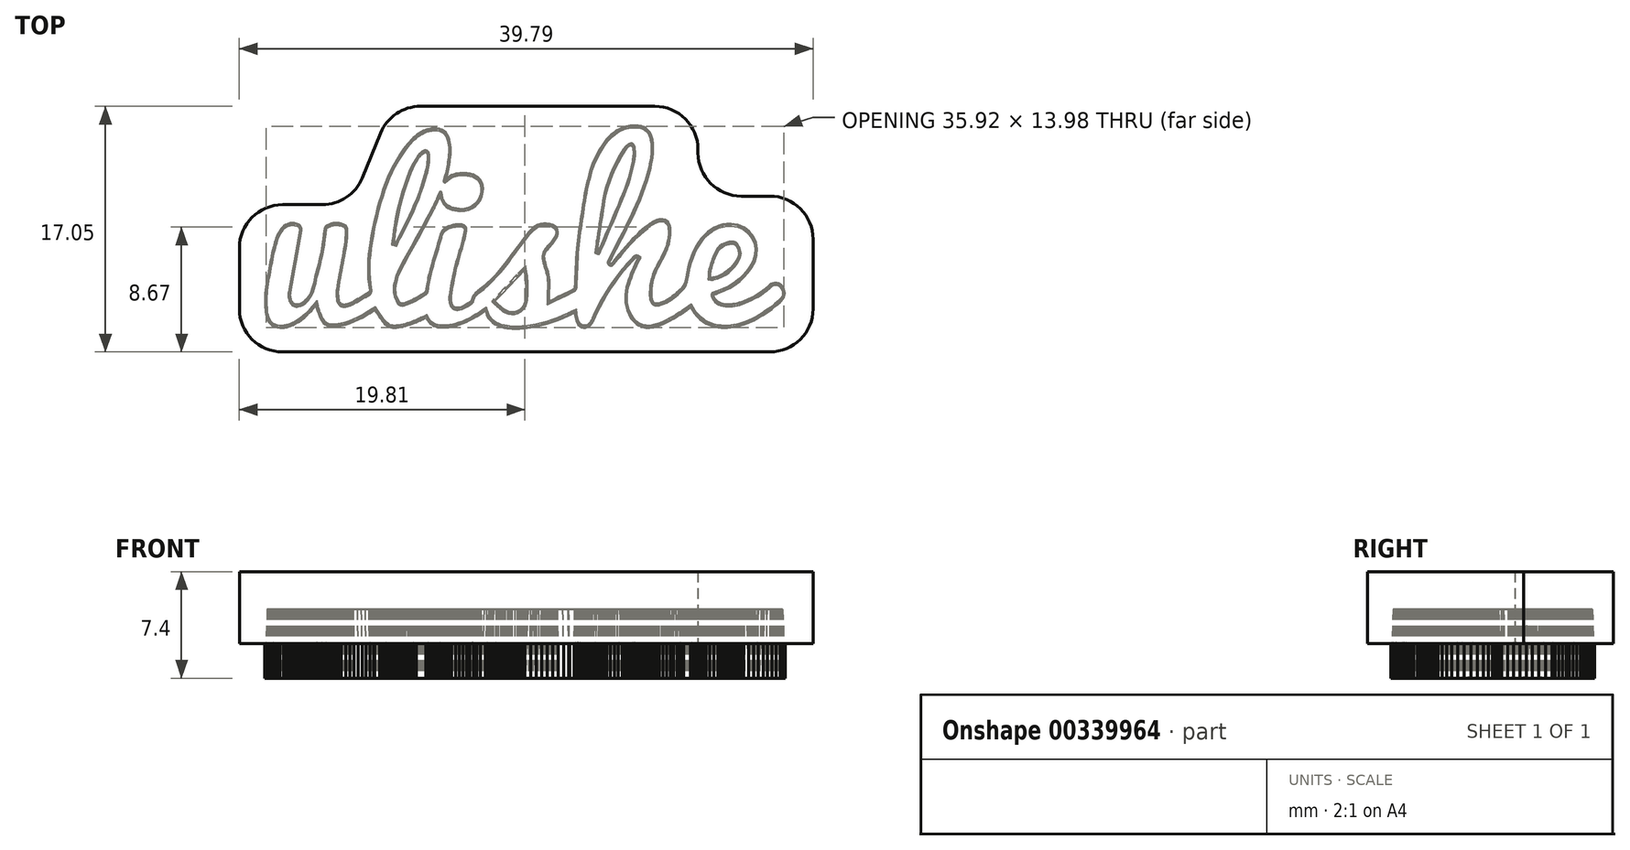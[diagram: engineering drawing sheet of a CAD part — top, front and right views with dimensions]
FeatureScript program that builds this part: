
annotation { "Feature Type Name" : "Feature", "Feature Type Description" : "" }
export const myFeature = defineFeature(function(context is Context, id is Id, definition is map)
    precondition{}
    {
        {
            var Q0;
            Q0=qCreatedBy(makeId("Top.planeOp"),FACE);
            var sketch = newSketch(context, id + "F0", { "sketchPlane" : qUnion([Q0])});
            skLineSegment(sketch, "E0", {"start": v(148.2, -33.5) * mm, "end": v(147.47, -32.9) * mm});
            skLineSegment(sketch, "E1", {"start": v(147.47, -32.9) * mm, "end": v(146.65, -32.48) * mm});
            skLineSegment(sketch, "E2", {"start": v(146.65, -32.48) * mm, "end": v(145.8, -32.22) * mm});
            skLineSegment(sketch, "E3", {"start": v(145.8, -32.22) * mm, "end": v(144.9, -32.13) * mm});
            skLineSegment(sketch, "E4", {"start": v(144.9, -32.13) * mm, "end": v(144, -32.2) * mm});
            skLineSegment(sketch, "E5", {"start": v(144, -32.2) * mm, "end": v(143.13, -32.42) * mm});
            skLineSegment(sketch, "E6", {"start": v(143.13, -32.42) * mm, "end": v(142.3, -32.82) * mm});
            skLineSegment(sketch, "E7", {"start": v(142.3, -32.82) * mm, "end": v(141.55, -33.38) * mm});
            skLineSegment(sketch, "E8", {"start": v(141.55, -33.38) * mm, "end": v(141.41, -33.5) * mm});
            skLineSegment(sketch, "E9", {"start": v(141.41, -33.5) * mm, "end": v(141.29, -33.62) * mm});
            skLineSegment(sketch, "E10", {"start": v(141.29, -33.62) * mm, "end": v(141.17, -33.73) * mm});
            skLineSegment(sketch, "E11", {"start": v(141.17, -33.73) * mm, "end": v(141.07, -33.82) * mm});
            skLineSegment(sketch, "E12", {"start": v(141.07, -33.82) * mm, "end": v(140.98, -33.9) * mm});
            skLineSegment(sketch, "E13", {"start": v(140.98, -33.9) * mm, "end": v(140.91, -33.96) * mm});
            skLineSegment(sketch, "E14", {"start": v(140.91, -33.96) * mm, "end": v(140.86, -34) * mm});
            skLineSegment(sketch, "E15", {"start": v(140.86, -34) * mm, "end": v(140.83, -34.04) * mm});
            skLineSegment(sketch, "E16", {"start": v(140.83, -34.04) * mm, "end": v(138.94, -35.65) * mm});
            skLineSegment(sketch, "E17", {"start": v(138.94, -35.65) * mm, "end": v(137.24, -37) * mm});
            skLineSegment(sketch, "E18", {"start": v(137.24, -37) * mm, "end": v(135.64, -38.16) * mm});
            skLineSegment(sketch, "E19", {"start": v(135.64, -38.16) * mm, "end": v(134.07, -39.16) * mm});
            skLineSegment(sketch, "E20", {"start": v(134.07, -39.16) * mm, "end": v(132.43, -40.06) * mm});
            skLineSegment(sketch, "E21", {"start": v(132.43, -40.06) * mm, "end": v(130.66, -40.94) * mm});
            skLineSegment(sketch, "E22", {"start": v(130.66, -40.94) * mm, "end": v(128.66, -41.83) * mm});
            skLineSegment(sketch, "E23", {"start": v(128.66, -41.83) * mm, "end": v(126.37, -42.8) * mm});
            skLineSegment(sketch, "E24", {"start": v(126.37, -42.8) * mm, "end": v(125.09, -43.3) * mm});
            skLineSegment(sketch, "E25", {"start": v(125.09, -43.3) * mm, "end": v(123.8, -43.72) * mm});
            skLineSegment(sketch, "E26", {"start": v(123.8, -43.72) * mm, "end": v(122.52, -44.05) * mm});
            skLineSegment(sketch, "E27", {"start": v(122.52, -44.05) * mm, "end": v(121.22, -44.3) * mm});
            skLineSegment(sketch, "E28", {"start": v(121.22, -44.3) * mm, "end": v(119.9, -44.5) * mm});
            skLineSegment(sketch, "E29", {"start": v(119.9, -44.5) * mm, "end": v(118.57, -44.6) * mm});
            skLineSegment(sketch, "E30", {"start": v(118.57, -44.6) * mm, "end": v(117.21, -44.64) * mm});
            skLineSegment(sketch, "E31", {"start": v(117.21, -44.64) * mm, "end": v(115.82, -44.6) * mm});
            skLineSegment(sketch, "E32", {"start": v(115.82, -44.6) * mm, "end": v(114.69, -44.46) * mm});
            skLineSegment(sketch, "E33", {"start": v(114.69, -44.46) * mm, "end": v(113.6, -44.14) * mm});
            skLineSegment(sketch, "E34", {"start": v(113.6, -44.14) * mm, "end": v(112.57, -43.66) * mm});
            skLineSegment(sketch, "E35", {"start": v(112.57, -43.66) * mm, "end": v(111.62, -43.03) * mm});
            skLineSegment(sketch, "E36", {"start": v(111.62, -43.03) * mm, "end": v(110.77, -42.27) * mm});
            skLineSegment(sketch, "E37", {"start": v(110.77, -42.27) * mm, "end": v(110.04, -41.4) * mm});
            skLineSegment(sketch, "E38", {"start": v(110.04, -41.4) * mm, "end": v(109.44, -40.41) * mm});
            skLineSegment(sketch, "E39", {"start": v(109.44, -40.41) * mm, "end": v(109, -39.34) * mm});
            skLineSegment(sketch, "E40", {"start": v(109, -39.34) * mm, "end": v(109, -39.33) * mm});
            skLineSegment(sketch, "E41", {"start": v(109, -39.33) * mm, "end": v(109, -39.31) * mm});
            skLineSegment(sketch, "E42", {"start": v(109, -39.31) * mm, "end": v(109.01, -39.3) * mm});
            skLineSegment(sketch, "E43", {"start": v(109.01, -39.3) * mm, "end": v(109.02, -39.28) * mm});
            skLineSegment(sketch, "E44", {"start": v(109.02, -39.28) * mm, "end": v(109.03, -39.27) * mm});
            skLineSegment(sketch, "E45", {"start": v(109.03, -39.27) * mm, "end": v(109.04, -39.25) * mm});
            skLineSegment(sketch, "E46", {"start": v(109.04, -39.25) * mm, "end": v(109.04, -39.24) * mm});
            skLineSegment(sketch, "E47", {"start": v(109.04, -39.24) * mm, "end": v(109.05, -39.22) * mm});
            skLineSegment(sketch, "E48", {"start": v(109.05, -39.22) * mm, "end": v(109.38, -39.11) * mm});
            skLineSegment(sketch, "E49", {"start": v(109.38, -39.11) * mm, "end": v(109.7, -39) * mm});
            skLineSegment(sketch, "E50", {"start": v(109.7, -39) * mm, "end": v(110.03, -38.9) * mm});
            skLineSegment(sketch, "E51", {"start": v(110.03, -38.9) * mm, "end": v(110.36, -38.8) * mm});
            skLineSegment(sketch, "E52", {"start": v(110.36, -38.8) * mm, "end": v(110.69, -38.7) * mm});
            skLineSegment(sketch, "E53", {"start": v(110.69, -38.7) * mm, "end": v(111.01, -38.58) * mm});
            skLineSegment(sketch, "E54", {"start": v(111.01, -38.58) * mm, "end": v(111.34, -38.47) * mm});
            skLineSegment(sketch, "E55", {"start": v(111.34, -38.47) * mm, "end": v(111.67, -38.36) * mm});
            skLineSegment(sketch, "E56", {"start": v(111.67, -38.36) * mm, "end": v(115.1, -37) * mm});
            skLineSegment(sketch, "E57", {"start": v(115.1, -37) * mm, "end": v(118.32, -35.42) * mm});
            skLineSegment(sketch, "E58", {"start": v(118.32, -35.42) * mm, "end": v(121.34, -33.6) * mm});
            skLineSegment(sketch, "E59", {"start": v(121.34, -33.6) * mm, "end": v(124.14, -31.51) * mm});
            skLineSegment(sketch, "E60", {"start": v(124.14, -31.51) * mm, "end": v(126.7, -29.16) * mm});
            skLineSegment(sketch, "E61", {"start": v(126.7, -29.16) * mm, "end": v(129.02, -26.51) * mm});
            skLineSegment(sketch, "E62", {"start": v(129.02, -26.51) * mm, "end": v(131.08, -23.57) * mm});
            skLineSegment(sketch, "E63", {"start": v(131.08, -23.57) * mm, "end": v(132.87, -20.3) * mm});
            skLineSegment(sketch, "E64", {"start": v(132.87, -20.3) * mm, "end": v(134.14, -16.46) * mm});
            skLineSegment(sketch, "E65", {"start": v(134.14, -16.46) * mm, "end": v(134.38, -12.6) * mm});
            skLineSegment(sketch, "E66", {"start": v(134.38, -12.6) * mm, "end": v(133.67, -8.87) * mm});
            skLineSegment(sketch, "E67", {"start": v(133.67, -8.87) * mm, "end": v(132.11, -5.45) * mm});
            skLineSegment(sketch, "E68", {"start": v(132.11, -5.45) * mm, "end": v(129.8, -2.48) * mm});
            skLineSegment(sketch, "E69", {"start": v(129.8, -2.48) * mm, "end": v(126.84, -0.14) * mm});
            skLineSegment(sketch, "E70", {"start": v(126.84, -0.14) * mm, "end": v(123.32, 1.42) * mm});
            skLineSegment(sketch, "E71", {"start": v(123.32, 1.42) * mm, "end": v(119.32, 2.03) * mm});
            skLineSegment(sketch, "E72", {"start": v(119.32, 2.03) * mm, "end": v(116.62, 1.93) * mm});
            skLineSegment(sketch, "E73", {"start": v(116.62, 1.93) * mm, "end": v(114.08, 1.53) * mm});
            skLineSegment(sketch, "E74", {"start": v(114.08, 1.53) * mm, "end": v(111.68, 0.84) * mm});
            skLineSegment(sketch, "E75", {"start": v(111.68, 0.84) * mm, "end": v(109.43, -0.14) * mm});
            skLineSegment(sketch, "E76", {"start": v(109.43, -0.14) * mm, "end": v(107.33, -1.39) * mm});
            skLineSegment(sketch, "E77", {"start": v(107.33, -1.39) * mm, "end": v(105.35, -2.9) * mm});
            skLineSegment(sketch, "E78", {"start": v(105.35, -2.9) * mm, "end": v(103.51, -4.65) * mm});
            skLineSegment(sketch, "E79", {"start": v(103.51, -4.65) * mm, "end": v(101.8, -6.64) * mm});
            skLineSegment(sketch, "E80", {"start": v(101.8, -6.64) * mm, "end": v(99.98, -9.17) * mm});
            skLineSegment(sketch, "E81", {"start": v(99.98, -9.17) * mm, "end": v(98.42, -11.8) * mm});
            skLineSegment(sketch, "E82", {"start": v(98.42, -11.8) * mm, "end": v(97.07, -14.53) * mm});
            skLineSegment(sketch, "E83", {"start": v(97.07, -14.53) * mm, "end": v(95.93, -17.34) * mm});
            skLineSegment(sketch, "E84", {"start": v(95.93, -17.34) * mm, "end": v(94.98, -20.22) * mm});
            skLineSegment(sketch, "E85", {"start": v(94.98, -20.22) * mm, "end": v(94.18, -23.16) * mm});
            skLineSegment(sketch, "E86", {"start": v(94.18, -23.16) * mm, "end": v(93.52, -26.14) * mm});
            skLineSegment(sketch, "E87", {"start": v(93.52, -26.14) * mm, "end": v(92.98, -29.16) * mm});
            skLineSegment(sketch, "E88", {"start": v(92.98, -29.16) * mm, "end": v(92.8, -30.2) * mm});
            skLineSegment(sketch, "E89", {"start": v(92.8, -30.2) * mm, "end": v(92.57, -31.2) * mm});
            skLineSegment(sketch, "E90", {"start": v(92.57, -31.2) * mm, "end": v(92.3, -32.14) * mm});
            skLineSegment(sketch, "E91", {"start": v(92.3, -32.14) * mm, "end": v(91.95, -33.04) * mm});
            skLineSegment(sketch, "E92", {"start": v(91.95, -33.04) * mm, "end": v(91.52, -33.88) * mm});
            skLineSegment(sketch, "E93", {"start": v(91.52, -33.88) * mm, "end": v(90.98, -34.66) * mm});
            skLineSegment(sketch, "E94", {"start": v(90.98, -34.66) * mm, "end": v(90.33, -35.4) * mm});
            skLineSegment(sketch, "E95", {"start": v(90.33, -35.4) * mm, "end": v(89.53, -36.07) * mm});
            skLineSegment(sketch, "E96", {"start": v(89.53, -36.07) * mm, "end": v(89.42, -36.17) * mm});
            skLineSegment(sketch, "E97", {"start": v(89.42, -36.17) * mm, "end": v(89.3, -36.27) * mm});
            skLineSegment(sketch, "E98", {"start": v(89.3, -36.27) * mm, "end": v(89.2, -36.37) * mm});
            skLineSegment(sketch, "E99", {"start": v(89.2, -36.37) * mm, "end": v(89.1, -36.48) * mm});
            skLineSegment(sketch, "E100", {"start": v(89.1, -36.48) * mm, "end": v(89, -36.59) * mm});
            skLineSegment(sketch, "E101", {"start": v(89, -36.59) * mm, "end": v(88.89, -36.7) * mm});
            skLineSegment(sketch, "E102", {"start": v(88.89, -36.7) * mm, "end": v(88.78, -36.8) * mm});
            skLineSegment(sketch, "E103", {"start": v(88.78, -36.8) * mm, "end": v(88.68, -36.91) * mm});
            skLineSegment(sketch, "E104", {"start": v(88.68, -36.91) * mm, "end": v(87.54, -37.97) * mm});
            skLineSegment(sketch, "E105", {"start": v(87.54, -37.97) * mm, "end": v(86.38, -39) * mm});
            skLineSegment(sketch, "E106", {"start": v(86.38, -39) * mm, "end": v(85.19, -39.96) * mm});
            skLineSegment(sketch, "E107", {"start": v(85.19, -39.96) * mm, "end": v(83.96, -40.88) * mm});
            skLineSegment(sketch, "E108", {"start": v(83.96, -40.88) * mm, "end": v(82.68, -41.72) * mm});
            skLineSegment(sketch, "E109", {"start": v(82.68, -41.72) * mm, "end": v(81.34, -42.48) * mm});
            skLineSegment(sketch, "E110", {"start": v(81.34, -42.48) * mm, "end": v(79.95, -43.15) * mm});
            skLineSegment(sketch, "E111", {"start": v(79.95, -43.15) * mm, "end": v(78.49, -43.7) * mm});
            skLineSegment(sketch, "E112", {"start": v(78.49, -43.7) * mm, "end": v(77.35, -44.02) * mm});
            skLineSegment(sketch, "E113", {"start": v(77.35, -44.02) * mm, "end": v(76.37, -44.13) * mm});
            skLineSegment(sketch, "E114", {"start": v(76.37, -44.13) * mm, "end": v(75.54, -44.03) * mm});
            skLineSegment(sketch, "E115", {"start": v(75.54, -44.03) * mm, "end": v(74.85, -43.72) * mm});
            skLineSegment(sketch, "E116", {"start": v(74.85, -43.72) * mm, "end": v(74.3, -43.2) * mm});
            skLineSegment(sketch, "E117", {"start": v(74.3, -43.2) * mm, "end": v(73.89, -42.47) * mm});
            skLineSegment(sketch, "E118", {"start": v(73.89, -42.47) * mm, "end": v(73.6, -41.52) * mm});
            skLineSegment(sketch, "E119", {"start": v(73.6, -41.52) * mm, "end": v(73.42, -40.34) * mm});
            skLineSegment(sketch, "E120", {"start": v(73.42, -40.34) * mm, "end": v(73.41, -40.3) * mm});
            skLineSegment(sketch, "E121", {"start": v(73.41, -40.3) * mm, "end": v(73.41, -40.25) * mm});
            skLineSegment(sketch, "E122", {"start": v(73.41, -40.25) * mm, "end": v(73.4, -40.2) * mm});
            skLineSegment(sketch, "E123", {"start": v(73.4, -40.2) * mm, "end": v(73.4, -40.16) * mm});
            skLineSegment(sketch, "E124", {"start": v(73.4, -40.16) * mm, "end": v(73.4, -40.12) * mm});
            skLineSegment(sketch, "E125", {"start": v(73.4, -40.12) * mm, "end": v(73.4, -40.07) * mm});
            skLineSegment(sketch, "E126", {"start": v(73.4, -40.07) * mm, "end": v(73.4, -40.03) * mm});
            skLineSegment(sketch, "E127", {"start": v(73.4, -40.03) * mm, "end": v(73.4, -39.98) * mm});
            skLineSegment(sketch, "E128", {"start": v(73.4, -39.98) * mm, "end": v(73.34, -37.9) * mm});
            skLineSegment(sketch, "E129", {"start": v(73.34, -37.9) * mm, "end": v(73.43, -35.85) * mm});
            skLineSegment(sketch, "E130", {"start": v(73.43, -35.85) * mm, "end": v(73.65, -33.82) * mm});
            skLineSegment(sketch, "E131", {"start": v(73.65, -33.82) * mm, "end": v(74, -31.82) * mm});
            skLineSegment(sketch, "E132", {"start": v(74, -31.82) * mm, "end": v(74.5, -29.85) * mm});
            skLineSegment(sketch, "E133", {"start": v(74.5, -29.85) * mm, "end": v(75.11, -27.9) * mm});
            skLineSegment(sketch, "E134", {"start": v(75.11, -27.9) * mm, "end": v(75.86, -26) * mm});
            skLineSegment(sketch, "E135", {"start": v(75.86, -26) * mm, "end": v(76.74, -24.11) * mm});
            skLineSegment(sketch, "E136", {"start": v(76.74, -24.11) * mm, "end": v(77.32, -22.98) * mm});
            skLineSegment(sketch, "E137", {"start": v(77.32, -22.98) * mm, "end": v(77.9, -21.85) * mm});
            skLineSegment(sketch, "E138", {"start": v(77.9, -21.85) * mm, "end": v(78.5, -20.72) * mm});
            skLineSegment(sketch, "E139", {"start": v(78.5, -20.72) * mm, "end": v(79.1, -19.6) * mm});
            skLineSegment(sketch, "E140", {"start": v(79.1, -19.6) * mm, "end": v(79.68, -18.47) * mm});
            skLineSegment(sketch, "E141", {"start": v(79.68, -18.47) * mm, "end": v(80.27, -17.34) * mm});
            skLineSegment(sketch, "E142", {"start": v(80.27, -17.34) * mm, "end": v(80.84, -16.2) * mm});
            skLineSegment(sketch, "E143", {"start": v(80.84, -16.2) * mm, "end": v(81.4, -15.06) * mm});
            skLineSegment(sketch, "E144", {"start": v(81.4, -15.06) * mm, "end": v(82.18, -13.33) * mm});
            skLineSegment(sketch, "E145", {"start": v(82.18, -13.33) * mm, "end": v(82.84, -11.58) * mm});
            skLineSegment(sketch, "E146", {"start": v(82.84, -11.58) * mm, "end": v(83.39, -9.8) * mm});
            skLineSegment(sketch, "E147", {"start": v(83.39, -9.8) * mm, "end": v(83.82, -8) * mm});
            skLineSegment(sketch, "E148", {"start": v(83.82, -8) * mm, "end": v(84.12, -6.16) * mm});
            skLineSegment(sketch, "E149", {"start": v(84.12, -6.16) * mm, "end": v(84.3, -4.31) * mm});
            skLineSegment(sketch, "E150", {"start": v(84.3, -4.31) * mm, "end": v(84.33, -2.44) * mm});
            skLineSegment(sketch, "E151", {"start": v(84.33, -2.44) * mm, "end": v(84.23, -0.53) * mm});
            skLineSegment(sketch, "E152", {"start": v(84.23, -0.53) * mm, "end": v(83.98, 0.8) * mm});
            skLineSegment(sketch, "E153", {"start": v(83.98, 0.8) * mm, "end": v(83.52, 1.97) * mm});
            skLineSegment(sketch, "E154", {"start": v(83.52, 1.97) * mm, "end": v(82.87, 2.95) * mm});
            skLineSegment(sketch, "E155", {"start": v(82.87, 2.95) * mm, "end": v(82.04, 3.72) * mm});
            skLineSegment(sketch, "E156", {"start": v(82.04, 3.72) * mm, "end": v(81.05, 4.27) * mm});
            skLineSegment(sketch, "E157", {"start": v(81.05, 4.27) * mm, "end": v(79.92, 4.6) * mm});
            skLineSegment(sketch, "E158", {"start": v(79.92, 4.6) * mm, "end": v(78.67, 4.67) * mm});
            skLineSegment(sketch, "E159", {"start": v(78.67, 4.67) * mm, "end": v(77.33, 4.5) * mm});
            skLineSegment(sketch, "E160", {"start": v(77.33, 4.5) * mm, "end": v(76.9, 4.38) * mm});
            skLineSegment(sketch, "E161", {"start": v(76.9, 4.38) * mm, "end": v(76.47, 4.26) * mm});
            skLineSegment(sketch, "E162", {"start": v(76.47, 4.26) * mm, "end": v(76.04, 4.12) * mm});
            skLineSegment(sketch, "E163", {"start": v(76.04, 4.12) * mm, "end": v(75.62, 3.96) * mm});
            skLineSegment(sketch, "E164", {"start": v(75.62, 3.96) * mm, "end": v(75.2, 3.8) * mm});
            skLineSegment(sketch, "E165", {"start": v(75.2, 3.8) * mm, "end": v(74.8, 3.6) * mm});
            skLineSegment(sketch, "E166", {"start": v(74.8, 3.6) * mm, "end": v(74.4, 3.4) * mm});
            skLineSegment(sketch, "E167", {"start": v(74.4, 3.4) * mm, "end": v(74, 3.2) * mm});
            skLineSegment(sketch, "E168", {"start": v(74, 3.2) * mm, "end": v(73.49, 2.89) * mm});
            skLineSegment(sketch, "E169", {"start": v(73.49, 2.89) * mm, "end": v(72.98, 2.57) * mm});
            skLineSegment(sketch, "E170", {"start": v(72.98, 2.57) * mm, "end": v(72.48, 2.24) * mm});
            skLineSegment(sketch, "E171", {"start": v(72.48, 2.24) * mm, "end": v(71.98, 1.9) * mm});
            skLineSegment(sketch, "E172", {"start": v(71.98, 1.9) * mm, "end": v(71.5, 1.56) * mm});
            skLineSegment(sketch, "E173", {"start": v(71.5, 1.56) * mm, "end": v(71.01, 1.2) * mm});
            skLineSegment(sketch, "E174", {"start": v(71.01, 1.2) * mm, "end": v(70.54, 0.83) * mm});
            skLineSegment(sketch, "E175", {"start": v(70.54, 0.83) * mm, "end": v(70.08, 0.45) * mm});
            skLineSegment(sketch, "E176", {"start": v(70.08, 0.45) * mm, "end": v(67.96, -1.36) * mm});
            skLineSegment(sketch, "E177", {"start": v(67.96, -1.36) * mm, "end": v(65.88, -3.23) * mm});
            skLineSegment(sketch, "E178", {"start": v(65.88, -3.23) * mm, "end": v(63.85, -5.14) * mm});
            skLineSegment(sketch, "E179", {"start": v(63.85, -5.14) * mm, "end": v(61.88, -7.1) * mm});
            skLineSegment(sketch, "E180", {"start": v(61.88, -7.1) * mm, "end": v(59.95, -9.11) * mm});
            skLineSegment(sketch, "E181", {"start": v(59.95, -9.11) * mm, "end": v(58.08, -11.18) * mm});
            skLineSegment(sketch, "E182", {"start": v(58.08, -11.18) * mm, "end": v(56.27, -13.3) * mm});
            skLineSegment(sketch, "E183", {"start": v(56.27, -13.3) * mm, "end": v(54.52, -15.47) * mm});
            skLineSegment(sketch, "E184", {"start": v(54.52, -15.47) * mm, "end": v(53.98, -16.15) * mm});
            skLineSegment(sketch, "E185", {"start": v(53.98, -16.15) * mm, "end": v(53.43, -16.82) * mm});
            skLineSegment(sketch, "E186", {"start": v(53.43, -16.82) * mm, "end": v(52.87, -17.49) * mm});
            skLineSegment(sketch, "E187", {"start": v(52.87, -17.49) * mm, "end": v(52.31, -18.16) * mm});
            skLineSegment(sketch, "E188", {"start": v(52.31, -18.16) * mm, "end": v(51.75, -18.83) * mm});
            skLineSegment(sketch, "E189", {"start": v(51.75, -18.83) * mm, "end": v(51.2, -19.5) * mm});
            skLineSegment(sketch, "E190", {"start": v(51.2, -19.5) * mm, "end": v(50.64, -20.2) * mm});
            skLineSegment(sketch, "E191", {"start": v(50.64, -20.2) * mm, "end": v(50.09, -20.89) * mm});
            skLineSegment(sketch, "E192", {"start": v(50.09, -20.89) * mm, "end": v(49.92, -21.02) * mm});
            skLineSegment(sketch, "E193", {"start": v(49.92, -21.02) * mm, "end": v(49.73, -21.07) * mm});
            skLineSegment(sketch, "E194", {"start": v(49.73, -21.07) * mm, "end": v(49.53, -21.03) * mm});
            skLineSegment(sketch, "E195", {"start": v(49.53, -21.03) * mm, "end": v(49.35, -20.94) * mm});
            skLineSegment(sketch, "E196", {"start": v(49.35, -20.94) * mm, "end": v(49.2, -20.79) * mm});
            skLineSegment(sketch, "E197", {"start": v(49.2, -20.79) * mm, "end": v(49.11, -20.6) * mm});
            skLineSegment(sketch, "E198", {"start": v(49.11, -20.6) * mm, "end": v(49.08, -20.39) * mm});
            skLineSegment(sketch, "E199", {"start": v(49.08, -20.39) * mm, "end": v(49.14, -20.16) * mm});
            skLineSegment(sketch, "E200", {"start": v(49.14, -20.16) * mm, "end": v(49.23, -19.99) * mm});
            skLineSegment(sketch, "E201", {"start": v(49.23, -19.99) * mm, "end": v(49.32, -19.82) * mm});
            skLineSegment(sketch, "E202", {"start": v(49.32, -19.82) * mm, "end": v(49.4, -19.66) * mm});
            skLineSegment(sketch, "E203", {"start": v(49.4, -19.66) * mm, "end": v(49.48, -19.5) * mm});
            skLineSegment(sketch, "E204", {"start": v(49.48, -19.5) * mm, "end": v(49.56, -19.36) * mm});
            skLineSegment(sketch, "E205", {"start": v(49.56, -19.36) * mm, "end": v(49.64, -19.21) * mm});
            skLineSegment(sketch, "E206", {"start": v(49.64, -19.21) * mm, "end": v(49.72, -19.06) * mm});
            skLineSegment(sketch, "E207", {"start": v(49.72, -19.06) * mm, "end": v(49.8, -18.92) * mm});
            skLineSegment(sketch, "E208", {"start": v(49.8, -18.92) * mm, "end": v(51.32, -15.92) * mm});
            skLineSegment(sketch, "E209", {"start": v(51.32, -15.92) * mm, "end": v(52.86, -12.92) * mm});
            skLineSegment(sketch, "E210", {"start": v(52.86, -12.92) * mm, "end": v(54.4, -9.92) * mm});
            skLineSegment(sketch, "E211", {"start": v(54.4, -9.92) * mm, "end": v(55.94, -6.92) * mm});
            skLineSegment(sketch, "E212", {"start": v(55.94, -6.92) * mm, "end": v(57.47, -3.92) * mm});
            skLineSegment(sketch, "E213", {"start": v(57.47, -3.92) * mm, "end": v(58.98, -0.91) * mm});
            skLineSegment(sketch, "E214", {"start": v(58.98, -0.91) * mm, "end": v(60.48, 2.1) * mm});
            skLineSegment(sketch, "E215", {"start": v(60.48, 2.1) * mm, "end": v(61.96, 5.13) * mm});
            skLineSegment(sketch, "E216", {"start": v(61.96, 5.13) * mm, "end": v(63.62, 8.65) * mm});
            skLineSegment(sketch, "E217", {"start": v(63.62, 8.65) * mm, "end": v(65.22, 12.2) * mm});
            skLineSegment(sketch, "E218", {"start": v(65.22, 12.2) * mm, "end": v(66.74, 15.79) * mm});
            skLineSegment(sketch, "E219", {"start": v(66.74, 15.79) * mm, "end": v(68.17, 19.4) * mm});
            skLineSegment(sketch, "E220", {"start": v(68.17, 19.4) * mm, "end": v(69.5, 23.05) * mm});
            skLineSegment(sketch, "E221", {"start": v(69.5, 23.05) * mm, "end": v(70.74, 26.74) * mm});
            skLineSegment(sketch, "E222", {"start": v(70.74, 26.74) * mm, "end": v(71.85, 30.47) * mm});
            skLineSegment(sketch, "E223", {"start": v(71.85, 30.47) * mm, "end": v(72.84, 34.25) * mm});
            skLineSegment(sketch, "E224", {"start": v(72.84, 34.25) * mm, "end": v(73.3, 36.28) * mm});
            skLineSegment(sketch, "E225", {"start": v(73.3, 36.28) * mm, "end": v(73.7, 38.3) * mm});
            skLineSegment(sketch, "E226", {"start": v(73.7, 38.3) * mm, "end": v(74, 40.35) * mm});
            skLineSegment(sketch, "E227", {"start": v(74, 40.35) * mm, "end": v(74.22, 42.39) * mm});
            skLineSegment(sketch, "E228", {"start": v(74.22, 42.39) * mm, "end": v(74.33, 44.44) * mm});
            skLineSegment(sketch, "E229", {"start": v(74.33, 44.44) * mm, "end": v(74.32, 46.5) * mm});
            skLineSegment(sketch, "E230", {"start": v(74.32, 46.5) * mm, "end": v(74.19, 48.56) * mm});
            skLineSegment(sketch, "E231", {"start": v(74.19, 48.56) * mm, "end": v(73.9, 50.64) * mm});
            skLineSegment(sketch, "E232", {"start": v(73.9, 50.64) * mm, "end": v(73.5, 52.32) * mm});
            skLineSegment(sketch, "E233", {"start": v(73.5, 52.32) * mm, "end": v(72.92, 53.82) * mm});
            skLineSegment(sketch, "E234", {"start": v(72.92, 53.82) * mm, "end": v(72.14, 55.14) * mm});
            skLineSegment(sketch, "E235", {"start": v(72.14, 55.14) * mm, "end": v(71.18, 56.27) * mm});
            skLineSegment(sketch, "E236", {"start": v(71.18, 56.27) * mm, "end": v(70.05, 57.21) * mm});
            skLineSegment(sketch, "E237", {"start": v(70.05, 57.21) * mm, "end": v(68.74, 57.95) * mm});
            skLineSegment(sketch, "E238", {"start": v(68.74, 57.95) * mm, "end": v(67.25, 58.48) * mm});
            skLineSegment(sketch, "E239", {"start": v(67.25, 58.48) * mm, "end": v(65.6, 58.79) * mm});
            skLineSegment(sketch, "E240", {"start": v(65.6, 58.79) * mm, "end": v(64.39, 58.9) * mm});
            skLineSegment(sketch, "E241", {"start": v(64.39, 58.9) * mm, "end": v(63.17, 58.93) * mm});
            skLineSegment(sketch, "E242", {"start": v(63.17, 58.93) * mm, "end": v(61.96, 58.9) * mm});
            skLineSegment(sketch, "E243", {"start": v(61.96, 58.9) * mm, "end": v(60.76, 58.8) * mm});
            skLineSegment(sketch, "E244", {"start": v(60.76, 58.8) * mm, "end": v(59.57, 58.62) * mm});
            skLineSegment(sketch, "E245", {"start": v(59.57, 58.62) * mm, "end": v(58.4, 58.36) * mm});
            skLineSegment(sketch, "E246", {"start": v(58.4, 58.36) * mm, "end": v(57.22, 58.02) * mm});
            skLineSegment(sketch, "E247", {"start": v(57.22, 58.02) * mm, "end": v(56.07, 57.59) * mm});
            skLineSegment(sketch, "E248", {"start": v(56.07, 57.59) * mm, "end": v(54.3, 56.76) * mm});
            skLineSegment(sketch, "E249", {"start": v(54.3, 56.76) * mm, "end": v(52.65, 55.8) * mm});
            skLineSegment(sketch, "E250", {"start": v(52.65, 55.8) * mm, "end": v(51.11, 54.7) * mm});
            skLineSegment(sketch, "E251", {"start": v(51.11, 54.7) * mm, "end": v(49.68, 53.49) * mm});
            skLineSegment(sketch, "E252", {"start": v(49.68, 53.49) * mm, "end": v(48.33, 52.17) * mm});
            skLineSegment(sketch, "E253", {"start": v(48.33, 52.17) * mm, "end": v(47.07, 50.77) * mm});
            skLineSegment(sketch, "E254", {"start": v(47.07, 50.77) * mm, "end": v(45.88, 49.27) * mm});
            skLineSegment(sketch, "E255", {"start": v(45.88, 49.27) * mm, "end": v(44.77, 47.7) * mm});
            skLineSegment(sketch, "E256", {"start": v(44.77, 47.7) * mm, "end": v(43.05, 45) * mm});
            skLineSegment(sketch, "E257", {"start": v(43.05, 45) * mm, "end": v(41.5, 42.22) * mm});
            skLineSegment(sketch, "E258", {"start": v(41.5, 42.22) * mm, "end": v(40.13, 39.37) * mm});
            skLineSegment(sketch, "E259", {"start": v(40.13, 39.37) * mm, "end": v(38.9, 36.45) * mm});
            skLineSegment(sketch, "E260", {"start": v(38.9, 36.45) * mm, "end": v(37.81, 33.49) * mm});
            skLineSegment(sketch, "E261", {"start": v(37.81, 33.49) * mm, "end": v(36.86, 30.47) * mm});
            skLineSegment(sketch, "E262", {"start": v(36.86, 30.47) * mm, "end": v(36.03, 27.4) * mm});
            skLineSegment(sketch, "E263", {"start": v(36.03, 27.4) * mm, "end": v(35.3, 24.3) * mm});
            skLineSegment(sketch, "E264", {"start": v(35.3, 24.3) * mm, "end": v(34.85, 22.07) * mm});
            skLineSegment(sketch, "E265", {"start": v(34.85, 22.07) * mm, "end": v(34.42, 19.84) * mm});
            skLineSegment(sketch, "E266", {"start": v(34.42, 19.84) * mm, "end": v(34.02, 17.6) * mm});
            skLineSegment(sketch, "E267", {"start": v(34.02, 17.6) * mm, "end": v(33.64, 15.35) * mm});
            skLineSegment(sketch, "E268", {"start": v(33.64, 15.35) * mm, "end": v(33.28, 13.1) * mm});
            skLineSegment(sketch, "E269", {"start": v(33.28, 13.1) * mm, "end": v(32.93, 10.85) * mm});
            skLineSegment(sketch, "E270", {"start": v(32.93, 10.85) * mm, "end": v(32.6, 8.6) * mm});
            skLineSegment(sketch, "E271", {"start": v(32.6, 8.6) * mm, "end": v(32.26, 6.35) * mm});
            skLineSegment(sketch, "E272", {"start": v(32.26, 6.35) * mm, "end": v(31.9, 4) * mm});
            skLineSegment(sketch, "E273", {"start": v(31.9, 4) * mm, "end": v(31.55, 1.67) * mm});
            skLineSegment(sketch, "E274", {"start": v(31.55, 1.67) * mm, "end": v(31.2, -0.68) * mm});
            skLineSegment(sketch, "E275", {"start": v(31.2, -0.68) * mm, "end": v(30.88, -3.02) * mm});
            skLineSegment(sketch, "E276", {"start": v(30.88, -3.02) * mm, "end": v(30.56, -5.37) * mm});
            skLineSegment(sketch, "E277", {"start": v(30.56, -5.37) * mm, "end": v(30.28, -7.72) * mm});
            skLineSegment(sketch, "E278", {"start": v(30.28, -7.72) * mm, "end": v(30.02, -10.07) * mm});
            skLineSegment(sketch, "E279", {"start": v(30.02, -10.07) * mm, "end": v(29.8, -12.42) * mm});
            skLineSegment(sketch, "E280", {"start": v(29.8, -12.42) * mm, "end": v(29.58, -15.23) * mm});
            skLineSegment(sketch, "E281", {"start": v(29.58, -15.23) * mm, "end": v(29.4, -18.04) * mm});
            skLineSegment(sketch, "E282", {"start": v(29.4, -18.04) * mm, "end": v(29.23, -20.85) * mm});
            skLineSegment(sketch, "E283", {"start": v(29.23, -20.85) * mm, "end": v(29.1, -23.67) * mm});
            skLineSegment(sketch, "E284", {"start": v(29.1, -23.67) * mm, "end": v(28.96, -26.48) * mm});
            skLineSegment(sketch, "E285", {"start": v(28.96, -26.48) * mm, "end": v(28.84, -29.3) * mm});
            skLineSegment(sketch, "E286", {"start": v(28.84, -29.3) * mm, "end": v(28.7, -32.1) * mm});
            skLineSegment(sketch, "E287", {"start": v(28.7, -32.1) * mm, "end": v(28.56, -34.92) * mm});
            skLineSegment(sketch, "E288", {"start": v(28.56, -34.92) * mm, "end": v(28.54, -35.07) * mm});
            skLineSegment(sketch, "E289", {"start": v(28.54, -35.07) * mm, "end": v(28.5, -35.23) * mm});
            skLineSegment(sketch, "E290", {"start": v(28.5, -35.23) * mm, "end": v(28.42, -35.38) * mm});
            skLineSegment(sketch, "E291", {"start": v(28.42, -35.38) * mm, "end": v(28.34, -35.54) * mm});
            skLineSegment(sketch, "E292", {"start": v(28.34, -35.54) * mm, "end": v(28.24, -35.68) * mm});
            skLineSegment(sketch, "E293", {"start": v(28.24, -35.68) * mm, "end": v(28.13, -35.81) * mm});
            skLineSegment(sketch, "E294", {"start": v(28.13, -35.81) * mm, "end": v(28.02, -35.92) * mm});
            skLineSegment(sketch, "E295", {"start": v(28.02, -35.92) * mm, "end": v(27.9, -36) * mm});
            skLineSegment(sketch, "E296", {"start": v(27.9, -36) * mm, "end": v(26.19, -36.85) * mm});
            skLineSegment(sketch, "E297", {"start": v(26.19, -36.85) * mm, "end": v(24.48, -37.7) * mm});
            skLineSegment(sketch, "E298", {"start": v(24.48, -37.7) * mm, "end": v(22.77, -38.56) * mm});
            skLineSegment(sketch, "E299", {"start": v(22.77, -38.56) * mm, "end": v(21.06, -39.4) * mm});
            skLineSegment(sketch, "E300", {"start": v(21.06, -39.4) * mm, "end": v(19.35, -40.24) * mm});
            skLineSegment(sketch, "E301", {"start": v(19.35, -40.24) * mm, "end": v(17.65, -41.08) * mm});
            skLineSegment(sketch, "E302", {"start": v(17.65, -41.08) * mm, "end": v(15.95, -41.92) * mm});
            skLineSegment(sketch, "E303", {"start": v(15.95, -41.92) * mm, "end": v(14.26, -42.75) * mm});
            skLineSegment(sketch, "E304", {"start": v(14.26, -42.75) * mm, "end": v(14.25, -42.05) * mm});
            skLineSegment(sketch, "E305", {"start": v(14.25, -42.05) * mm, "end": v(14.23, -41.34) * mm});
            skLineSegment(sketch, "E306", {"start": v(14.23, -41.34) * mm, "end": v(14.22, -40.63) * mm});
            skLineSegment(sketch, "E307", {"start": v(14.22, -40.63) * mm, "end": v(14.2, -39.91) * mm});
            skLineSegment(sketch, "E308", {"start": v(14.2, -39.91) * mm, "end": v(14.2, -39.2) * mm});
            skLineSegment(sketch, "E309", {"start": v(14.2, -39.2) * mm, "end": v(14.2, -38.49) * mm});
            skLineSegment(sketch, "E310", {"start": v(14.2, -38.49) * mm, "end": v(14.23, -37.77) * mm});
            skLineSegment(sketch, "E311", {"start": v(14.23, -37.77) * mm, "end": v(14.29, -37.06) * mm});
            skLineSegment(sketch, "E312", {"start": v(14.29, -37.06) * mm, "end": v(14.42, -35.45) * mm});
            skLineSegment(sketch, "E313", {"start": v(14.42, -35.45) * mm, "end": v(14.48, -33.84) * mm});
            skLineSegment(sketch, "E314", {"start": v(14.48, -33.84) * mm, "end": v(14.46, -32.25) * mm});
            skLineSegment(sketch, "E315", {"start": v(14.46, -32.25) * mm, "end": v(14.36, -30.66) * mm});
            skLineSegment(sketch, "E316", {"start": v(14.36, -30.66) * mm, "end": v(14.18, -29.09) * mm});
            skLineSegment(sketch, "E317", {"start": v(14.18, -29.09) * mm, "end": v(13.9, -27.52) * mm});
            skLineSegment(sketch, "E318", {"start": v(13.9, -27.52) * mm, "end": v(13.53, -25.96) * mm});
            skLineSegment(sketch, "E319", {"start": v(13.53, -25.96) * mm, "end": v(13.05, -24.4) * mm});
            skLineSegment(sketch, "E320", {"start": v(13.05, -24.4) * mm, "end": v(12.84, -23.76) * mm});
            skLineSegment(sketch, "E321", {"start": v(12.84, -23.76) * mm, "end": v(12.65, -23.12) * mm});
            skLineSegment(sketch, "E322", {"start": v(12.65, -23.12) * mm, "end": v(12.47, -22.47) * mm});
            skLineSegment(sketch, "E323", {"start": v(12.47, -22.47) * mm, "end": v(12.3, -21.82) * mm});
            skLineSegment(sketch, "E324", {"start": v(12.3, -21.82) * mm, "end": v(12.13, -21.17) * mm});
            skLineSegment(sketch, "E325", {"start": v(12.13, -21.17) * mm, "end": v(11.96, -20.51) * mm});
            skLineSegment(sketch, "E326", {"start": v(11.96, -20.51) * mm, "end": v(11.8, -19.86) * mm});
            skLineSegment(sketch, "E327", {"start": v(11.8, -19.86) * mm, "end": v(11.63, -19.2) * mm});
            skLineSegment(sketch, "E328", {"start": v(11.63, -19.2) * mm, "end": v(11.43, -18.3) * mm});
            skLineSegment(sketch, "E329", {"start": v(11.43, -18.3) * mm, "end": v(11.34, -17.44) * mm});
            skLineSegment(sketch, "E330", {"start": v(11.34, -17.44) * mm, "end": v(11.36, -16.61) * mm});
            skLineSegment(sketch, "E331", {"start": v(11.36, -16.61) * mm, "end": v(11.5, -15.8) * mm});
            skLineSegment(sketch, "E332", {"start": v(11.5, -15.8) * mm, "end": v(11.76, -15.03) * mm});
            skLineSegment(sketch, "E333", {"start": v(11.76, -15.03) * mm, "end": v(12.14, -14.27) * mm});
            skLineSegment(sketch, "E334", {"start": v(12.14, -14.27) * mm, "end": v(12.65, -13.53) * mm});
            skLineSegment(sketch, "E335", {"start": v(12.65, -13.53) * mm, "end": v(13.3, -12.8) * mm});
            skLineSegment(sketch, "E336", {"start": v(13.3, -12.8) * mm, "end": v(14, -12.07) * mm});
            skLineSegment(sketch, "E337", {"start": v(14, -12.07) * mm, "end": v(14.68, -11.31) * mm});
            skLineSegment(sketch, "E338", {"start": v(14.68, -11.31) * mm, "end": v(15.34, -10.53) * mm});
            skLineSegment(sketch, "E339", {"start": v(15.34, -10.53) * mm, "end": v(15.97, -9.73) * mm});
            skLineSegment(sketch, "E340", {"start": v(15.97, -9.73) * mm, "end": v(16.59, -8.91) * mm});
            skLineSegment(sketch, "E341", {"start": v(16.59, -8.91) * mm, "end": v(17.17, -8.08) * mm});
            skLineSegment(sketch, "E342", {"start": v(17.17, -8.08) * mm, "end": v(17.74, -7.23) * mm});
            skLineSegment(sketch, "E343", {"start": v(17.74, -7.23) * mm, "end": v(18.29, -6.38) * mm});
            skLineSegment(sketch, "E344", {"start": v(18.29, -6.38) * mm, "end": v(18.85, -5.2) * mm});
            skLineSegment(sketch, "E345", {"start": v(18.85, -5.2) * mm, "end": v(19.16, -3.95) * mm});
            skLineSegment(sketch, "E346", {"start": v(19.16, -3.95) * mm, "end": v(19.2, -2.67) * mm});
            skLineSegment(sketch, "E347", {"start": v(19.2, -2.67) * mm, "end": v(18.92, -1.43) * mm});
            skLineSegment(sketch, "E348", {"start": v(18.92, -1.43) * mm, "end": v(18.32, -0.27) * mm});
            skLineSegment(sketch, "E349", {"start": v(18.32, -0.27) * mm, "end": v(17.38, 0.72) * mm});
            skLineSegment(sketch, "E350", {"start": v(17.38, 0.72) * mm, "end": v(16.06, 1.5) * mm});
            skLineSegment(sketch, "E351", {"start": v(16.06, 1.5) * mm, "end": v(14.34, 2) * mm});
            skLineSegment(sketch, "E352", {"start": v(14.34, 2) * mm, "end": v(12.46, 2.22) * mm});
            skLineSegment(sketch, "E353", {"start": v(12.46, 2.22) * mm, "end": v(10.68, 2.2) * mm});
            skLineSegment(sketch, "E354", {"start": v(10.68, 2.2) * mm, "end": v(9, 1.93) * mm});
            skLineSegment(sketch, "E355", {"start": v(9, 1.93) * mm, "end": v(7.44, 1.42) * mm});
            skLineSegment(sketch, "E356", {"start": v(7.44, 1.42) * mm, "end": v(5.96, 0.67) * mm});
            skLineSegment(sketch, "E357", {"start": v(5.96, 0.67) * mm, "end": v(4.57, -0.3) * mm});
            skLineSegment(sketch, "E358", {"start": v(4.57, -0.3) * mm, "end": v(3.28, -1.5) * mm});
            skLineSegment(sketch, "E359", {"start": v(3.28, -1.5) * mm, "end": v(2.07, -2.93) * mm});
            skLineSegment(sketch, "E360", {"start": v(2.07, -2.93) * mm, "end": v(0.74, -4.67) * mm});
            skLineSegment(sketch, "E361", {"start": v(0.74, -4.67) * mm, "end": v(-0.6, -6.4) * mm});
            skLineSegment(sketch, "E362", {"start": v(-0.6, -6.4) * mm, "end": v(-1.93, -8.14) * mm});
            skLineSegment(sketch, "E363", {"start": v(-1.93, -8.14) * mm, "end": v(-3.26, -9.87) * mm});
            skLineSegment(sketch, "E364", {"start": v(-3.26, -9.87) * mm, "end": v(-4.59, -11.61) * mm});
            skLineSegment(sketch, "E365", {"start": v(-4.59, -11.61) * mm, "end": v(-5.9, -13.36) * mm});
            skLineSegment(sketch, "E366", {"start": v(-5.9, -13.36) * mm, "end": v(-7.21, -15.12) * mm});
            skLineSegment(sketch, "E367", {"start": v(-7.21, -15.12) * mm, "end": v(-8.5, -16.88) * mm});
            skLineSegment(sketch, "E368", {"start": v(-8.5, -16.88) * mm, "end": v(-10.56, -19.68) * mm});
            skLineSegment(sketch, "E369", {"start": v(-10.56, -19.68) * mm, "end": v(-12.69, -22.42) * mm});
            skLineSegment(sketch, "E370", {"start": v(-12.69, -22.42) * mm, "end": v(-14.89, -25.08) * mm});
            skLineSegment(sketch, "E371", {"start": v(-14.89, -25.08) * mm, "end": v(-17.17, -27.67) * mm});
            skLineSegment(sketch, "E372", {"start": v(-17.17, -27.67) * mm, "end": v(-19.55, -30.17) * mm});
            skLineSegment(sketch, "E373", {"start": v(-19.55, -30.17) * mm, "end": v(-22.03, -32.57) * mm});
            skLineSegment(sketch, "E374", {"start": v(-22.03, -32.57) * mm, "end": v(-24.62, -34.86) * mm});
            skLineSegment(sketch, "E375", {"start": v(-24.62, -34.86) * mm, "end": v(-27.35, -37.04) * mm});
            skLineSegment(sketch, "E376", {"start": v(-27.35, -37.04) * mm, "end": v(-28, -37.56) * mm});
            skLineSegment(sketch, "E377", {"start": v(-28, -37.56) * mm, "end": v(-28.62, -38.13) * mm});
            skLineSegment(sketch, "E378", {"start": v(-28.62, -38.13) * mm, "end": v(-29.2, -38.73) * mm});
            skLineSegment(sketch, "E379", {"start": v(-29.2, -38.73) * mm, "end": v(-29.7, -39.38) * mm});
            skLineSegment(sketch, "E380", {"start": v(-29.7, -39.38) * mm, "end": v(-30.15, -40.07) * mm});
            skLineSegment(sketch, "E381", {"start": v(-30.15, -40.07) * mm, "end": v(-30.52, -40.82) * mm});
            skLineSegment(sketch, "E382", {"start": v(-30.52, -40.82) * mm, "end": v(-30.81, -41.61) * mm});
            skLineSegment(sketch, "E383", {"start": v(-30.81, -41.61) * mm, "end": v(-31, -42.47) * mm});
            skLineSegment(sketch, "E384", {"start": v(-31, -42.47) * mm, "end": v(-31.02, -42.54) * mm});
            skLineSegment(sketch, "E385", {"start": v(-31.02, -42.54) * mm, "end": v(-31.05, -42.6) * mm});
            skLineSegment(sketch, "E386", {"start": v(-31.05, -42.6) * mm, "end": v(-31.08, -42.68) * mm});
            skLineSegment(sketch, "E387", {"start": v(-31.08, -42.68) * mm, "end": v(-31.12, -42.75) * mm});
            skLineSegment(sketch, "E388", {"start": v(-31.12, -42.75) * mm, "end": v(-31.16, -42.81) * mm});
            skLineSegment(sketch, "E389", {"start": v(-31.16, -42.81) * mm, "end": v(-31.21, -42.87) * mm});
            skLineSegment(sketch, "E390", {"start": v(-31.21, -42.87) * mm, "end": v(-31.26, -42.92) * mm});
            skLineSegment(sketch, "E391", {"start": v(-31.26, -42.92) * mm, "end": v(-31.32, -42.97) * mm});
            skLineSegment(sketch, "E392", {"start": v(-31.32, -42.97) * mm, "end": v(-32.2, -43.57) * mm});
            skLineSegment(sketch, "E393", {"start": v(-32.2, -43.57) * mm, "end": v(-33.08, -44.16) * mm});
            skLineSegment(sketch, "E394", {"start": v(-33.08, -44.16) * mm, "end": v(-33.98, -44.73) * mm});
            skLineSegment(sketch, "E395", {"start": v(-33.98, -44.73) * mm, "end": v(-34.9, -45.26) * mm});
            skLineSegment(sketch, "E396", {"start": v(-34.9, -45.26) * mm, "end": v(-35.84, -45.73) * mm});
            skLineSegment(sketch, "E397", {"start": v(-35.84, -45.73) * mm, "end": v(-36.82, -46.11) * mm});
            skLineSegment(sketch, "E398", {"start": v(-36.82, -46.11) * mm, "end": v(-37.85, -46.4) * mm});
            skLineSegment(sketch, "E399", {"start": v(-37.85, -46.4) * mm, "end": v(-38.93, -46.58) * mm});
            skLineSegment(sketch, "E400", {"start": v(-38.93, -46.58) * mm, "end": v(-39.5, -46.57) * mm});
            skLineSegment(sketch, "E401", {"start": v(-39.5, -46.57) * mm, "end": v(-40.06, -46.46) * mm});
            skLineSegment(sketch, "E402", {"start": v(-40.06, -46.46) * mm, "end": v(-40.57, -46.25) * mm});
            skLineSegment(sketch, "E403", {"start": v(-40.57, -46.25) * mm, "end": v(-41.03, -45.95) * mm});
            skLineSegment(sketch, "E404", {"start": v(-41.03, -45.95) * mm, "end": v(-41.44, -45.57) * mm});
            skLineSegment(sketch, "E405", {"start": v(-41.44, -45.57) * mm, "end": v(-41.77, -45.12) * mm});
            skLineSegment(sketch, "E406", {"start": v(-41.77, -45.12) * mm, "end": v(-42.02, -44.61) * mm});
            skLineSegment(sketch, "E407", {"start": v(-42.02, -44.61) * mm, "end": v(-42.18, -44.06) * mm});
            skLineSegment(sketch, "E408", {"start": v(-42.18, -44.06) * mm, "end": v(-42.28, -43.54) * mm});
            skLineSegment(sketch, "E409", {"start": v(-42.28, -43.54) * mm, "end": v(-42.37, -43.03) * mm});
            skLineSegment(sketch, "E410", {"start": v(-42.37, -43.03) * mm, "end": v(-42.45, -42.5) * mm});
            skLineSegment(sketch, "E411", {"start": v(-42.45, -42.5) * mm, "end": v(-42.5, -41.98) * mm});
            skLineSegment(sketch, "E412", {"start": v(-42.5, -41.98) * mm, "end": v(-42.54, -41.46) * mm});
            skLineSegment(sketch, "E413", {"start": v(-42.54, -41.46) * mm, "end": v(-42.55, -40.95) * mm});
            skLineSegment(sketch, "E414", {"start": v(-42.55, -40.95) * mm, "end": v(-42.53, -40.43) * mm});
            skLineSegment(sketch, "E415", {"start": v(-42.53, -40.43) * mm, "end": v(-42.47, -39.93) * mm});
            skLineSegment(sketch, "E416", {"start": v(-42.47, -39.93) * mm, "end": v(-42.17, -38.06) * mm});
            skLineSegment(sketch, "E417", {"start": v(-42.17, -38.06) * mm, "end": v(-41.86, -36.18) * mm});
            skLineSegment(sketch, "E418", {"start": v(-41.86, -36.18) * mm, "end": v(-41.55, -34.3) * mm});
            skLineSegment(sketch, "E419", {"start": v(-41.55, -34.3) * mm, "end": v(-41.22, -32.43) * mm});
            skLineSegment(sketch, "E420", {"start": v(-41.22, -32.43) * mm, "end": v(-40.87, -30.56) * mm});
            skLineSegment(sketch, "E421", {"start": v(-40.87, -30.56) * mm, "end": v(-40.5, -28.7) * mm});
            skLineSegment(sketch, "E422", {"start": v(-40.5, -28.7) * mm, "end": v(-40.1, -26.84) * mm});
            skLineSegment(sketch, "E423", {"start": v(-40.1, -26.84) * mm, "end": v(-39.67, -25) * mm});
            skLineSegment(sketch, "E424", {"start": v(-39.67, -25) * mm, "end": v(-39.14, -22.88) * mm});
            skLineSegment(sketch, "E425", {"start": v(-39.14, -22.88) * mm, "end": v(-38.58, -20.76) * mm});
            skLineSegment(sketch, "E426", {"start": v(-38.58, -20.76) * mm, "end": v(-38, -18.66) * mm});
            skLineSegment(sketch, "E427", {"start": v(-38, -18.66) * mm, "end": v(-37.4, -16.56) * mm});
            skLineSegment(sketch, "E428", {"start": v(-37.4, -16.56) * mm, "end": v(-36.8, -14.46) * mm});
            skLineSegment(sketch, "E429", {"start": v(-36.8, -14.46) * mm, "end": v(-36.18, -12.36) * mm});
            skLineSegment(sketch, "E430", {"start": v(-36.18, -12.36) * mm, "end": v(-35.58, -10.26) * mm});
            skLineSegment(sketch, "E431", {"start": v(-35.58, -10.26) * mm, "end": v(-35, -8.15) * mm});
            skLineSegment(sketch, "E432", {"start": v(-35, -8.15) * mm, "end": v(-34.8, -7.44) * mm});
            skLineSegment(sketch, "E433", {"start": v(-34.8, -7.44) * mm, "end": v(-34.61, -6.72) * mm});
            skLineSegment(sketch, "E434", {"start": v(-34.61, -6.72) * mm, "end": v(-34.44, -6) * mm});
            skLineSegment(sketch, "E435", {"start": v(-34.44, -6) * mm, "end": v(-34.27, -5.27) * mm});
            skLineSegment(sketch, "E436", {"start": v(-34.27, -5.27) * mm, "end": v(-34.12, -4.55) * mm});
            skLineSegment(sketch, "E437", {"start": v(-34.12, -4.55) * mm, "end": v(-33.97, -3.82) * mm});
            skLineSegment(sketch, "E438", {"start": v(-33.97, -3.82) * mm, "end": v(-33.83, -3.1) * mm});
            skLineSegment(sketch, "E439", {"start": v(-33.83, -3.1) * mm, "end": v(-33.71, -2.36) * mm});
            skLineSegment(sketch, "E440", {"start": v(-33.71, -2.36) * mm, "end": v(-33.66, -1.52) * mm});
            skLineSegment(sketch, "E441", {"start": v(-33.66, -1.52) * mm, "end": v(-33.78, -0.74) * mm});
            skLineSegment(sketch, "E442", {"start": v(-33.78, -0.74) * mm, "end": v(-34.06, -0.04) * mm});
            skLineSegment(sketch, "E443", {"start": v(-34.06, -0.04) * mm, "end": v(-34.48, 0.58) * mm});
            skLineSegment(sketch, "E444", {"start": v(-34.48, 0.58) * mm, "end": v(-35.02, 1.08) * mm});
            skLineSegment(sketch, "E445", {"start": v(-35.02, 1.08) * mm, "end": v(-35.68, 1.46) * mm});
            skLineSegment(sketch, "E446", {"start": v(-35.68, 1.46) * mm, "end": v(-36.43, 1.7) * mm});
            skLineSegment(sketch, "E447", {"start": v(-36.43, 1.7) * mm, "end": v(-37.27, 1.78) * mm});
            skLineSegment(sketch, "E448", {"start": v(-37.27, 1.78) * mm, "end": v(-38, 1.77) * mm});
            skLineSegment(sketch, "E449", {"start": v(-38, 1.77) * mm, "end": v(-38.73, 1.73) * mm});
            skLineSegment(sketch, "E450", {"start": v(-38.73, 1.73) * mm, "end": v(-39.45, 1.67) * mm});
            skLineSegment(sketch, "E451", {"start": v(-39.45, 1.67) * mm, "end": v(-40.18, 1.58) * mm});
            skLineSegment(sketch, "E452", {"start": v(-40.18, 1.58) * mm, "end": v(-40.9, 1.46) * mm});
            skLineSegment(sketch, "E453", {"start": v(-40.9, 1.46) * mm, "end": v(-41.62, 1.32) * mm});
            skLineSegment(sketch, "E454", {"start": v(-41.62, 1.32) * mm, "end": v(-42.33, 1.16) * mm});
            skLineSegment(sketch, "E455", {"start": v(-42.33, 1.16) * mm, "end": v(-43.03, 0.97) * mm});
            skLineSegment(sketch, "E456", {"start": v(-43.03, 0.97) * mm, "end": v(-44.23, 0.57) * mm});
            skLineSegment(sketch, "E457", {"start": v(-44.23, 0.57) * mm, "end": v(-45.34, 0.06) * mm});
            skLineSegment(sketch, "E458", {"start": v(-45.34, 0.06) * mm, "end": v(-46.34, -0.55) * mm});
            skLineSegment(sketch, "E459", {"start": v(-46.34, -0.55) * mm, "end": v(-47.24, -1.28) * mm});
            skLineSegment(sketch, "E460", {"start": v(-47.24, -1.28) * mm, "end": v(-48, -2.13) * mm});
            skLineSegment(sketch, "E461", {"start": v(-48, -2.13) * mm, "end": v(-48.62, -3.13) * mm});
            skLineSegment(sketch, "E462", {"start": v(-48.62, -3.13) * mm, "end": v(-49.08, -4.28) * mm});
            skLineSegment(sketch, "E463", {"start": v(-49.08, -4.28) * mm, "end": v(-49.37, -5.6) * mm});
            skLineSegment(sketch, "E464", {"start": v(-49.37, -5.6) * mm, "end": v(-49.41, -5.8) * mm});
            skLineSegment(sketch, "E465", {"start": v(-49.41, -5.8) * mm, "end": v(-49.46, -6) * mm});
            skLineSegment(sketch, "E466", {"start": v(-49.46, -6) * mm, "end": v(-49.51, -6.2) * mm});
            skLineSegment(sketch, "E467", {"start": v(-49.51, -6.2) * mm, "end": v(-49.57, -6.4) * mm});
            skLineSegment(sketch, "E468", {"start": v(-49.57, -6.4) * mm, "end": v(-49.64, -6.6) * mm});
            skLineSegment(sketch, "E469", {"start": v(-49.64, -6.6) * mm, "end": v(-49.7, -6.8) * mm});
            skLineSegment(sketch, "E470", {"start": v(-49.7, -6.8) * mm, "end": v(-49.77, -7) * mm});
            skLineSegment(sketch, "E471", {"start": v(-49.77, -7) * mm, "end": v(-49.83, -7.2) * mm});
            skLineSegment(sketch, "E472", {"start": v(-49.83, -7.2) * mm, "end": v(-50.55, -9.66) * mm});
            skLineSegment(sketch, "E473", {"start": v(-50.55, -9.66) * mm, "end": v(-51.28, -12.12) * mm});
            skLineSegment(sketch, "E474", {"start": v(-51.28, -12.12) * mm, "end": v(-52, -14.57) * mm});
            skLineSegment(sketch, "E475", {"start": v(-52, -14.57) * mm, "end": v(-52.73, -17.03) * mm});
            skLineSegment(sketch, "E476", {"start": v(-52.73, -17.03) * mm, "end": v(-53.45, -19.48) * mm});
            skLineSegment(sketch, "E477", {"start": v(-53.45, -19.48) * mm, "end": v(-54.15, -21.94) * mm});
            skLineSegment(sketch, "E478", {"start": v(-54.15, -21.94) * mm, "end": v(-54.84, -24.4) * mm});
            skLineSegment(sketch, "E479", {"start": v(-54.84, -24.4) * mm, "end": v(-55.5, -26.88) * mm});
            skLineSegment(sketch, "E480", {"start": v(-55.5, -26.88) * mm, "end": v(-55.8, -28.1) * mm});
            skLineSegment(sketch, "E481", {"start": v(-55.8, -28.1) * mm, "end": v(-56.07, -29.32) * mm});
            skLineSegment(sketch, "E482", {"start": v(-56.07, -29.32) * mm, "end": v(-56.3, -30.56) * mm});
            skLineSegment(sketch, "E483", {"start": v(-56.3, -30.56) * mm, "end": v(-56.51, -31.8) * mm});
            skLineSegment(sketch, "E484", {"start": v(-56.51, -31.8) * mm, "end": v(-56.72, -33.04) * mm});
            skLineSegment(sketch, "E485", {"start": v(-56.72, -33.04) * mm, "end": v(-56.92, -34.29) * mm});
            skLineSegment(sketch, "E486", {"start": v(-56.92, -34.29) * mm, "end": v(-57.12, -35.53) * mm});
            skLineSegment(sketch, "E487", {"start": v(-57.12, -35.53) * mm, "end": v(-57.35, -36.77) * mm});
            skLineSegment(sketch, "E488", {"start": v(-57.35, -36.77) * mm, "end": v(-57.4, -36.94) * mm});
            skLineSegment(sketch, "E489", {"start": v(-57.4, -36.94) * mm, "end": v(-57.46, -37.1) * mm});
            skLineSegment(sketch, "E490", {"start": v(-57.46, -37.1) * mm, "end": v(-57.54, -37.28) * mm});
            skLineSegment(sketch, "E491", {"start": v(-57.54, -37.28) * mm, "end": v(-57.63, -37.45) * mm});
            skLineSegment(sketch, "E492", {"start": v(-57.63, -37.45) * mm, "end": v(-57.74, -37.6) * mm});
            skLineSegment(sketch, "E493", {"start": v(-57.74, -37.6) * mm, "end": v(-57.86, -37.74) * mm});
            skLineSegment(sketch, "E494", {"start": v(-57.86, -37.74) * mm, "end": v(-57.99, -37.87) * mm});
            skLineSegment(sketch, "E495", {"start": v(-57.99, -37.87) * mm, "end": v(-58.13, -37.97) * mm});
            skLineSegment(sketch, "E496", {"start": v(-58.13, -37.97) * mm, "end": v(-58.96, -38.5) * mm});
            skLineSegment(sketch, "E497", {"start": v(-58.96, -38.5) * mm, "end": v(-59.8, -39.02) * mm});
            skLineSegment(sketch, "E498", {"start": v(-59.8, -39.02) * mm, "end": v(-60.64, -39.54) * mm});
            skLineSegment(sketch, "E499", {"start": v(-60.64, -39.54) * mm, "end": v(-61.48, -40.06) * mm});
            skLineSegment(sketch, "E500", {"start": v(-61.48, -40.06) * mm, "end": v(-62.33, -40.57) * mm});
            skLineSegment(sketch, "E501", {"start": v(-62.33, -40.57) * mm, "end": v(-63.19, -41.06) * mm});
            skLineSegment(sketch, "E502", {"start": v(-63.19, -41.06) * mm, "end": v(-64.05, -41.54) * mm});
            skLineSegment(sketch, "E503", {"start": v(-64.05, -41.54) * mm, "end": v(-64.92, -42) * mm});
            skLineSegment(sketch, "E504", {"start": v(-64.92, -42) * mm, "end": v(-65.55, -42.31) * mm});
            skLineSegment(sketch, "E505", {"start": v(-65.55, -42.31) * mm, "end": v(-66.19, -42.6) * mm});
            skLineSegment(sketch, "E506", {"start": v(-66.19, -42.6) * mm, "end": v(-66.83, -42.86) * mm});
            skLineSegment(sketch, "E507", {"start": v(-66.83, -42.86) * mm, "end": v(-67.5, -43.11) * mm});
            skLineSegment(sketch, "E508", {"start": v(-67.5, -43.11) * mm, "end": v(-68.16, -43.35) * mm});
            skLineSegment(sketch, "E509", {"start": v(-68.16, -43.35) * mm, "end": v(-68.82, -43.57) * mm});
            skLineSegment(sketch, "E510", {"start": v(-68.82, -43.57) * mm, "end": v(-69.49, -43.8) * mm});
            skLineSegment(sketch, "E511", {"start": v(-69.49, -43.8) * mm, "end": v(-70.16, -44.02) * mm});
            skLineSegment(sketch, "E512", {"start": v(-70.16, -44.02) * mm, "end": v(-70.53, -44.12) * mm});
            skLineSegment(sketch, "E513", {"start": v(-70.53, -44.12) * mm, "end": v(-70.9, -44.17) * mm});
            skLineSegment(sketch, "E514", {"start": v(-70.9, -44.17) * mm, "end": v(-71.25, -44.17) * mm});
            skLineSegment(sketch, "E515", {"start": v(-71.25, -44.17) * mm, "end": v(-71.59, -44.1) * mm});
            skLineSegment(sketch, "E516", {"start": v(-71.59, -44.1) * mm, "end": v(-71.9, -43.96) * mm});
            skLineSegment(sketch, "E517", {"start": v(-71.9, -43.96) * mm, "end": v(-72.2, -43.76) * mm});
            skLineSegment(sketch, "E518", {"start": v(-72.2, -43.76) * mm, "end": v(-72.47, -43.47) * mm});
            skLineSegment(sketch, "E519", {"start": v(-72.47, -43.47) * mm, "end": v(-72.72, -43.1) * mm});
            skLineSegment(sketch, "E520", {"start": v(-72.72, -43.1) * mm, "end": v(-73.26, -42.04) * mm});
            skLineSegment(sketch, "E521", {"start": v(-73.26, -42.04) * mm, "end": v(-73.71, -40.96) * mm});
            skLineSegment(sketch, "E522", {"start": v(-73.71, -40.96) * mm, "end": v(-74.08, -39.87) * mm});
            skLineSegment(sketch, "E523", {"start": v(-74.08, -39.87) * mm, "end": v(-74.37, -38.75) * mm});
            skLineSegment(sketch, "E524", {"start": v(-74.37, -38.75) * mm, "end": v(-74.56, -37.62) * mm});
            skLineSegment(sketch, "E525", {"start": v(-74.56, -37.62) * mm, "end": v(-74.65, -36.47) * mm});
            skLineSegment(sketch, "E526", {"start": v(-74.65, -36.47) * mm, "end": v(-74.64, -35.3) * mm});
            skLineSegment(sketch, "E527", {"start": v(-74.64, -35.3) * mm, "end": v(-74.53, -34.11) * mm});
            skLineSegment(sketch, "E528", {"start": v(-74.53, -34.11) * mm, "end": v(-74.17, -32.14) * mm});
            skLineSegment(sketch, "E529", {"start": v(-74.17, -32.14) * mm, "end": v(-73.67, -30.23) * mm});
            skLineSegment(sketch, "E530", {"start": v(-73.67, -30.23) * mm, "end": v(-73.04, -28.37) * mm});
            skLineSegment(sketch, "E531", {"start": v(-73.04, -28.37) * mm, "end": v(-72.3, -26.54) * mm});
            skLineSegment(sketch, "E532", {"start": v(-72.3, -26.54) * mm, "end": v(-71.49, -24.76) * mm});
            skLineSegment(sketch, "E533", {"start": v(-71.49, -24.76) * mm, "end": v(-70.6, -23) * mm});
            skLineSegment(sketch, "E534", {"start": v(-70.6, -23) * mm, "end": v(-69.68, -21.25) * mm});
            skLineSegment(sketch, "E535", {"start": v(-69.68, -21.25) * mm, "end": v(-68.73, -19.5) * mm});
            skLineSegment(sketch, "E536", {"start": v(-68.73, -19.5) * mm, "end": v(-66.68, -15.8) * mm});
            skLineSegment(sketch, "E537", {"start": v(-66.68, -15.8) * mm, "end": v(-64.63, -12.09) * mm});
            skLineSegment(sketch, "E538", {"start": v(-64.63, -12.09) * mm, "end": v(-62.58, -8.38) * mm});
            skLineSegment(sketch, "E539", {"start": v(-62.58, -8.38) * mm, "end": v(-60.53, -4.67) * mm});
            skLineSegment(sketch, "E540", {"start": v(-60.53, -4.67) * mm, "end": v(-58.5, -0.95) * mm});
            skLineSegment(sketch, "E541", {"start": v(-58.5, -0.95) * mm, "end": v(-56.5, 2.78) * mm});
            skLineSegment(sketch, "E542", {"start": v(-56.5, 2.78) * mm, "end": v(-54.5, 6.52) * mm});
            skLineSegment(sketch, "E543", {"start": v(-54.5, 6.52) * mm, "end": v(-52.55, 10.28) * mm});
            skLineSegment(sketch, "E544", {"start": v(-52.55, 10.28) * mm, "end": v(-52.07, 11.2) * mm});
            skLineSegment(sketch, "E545", {"start": v(-52.07, 11.2) * mm, "end": v(-51.6, 12.14) * mm});
            skLineSegment(sketch, "E546", {"start": v(-51.6, 12.14) * mm, "end": v(-51.15, 13.07) * mm});
            skLineSegment(sketch, "E547", {"start": v(-51.15, 13.07) * mm, "end": v(-50.7, 14.01) * mm});
            skLineSegment(sketch, "E548", {"start": v(-50.7, 14.01) * mm, "end": v(-50.27, 14.95) * mm});
            skLineSegment(sketch, "E549", {"start": v(-50.27, 14.95) * mm, "end": v(-49.84, 15.9) * mm});
            skLineSegment(sketch, "E550", {"start": v(-49.84, 15.9) * mm, "end": v(-49.42, 16.85) * mm});
            skLineSegment(sketch, "E551", {"start": v(-49.42, 16.85) * mm, "end": v(-49.01, 17.8) * mm});
            skLineSegment(sketch, "E552", {"start": v(-49.01, 17.8) * mm, "end": v(-48.76, 16.6) * mm});
            skLineSegment(sketch, "E553", {"start": v(-48.76, 16.6) * mm, "end": v(-48.37, 15.45) * mm});
            skLineSegment(sketch, "E554", {"start": v(-48.37, 15.45) * mm, "end": v(-47.86, 14.37) * mm});
            skLineSegment(sketch, "E555", {"start": v(-47.86, 14.37) * mm, "end": v(-47.22, 13.36) * mm});
            skLineSegment(sketch, "E556", {"start": v(-47.22, 13.36) * mm, "end": v(-46.46, 12.46) * mm});
            skLineSegment(sketch, "E557", {"start": v(-46.46, 12.46) * mm, "end": v(-45.58, 11.66) * mm});
            skLineSegment(sketch, "E558", {"start": v(-45.58, 11.66) * mm, "end": v(-44.6, 10.98) * mm});
            skLineSegment(sketch, "E559", {"start": v(-44.6, 10.98) * mm, "end": v(-43.5, 10.44) * mm});
            skLineSegment(sketch, "E560", {"start": v(-43.5, 10.44) * mm, "end": v(-42.79, 10.18) * mm});
            skLineSegment(sketch, "E561", {"start": v(-42.79, 10.18) * mm, "end": v(-42.06, 9.97) * mm});
            skLineSegment(sketch, "E562", {"start": v(-42.06, 9.97) * mm, "end": v(-41.32, 9.79) * mm});
            skLineSegment(sketch, "E563", {"start": v(-41.32, 9.79) * mm, "end": v(-40.57, 9.63) * mm});
            skLineSegment(sketch, "E564", {"start": v(-40.57, 9.63) * mm, "end": v(-39.81, 9.5) * mm});
            skLineSegment(sketch, "E565", {"start": v(-39.81, 9.5) * mm, "end": v(-39.05, 9.36) * mm});
            skLineSegment(sketch, "E566", {"start": v(-39.05, 9.36) * mm, "end": v(-38.3, 9.22) * mm});
            skLineSegment(sketch, "E567", {"start": v(-38.3, 9.22) * mm, "end": v(-37.55, 9.06) * mm});
            skLineSegment(sketch, "E568", {"start": v(-37.55, 9.06) * mm, "end": v(-34.81, 9.32) * mm});
            skLineSegment(sketch, "E569", {"start": v(-34.81, 9.32) * mm, "end": v(-32.35, 9.92) * mm});
            skLineSegment(sketch, "E570", {"start": v(-32.35, 9.92) * mm, "end": v(-30.18, 10.87) * mm});
            skLineSegment(sketch, "E571", {"start": v(-30.18, 10.87) * mm, "end": v(-28.3, 12.15) * mm});
            skLineSegment(sketch, "E572", {"start": v(-28.3, 12.15) * mm, "end": v(-26.75, 13.75) * mm});
            skLineSegment(sketch, "E573", {"start": v(-26.75, 13.75) * mm, "end": v(-25.53, 15.67) * mm});
            skLineSegment(sketch, "E574", {"start": v(-25.53, 15.67) * mm, "end": v(-24.65, 17.88) * mm});
            skLineSegment(sketch, "E575", {"start": v(-24.65, 17.88) * mm, "end": v(-24.13, 20.4) * mm});
            skLineSegment(sketch, "E576", {"start": v(-24.13, 20.4) * mm, "end": v(-24.04, 22.34) * mm});
            skLineSegment(sketch, "E577", {"start": v(-24.04, 22.34) * mm, "end": v(-24.27, 24.14) * mm});
            skLineSegment(sketch, "E578", {"start": v(-24.27, 24.14) * mm, "end": v(-24.8, 25.79) * mm});
            skLineSegment(sketch, "E579", {"start": v(-24.8, 25.79) * mm, "end": v(-25.63, 27.25) * mm});
            skLineSegment(sketch, "E580", {"start": v(-25.63, 27.25) * mm, "end": v(-26.73, 28.52) * mm});
            skLineSegment(sketch, "E581", {"start": v(-26.73, 28.52) * mm, "end": v(-28.1, 29.57) * mm});
            skLineSegment(sketch, "E582", {"start": v(-28.1, 29.57) * mm, "end": v(-29.71, 30.38) * mm});
            skLineSegment(sketch, "E583", {"start": v(-29.71, 30.38) * mm, "end": v(-31.57, 30.92) * mm});
            skLineSegment(sketch, "E584", {"start": v(-31.57, 30.92) * mm, "end": v(-32.16, 31.04) * mm});
            skLineSegment(sketch, "E585", {"start": v(-32.16, 31.04) * mm, "end": v(-32.75, 31.14) * mm});
            skLineSegment(sketch, "E586", {"start": v(-32.75, 31.14) * mm, "end": v(-33.35, 31.22) * mm});
            skLineSegment(sketch, "E587", {"start": v(-33.35, 31.22) * mm, "end": v(-33.95, 31.3) * mm});
            skLineSegment(sketch, "E588", {"start": v(-33.95, 31.3) * mm, "end": v(-34.55, 31.35) * mm});
            skLineSegment(sketch, "E589", {"start": v(-34.55, 31.35) * mm, "end": v(-35.15, 31.38) * mm});
            skLineSegment(sketch, "E590", {"start": v(-35.15, 31.38) * mm, "end": v(-35.75, 31.4) * mm});
            skLineSegment(sketch, "E591", {"start": v(-35.75, 31.4) * mm, "end": v(-36.35, 31.4) * mm});
            skLineSegment(sketch, "E592", {"start": v(-36.35, 31.4) * mm, "end": v(-37.66, 31.32) * mm});
            skLineSegment(sketch, "E593", {"start": v(-37.66, 31.32) * mm, "end": v(-38.92, 31.15) * mm});
            skLineSegment(sketch, "E594", {"start": v(-38.92, 31.15) * mm, "end": v(-40.13, 30.9) * mm});
            skLineSegment(sketch, "E595", {"start": v(-40.13, 30.9) * mm, "end": v(-41.3, 30.56) * mm});
            skLineSegment(sketch, "E596", {"start": v(-41.3, 30.56) * mm, "end": v(-42.4, 30.12) * mm});
            skLineSegment(sketch, "E597", {"start": v(-42.4, 30.12) * mm, "end": v(-43.43, 29.57) * mm});
            skLineSegment(sketch, "E598", {"start": v(-43.43, 29.57) * mm, "end": v(-44.41, 28.92) * mm});
            skLineSegment(sketch, "E599", {"start": v(-44.41, 28.92) * mm, "end": v(-45.32, 28.16) * mm});
            skLineSegment(sketch, "E600", {"start": v(-45.32, 28.16) * mm, "end": v(-44.96, 29.48) * mm});
            skLineSegment(sketch, "E601", {"start": v(-44.96, 29.48) * mm, "end": v(-44.62, 30.8) * mm});
            skLineSegment(sketch, "E602", {"start": v(-44.62, 30.8) * mm, "end": v(-44.3, 32.14) * mm});
            skLineSegment(sketch, "E603", {"start": v(-44.3, 32.14) * mm, "end": v(-44.01, 33.48) * mm});
            skLineSegment(sketch, "E604", {"start": v(-44.01, 33.48) * mm, "end": v(-43.75, 34.83) * mm});
            skLineSegment(sketch, "E605", {"start": v(-43.75, 34.83) * mm, "end": v(-43.5, 36.19) * mm});
            skLineSegment(sketch, "E606", {"start": v(-43.5, 36.19) * mm, "end": v(-43.3, 37.55) * mm});
            skLineSegment(sketch, "E607", {"start": v(-43.3, 37.55) * mm, "end": v(-43.11, 38.93) * mm});
            skLineSegment(sketch, "E608", {"start": v(-43.11, 38.93) * mm, "end": v(-42.94, 40.37) * mm});
            skLineSegment(sketch, "E609", {"start": v(-42.94, 40.37) * mm, "end": v(-42.82, 41.82) * mm});
            skLineSegment(sketch, "E610", {"start": v(-42.82, 41.82) * mm, "end": v(-42.73, 43.27) * mm});
            skLineSegment(sketch, "E611", {"start": v(-42.73, 43.27) * mm, "end": v(-42.71, 44.72) * mm});
            skLineSegment(sketch, "E612", {"start": v(-42.71, 44.72) * mm, "end": v(-42.76, 46.16) * mm});
            skLineSegment(sketch, "E613", {"start": v(-42.76, 46.16) * mm, "end": v(-42.89, 47.6) * mm});
            skLineSegment(sketch, "E614", {"start": v(-42.89, 47.6) * mm, "end": v(-43.1, 49.04) * mm});
            skLineSegment(sketch, "E615", {"start": v(-43.1, 49.04) * mm, "end": v(-43.43, 50.48) * mm});
            skLineSegment(sketch, "E616", {"start": v(-43.43, 50.48) * mm, "end": v(-43.98, 52.1) * mm});
            skLineSegment(sketch, "E617", {"start": v(-43.98, 52.1) * mm, "end": v(-44.7, 53.53) * mm});
            skLineSegment(sketch, "E618", {"start": v(-44.7, 53.53) * mm, "end": v(-45.59, 54.74) * mm});
            skLineSegment(sketch, "E619", {"start": v(-45.59, 54.74) * mm, "end": v(-46.65, 55.72) * mm});
            skLineSegment(sketch, "E620", {"start": v(-46.65, 55.72) * mm, "end": v(-47.87, 56.48) * mm});
            skLineSegment(sketch, "E621", {"start": v(-47.87, 56.48) * mm, "end": v(-49.26, 57) * mm});
            skLineSegment(sketch, "E622", {"start": v(-49.26, 57) * mm, "end": v(-50.81, 57.28) * mm});
            skLineSegment(sketch, "E623", {"start": v(-50.81, 57.28) * mm, "end": v(-52.52, 57.3) * mm});
            skLineSegment(sketch, "E624", {"start": v(-52.52, 57.3) * mm, "end": v(-53.3, 57.24) * mm});
            skLineSegment(sketch, "E625", {"start": v(-53.3, 57.24) * mm, "end": v(-54.07, 57.13) * mm});
            skLineSegment(sketch, "E626", {"start": v(-54.07, 57.13) * mm, "end": v(-54.85, 56.99) * mm});
            skLineSegment(sketch, "E627", {"start": v(-54.85, 56.99) * mm, "end": v(-55.62, 56.8) * mm});
            skLineSegment(sketch, "E628", {"start": v(-55.62, 56.8) * mm, "end": v(-56.39, 56.6) * mm});
            skLineSegment(sketch, "E629", {"start": v(-56.39, 56.6) * mm, "end": v(-57.14, 56.34) * mm});
            skLineSegment(sketch, "E630", {"start": v(-57.14, 56.34) * mm, "end": v(-57.88, 56.07) * mm});
            skLineSegment(sketch, "E631", {"start": v(-57.88, 56.07) * mm, "end": v(-58.6, 55.77) * mm});
            skLineSegment(sketch, "E632", {"start": v(-58.6, 55.77) * mm, "end": v(-59.96, 55.1) * mm});
            skLineSegment(sketch, "E633", {"start": v(-59.96, 55.1) * mm, "end": v(-61.25, 54.34) * mm});
            skLineSegment(sketch, "E634", {"start": v(-61.25, 54.34) * mm, "end": v(-62.47, 53.48) * mm});
            skLineSegment(sketch, "E635", {"start": v(-62.47, 53.48) * mm, "end": v(-63.64, 52.55) * mm});
            skLineSegment(sketch, "E636", {"start": v(-63.64, 52.55) * mm, "end": v(-64.74, 51.55) * mm});
            skLineSegment(sketch, "E637", {"start": v(-64.74, 51.55) * mm, "end": v(-65.8, 50.49) * mm});
            skLineSegment(sketch, "E638", {"start": v(-65.8, 50.49) * mm, "end": v(-66.82, 49.38) * mm});
            skLineSegment(sketch, "E639", {"start": v(-66.82, 49.38) * mm, "end": v(-67.8, 48.23) * mm});
            skLineSegment(sketch, "E640", {"start": v(-67.8, 48.23) * mm, "end": v(-70.13, 45.24) * mm});
            skLineSegment(sketch, "E641", {"start": v(-70.13, 45.24) * mm, "end": v(-72.3, 42.16) * mm});
            skLineSegment(sketch, "E642", {"start": v(-72.3, 42.16) * mm, "end": v(-74.3, 39) * mm});
            skLineSegment(sketch, "E643", {"start": v(-74.3, 39) * mm, "end": v(-76.15, 35.74) * mm});
            skLineSegment(sketch, "E644", {"start": v(-76.15, 35.74) * mm, "end": v(-77.85, 32.4) * mm});
            skLineSegment(sketch, "E645", {"start": v(-77.85, 32.4) * mm, "end": v(-79.4, 28.99) * mm});
            skLineSegment(sketch, "E646", {"start": v(-79.4, 28.99) * mm, "end": v(-80.8, 25.5) * mm});
            skLineSegment(sketch, "E647", {"start": v(-80.8, 25.5) * mm, "end": v(-82.08, 21.94) * mm});
            skLineSegment(sketch, "E648", {"start": v(-82.08, 21.94) * mm, "end": v(-83.3, 18.16) * mm});
            skLineSegment(sketch, "E649", {"start": v(-83.3, 18.16) * mm, "end": v(-84.43, 14.36) * mm});
            skLineSegment(sketch, "E650", {"start": v(-84.43, 14.36) * mm, "end": v(-85.49, 10.54) * mm});
            skLineSegment(sketch, "E651", {"start": v(-85.49, 10.54) * mm, "end": v(-86.46, 6.7) * mm});
            skLineSegment(sketch, "E652", {"start": v(-86.46, 6.7) * mm, "end": v(-87.35, 2.84) * mm});
            skLineSegment(sketch, "E653", {"start": v(-87.35, 2.84) * mm, "end": v(-88.17, -1.05) * mm});
            skLineSegment(sketch, "E654", {"start": v(-88.17, -1.05) * mm, "end": v(-88.91, -4.95) * mm});
            skLineSegment(sketch, "E655", {"start": v(-88.91, -4.95) * mm, "end": v(-89.58, -8.87) * mm});
            skLineSegment(sketch, "E656", {"start": v(-89.58, -8.87) * mm, "end": v(-90.1, -12.36) * mm});
            skLineSegment(sketch, "E657", {"start": v(-90.1, -12.36) * mm, "end": v(-90.51, -15.84) * mm});
            skLineSegment(sketch, "E658", {"start": v(-90.51, -15.84) * mm, "end": v(-90.8, -19.33) * mm});
            skLineSegment(sketch, "E659", {"start": v(-90.8, -19.33) * mm, "end": v(-90.96, -22.81) * mm});
            skLineSegment(sketch, "E660", {"start": v(-90.96, -22.81) * mm, "end": v(-90.96, -26.3) * mm});
            skLineSegment(sketch, "E661", {"start": v(-90.96, -26.3) * mm, "end": v(-90.8, -29.78) * mm});
            skLineSegment(sketch, "E662", {"start": v(-90.8, -29.78) * mm, "end": v(-90.44, -33.27) * mm});
            skLineSegment(sketch, "E663", {"start": v(-90.44, -33.27) * mm, "end": v(-89.87, -36.77) * mm});
            skLineSegment(sketch, "E664", {"start": v(-89.87, -36.77) * mm, "end": v(-89.87, -36.9) * mm});
            skLineSegment(sketch, "E665", {"start": v(-89.87, -36.9) * mm, "end": v(-89.89, -37.06) * mm});
            skLineSegment(sketch, "E666", {"start": v(-89.89, -37.06) * mm, "end": v(-89.94, -37.23) * mm});
            skLineSegment(sketch, "E667", {"start": v(-89.94, -37.23) * mm, "end": v(-90, -37.4) * mm});
            skLineSegment(sketch, "E668", {"start": v(-90, -37.4) * mm, "end": v(-90.09, -37.55) * mm});
            skLineSegment(sketch, "E669", {"start": v(-90.09, -37.55) * mm, "end": v(-90.19, -37.69) * mm});
            skLineSegment(sketch, "E670", {"start": v(-90.19, -37.69) * mm, "end": v(-90.3, -37.8) * mm});
            skLineSegment(sketch, "E671", {"start": v(-90.3, -37.8) * mm, "end": v(-90.41, -37.9) * mm});
            skLineSegment(sketch, "E672", {"start": v(-90.41, -37.9) * mm, "end": v(-91.66, -38.63) * mm});
            skLineSegment(sketch, "E673", {"start": v(-91.66, -38.63) * mm, "end": v(-92.9, -39.37) * mm});
            skLineSegment(sketch, "E674", {"start": v(-92.9, -39.37) * mm, "end": v(-94.16, -40.1) * mm});
            skLineSegment(sketch, "E675", {"start": v(-94.16, -40.1) * mm, "end": v(-95.4, -40.84) * mm});
            skLineSegment(sketch, "E676", {"start": v(-95.4, -40.84) * mm, "end": v(-96.66, -41.56) * mm});
            skLineSegment(sketch, "E677", {"start": v(-96.66, -41.56) * mm, "end": v(-97.92, -42.28) * mm});
            skLineSegment(sketch, "E678", {"start": v(-97.92, -42.28) * mm, "end": v(-99.19, -43) * mm});
            skLineSegment(sketch, "E679", {"start": v(-99.19, -43) * mm, "end": v(-100.46, -43.7) * mm});
            skLineSegment(sketch, "E680", {"start": v(-100.46, -43.7) * mm, "end": v(-100.84, -43.89) * mm});
            skLineSegment(sketch, "E681", {"start": v(-100.84, -43.89) * mm, "end": v(-101.24, -44.06) * mm});
            skLineSegment(sketch, "E682", {"start": v(-101.24, -44.06) * mm, "end": v(-101.66, -44.2) * mm});
            skLineSegment(sketch, "E683", {"start": v(-101.66, -44.2) * mm, "end": v(-102.08, -44.34) * mm});
            skLineSegment(sketch, "E684", {"start": v(-102.08, -44.34) * mm, "end": v(-102.5, -44.46) * mm});
            skLineSegment(sketch, "E685", {"start": v(-102.5, -44.46) * mm, "end": v(-102.93, -44.57) * mm});
            skLineSegment(sketch, "E686", {"start": v(-102.93, -44.57) * mm, "end": v(-103.36, -44.67) * mm});
            skLineSegment(sketch, "E687", {"start": v(-103.36, -44.67) * mm, "end": v(-103.8, -44.76) * mm});
            skLineSegment(sketch, "E688", {"start": v(-103.8, -44.76) * mm, "end": v(-104.43, -44.83) * mm});
            skLineSegment(sketch, "E689", {"start": v(-104.43, -44.83) * mm, "end": v(-105.03, -44.77) * mm});
            skLineSegment(sketch, "E690", {"start": v(-105.03, -44.77) * mm, "end": v(-105.6, -44.6) * mm});
            skLineSegment(sketch, "E691", {"start": v(-105.6, -44.6) * mm, "end": v(-106.12, -44.32) * mm});
            skLineSegment(sketch, "E692", {"start": v(-106.12, -44.32) * mm, "end": v(-106.57, -43.94) * mm});
            skLineSegment(sketch, "E693", {"start": v(-106.57, -43.94) * mm, "end": v(-106.93, -43.47) * mm});
            skLineSegment(sketch, "E694", {"start": v(-106.93, -43.47) * mm, "end": v(-107.2, -42.92) * mm});
            skLineSegment(sketch, "E695", {"start": v(-107.2, -42.92) * mm, "end": v(-107.35, -42.3) * mm});
            skLineSegment(sketch, "E696", {"start": v(-107.35, -42.3) * mm, "end": v(-107.46, -41.54) * mm});
            skLineSegment(sketch, "E697", {"start": v(-107.46, -41.54) * mm, "end": v(-107.56, -40.76) * mm});
            skLineSegment(sketch, "E698", {"start": v(-107.56, -40.76) * mm, "end": v(-107.64, -39.97) * mm});
            skLineSegment(sketch, "E699", {"start": v(-107.64, -39.97) * mm, "end": v(-107.7, -39.19) * mm});
            skLineSegment(sketch, "E700", {"start": v(-107.7, -39.19) * mm, "end": v(-107.72, -38.4) * mm});
            skLineSegment(sketch, "E701", {"start": v(-107.72, -38.4) * mm, "end": v(-107.71, -37.62) * mm});
            skLineSegment(sketch, "E702", {"start": v(-107.71, -37.62) * mm, "end": v(-107.67, -36.85) * mm});
            skLineSegment(sketch, "E703", {"start": v(-107.67, -36.85) * mm, "end": v(-107.58, -36.09) * mm});
            skLineSegment(sketch, "E704", {"start": v(-107.58, -36.09) * mm, "end": v(-107.25, -33.94) * mm});
            skLineSegment(sketch, "E705", {"start": v(-107.25, -33.94) * mm, "end": v(-106.9, -31.8) * mm});
            skLineSegment(sketch, "E706", {"start": v(-106.9, -31.8) * mm, "end": v(-106.52, -29.66) * mm});
            skLineSegment(sketch, "E707", {"start": v(-106.52, -29.66) * mm, "end": v(-106.14, -27.52) * mm});
            skLineSegment(sketch, "E708", {"start": v(-106.14, -27.52) * mm, "end": v(-105.74, -25.39) * mm});
            skLineSegment(sketch, "E709", {"start": v(-105.74, -25.39) * mm, "end": v(-105.34, -23.25) * mm});
            skLineSegment(sketch, "E710", {"start": v(-105.34, -23.25) * mm, "end": v(-104.94, -21.12) * mm});
            skLineSegment(sketch, "E711", {"start": v(-104.94, -21.12) * mm, "end": v(-104.55, -18.98) * mm});
            skLineSegment(sketch, "E712", {"start": v(-104.55, -18.98) * mm, "end": v(-104.16, -16.88) * mm});
            skLineSegment(sketch, "E713", {"start": v(-104.16, -16.88) * mm, "end": v(-103.76, -14.77) * mm});
            skLineSegment(sketch, "E714", {"start": v(-103.76, -14.77) * mm, "end": v(-103.4, -12.67) * mm});
            skLineSegment(sketch, "E715", {"start": v(-103.4, -12.67) * mm, "end": v(-103.06, -10.55) * mm});
            skLineSegment(sketch, "E716", {"start": v(-103.06, -10.55) * mm, "end": v(-102.77, -8.44) * mm});
            skLineSegment(sketch, "E717", {"start": v(-102.77, -8.44) * mm, "end": v(-102.56, -6.3) * mm});
            skLineSegment(sketch, "E718", {"start": v(-102.56, -6.3) * mm, "end": v(-102.44, -4.17) * mm});
            skLineSegment(sketch, "E719", {"start": v(-102.44, -4.17) * mm, "end": v(-102.42, -2.01) * mm});
            skLineSegment(sketch, "E720", {"start": v(-102.42, -2.01) * mm, "end": v(-102.47, -1.34) * mm});
            skLineSegment(sketch, "E721", {"start": v(-102.47, -1.34) * mm, "end": v(-102.6, -0.73) * mm});
            skLineSegment(sketch, "E722", {"start": v(-102.6, -0.73) * mm, "end": v(-102.79, -0.18) * mm});
            skLineSegment(sketch, "E723", {"start": v(-102.79, -0.18) * mm, "end": v(-103.05, 0.31) * mm});
            skLineSegment(sketch, "E724", {"start": v(-103.05, 0.31) * mm, "end": v(-103.4, 0.74) * mm});
            skLineSegment(sketch, "E725", {"start": v(-103.4, 0.74) * mm, "end": v(-103.81, 1.12) * mm});
            skLineSegment(sketch, "E726", {"start": v(-103.81, 1.12) * mm, "end": v(-104.3, 1.43) * mm});
            skLineSegment(sketch, "E727", {"start": v(-104.3, 1.43) * mm, "end": v(-104.88, 1.7) * mm});
            skLineSegment(sketch, "E728", {"start": v(-104.88, 1.7) * mm, "end": v(-106.09, 2.1) * mm});
            skLineSegment(sketch, "E729", {"start": v(-106.09, 2.1) * mm, "end": v(-107.3, 2.36) * mm});
            skLineSegment(sketch, "E730", {"start": v(-107.3, 2.36) * mm, "end": v(-108.49, 2.5) * mm});
            skLineSegment(sketch, "E731", {"start": v(-108.49, 2.5) * mm, "end": v(-109.68, 2.5) * mm});
            skLineSegment(sketch, "E732", {"start": v(-109.68, 2.5) * mm, "end": v(-110.87, 2.36) * mm});
            skLineSegment(sketch, "E733", {"start": v(-110.87, 2.36) * mm, "end": v(-112.04, 2.08) * mm});
            skLineSegment(sketch, "E734", {"start": v(-112.04, 2.08) * mm, "end": v(-113.21, 1.68) * mm});
            skLineSegment(sketch, "E735", {"start": v(-113.21, 1.68) * mm, "end": v(-114.37, 1.13) * mm});
            skLineSegment(sketch, "E736", {"start": v(-114.37, 1.13) * mm, "end": v(-114.93, 0.76) * mm});
            skLineSegment(sketch, "E737", {"start": v(-114.93, 0.76) * mm, "end": v(-115.36, 0.3) * mm});
            skLineSegment(sketch, "E738", {"start": v(-115.36, 0.3) * mm, "end": v(-115.69, -0.22) * mm});
            skLineSegment(sketch, "E739", {"start": v(-115.69, -0.22) * mm, "end": v(-115.92, -0.83) * mm});
            skLineSegment(sketch, "E740", {"start": v(-115.92, -0.83) * mm, "end": v(-116.09, -1.5) * mm});
            skLineSegment(sketch, "E741", {"start": v(-116.09, -1.5) * mm, "end": v(-116.21, -2.27) * mm});
            skLineSegment(sketch, "E742", {"start": v(-116.21, -2.27) * mm, "end": v(-116.31, -3.1) * mm});
            skLineSegment(sketch, "E743", {"start": v(-116.31, -3.1) * mm, "end": v(-116.4, -4.02) * mm});
            skLineSegment(sketch, "E744", {"start": v(-116.4, -4.02) * mm, "end": v(-116.77, -7) * mm});
            skLineSegment(sketch, "E745", {"start": v(-116.77, -7) * mm, "end": v(-117.19, -9.9) * mm});
            skLineSegment(sketch, "E746", {"start": v(-117.19, -9.9) * mm, "end": v(-117.67, -12.76) * mm});
            skLineSegment(sketch, "E747", {"start": v(-117.67, -12.76) * mm, "end": v(-118.22, -15.58) * mm});
            skLineSegment(sketch, "E748", {"start": v(-118.22, -15.58) * mm, "end": v(-118.83, -18.4) * mm});
            skLineSegment(sketch, "E749", {"start": v(-118.83, -18.4) * mm, "end": v(-119.5, -21.24) * mm});
            skLineSegment(sketch, "E750", {"start": v(-119.5, -21.24) * mm, "end": v(-120.24, -24.1) * mm});
            skLineSegment(sketch, "E751", {"start": v(-120.24, -24.1) * mm, "end": v(-121.04, -27.04) * mm});
            skLineSegment(sketch, "E752", {"start": v(-121.04, -27.04) * mm, "end": v(-121.46, -28.72) * mm});
            skLineSegment(sketch, "E753", {"start": v(-121.46, -28.72) * mm, "end": v(-121.83, -30.42) * mm});
            skLineSegment(sketch, "E754", {"start": v(-121.83, -30.42) * mm, "end": v(-122.18, -32.13) * mm});
            skLineSegment(sketch, "E755", {"start": v(-122.18, -32.13) * mm, "end": v(-122.57, -33.83) * mm});
            skLineSegment(sketch, "E756", {"start": v(-122.57, -33.83) * mm, "end": v(-123.02, -35.5) * mm});
            skLineSegment(sketch, "E757", {"start": v(-123.02, -35.5) * mm, "end": v(-123.59, -37.14) * mm});
            skLineSegment(sketch, "E758", {"start": v(-123.59, -37.14) * mm, "end": v(-124.3, -38.72) * mm});
            skLineSegment(sketch, "E759", {"start": v(-124.3, -38.72) * mm, "end": v(-125.22, -40.23) * mm});
            skLineSegment(sketch, "E760", {"start": v(-125.22, -40.23) * mm, "end": v(-125.78, -40.99) * mm});
            skLineSegment(sketch, "E761", {"start": v(-125.78, -40.99) * mm, "end": v(-126.37, -41.71) * mm});
            skLineSegment(sketch, "E762", {"start": v(-126.37, -41.71) * mm, "end": v(-127, -42.39) * mm});
            skLineSegment(sketch, "E763", {"start": v(-127, -42.39) * mm, "end": v(-127.66, -43) * mm});
            skLineSegment(sketch, "E764", {"start": v(-127.66, -43) * mm, "end": v(-128.39, -43.54) * mm});
            skLineSegment(sketch, "E765", {"start": v(-128.39, -43.54) * mm, "end": v(-129.18, -44) * mm});
            skLineSegment(sketch, "E766", {"start": v(-129.18, -44) * mm, "end": v(-130.04, -44.37) * mm});
            skLineSegment(sketch, "E767", {"start": v(-130.04, -44.37) * mm, "end": v(-130.98, -44.63) * mm});
            skLineSegment(sketch, "E768", {"start": v(-130.98, -44.63) * mm, "end": v(-131.6, -44.73) * mm});
            skLineSegment(sketch, "E769", {"start": v(-131.6, -44.73) * mm, "end": v(-132.19, -44.73) * mm});
            skLineSegment(sketch, "E770", {"start": v(-132.19, -44.73) * mm, "end": v(-132.72, -44.64) * mm});
            skLineSegment(sketch, "E771", {"start": v(-132.72, -44.64) * mm, "end": v(-133.2, -44.47) * mm});
            skLineSegment(sketch, "E772", {"start": v(-133.2, -44.47) * mm, "end": v(-133.64, -44.2) * mm});
            skLineSegment(sketch, "E773", {"start": v(-133.64, -44.2) * mm, "end": v(-134.03, -43.83) * mm});
            skLineSegment(sketch, "E774", {"start": v(-134.03, -43.83) * mm, "end": v(-134.38, -43.37) * mm});
            skLineSegment(sketch, "E775", {"start": v(-134.38, -43.37) * mm, "end": v(-134.7, -42.8) * mm});
            skLineSegment(sketch, "E776", {"start": v(-134.7, -42.8) * mm, "end": v(-134.95, -42.2) * mm});
            skLineSegment(sketch, "E777", {"start": v(-134.95, -42.2) * mm, "end": v(-135.15, -41.6) * mm});
            skLineSegment(sketch, "E778", {"start": v(-135.15, -41.6) * mm, "end": v(-135.3, -40.98) * mm});
            skLineSegment(sketch, "E779", {"start": v(-135.3, -40.98) * mm, "end": v(-135.4, -40.35) * mm});
            skLineSegment(sketch, "E780", {"start": v(-135.4, -40.35) * mm, "end": v(-135.45, -39.72) * mm});
            skLineSegment(sketch, "E781", {"start": v(-135.45, -39.72) * mm, "end": v(-135.45, -39.08) * mm});
            skLineSegment(sketch, "E782", {"start": v(-135.45, -39.08) * mm, "end": v(-135.4, -38.44) * mm});
            skLineSegment(sketch, "E783", {"start": v(-135.4, -38.44) * mm, "end": v(-135.3, -37.78) * mm});
            skLineSegment(sketch, "E784", {"start": v(-135.3, -37.78) * mm, "end": v(-134.51, -33.31) * mm});
            skLineSegment(sketch, "E785", {"start": v(-134.51, -33.31) * mm, "end": v(-133.72, -28.84) * mm});
            skLineSegment(sketch, "E786", {"start": v(-133.72, -28.84) * mm, "end": v(-132.93, -24.38) * mm});
            skLineSegment(sketch, "E787", {"start": v(-132.93, -24.38) * mm, "end": v(-132.14, -19.9) * mm});
            skLineSegment(sketch, "E788", {"start": v(-132.14, -19.9) * mm, "end": v(-131.36, -15.44) * mm});
            skLineSegment(sketch, "E789", {"start": v(-131.36, -15.44) * mm, "end": v(-130.57, -10.97) * mm});
            skLineSegment(sketch, "E790", {"start": v(-130.57, -10.97) * mm, "end": v(-129.78, -6.5) * mm});
            skLineSegment(sketch, "E791", {"start": v(-129.78, -6.5) * mm, "end": v(-129, -2.03) * mm});
            skLineSegment(sketch, "E792", {"start": v(-129, -2.03) * mm, "end": v(-128.95, -1.36) * mm});
            skLineSegment(sketch, "E793", {"start": v(-128.95, -1.36) * mm, "end": v(-129.02, -0.72) * mm});
            skLineSegment(sketch, "E794", {"start": v(-129.02, -0.72) * mm, "end": v(-129.2, -0.11) * mm});
            skLineSegment(sketch, "E795", {"start": v(-129.2, -0.11) * mm, "end": v(-129.5, 0.45) * mm});
            skLineSegment(sketch, "E796", {"start": v(-129.5, 0.45) * mm, "end": v(-129.88, 0.96) * mm});
            skLineSegment(sketch, "E797", {"start": v(-129.88, 0.96) * mm, "end": v(-130.35, 1.39) * mm});
            skLineSegment(sketch, "E798", {"start": v(-130.35, 1.39) * mm, "end": v(-130.9, 1.73) * mm});
            skLineSegment(sketch, "E799", {"start": v(-130.9, 1.73) * mm, "end": v(-131.53, 1.98) * mm});
            skLineSegment(sketch, "E800", {"start": v(-131.53, 1.98) * mm, "end": v(-133.08, 2.33) * mm});
            skLineSegment(sketch, "E801", {"start": v(-133.08, 2.33) * mm, "end": v(-134.55, 2.46) * mm});
            skLineSegment(sketch, "E802", {"start": v(-134.55, 2.46) * mm, "end": v(-135.93, 2.36) * mm});
            skLineSegment(sketch, "E803", {"start": v(-135.93, 2.36) * mm, "end": v(-137.22, 2.02) * mm});
            skLineSegment(sketch, "E804", {"start": v(-137.22, 2.02) * mm, "end": v(-138.43, 1.45) * mm});
            skLineSegment(sketch, "E805", {"start": v(-138.43, 1.45) * mm, "end": v(-139.56, 0.65) * mm});
            skLineSegment(sketch, "E806", {"start": v(-139.56, 0.65) * mm, "end": v(-140.62, -0.4) * mm});
            skLineSegment(sketch, "E807", {"start": v(-140.62, -0.4) * mm, "end": v(-141.6, -1.68) * mm});
            skLineSegment(sketch, "E808", {"start": v(-141.6, -1.68) * mm, "end": v(-142.3, -2.8) * mm});
            skLineSegment(sketch, "E809", {"start": v(-142.3, -2.8) * mm, "end": v(-142.9, -3.97) * mm});
            skLineSegment(sketch, "E810", {"start": v(-142.9, -3.97) * mm, "end": v(-143.44, -5.16) * mm});
            skLineSegment(sketch, "E811", {"start": v(-143.44, -5.16) * mm, "end": v(-143.9, -6.38) * mm});
            skLineSegment(sketch, "E812", {"start": v(-143.9, -6.38) * mm, "end": v(-144.33, -7.63) * mm});
            skLineSegment(sketch, "E813", {"start": v(-144.33, -7.63) * mm, "end": v(-144.71, -8.88) * mm});
            skLineSegment(sketch, "E814", {"start": v(-144.71, -8.88) * mm, "end": v(-145.08, -10.15) * mm});
            skLineSegment(sketch, "E815", {"start": v(-145.08, -10.15) * mm, "end": v(-145.43, -11.43) * mm});
            skLineSegment(sketch, "E816", {"start": v(-145.43, -11.43) * mm, "end": v(-145.92, -13.25) * mm});
            skLineSegment(sketch, "E817", {"start": v(-145.92, -13.25) * mm, "end": v(-146.34, -15.04) * mm});
            skLineSegment(sketch, "E818", {"start": v(-146.34, -15.04) * mm, "end": v(-146.72, -16.8) * mm});
            skLineSegment(sketch, "E819", {"start": v(-146.72, -16.8) * mm, "end": v(-147.06, -18.54) * mm});
            skLineSegment(sketch, "E820", {"start": v(-147.06, -18.54) * mm, "end": v(-147.38, -20.28) * mm});
            skLineSegment(sketch, "E821", {"start": v(-147.38, -20.28) * mm, "end": v(-147.7, -22.04) * mm});
            skLineSegment(sketch, "E822", {"start": v(-147.7, -22.04) * mm, "end": v(-148, -23.84) * mm});
            skLineSegment(sketch, "E823", {"start": v(-148, -23.84) * mm, "end": v(-148.32, -25.68) * mm});
            skLineSegment(sketch, "E824", {"start": v(-148.32, -25.68) * mm, "end": v(-148.64, -27.42) * mm});
            skLineSegment(sketch, "E825", {"start": v(-148.64, -27.42) * mm, "end": v(-148.98, -29.2) * mm});
            skLineSegment(sketch, "E826", {"start": v(-148.98, -29.2) * mm, "end": v(-149.33, -31) * mm});
            skLineSegment(sketch, "E827", {"start": v(-149.33, -31) * mm, "end": v(-149.66, -32.83) * mm});
            skLineSegment(sketch, "E828", {"start": v(-149.66, -32.83) * mm, "end": v(-149.94, -34.67) * mm});
            skLineSegment(sketch, "E829", {"start": v(-149.94, -34.67) * mm, "end": v(-150.17, -36.5) * mm});
            skLineSegment(sketch, "E830", {"start": v(-150.17, -36.5) * mm, "end": v(-150.32, -38.3) * mm});
            skLineSegment(sketch, "E831", {"start": v(-150.32, -38.3) * mm, "end": v(-150.37, -40.09) * mm});
            skLineSegment(sketch, "E832", {"start": v(-150.37, -40.09) * mm, "end": v(-150.37, -41.39) * mm});
            skLineSegment(sketch, "E833", {"start": v(-150.37, -41.39) * mm, "end": v(-150.37, -42.7) * mm});
            skLineSegment(sketch, "E834", {"start": v(-150.37, -42.7) * mm, "end": v(-150.37, -44) * mm});
            skLineSegment(sketch, "E835", {"start": v(-150.37, -44) * mm, "end": v(-150.35, -45.3) * mm});
            skLineSegment(sketch, "E836", {"start": v(-150.35, -45.3) * mm, "end": v(-150.31, -46.6) * mm});
            skLineSegment(sketch, "E837", {"start": v(-150.31, -46.6) * mm, "end": v(-150.23, -47.9) * mm});
            skLineSegment(sketch, "E838", {"start": v(-150.23, -47.9) * mm, "end": v(-150.1, -49.19) * mm});
            skLineSegment(sketch, "E839", {"start": v(-150.1, -49.19) * mm, "end": v(-149.93, -50.46) * mm});
            skLineSegment(sketch, "E840", {"start": v(-149.93, -50.46) * mm, "end": v(-149.43, -52.44) * mm});
            skLineSegment(sketch, "E841", {"start": v(-149.43, -52.44) * mm, "end": v(-148.68, -54.16) * mm});
            skLineSegment(sketch, "E842", {"start": v(-148.68, -54.16) * mm, "end": v(-147.67, -55.6) * mm});
            skLineSegment(sketch, "E843", {"start": v(-147.67, -55.6) * mm, "end": v(-146.44, -56.77) * mm});
            skLineSegment(sketch, "E844", {"start": v(-146.44, -56.77) * mm, "end": v(-145, -57.65) * mm});
            skLineSegment(sketch, "E845", {"start": v(-145, -57.65) * mm, "end": v(-143.38, -58.22) * mm});
            skLineSegment(sketch, "E846", {"start": v(-143.38, -58.22) * mm, "end": v(-141.58, -58.48) * mm});
            skLineSegment(sketch, "E847", {"start": v(-141.58, -58.48) * mm, "end": v(-139.64, -58.41) * mm});
            skLineSegment(sketch, "E848", {"start": v(-139.64, -58.41) * mm, "end": v(-138.93, -58.31) * mm});
            skLineSegment(sketch, "E849", {"start": v(-138.93, -58.31) * mm, "end": v(-138.21, -58.18) * mm});
            skLineSegment(sketch, "E850", {"start": v(-138.21, -58.18) * mm, "end": v(-137.5, -58) * mm});
            skLineSegment(sketch, "E851", {"start": v(-137.5, -58) * mm, "end": v(-136.8, -57.81) * mm});
            skLineSegment(sketch, "E852", {"start": v(-136.8, -57.81) * mm, "end": v(-136.09, -57.59) * mm});
            skLineSegment(sketch, "E853", {"start": v(-136.09, -57.59) * mm, "end": v(-135.4, -57.34) * mm});
            skLineSegment(sketch, "E854", {"start": v(-135.4, -57.34) * mm, "end": v(-134.72, -57.07) * mm});
            skLineSegment(sketch, "E855", {"start": v(-134.72, -57.07) * mm, "end": v(-134.05, -56.77) * mm});
            skLineSegment(sketch, "E856", {"start": v(-134.05, -56.77) * mm, "end": v(-132.27, -55.86) * mm});
            skLineSegment(sketch, "E857", {"start": v(-132.27, -55.86) * mm, "end": v(-130.58, -54.83) * mm});
            skLineSegment(sketch, "E858", {"start": v(-130.58, -54.83) * mm, "end": v(-128.98, -53.7) * mm});
            skLineSegment(sketch, "E859", {"start": v(-128.98, -53.7) * mm, "end": v(-127.45, -52.45) * mm});
            skLineSegment(sketch, "E860", {"start": v(-127.45, -52.45) * mm, "end": v(-126, -51.13) * mm});
            skLineSegment(sketch, "E861", {"start": v(-126, -51.13) * mm, "end": v(-124.6, -49.73) * mm});
            skLineSegment(sketch, "E862", {"start": v(-124.6, -49.73) * mm, "end": v(-123.26, -48.27) * mm});
            skLineSegment(sketch, "E863", {"start": v(-123.26, -48.27) * mm, "end": v(-121.96, -46.77) * mm});
            skLineSegment(sketch, "E864", {"start": v(-121.96, -46.77) * mm, "end": v(-121.85, -46.64) * mm});
            skLineSegment(sketch, "E865", {"start": v(-121.85, -46.64) * mm, "end": v(-121.73, -46.5) * mm});
            skLineSegment(sketch, "E866", {"start": v(-121.73, -46.5) * mm, "end": v(-121.62, -46.37) * mm});
            skLineSegment(sketch, "E867", {"start": v(-121.62, -46.37) * mm, "end": v(-121.5, -46.23) * mm});
            skLineSegment(sketch, "E868", {"start": v(-121.5, -46.23) * mm, "end": v(-121.37, -46.08) * mm});
            skLineSegment(sketch, "E869", {"start": v(-121.37, -46.08) * mm, "end": v(-121.24, -45.92) * mm});
            skLineSegment(sketch, "E870", {"start": v(-121.24, -45.92) * mm, "end": v(-121.1, -45.76) * mm});
            skLineSegment(sketch, "E871", {"start": v(-121.1, -45.76) * mm, "end": v(-120.95, -45.58) * mm});
            skLineSegment(sketch, "E872", {"start": v(-120.95, -45.58) * mm, "end": v(-120.88, -45.84) * mm});
            skLineSegment(sketch, "E873", {"start": v(-120.88, -45.84) * mm, "end": v(-120.82, -46.08) * mm});
            skLineSegment(sketch, "E874", {"start": v(-120.82, -46.08) * mm, "end": v(-120.77, -46.3) * mm});
            skLineSegment(sketch, "E875", {"start": v(-120.77, -46.3) * mm, "end": v(-120.72, -46.52) * mm});
            skLineSegment(sketch, "E876", {"start": v(-120.72, -46.52) * mm, "end": v(-120.67, -46.72) * mm});
            skLineSegment(sketch, "E877", {"start": v(-120.67, -46.72) * mm, "end": v(-120.61, -46.92) * mm});
            skLineSegment(sketch, "E878", {"start": v(-120.61, -46.92) * mm, "end": v(-120.56, -47.1) * mm});
            skLineSegment(sketch, "E879", {"start": v(-120.56, -47.1) * mm, "end": v(-120.5, -47.28) * mm});
            skLineSegment(sketch, "E880", {"start": v(-120.5, -47.28) * mm, "end": v(-120.17, -48.12) * mm});
            skLineSegment(sketch, "E881", {"start": v(-120.17, -48.12) * mm, "end": v(-119.86, -48.96) * mm});
            skLineSegment(sketch, "E882", {"start": v(-119.86, -48.96) * mm, "end": v(-119.55, -49.8) * mm});
            skLineSegment(sketch, "E883", {"start": v(-119.55, -49.8) * mm, "end": v(-119.24, -50.64) * mm});
            skLineSegment(sketch, "E884", {"start": v(-119.24, -50.64) * mm, "end": v(-118.91, -51.48) * mm});
            skLineSegment(sketch, "E885", {"start": v(-118.91, -51.48) * mm, "end": v(-118.57, -52.3) * mm});
            skLineSegment(sketch, "E886", {"start": v(-118.57, -52.3) * mm, "end": v(-118.2, -53.1) * mm});
            skLineSegment(sketch, "E887", {"start": v(-118.2, -53.1) * mm, "end": v(-117.78, -53.9) * mm});
            skLineSegment(sketch, "E888", {"start": v(-117.78, -53.9) * mm, "end": v(-117.16, -54.87) * mm});
            skLineSegment(sketch, "E889", {"start": v(-117.16, -54.87) * mm, "end": v(-116.44, -55.7) * mm});
            skLineSegment(sketch, "E890", {"start": v(-116.44, -55.7) * mm, "end": v(-115.63, -56.39) * mm});
            skLineSegment(sketch, "E891", {"start": v(-115.63, -56.39) * mm, "end": v(-114.74, -56.94) * mm});
            skLineSegment(sketch, "E892", {"start": v(-114.74, -56.94) * mm, "end": v(-113.77, -57.35) * mm});
            skLineSegment(sketch, "E893", {"start": v(-113.77, -57.35) * mm, "end": v(-112.72, -57.62) * mm});
            skLineSegment(sketch, "E894", {"start": v(-112.72, -57.62) * mm, "end": v(-111.62, -57.76) * mm});
            skLineSegment(sketch, "E895", {"start": v(-111.62, -57.76) * mm, "end": v(-110.45, -57.76) * mm});
            skLineSegment(sketch, "E896", {"start": v(-110.45, -57.76) * mm, "end": v(-109.9, -57.72) * mm});
            skLineSegment(sketch, "E897", {"start": v(-109.9, -57.72) * mm, "end": v(-109.35, -57.67) * mm});
            skLineSegment(sketch, "E898", {"start": v(-109.35, -57.67) * mm, "end": v(-108.8, -57.61) * mm});
            skLineSegment(sketch, "E899", {"start": v(-108.8, -57.61) * mm, "end": v(-108.25, -57.54) * mm});
            skLineSegment(sketch, "E900", {"start": v(-108.25, -57.54) * mm, "end": v(-107.7, -57.46) * mm});
            skLineSegment(sketch, "E901", {"start": v(-107.7, -57.46) * mm, "end": v(-107.15, -57.36) * mm});
            skLineSegment(sketch, "E902", {"start": v(-107.15, -57.36) * mm, "end": v(-106.6, -57.25) * mm});
            skLineSegment(sketch, "E903", {"start": v(-106.6, -57.25) * mm, "end": v(-106.07, -57.13) * mm});
            skLineSegment(sketch, "E904", {"start": v(-106.07, -57.13) * mm, "end": v(-103.56, -56.46) * mm});
            skLineSegment(sketch, "E905", {"start": v(-103.56, -56.46) * mm, "end": v(-101.12, -55.64) * mm});
            skLineSegment(sketch, "E906", {"start": v(-101.12, -55.64) * mm, "end": v(-98.73, -54.7) * mm});
            skLineSegment(sketch, "E907", {"start": v(-98.73, -54.7) * mm, "end": v(-96.4, -53.65) * mm});
            skLineSegment(sketch, "E908", {"start": v(-96.4, -53.65) * mm, "end": v(-94.1, -52.5) * mm});
            skLineSegment(sketch, "E909", {"start": v(-94.1, -52.5) * mm, "end": v(-91.86, -51.23) * mm});
            skLineSegment(sketch, "E910", {"start": v(-91.86, -51.23) * mm, "end": v(-89.66, -49.9) * mm});
            skLineSegment(sketch, "E911", {"start": v(-89.66, -49.9) * mm, "end": v(-87.5, -48.48) * mm});
            skLineSegment(sketch, "E912", {"start": v(-87.5, -48.48) * mm, "end": v(-87.39, -48.4) * mm});
            skLineSegment(sketch, "E913", {"start": v(-87.39, -48.4) * mm, "end": v(-87.29, -48.34) * mm});
            skLineSegment(sketch, "E914", {"start": v(-87.29, -48.34) * mm, "end": v(-87.19, -48.28) * mm});
            skLineSegment(sketch, "E915", {"start": v(-87.19, -48.28) * mm, "end": v(-87.1, -48.23) * mm});
            skLineSegment(sketch, "E916", {"start": v(-87.1, -48.23) * mm, "end": v(-87.02, -48.18) * mm});
            skLineSegment(sketch, "E917", {"start": v(-87.02, -48.18) * mm, "end": v(-86.95, -48.14) * mm});
            skLineSegment(sketch, "E918", {"start": v(-86.95, -48.14) * mm, "end": v(-86.9, -48.12) * mm});
            skLineSegment(sketch, "E919", {"start": v(-86.9, -48.12) * mm, "end": v(-86.88, -48.1) * mm});
            skLineSegment(sketch, "E920", {"start": v(-86.88, -48.1) * mm, "end": v(-86.26, -49.01) * mm});
            skLineSegment(sketch, "E921", {"start": v(-86.26, -49.01) * mm, "end": v(-85.65, -49.92) * mm});
            skLineSegment(sketch, "E922", {"start": v(-85.65, -49.92) * mm, "end": v(-85.05, -50.83) * mm});
            skLineSegment(sketch, "E923", {"start": v(-85.05, -50.83) * mm, "end": v(-84.46, -51.72) * mm});
            skLineSegment(sketch, "E924", {"start": v(-84.46, -51.72) * mm, "end": v(-83.86, -52.6) * mm});
            skLineSegment(sketch, "E925", {"start": v(-83.86, -52.6) * mm, "end": v(-83.24, -53.48) * mm});
            skLineSegment(sketch, "E926", {"start": v(-83.24, -53.48) * mm, "end": v(-82.62, -54.33) * mm});
            skLineSegment(sketch, "E927", {"start": v(-82.62, -54.33) * mm, "end": v(-81.97, -55.16) * mm});
            skLineSegment(sketch, "E928", {"start": v(-81.97, -55.16) * mm, "end": v(-81.2, -56) * mm});
            skLineSegment(sketch, "E929", {"start": v(-81.2, -56) * mm, "end": v(-80.38, -56.7) * mm});
            skLineSegment(sketch, "E930", {"start": v(-80.38, -56.7) * mm, "end": v(-79.5, -57.3) * mm});
            skLineSegment(sketch, "E931", {"start": v(-79.5, -57.3) * mm, "end": v(-78.56, -57.76) * mm});
            skLineSegment(sketch, "E932", {"start": v(-78.56, -57.76) * mm, "end": v(-77.56, -58.1) * mm});
            skLineSegment(sketch, "E933", {"start": v(-77.56, -58.1) * mm, "end": v(-76.5, -58.3) * mm});
            skLineSegment(sketch, "E934", {"start": v(-76.5, -58.3) * mm, "end": v(-75.39, -58.38) * mm});
            skLineSegment(sketch, "E935", {"start": v(-75.39, -58.38) * mm, "end": v(-74.22, -58.33) * mm});
            skLineSegment(sketch, "E936", {"start": v(-74.22, -58.33) * mm, "end": v(-72.85, -58.16) * mm});
            skLineSegment(sketch, "E937", {"start": v(-72.85, -58.16) * mm, "end": v(-71.5, -57.93) * mm});
            skLineSegment(sketch, "E938", {"start": v(-71.5, -57.93) * mm, "end": v(-70.18, -57.64) * mm});
            skLineSegment(sketch, "E939", {"start": v(-70.18, -57.64) * mm, "end": v(-68.86, -57.3) * mm});
            skLineSegment(sketch, "E940", {"start": v(-68.86, -57.3) * mm, "end": v(-67.56, -56.9) * mm});
            skLineSegment(sketch, "E941", {"start": v(-67.56, -56.9) * mm, "end": v(-66.27, -56.47) * mm});
            skLineSegment(sketch, "E942", {"start": v(-66.27, -56.47) * mm, "end": v(-65, -56) * mm});
            skLineSegment(sketch, "E943", {"start": v(-65, -56) * mm, "end": v(-63.73, -55.5) * mm});
            skLineSegment(sketch, "E944", {"start": v(-63.73, -55.5) * mm, "end": v(-62.9, -55.15) * mm});
            skLineSegment(sketch, "E945", {"start": v(-62.9, -55.15) * mm, "end": v(-62.1, -54.8) * mm});
            skLineSegment(sketch, "E946", {"start": v(-62.1, -54.8) * mm, "end": v(-61.28, -54.44) * mm});
            skLineSegment(sketch, "E947", {"start": v(-61.28, -54.44) * mm, "end": v(-60.47, -54.07) * mm});
            skLineSegment(sketch, "E948", {"start": v(-60.47, -54.07) * mm, "end": v(-59.66, -53.7) * mm});
            skLineSegment(sketch, "E949", {"start": v(-59.66, -53.7) * mm, "end": v(-58.85, -53.33) * mm});
            skLineSegment(sketch, "E950", {"start": v(-58.85, -53.33) * mm, "end": v(-58.05, -52.96) * mm});
            skLineSegment(sketch, "E951", {"start": v(-58.05, -52.96) * mm, "end": v(-57.24, -52.6) * mm});
            skLineSegment(sketch, "E952", {"start": v(-57.24, -52.6) * mm, "end": v(-56.44, -53.87) * mm});
            skLineSegment(sketch, "E953", {"start": v(-56.44, -53.87) * mm, "end": v(-55.63, -54.97) * mm});
            skLineSegment(sketch, "E954", {"start": v(-55.63, -54.97) * mm, "end": v(-54.78, -55.9) * mm});
            skLineSegment(sketch, "E955", {"start": v(-54.78, -55.9) * mm, "end": v(-53.87, -56.66) * mm});
            skLineSegment(sketch, "E956", {"start": v(-53.87, -56.66) * mm, "end": v(-52.9, -57.26) * mm});
            skLineSegment(sketch, "E957", {"start": v(-52.9, -57.26) * mm, "end": v(-51.83, -57.71) * mm});
            skLineSegment(sketch, "E958", {"start": v(-51.83, -57.71) * mm, "end": v(-50.66, -58.02) * mm});
            skLineSegment(sketch, "E959", {"start": v(-50.66, -58.02) * mm, "end": v(-49.36, -58.18) * mm});
            skLineSegment(sketch, "E960", {"start": v(-49.36, -58.18) * mm, "end": v(-48.49, -58.23) * mm});
            skLineSegment(sketch, "E961", {"start": v(-48.49, -58.23) * mm, "end": v(-47.6, -58.26) * mm});
            skLineSegment(sketch, "E962", {"start": v(-47.6, -58.26) * mm, "end": v(-46.72, -58.27) * mm});
            skLineSegment(sketch, "E963", {"start": v(-46.72, -58.27) * mm, "end": v(-45.84, -58.24) * mm});
            skLineSegment(sketch, "E964", {"start": v(-45.84, -58.24) * mm, "end": v(-44.95, -58.19) * mm});
            skLineSegment(sketch, "E965", {"start": v(-44.95, -58.19) * mm, "end": v(-44.07, -58.1) * mm});
            skLineSegment(sketch, "E966", {"start": v(-44.07, -58.1) * mm, "end": v(-43.2, -57.99) * mm});
            skLineSegment(sketch, "E967", {"start": v(-43.2, -57.99) * mm, "end": v(-42.35, -57.83) * mm});
            skLineSegment(sketch, "E968", {"start": v(-42.35, -57.83) * mm, "end": v(-40.13, -57.3) * mm});
            skLineSegment(sketch, "E969", {"start": v(-40.13, -57.3) * mm, "end": v(-37.97, -56.65) * mm});
            skLineSegment(sketch, "E970", {"start": v(-37.97, -56.65) * mm, "end": v(-35.85, -55.87) * mm});
            skLineSegment(sketch, "E971", {"start": v(-35.85, -55.87) * mm, "end": v(-33.78, -54.98) * mm});
            skLineSegment(sketch, "E972", {"start": v(-33.78, -54.98) * mm, "end": v(-31.76, -54) * mm});
            skLineSegment(sketch, "E973", {"start": v(-31.76, -54) * mm, "end": v(-29.77, -52.92) * mm});
            skLineSegment(sketch, "E974", {"start": v(-29.77, -52.92) * mm, "end": v(-27.82, -51.78) * mm});
            skLineSegment(sketch, "E975", {"start": v(-27.82, -51.78) * mm, "end": v(-25.89, -50.57) * mm});
            skLineSegment(sketch, "E976", {"start": v(-25.89, -50.57) * mm, "end": v(-25.53, -50.34) * mm});
            skLineSegment(sketch, "E977", {"start": v(-25.53, -50.34) * mm, "end": v(-25.17, -50.1) * mm});
            skLineSegment(sketch, "E978", {"start": v(-25.17, -50.1) * mm, "end": v(-24.81, -49.86) * mm});
            skLineSegment(sketch, "E979", {"start": v(-24.81, -49.86) * mm, "end": v(-24.45, -49.61) * mm});
            skLineSegment(sketch, "E980", {"start": v(-24.45, -49.61) * mm, "end": v(-24.1, -49.36) * mm});
            skLineSegment(sketch, "E981", {"start": v(-24.1, -49.36) * mm, "end": v(-23.72, -49.11) * mm});
            skLineSegment(sketch, "E982", {"start": v(-23.72, -49.11) * mm, "end": v(-23.35, -48.86) * mm});
            skLineSegment(sketch, "E983", {"start": v(-23.35, -48.86) * mm, "end": v(-22.97, -48.6) * mm});
            skLineSegment(sketch, "E984", {"start": v(-22.97, -48.6) * mm, "end": v(-22.32, -50.68) * mm});
            skLineSegment(sketch, "E985", {"start": v(-22.32, -50.68) * mm, "end": v(-21.43, -52.47) * mm});
            skLineSegment(sketch, "E986", {"start": v(-21.43, -52.47) * mm, "end": v(-20.3, -54) * mm});
            skLineSegment(sketch, "E987", {"start": v(-20.3, -54) * mm, "end": v(-18.97, -55.26) * mm});
            skLineSegment(sketch, "E988", {"start": v(-18.97, -55.26) * mm, "end": v(-17.45, -56.3) * mm});
            skLineSegment(sketch, "E989", {"start": v(-17.45, -56.3) * mm, "end": v(-15.76, -57.14) * mm});
            skLineSegment(sketch, "E990", {"start": v(-15.76, -57.14) * mm, "end": v(-13.9, -57.8) * mm});
            skLineSegment(sketch, "E991", {"start": v(-13.9, -57.8) * mm, "end": v(-11.92, -58.29) * mm});
            skLineSegment(sketch, "E992", {"start": v(-11.92, -58.29) * mm, "end": v(-10.45, -58.56) * mm});
            skLineSegment(sketch, "E993", {"start": v(-10.45, -58.56) * mm, "end": v(-8.98, -58.75) * mm});
            skLineSegment(sketch, "E994", {"start": v(-8.98, -58.75) * mm, "end": v(-7.5, -58.87) * mm});
            skLineSegment(sketch, "E995", {"start": v(-7.5, -58.87) * mm, "end": v(-6.03, -58.93) * mm});
            skLineSegment(sketch, "E996", {"start": v(-6.03, -58.93) * mm, "end": v(-4.55, -58.93) * mm});
            skLineSegment(sketch, "E997", {"start": v(-4.55, -58.93) * mm, "end": v(-3.07, -58.88) * mm});
            skLineSegment(sketch, "E998", {"start": v(-3.07, -58.88) * mm, "end": v(-1.59, -58.78) * mm});
            skLineSegment(sketch, "E999", {"start": v(-1.59, -58.78) * mm, "end": v(-0.1, -58.64) * mm});
            skLineSegment(sketch, "E1000", {"start": v(-0.1, -58.64) * mm, "end": v(3.2, -58.19) * mm});
            skLineSegment(sketch, "E1001", {"start": v(3.2, -58.19) * mm, "end": v(6.48, -57.59) * mm});
            skLineSegment(sketch, "E1002", {"start": v(6.48, -57.59) * mm, "end": v(9.71, -56.85) * mm});
            skLineSegment(sketch, "E1003", {"start": v(9.71, -56.85) * mm, "end": v(12.9, -55.97) * mm});
            skLineSegment(sketch, "E1004", {"start": v(12.9, -55.97) * mm, "end": v(16.06, -54.96) * mm});
            skLineSegment(sketch, "E1005", {"start": v(16.06, -54.96) * mm, "end": v(19.18, -53.83) * mm});
            skLineSegment(sketch, "E1006", {"start": v(19.18, -53.83) * mm, "end": v(22.26, -52.59) * mm});
            skLineSegment(sketch, "E1007", {"start": v(22.26, -52.59) * mm, "end": v(25.31, -51.23) * mm});
            skLineSegment(sketch, "E1008", {"start": v(25.31, -51.23) * mm, "end": v(25.71, -51.05) * mm});
            skLineSegment(sketch, "E1009", {"start": v(25.71, -51.05) * mm, "end": v(26.11, -50.85) * mm});
            skLineSegment(sketch, "E1010", {"start": v(26.11, -50.85) * mm, "end": v(26.51, -50.66) * mm});
            skLineSegment(sketch, "E1011", {"start": v(26.51, -50.66) * mm, "end": v(26.92, -50.45) * mm});
            skLineSegment(sketch, "E1012", {"start": v(26.92, -50.45) * mm, "end": v(27.32, -50.25) * mm});
            skLineSegment(sketch, "E1013", {"start": v(27.32, -50.25) * mm, "end": v(27.74, -50.04) * mm});
            skLineSegment(sketch, "E1014", {"start": v(27.74, -50.04) * mm, "end": v(28.16, -49.83) * mm});
            skLineSegment(sketch, "E1015", {"start": v(28.16, -49.83) * mm, "end": v(28.6, -49.61) * mm});
            skLineSegment(sketch, "E1016", {"start": v(28.6, -49.61) * mm, "end": v(28.62, -49.85) * mm});
            skLineSegment(sketch, "E1017", {"start": v(28.62, -49.85) * mm, "end": v(28.64, -50.07) * mm});
            skLineSegment(sketch, "E1018", {"start": v(28.64, -50.07) * mm, "end": v(28.66, -50.28) * mm});
            skLineSegment(sketch, "E1019", {"start": v(28.66, -50.28) * mm, "end": v(28.68, -50.48) * mm});
            skLineSegment(sketch, "E1020", {"start": v(28.68, -50.48) * mm, "end": v(28.7, -50.67) * mm});
            skLineSegment(sketch, "E1021", {"start": v(28.7, -50.67) * mm, "end": v(28.72, -50.85) * mm});
            skLineSegment(sketch, "E1022", {"start": v(28.72, -50.85) * mm, "end": v(28.75, -51.03) * mm});
            skLineSegment(sketch, "E1023", {"start": v(28.75, -51.03) * mm, "end": v(28.8, -51.2) * mm});
            skLineSegment(sketch, "E1024", {"start": v(28.8, -51.2) * mm, "end": v(28.93, -51.75) * mm});
            skLineSegment(sketch, "E1025", {"start": v(28.93, -51.75) * mm, "end": v(29.05, -52.3) * mm});
            skLineSegment(sketch, "E1026", {"start": v(29.05, -52.3) * mm, "end": v(29.18, -52.86) * mm});
            skLineSegment(sketch, "E1027", {"start": v(29.18, -52.86) * mm, "end": v(29.31, -53.4) * mm});
            skLineSegment(sketch, "E1028", {"start": v(29.31, -53.4) * mm, "end": v(29.46, -53.96) * mm});
            skLineSegment(sketch, "E1029", {"start": v(29.46, -53.96) * mm, "end": v(29.62, -54.5) * mm});
            skLineSegment(sketch, "E1030", {"start": v(29.62, -54.5) * mm, "end": v(29.8, -55.02) * mm});
            skLineSegment(sketch, "E1031", {"start": v(29.8, -55.02) * mm, "end": v(30.02, -55.53) * mm});
            skLineSegment(sketch, "E1032", {"start": v(30.02, -55.53) * mm, "end": v(30.72, -56.64) * mm});
            skLineSegment(sketch, "E1033", {"start": v(30.72, -56.64) * mm, "end": v(31.64, -57.47) * mm});
            skLineSegment(sketch, "E1034", {"start": v(31.64, -57.47) * mm, "end": v(32.71, -58.03) * mm});
            skLineSegment(sketch, "E1035", {"start": v(32.71, -58.03) * mm, "end": v(33.88, -58.31) * mm});
            skLineSegment(sketch, "E1036", {"start": v(33.88, -58.31) * mm, "end": v(35.09, -58.3) * mm});
            skLineSegment(sketch, "E1037", {"start": v(35.09, -58.3) * mm, "end": v(36.27, -58) * mm});
            skLineSegment(sketch, "E1038", {"start": v(36.27, -58) * mm, "end": v(37.36, -57.4) * mm});
            skLineSegment(sketch, "E1039", {"start": v(37.36, -57.4) * mm, "end": v(38.3, -56.49) * mm});
            skLineSegment(sketch, "E1040", {"start": v(38.3, -56.49) * mm, "end": v(38.58, -56.12) * mm});
            skLineSegment(sketch, "E1041", {"start": v(38.58, -56.12) * mm, "end": v(38.84, -55.75) * mm});
            skLineSegment(sketch, "E1042", {"start": v(38.84, -55.75) * mm, "end": v(39.1, -55.36) * mm});
            skLineSegment(sketch, "E1043", {"start": v(39.1, -55.36) * mm, "end": v(39.33, -54.96) * mm});
            skLineSegment(sketch, "E1044", {"start": v(39.33, -54.96) * mm, "end": v(39.55, -54.55) * mm});
            skLineSegment(sketch, "E1045", {"start": v(39.55, -54.55) * mm, "end": v(39.77, -54.14) * mm});
            skLineSegment(sketch, "E1046", {"start": v(39.77, -54.14) * mm, "end": v(39.96, -53.72) * mm});
            skLineSegment(sketch, "E1047", {"start": v(39.96, -53.72) * mm, "end": v(40.15, -53.3) * mm});
            skLineSegment(sketch, "E1048", {"start": v(40.15, -53.3) * mm, "end": v(41.77, -49.69) * mm});
            skLineSegment(sketch, "E1049", {"start": v(41.77, -49.69) * mm, "end": v(43.52, -46.15) * mm});
            skLineSegment(sketch, "E1050", {"start": v(43.52, -46.15) * mm, "end": v(45.39, -42.7) * mm});
            skLineSegment(sketch, "E1051", {"start": v(45.39, -42.7) * mm, "end": v(47.38, -39.3) * mm});
            skLineSegment(sketch, "E1052", {"start": v(47.38, -39.3) * mm, "end": v(49.47, -35.98) * mm});
            skLineSegment(sketch, "E1053", {"start": v(49.47, -35.98) * mm, "end": v(51.67, -32.71) * mm});
            skLineSegment(sketch, "E1054", {"start": v(51.67, -32.71) * mm, "end": v(53.97, -29.51) * mm});
            skLineSegment(sketch, "E1055", {"start": v(53.97, -29.51) * mm, "end": v(56.36, -26.37) * mm});
            skLineSegment(sketch, "E1056", {"start": v(56.36, -26.37) * mm, "end": v(57.2, -25.33) * mm});
            skLineSegment(sketch, "E1057", {"start": v(57.2, -25.33) * mm, "end": v(58.05, -24.31) * mm});
            skLineSegment(sketch, "E1058", {"start": v(58.05, -24.31) * mm, "end": v(58.92, -23.3) * mm});
            skLineSegment(sketch, "E1059", {"start": v(58.92, -23.3) * mm, "end": v(59.8, -22.31) * mm});
            skLineSegment(sketch, "E1060", {"start": v(59.8, -22.31) * mm, "end": v(60.7, -21.32) * mm});
            skLineSegment(sketch, "E1061", {"start": v(60.7, -21.32) * mm, "end": v(61.6, -20.34) * mm});
            skLineSegment(sketch, "E1062", {"start": v(61.6, -20.34) * mm, "end": v(62.5, -19.35) * mm});
            skLineSegment(sketch, "E1063", {"start": v(62.5, -19.35) * mm, "end": v(63.4, -18.36) * mm});
            skLineSegment(sketch, "E1064", {"start": v(63.4, -18.36) * mm, "end": v(63.59, -18.17) * mm});
            skLineSegment(sketch, "E1065", {"start": v(63.59, -18.17) * mm, "end": v(63.78, -18) * mm});
            skLineSegment(sketch, "E1066", {"start": v(63.78, -18) * mm, "end": v(64, -17.86) * mm});
            skLineSegment(sketch, "E1067", {"start": v(64, -17.86) * mm, "end": v(64.21, -17.76) * mm});
            skLineSegment(sketch, "E1068", {"start": v(64.21, -17.76) * mm, "end": v(64.45, -17.72) * mm});
            skLineSegment(sketch, "E1069", {"start": v(64.45, -17.72) * mm, "end": v(64.7, -17.75) * mm});
            skLineSegment(sketch, "E1070", {"start": v(64.7, -17.75) * mm, "end": v(64.95, -17.86) * mm});
            skLineSegment(sketch, "E1071", {"start": v(64.95, -17.86) * mm, "end": v(65.22, -18.05) * mm});
            skLineSegment(sketch, "E1072", {"start": v(65.22, -18.05) * mm, "end": v(64.32, -19.8) * mm});
            skLineSegment(sketch, "E1073", {"start": v(64.32, -19.8) * mm, "end": v(63.45, -21.57) * mm});
            skLineSegment(sketch, "E1074", {"start": v(63.45, -21.57) * mm, "end": v(62.63, -23.36) * mm});
            skLineSegment(sketch, "E1075", {"start": v(62.63, -23.36) * mm, "end": v(61.85, -25.15) * mm});
            skLineSegment(sketch, "E1076", {"start": v(61.85, -25.15) * mm, "end": v(61.1, -26.97) * mm});
            skLineSegment(sketch, "E1077", {"start": v(61.1, -26.97) * mm, "end": v(60.4, -28.8) * mm});
            skLineSegment(sketch, "E1078", {"start": v(60.4, -28.8) * mm, "end": v(59.73, -30.64) * mm});
            skLineSegment(sketch, "E1079", {"start": v(59.73, -30.64) * mm, "end": v(59.1, -32.5) * mm});
            skLineSegment(sketch, "E1080", {"start": v(59.1, -32.5) * mm, "end": v(58.46, -34.78) * mm});
            skLineSegment(sketch, "E1081", {"start": v(58.46, -34.78) * mm, "end": v(58, -37.04) * mm});
            skLineSegment(sketch, "E1082", {"start": v(58, -37.04) * mm, "end": v(57.76, -39.29) * mm});
            skLineSegment(sketch, "E1083", {"start": v(57.76, -39.29) * mm, "end": v(57.72, -41.53) * mm});
            skLineSegment(sketch, "E1084", {"start": v(57.72, -41.53) * mm, "end": v(57.9, -43.75) * mm});
            skLineSegment(sketch, "E1085", {"start": v(57.9, -43.75) * mm, "end": v(58.3, -45.97) * mm});
            skLineSegment(sketch, "E1086", {"start": v(58.3, -45.97) * mm, "end": v(58.96, -48.17) * mm});
            skLineSegment(sketch, "E1087", {"start": v(58.96, -48.17) * mm, "end": v(59.87, -50.36) * mm});
            skLineSegment(sketch, "E1088", {"start": v(59.87, -50.36) * mm, "end": v(60.59, -51.76) * mm});
            skLineSegment(sketch, "E1089", {"start": v(60.59, -51.76) * mm, "end": v(61.4, -53.07) * mm});
            skLineSegment(sketch, "E1090", {"start": v(61.4, -53.07) * mm, "end": v(62.3, -54.27) * mm});
            skLineSegment(sketch, "E1091", {"start": v(62.3, -54.27) * mm, "end": v(63.32, -55.35) * mm});
            skLineSegment(sketch, "E1092", {"start": v(63.32, -55.35) * mm, "end": v(64.46, -56.3) * mm});
            skLineSegment(sketch, "E1093", {"start": v(64.46, -56.3) * mm, "end": v(65.73, -57.09) * mm});
            skLineSegment(sketch, "E1094", {"start": v(65.73, -57.09) * mm, "end": v(67.13, -57.7) * mm});
            skLineSegment(sketch, "E1095", {"start": v(67.13, -57.7) * mm, "end": v(68.7, -58.15) * mm});
            skLineSegment(sketch, "E1096", {"start": v(68.7, -58.15) * mm, "end": v(69.86, -58.33) * mm});
            skLineSegment(sketch, "E1097", {"start": v(69.86, -58.33) * mm, "end": v(71.01, -58.4) * mm});
            skLineSegment(sketch, "E1098", {"start": v(71.01, -58.4) * mm, "end": v(72.15, -58.36) * mm});
            skLineSegment(sketch, "E1099", {"start": v(72.15, -58.36) * mm, "end": v(73.29, -58.23) * mm});
            skLineSegment(sketch, "E1100", {"start": v(73.29, -58.23) * mm, "end": v(74.41, -58.02) * mm});
            skLineSegment(sketch, "E1101", {"start": v(74.41, -58.02) * mm, "end": v(75.53, -57.74) * mm});
            skLineSegment(sketch, "E1102", {"start": v(75.53, -57.74) * mm, "end": v(76.64, -57.4) * mm});
            skLineSegment(sketch, "E1103", {"start": v(76.64, -57.4) * mm, "end": v(77.74, -57.03) * mm});
            skLineSegment(sketch, "E1104", {"start": v(77.74, -57.03) * mm, "end": v(79.9, -56.2) * mm});
            skLineSegment(sketch, "E1105", {"start": v(79.9, -56.2) * mm, "end": v(81.98, -55.24) * mm});
            skLineSegment(sketch, "E1106", {"start": v(81.98, -55.24) * mm, "end": v(84.02, -54.2) * mm});
            skLineSegment(sketch, "E1107", {"start": v(84.02, -54.2) * mm, "end": v(86.01, -53.09) * mm});
            skLineSegment(sketch, "E1108", {"start": v(86.01, -53.09) * mm, "end": v(87.96, -51.9) * mm});
            skLineSegment(sketch, "E1109", {"start": v(87.96, -51.9) * mm, "end": v(89.89, -50.66) * mm});
            skLineSegment(sketch, "E1110", {"start": v(89.89, -50.66) * mm, "end": v(91.78, -49.37) * mm});
            skLineSegment(sketch, "E1111", {"start": v(91.78, -49.37) * mm, "end": v(93.66, -48.06) * mm});
            skLineSegment(sketch, "E1112", {"start": v(93.66, -48.06) * mm, "end": v(93.91, -47.88) * mm});
            skLineSegment(sketch, "E1113", {"start": v(93.91, -47.88) * mm, "end": v(94.16, -47.7) * mm});
            skLineSegment(sketch, "E1114", {"start": v(94.16, -47.7) * mm, "end": v(94.42, -47.52) * mm});
            skLineSegment(sketch, "E1115", {"start": v(94.42, -47.52) * mm, "end": v(94.67, -47.34) * mm});
            skLineSegment(sketch, "E1116", {"start": v(94.67, -47.34) * mm, "end": v(94.92, -47.16) * mm});
            skLineSegment(sketch, "E1117", {"start": v(94.92, -47.16) * mm, "end": v(95.18, -46.98) * mm});
            skLineSegment(sketch, "E1118", {"start": v(95.18, -46.98) * mm, "end": v(95.44, -46.8) * mm});
            skLineSegment(sketch, "E1119", {"start": v(95.44, -46.8) * mm, "end": v(95.7, -46.6) * mm});
            skLineSegment(sketch, "E1120", {"start": v(95.7, -46.6) * mm, "end": v(95.81, -46.8) * mm});
            skLineSegment(sketch, "E1121", {"start": v(95.81, -46.8) * mm, "end": v(95.92, -46.97) * mm});
            skLineSegment(sketch, "E1122", {"start": v(95.92, -46.97) * mm, "end": v(96.02, -47.13) * mm});
            skLineSegment(sketch, "E1123", {"start": v(96.02, -47.13) * mm, "end": v(96.11, -47.29) * mm});
            skLineSegment(sketch, "E1124", {"start": v(96.11, -47.29) * mm, "end": v(96.2, -47.44) * mm});
            skLineSegment(sketch, "E1125", {"start": v(96.2, -47.44) * mm, "end": v(96.29, -47.58) * mm});
            skLineSegment(sketch, "E1126", {"start": v(96.29, -47.58) * mm, "end": v(96.37, -47.72) * mm});
            skLineSegment(sketch, "E1127", {"start": v(96.37, -47.72) * mm, "end": v(96.46, -47.86) * mm});
            skLineSegment(sketch, "E1128", {"start": v(96.46, -47.86) * mm, "end": v(97.82, -49.9) * mm});
            skLineSegment(sketch, "E1129", {"start": v(97.82, -49.9) * mm, "end": v(99.33, -51.73) * mm});
            skLineSegment(sketch, "E1130", {"start": v(99.33, -51.73) * mm, "end": v(100.98, -53.34) * mm});
            skLineSegment(sketch, "E1131", {"start": v(100.98, -53.34) * mm, "end": v(102.77, -54.74) * mm});
            skLineSegment(sketch, "E1132", {"start": v(102.77, -54.74) * mm, "end": v(104.72, -55.91) * mm});
            skLineSegment(sketch, "E1133", {"start": v(104.72, -55.91) * mm, "end": v(106.82, -56.86) * mm});
            skLineSegment(sketch, "E1134", {"start": v(106.82, -56.86) * mm, "end": v(109.07, -57.59) * mm});
            skLineSegment(sketch, "E1135", {"start": v(109.07, -57.59) * mm, "end": v(111.48, -58.08) * mm});
            skLineSegment(sketch, "E1136", {"start": v(111.48, -58.08) * mm, "end": v(113.39, -58.3) * mm});
            skLineSegment(sketch, "E1137", {"start": v(113.39, -58.3) * mm, "end": v(115.28, -58.39) * mm});
            skLineSegment(sketch, "E1138", {"start": v(115.28, -58.39) * mm, "end": v(117.15, -58.35) * mm});
            skLineSegment(sketch, "E1139", {"start": v(117.15, -58.35) * mm, "end": v(119.02, -58.19) * mm});
            skLineSegment(sketch, "E1140", {"start": v(119.02, -58.19) * mm, "end": v(120.87, -57.92) * mm});
            skLineSegment(sketch, "E1141", {"start": v(120.87, -57.92) * mm, "end": v(122.71, -57.54) * mm});
            skLineSegment(sketch, "E1142", {"start": v(122.71, -57.54) * mm, "end": v(124.54, -57.06) * mm});
            skLineSegment(sketch, "E1143", {"start": v(124.54, -57.06) * mm, "end": v(126.36, -56.49) * mm});
            skLineSegment(sketch, "E1144", {"start": v(126.36, -56.49) * mm, "end": v(129.32, -55.37) * mm});
            skLineSegment(sketch, "E1145", {"start": v(129.32, -55.37) * mm, "end": v(132.18, -54.08) * mm});
            skLineSegment(sketch, "E1146", {"start": v(132.18, -54.08) * mm, "end": v(134.94, -52.64) * mm});
            skLineSegment(sketch, "E1147", {"start": v(134.94, -52.64) * mm, "end": v(137.61, -51.04) * mm});
            skLineSegment(sketch, "E1148", {"start": v(137.61, -51.04) * mm, "end": v(140.2, -49.32) * mm});
            skLineSegment(sketch, "E1149", {"start": v(140.2, -49.32) * mm, "end": v(142.72, -47.47) * mm});
            skLineSegment(sketch, "E1150", {"start": v(142.72, -47.47) * mm, "end": v(145.17, -45.52) * mm});
            skLineSegment(sketch, "E1151", {"start": v(145.17, -45.52) * mm, "end": v(147.57, -43.47) * mm});
            skLineSegment(sketch, "E1152", {"start": v(147.57, -43.47) * mm, "end": v(147.67, -43.38) * mm});
            skLineSegment(sketch, "E1153", {"start": v(147.67, -43.38) * mm, "end": v(147.77, -43.3) * mm});
            skLineSegment(sketch, "E1154", {"start": v(147.77, -43.3) * mm, "end": v(147.87, -43.2) * mm});
            skLineSegment(sketch, "E1155", {"start": v(147.87, -43.2) * mm, "end": v(147.97, -43.11) * mm});
            skLineSegment(sketch, "E1156", {"start": v(147.97, -43.11) * mm, "end": v(148.07, -43.02) * mm});
            skLineSegment(sketch, "E1157", {"start": v(148.07, -43.02) * mm, "end": v(148.17, -42.93) * mm});
            skLineSegment(sketch, "E1158", {"start": v(148.17, -42.93) * mm, "end": v(148.28, -42.84) * mm});
            skLineSegment(sketch, "E1159", {"start": v(148.28, -42.84) * mm, "end": v(148.38, -42.75) * mm});
            skLineSegment(sketch, "E1160", {"start": v(148.38, -42.75) * mm, "end": v(149.24, -41.77) * mm});
            skLineSegment(sketch, "E1161", {"start": v(149.24, -41.77) * mm, "end": v(149.86, -40.68) * mm});
            skLineSegment(sketch, "E1162", {"start": v(149.86, -40.68) * mm, "end": v(150.24, -39.5) * mm});
            skLineSegment(sketch, "E1163", {"start": v(150.24, -39.5) * mm, "end": v(150.37, -38.3) * mm});
            skLineSegment(sketch, "E1164", {"start": v(150.37, -38.3) * mm, "end": v(150.27, -37.07) * mm});
            skLineSegment(sketch, "E1165", {"start": v(150.27, -37.07) * mm, "end": v(149.93, -35.89) * mm});
            skLineSegment(sketch, "E1166", {"start": v(149.93, -35.89) * mm, "end": v(149.34, -34.78) * mm});
            skLineSegment(sketch, "E1167", {"start": v(149.34, -34.78) * mm, "end": v(148.5, -33.78) * mm});
            skLineSegment(sketch, "E1168", {"start": v(148.5, -33.78) * mm, "end": v(148.47, -33.75) * mm});
            skLineSegment(sketch, "E1169", {"start": v(148.47, -33.75) * mm, "end": v(148.43, -33.71) * mm});
            skLineSegment(sketch, "E1170", {"start": v(148.43, -33.71) * mm, "end": v(148.4, -33.68) * mm});
            skLineSegment(sketch, "E1171", {"start": v(148.4, -33.68) * mm, "end": v(148.35, -33.64) * mm});
            skLineSegment(sketch, "E1172", {"start": v(148.35, -33.64) * mm, "end": v(148.32, -33.6) * mm});
            skLineSegment(sketch, "E1173", {"start": v(148.32, -33.6) * mm, "end": v(148.28, -33.57) * mm});
            skLineSegment(sketch, "E1174", {"start": v(148.28, -33.57) * mm, "end": v(148.24, -33.53) * mm});
            skLineSegment(sketch, "E1175", {"start": v(148.24, -33.53) * mm, "end": v(148.2, -33.5) * mm});
            skLineSegment(sketch, "E1176", {"start": v(41.95, -14.05) * mm, "end": v(42.08, -13.11) * mm});
            skLineSegment(sketch, "E1177", {"start": v(42.08, -13.11) * mm, "end": v(42.2, -12.17) * mm});
            skLineSegment(sketch, "E1178", {"start": v(42.2, -12.17) * mm, "end": v(42.32, -11.22) * mm});
            skLineSegment(sketch, "E1179", {"start": v(42.32, -11.22) * mm, "end": v(42.45, -10.28) * mm});
            skLineSegment(sketch, "E1180", {"start": v(42.45, -10.28) * mm, "end": v(42.57, -9.34) * mm});
            skLineSegment(sketch, "E1181", {"start": v(42.57, -9.34) * mm, "end": v(42.7, -8.4) * mm});
            skLineSegment(sketch, "E1182", {"start": v(42.7, -8.4) * mm, "end": v(42.83, -7.45) * mm});
            skLineSegment(sketch, "E1183", {"start": v(42.83, -7.45) * mm, "end": v(42.97, -6.51) * mm});
            skLineSegment(sketch, "E1184", {"start": v(42.97, -6.51) * mm, "end": v(43.38, -3.8) * mm});
            skLineSegment(sketch, "E1185", {"start": v(43.38, -3.8) * mm, "end": v(43.79, -1.1) * mm});
            skLineSegment(sketch, "E1186", {"start": v(43.79, -1.1) * mm, "end": v(44.2, 1.62) * mm});
            skLineSegment(sketch, "E1187", {"start": v(44.2, 1.62) * mm, "end": v(44.6, 4.33) * mm});
            skLineSegment(sketch, "E1188", {"start": v(44.6, 4.33) * mm, "end": v(45.02, 7.04) * mm});
            skLineSegment(sketch, "E1189", {"start": v(45.02, 7.04) * mm, "end": v(45.44, 9.74) * mm});
            skLineSegment(sketch, "E1190", {"start": v(45.44, 9.74) * mm, "end": v(45.87, 12.45) * mm});
            skLineSegment(sketch, "E1191", {"start": v(45.87, 12.45) * mm, "end": v(46.3, 15.16) * mm});
            skLineSegment(sketch, "E1192", {"start": v(46.3, 15.16) * mm, "end": v(47.06, 19.08) * mm});
            skLineSegment(sketch, "E1193", {"start": v(47.06, 19.08) * mm, "end": v(48.05, 22.91) * mm});
            skLineSegment(sketch, "E1194", {"start": v(48.05, 22.91) * mm, "end": v(49.27, 26.65) * mm});
            skLineSegment(sketch, "E1195", {"start": v(49.27, 26.65) * mm, "end": v(50.68, 30.31) * mm});
            skLineSegment(sketch, "E1196", {"start": v(50.68, 30.31) * mm, "end": v(52.29, 33.9) * mm});
            skLineSegment(sketch, "E1197", {"start": v(52.29, 33.9) * mm, "end": v(54.06, 37.41) * mm});
            skLineSegment(sketch, "E1198", {"start": v(54.06, 37.41) * mm, "end": v(56, 40.86) * mm});
            skLineSegment(sketch, "E1199", {"start": v(56, 40.86) * mm, "end": v(58.07, 44.26) * mm});
            skLineSegment(sketch, "E1200", {"start": v(58.07, 44.26) * mm, "end": v(58.28, 44.56) * mm});
            skLineSegment(sketch, "E1201", {"start": v(58.28, 44.56) * mm, "end": v(58.5, 44.87) * mm});
            skLineSegment(sketch, "E1202", {"start": v(58.5, 44.87) * mm, "end": v(58.73, 45.16) * mm});
            skLineSegment(sketch, "E1203", {"start": v(58.73, 45.16) * mm, "end": v(58.97, 45.45) * mm});
            skLineSegment(sketch, "E1204", {"start": v(58.97, 45.45) * mm, "end": v(59.22, 45.73) * mm});
            skLineSegment(sketch, "E1205", {"start": v(59.22, 45.73) * mm, "end": v(59.48, 46) * mm});
            skLineSegment(sketch, "E1206", {"start": v(59.48, 46) * mm, "end": v(59.75, 46.26) * mm});
            skLineSegment(sketch, "E1207", {"start": v(59.75, 46.26) * mm, "end": v(60.01, 46.52) * mm});
            skLineSegment(sketch, "E1208", {"start": v(60.01, 46.52) * mm, "end": v(60.4, 46.85) * mm});
            skLineSegment(sketch, "E1209", {"start": v(60.4, 46.85) * mm, "end": v(60.77, 47.05) * mm});
            skLineSegment(sketch, "E1210", {"start": v(60.77, 47.05) * mm, "end": v(61.1, 47.14) * mm});
            skLineSegment(sketch, "E1211", {"start": v(61.1, 47.14) * mm, "end": v(61.4, 47.12) * mm});
            skLineSegment(sketch, "E1212", {"start": v(61.4, 47.12) * mm, "end": v(61.65, 46.98) * mm});
            skLineSegment(sketch, "E1213", {"start": v(61.65, 46.98) * mm, "end": v(61.88, 46.72) * mm});
            skLineSegment(sketch, "E1214", {"start": v(61.88, 46.72) * mm, "end": v(62.06, 46.35) * mm});
            skLineSegment(sketch, "E1215", {"start": v(62.06, 46.35) * mm, "end": v(62.2, 45.87) * mm});
            skLineSegment(sketch, "E1216", {"start": v(62.2, 45.87) * mm, "end": v(62.38, 44.9) * mm});
            skLineSegment(sketch, "E1217", {"start": v(62.38, 44.9) * mm, "end": v(62.49, 43.93) * mm});
            skLineSegment(sketch, "E1218", {"start": v(62.49, 43.93) * mm, "end": v(62.53, 42.96) * mm});
            skLineSegment(sketch, "E1219", {"start": v(62.53, 42.96) * mm, "end": v(62.51, 42) * mm});
            skLineSegment(sketch, "E1220", {"start": v(62.51, 42) * mm, "end": v(62.44, 41.03) * mm});
            skLineSegment(sketch, "E1221", {"start": v(62.44, 41.03) * mm, "end": v(62.33, 40.06) * mm});
            skLineSegment(sketch, "E1222", {"start": v(62.33, 40.06) * mm, "end": v(62.18, 39.1) * mm});
            skLineSegment(sketch, "E1223", {"start": v(62.18, 39.1) * mm, "end": v(62.01, 38.14) * mm});
            skLineSegment(sketch, "E1224", {"start": v(62.01, 38.14) * mm, "end": v(61.31, 34.86) * mm});
            skLineSegment(sketch, "E1225", {"start": v(61.31, 34.86) * mm, "end": v(60.5, 31.62) * mm});
            skLineSegment(sketch, "E1226", {"start": v(60.5, 31.62) * mm, "end": v(59.58, 28.42) * mm});
            skLineSegment(sketch, "E1227", {"start": v(59.58, 28.42) * mm, "end": v(58.56, 25.25) * mm});
            skLineSegment(sketch, "E1228", {"start": v(58.56, 25.25) * mm, "end": v(57.46, 22.1) * mm});
            skLineSegment(sketch, "E1229", {"start": v(57.46, 22.1) * mm, "end": v(56.28, 18.98) * mm});
            skLineSegment(sketch, "E1230", {"start": v(56.28, 18.98) * mm, "end": v(55.05, 15.88) * mm});
            skLineSegment(sketch, "E1231", {"start": v(55.05, 15.88) * mm, "end": v(53.76, 12.8) * mm});
            skLineSegment(sketch, "E1232", {"start": v(53.76, 12.8) * mm, "end": v(52.38, 9.54) * mm});
            skLineSegment(sketch, "E1233", {"start": v(52.38, 9.54) * mm, "end": v(50.99, 6.3) * mm});
            skLineSegment(sketch, "E1234", {"start": v(50.99, 6.3) * mm, "end": v(49.6, 3.05) * mm});
            skLineSegment(sketch, "E1235", {"start": v(49.6, 3.05) * mm, "end": v(48.2, -0.2) * mm});
            skLineSegment(sketch, "E1236", {"start": v(48.2, -0.2) * mm, "end": v(46.8, -3.44) * mm});
            skLineSegment(sketch, "E1237", {"start": v(46.8, -3.44) * mm, "end": v(45.4, -6.68) * mm});
            skLineSegment(sketch, "E1238", {"start": v(45.4, -6.68) * mm, "end": v(44, -9.93) * mm});
            skLineSegment(sketch, "E1239", {"start": v(44, -9.93) * mm, "end": v(42.6, -13.17) * mm});
            skLineSegment(sketch, "E1240", {"start": v(42.6, -13.17) * mm, "end": v(42.55, -13.3) * mm});
            skLineSegment(sketch, "E1241", {"start": v(42.55, -13.3) * mm, "end": v(42.5, -13.4) * mm});
            skLineSegment(sketch, "E1242", {"start": v(42.5, -13.4) * mm, "end": v(42.44, -13.53) * mm});
            skLineSegment(sketch, "E1243", {"start": v(42.44, -13.53) * mm, "end": v(42.38, -13.64) * mm});
            skLineSegment(sketch, "E1244", {"start": v(42.38, -13.64) * mm, "end": v(42.32, -13.76) * mm});
            skLineSegment(sketch, "E1245", {"start": v(42.32, -13.76) * mm, "end": v(42.27, -13.88) * mm});
            skLineSegment(sketch, "E1246", {"start": v(42.27, -13.88) * mm, "end": v(42.2, -14) * mm});
            skLineSegment(sketch, "E1247", {"start": v(42.2, -14) * mm, "end": v(42.15, -14.1) * mm});
            skLineSegment(sketch, "E1248", {"start": v(42.15, -14.1) * mm, "end": v(42.12, -14.1) * mm});
            skLineSegment(sketch, "E1249", {"start": v(42.12, -14.1) * mm, "end": v(42.1, -14.1) * mm});
            skLineSegment(sketch, "E1250", {"start": v(42.1, -14.1) * mm, "end": v(42.08, -14.09) * mm});
            skLineSegment(sketch, "E1251", {"start": v(42.08, -14.09) * mm, "end": v(42.05, -14.08) * mm});
            skLineSegment(sketch, "E1252", {"start": v(42.05, -14.08) * mm, "end": v(42.03, -14.07) * mm});
            skLineSegment(sketch, "E1253", {"start": v(42.03, -14.07) * mm, "end": v(42, -14.07) * mm});
            skLineSegment(sketch, "E1254", {"start": v(42, -14.07) * mm, "end": v(41.98, -14.06) * mm});
            skLineSegment(sketch, "E1255", {"start": v(41.98, -14.06) * mm, "end": v(41.95, -14.05) * mm});
            skLineSegment(sketch, "E1256", {"start": v(-75.54, -9.22) * mm, "end": v(-75.37, -7.98) * mm});
            skLineSegment(sketch, "E1257", {"start": v(-75.37, -7.98) * mm, "end": v(-75.2, -6.74) * mm});
            skLineSegment(sketch, "E1258", {"start": v(-75.2, -6.74) * mm, "end": v(-75.04, -5.5) * mm});
            skLineSegment(sketch, "E1259", {"start": v(-75.04, -5.5) * mm, "end": v(-74.87, -4.25) * mm});
            skLineSegment(sketch, "E1260", {"start": v(-74.87, -4.25) * mm, "end": v(-74.7, -3.01) * mm});
            skLineSegment(sketch, "E1261", {"start": v(-74.7, -3.01) * mm, "end": v(-74.53, -1.77) * mm});
            skLineSegment(sketch, "E1262", {"start": v(-74.53, -1.77) * mm, "end": v(-74.35, -0.53) * mm});
            skLineSegment(sketch, "E1263", {"start": v(-74.35, -0.53) * mm, "end": v(-74.17, 0.71) * mm});
            skLineSegment(sketch, "E1264", {"start": v(-74.17, 0.71) * mm, "end": v(-73.5, 4.68) * mm});
            skLineSegment(sketch, "E1265", {"start": v(-73.5, 4.68) * mm, "end": v(-72.7, 8.6) * mm});
            skLineSegment(sketch, "E1266", {"start": v(-72.7, 8.6) * mm, "end": v(-71.8, 12.51) * mm});
            skLineSegment(sketch, "E1267", {"start": v(-71.8, 12.51) * mm, "end": v(-70.8, 16.39) * mm});
            skLineSegment(sketch, "E1268", {"start": v(-70.8, 16.39) * mm, "end": v(-69.7, 20.23) * mm});
            skLineSegment(sketch, "E1269", {"start": v(-69.7, 20.23) * mm, "end": v(-68.48, 24.05) * mm});
            skLineSegment(sketch, "E1270", {"start": v(-68.48, 24.05) * mm, "end": v(-67.16, 27.83) * mm});
            skLineSegment(sketch, "E1271", {"start": v(-67.16, 27.83) * mm, "end": v(-65.76, 31.6) * mm});
            skLineSegment(sketch, "E1272", {"start": v(-65.76, 31.6) * mm, "end": v(-65.29, 32.72) * mm});
            skLineSegment(sketch, "E1273", {"start": v(-65.29, 32.72) * mm, "end": v(-64.77, 33.82) * mm});
            skLineSegment(sketch, "E1274", {"start": v(-64.77, 33.82) * mm, "end": v(-64.22, 34.9) * mm});
            skLineSegment(sketch, "E1275", {"start": v(-64.22, 34.9) * mm, "end": v(-63.63, 35.98) * mm});
            skLineSegment(sketch, "E1276", {"start": v(-63.63, 35.98) * mm, "end": v(-63.02, 37.05) * mm});
            skLineSegment(sketch, "E1277", {"start": v(-63.02, 37.05) * mm, "end": v(-62.39, 38.1) * mm});
            skLineSegment(sketch, "E1278", {"start": v(-62.39, 38.1) * mm, "end": v(-61.75, 39.15) * mm});
            skLineSegment(sketch, "E1279", {"start": v(-61.75, 39.15) * mm, "end": v(-61.1, 40.2) * mm});
            skLineSegment(sketch, "E1280", {"start": v(-61.1, 40.2) * mm, "end": v(-60.85, 40.58) * mm});
            skLineSegment(sketch, "E1281", {"start": v(-60.85, 40.58) * mm, "end": v(-60.56, 40.94) * mm});
            skLineSegment(sketch, "E1282", {"start": v(-60.56, 40.94) * mm, "end": v(-60.23, 41.28) * mm});
            skLineSegment(sketch, "E1283", {"start": v(-60.23, 41.28) * mm, "end": v(-59.88, 41.61) * mm});
            skLineSegment(sketch, "E1284", {"start": v(-59.88, 41.61) * mm, "end": v(-59.5, 41.93) * mm});
            skLineSegment(sketch, "E1285", {"start": v(-59.5, 41.93) * mm, "end": v(-59.13, 42.22) * mm});
            skLineSegment(sketch, "E1286", {"start": v(-59.13, 42.22) * mm, "end": v(-58.73, 42.5) * mm});
            skLineSegment(sketch, "E1287", {"start": v(-58.73, 42.5) * mm, "end": v(-58.34, 42.77) * mm});
            skLineSegment(sketch, "E1288", {"start": v(-58.34, 42.77) * mm, "end": v(-57.94, 43) * mm});
            skLineSegment(sketch, "E1289", {"start": v(-57.94, 43) * mm, "end": v(-57.6, 43.14) * mm});
            skLineSegment(sketch, "E1290", {"start": v(-57.6, 43.14) * mm, "end": v(-57.32, 43.17) * mm});
            skLineSegment(sketch, "E1291", {"start": v(-57.32, 43.17) * mm, "end": v(-57.09, 43.1) * mm});
            skLineSegment(sketch, "E1292", {"start": v(-57.09, 43.1) * mm, "end": v(-56.9, 42.94) * mm});
            skLineSegment(sketch, "E1293", {"start": v(-56.9, 42.94) * mm, "end": v(-56.76, 42.67) * mm});
            skLineSegment(sketch, "E1294", {"start": v(-56.76, 42.67) * mm, "end": v(-56.66, 42.3) * mm});
            skLineSegment(sketch, "E1295", {"start": v(-56.66, 42.3) * mm, "end": v(-56.59, 41.84) * mm});
            skLineSegment(sketch, "E1296", {"start": v(-56.59, 41.84) * mm, "end": v(-56.49, 40.39) * mm});
            skLineSegment(sketch, "E1297", {"start": v(-56.49, 40.39) * mm, "end": v(-56.5, 38.95) * mm});
            skLineSegment(sketch, "E1298", {"start": v(-56.5, 38.95) * mm, "end": v(-56.6, 37.52) * mm});
            skLineSegment(sketch, "E1299", {"start": v(-56.6, 37.52) * mm, "end": v(-56.79, 36.1) * mm});
            skLineSegment(sketch, "E1300", {"start": v(-56.79, 36.1) * mm, "end": v(-57.04, 34.7) * mm});
            skLineSegment(sketch, "E1301", {"start": v(-57.04, 34.7) * mm, "end": v(-57.34, 33.3) * mm});
            skLineSegment(sketch, "E1302", {"start": v(-57.34, 33.3) * mm, "end": v(-57.67, 31.9) * mm});
            skLineSegment(sketch, "E1303", {"start": v(-57.67, 31.9) * mm, "end": v(-58.03, 30.5) * mm});
            skLineSegment(sketch, "E1304", {"start": v(-58.03, 30.5) * mm, "end": v(-59.02, 26.97) * mm});
            skLineSegment(sketch, "E1305", {"start": v(-59.02, 26.97) * mm, "end": v(-60.13, 23.47) * mm});
            skLineSegment(sketch, "E1306", {"start": v(-60.13, 23.47) * mm, "end": v(-61.34, 20.02) * mm});
            skLineSegment(sketch, "E1307", {"start": v(-61.34, 20.02) * mm, "end": v(-62.65, 16.6) * mm});
            skLineSegment(sketch, "E1308", {"start": v(-62.65, 16.6) * mm, "end": v(-64.05, 13.22) * mm});
            skLineSegment(sketch, "E1309", {"start": v(-64.05, 13.22) * mm, "end": v(-65.52, 9.87) * mm});
            skLineSegment(sketch, "E1310", {"start": v(-65.52, 9.87) * mm, "end": v(-67.06, 6.54) * mm});
            skLineSegment(sketch, "E1311", {"start": v(-67.06, 6.54) * mm, "end": v(-68.65, 3.23) * mm});
            skLineSegment(sketch, "E1312", {"start": v(-68.65, 3.23) * mm, "end": v(-69.43, 1.65) * mm});
            skLineSegment(sketch, "E1313", {"start": v(-69.43, 1.65) * mm, "end": v(-70.22, 0.08) * mm});
            skLineSegment(sketch, "E1314", {"start": v(-70.22, 0.08) * mm, "end": v(-71.02, -1.5) * mm});
            skLineSegment(sketch, "E1315", {"start": v(-71.02, -1.5) * mm, "end": v(-71.83, -3.06) * mm});
            skLineSegment(sketch, "E1316", {"start": v(-71.83, -3.06) * mm, "end": v(-72.64, -4.62) * mm});
            skLineSegment(sketch, "E1317", {"start": v(-72.64, -4.62) * mm, "end": v(-73.45, -6.19) * mm});
            skLineSegment(sketch, "E1318", {"start": v(-73.45, -6.19) * mm, "end": v(-74.26, -7.75) * mm});
            skLineSegment(sketch, "E1319", {"start": v(-74.26, -7.75) * mm, "end": v(-75.07, -9.32) * mm});
            skLineSegment(sketch, "E1320", {"start": v(-75.07, -9.32) * mm, "end": v(-75.13, -9.3) * mm});
            skLineSegment(sketch, "E1321", {"start": v(-75.13, -9.3) * mm, "end": v(-75.19, -9.3) * mm});
            skLineSegment(sketch, "E1322", {"start": v(-75.19, -9.3) * mm, "end": v(-75.25, -9.28) * mm});
            skLineSegment(sketch, "E1323", {"start": v(-75.25, -9.28) * mm, "end": v(-75.3, -9.27) * mm});
            skLineSegment(sketch, "E1324", {"start": v(-75.3, -9.27) * mm, "end": v(-75.36, -9.26) * mm});
            skLineSegment(sketch, "E1325", {"start": v(-75.36, -9.26) * mm, "end": v(-75.42, -9.25) * mm});
            skLineSegment(sketch, "E1326", {"start": v(-75.42, -9.25) * mm, "end": v(-75.48, -9.24) * mm});
            skLineSegment(sketch, "E1327", {"start": v(-75.48, -9.24) * mm, "end": v(-75.54, -9.22) * mm});
            skLineSegment(sketch, "E1328", {"start": v(-17.23, -42.92) * mm, "end": v(-15.18, -40.77) * mm});
            skLineSegment(sketch, "E1329", {"start": v(-15.18, -40.77) * mm, "end": v(-13.13, -38.61) * mm});
            skLineSegment(sketch, "E1330", {"start": v(-13.13, -38.61) * mm, "end": v(-11.07, -36.45) * mm});
            skLineSegment(sketch, "E1331", {"start": v(-11.07, -36.45) * mm, "end": v(-9, -34.28) * mm});
            skLineSegment(sketch, "E1332", {"start": v(-9, -34.28) * mm, "end": v(-6.92, -32.09) * mm});
            skLineSegment(sketch, "E1333", {"start": v(-6.92, -32.09) * mm, "end": v(-4.81, -29.88) * mm});
            skLineSegment(sketch, "E1334", {"start": v(-4.81, -29.88) * mm, "end": v(-2.69, -27.65) * mm});
            skLineSegment(sketch, "E1335", {"start": v(-2.69, -27.65) * mm, "end": v(-0.54, -25.4) * mm});
            skLineSegment(sketch, "E1336", {"start": v(-0.54, -25.4) * mm, "end": v(-0.42, -26) * mm});
            skLineSegment(sketch, "E1337", {"start": v(-0.42, -26) * mm, "end": v(-0.3, -26.58) * mm});
            skLineSegment(sketch, "E1338", {"start": v(-0.3, -26.58) * mm, "end": v(-0.18, -27.15) * mm});
            skLineSegment(sketch, "E1339", {"start": v(-0.18, -27.15) * mm, "end": v(-0.06, -27.7) * mm});
            skLineSegment(sketch, "E1340", {"start": v(-0.06, -27.7) * mm, "end": v(0.05, -28.23) * mm});
            skLineSegment(sketch, "E1341", {"start": v(0.05, -28.23) * mm, "end": v(0.13, -28.75) * mm});
            skLineSegment(sketch, "E1342", {"start": v(0.13, -28.75) * mm, "end": v(0.2, -29.27) * mm});
            skLineSegment(sketch, "E1343", {"start": v(0.2, -29.27) * mm, "end": v(0.23, -29.79) * mm});
            skLineSegment(sketch, "E1344", {"start": v(0.23, -29.79) * mm, "end": v(0.26, -31.09) * mm});
            skLineSegment(sketch, "E1345", {"start": v(0.26, -31.09) * mm, "end": v(0.28, -32.39) * mm});
            skLineSegment(sketch, "E1346", {"start": v(0.28, -32.39) * mm, "end": v(0.3, -33.69) * mm});
            skLineSegment(sketch, "E1347", {"start": v(0.3, -33.69) * mm, "end": v(0.3, -34.99) * mm});
            skLineSegment(sketch, "E1348", {"start": v(0.3, -34.99) * mm, "end": v(0.3, -36.29) * mm});
            skLineSegment(sketch, "E1349", {"start": v(0.3, -36.29) * mm, "end": v(0.28, -37.59) * mm});
            skLineSegment(sketch, "E1350", {"start": v(0.28, -37.59) * mm, "end": v(0.26, -38.88) * mm});
            skLineSegment(sketch, "E1351", {"start": v(0.26, -38.88) * mm, "end": v(0.24, -40.18) * mm});
            skLineSegment(sketch, "E1352", {"start": v(0.24, -40.18) * mm, "end": v(0.22, -40.63) * mm});
            skLineSegment(sketch, "E1353", {"start": v(0.22, -40.63) * mm, "end": v(0.2, -41.08) * mm});
            skLineSegment(sketch, "E1354", {"start": v(0.2, -41.08) * mm, "end": v(0.15, -41.52) * mm});
            skLineSegment(sketch, "E1355", {"start": v(0.15, -41.52) * mm, "end": v(0.1, -41.97) * mm});
            skLineSegment(sketch, "E1356", {"start": v(0.1, -41.97) * mm, "end": v(0.03, -42.41) * mm});
            skLineSegment(sketch, "E1357", {"start": v(0.03, -42.41) * mm, "end": v(-0.05, -42.86) * mm});
            skLineSegment(sketch, "E1358", {"start": v(-0.05, -42.86) * mm, "end": v(-0.15, -43.3) * mm});
            skLineSegment(sketch, "E1359", {"start": v(-0.15, -43.3) * mm, "end": v(-0.26, -43.72) * mm});
            skLineSegment(sketch, "E1360", {"start": v(-0.26, -43.72) * mm, "end": v(-0.9, -45.35) * mm});
            skLineSegment(sketch, "E1361", {"start": v(-0.9, -45.35) * mm, "end": v(-1.87, -46.71) * mm});
            skLineSegment(sketch, "E1362", {"start": v(-1.87, -46.71) * mm, "end": v(-3.1, -47.8) * mm});
            skLineSegment(sketch, "E1363", {"start": v(-3.1, -47.8) * mm, "end": v(-4.51, -48.6) * mm});
            skLineSegment(sketch, "E1364", {"start": v(-4.51, -48.6) * mm, "end": v(-6.07, -49.06) * mm});
            skLineSegment(sketch, "E1365", {"start": v(-6.07, -49.06) * mm, "end": v(-7.7, -49.16) * mm});
            skLineSegment(sketch, "E1366", {"start": v(-7.7, -49.16) * mm, "end": v(-9.36, -48.9) * mm});
            skLineSegment(sketch, "E1367", {"start": v(-9.36, -48.9) * mm, "end": v(-10.97, -48.21) * mm});
            skLineSegment(sketch, "E1368", {"start": v(-10.97, -48.21) * mm, "end": v(-11.45, -47.92) * mm});
            skLineSegment(sketch, "E1369", {"start": v(-11.45, -47.92) * mm, "end": v(-11.91, -47.6) * mm});
            skLineSegment(sketch, "E1370", {"start": v(-11.91, -47.6) * mm, "end": v(-12.37, -47.27) * mm});
            skLineSegment(sketch, "E1371", {"start": v(-12.37, -47.27) * mm, "end": v(-12.81, -46.91) * mm});
            skLineSegment(sketch, "E1372", {"start": v(-12.81, -46.91) * mm, "end": v(-13.25, -46.55) * mm});
            skLineSegment(sketch, "E1373", {"start": v(-13.25, -46.55) * mm, "end": v(-13.68, -46.18) * mm});
            skLineSegment(sketch, "E1374", {"start": v(-13.68, -46.18) * mm, "end": v(-14.11, -45.8) * mm});
            skLineSegment(sketch, "E1375", {"start": v(-14.11, -45.8) * mm, "end": v(-14.55, -45.44) * mm});
            skLineSegment(sketch, "E1376", {"start": v(-14.55, -45.44) * mm, "end": v(-14.88, -45.14) * mm});
            skLineSegment(sketch, "E1377", {"start": v(-14.88, -45.14) * mm, "end": v(-15.22, -44.85) * mm});
            skLineSegment(sketch, "E1378", {"start": v(-15.22, -44.85) * mm, "end": v(-15.55, -44.54) * mm});
            skLineSegment(sketch, "E1379", {"start": v(-15.55, -44.54) * mm, "end": v(-15.87, -44.22) * mm});
            skLineSegment(sketch, "E1380", {"start": v(-15.87, -44.22) * mm, "end": v(-16.2, -43.9) * mm});
            skLineSegment(sketch, "E1381", {"start": v(-16.2, -43.9) * mm, "end": v(-16.54, -43.58) * mm});
            skLineSegment(sketch, "E1382", {"start": v(-16.54, -43.58) * mm, "end": v(-16.88, -43.25) * mm});
            skLineSegment(sketch, "E1383", {"start": v(-16.88, -43.25) * mm, "end": v(-17.23, -42.92) * mm});
            skLineSegment(sketch, "E1384", {"start": v(107.21, -29.16) * mm, "end": v(107.26, -28.58) * mm});
            skLineSegment(sketch, "E1385", {"start": v(107.26, -28.58) * mm, "end": v(107.3, -28) * mm});
            skLineSegment(sketch, "E1386", {"start": v(107.3, -28) * mm, "end": v(107.32, -27.44) * mm});
            skLineSegment(sketch, "E1387", {"start": v(107.32, -27.44) * mm, "end": v(107.35, -26.89) * mm});
            skLineSegment(sketch, "E1388", {"start": v(107.35, -26.89) * mm, "end": v(107.39, -26.34) * mm});
            skLineSegment(sketch, "E1389", {"start": v(107.39, -26.34) * mm, "end": v(107.45, -25.8) * mm});
            skLineSegment(sketch, "E1390", {"start": v(107.45, -25.8) * mm, "end": v(107.54, -25.28) * mm});
            skLineSegment(sketch, "E1391", {"start": v(107.54, -25.28) * mm, "end": v(107.67, -24.77) * mm});
            skLineSegment(sketch, "E1392", {"start": v(107.67, -24.77) * mm, "end": v(108.02, -23.6) * mm});
            skLineSegment(sketch, "E1393", {"start": v(108.02, -23.6) * mm, "end": v(108.38, -22.42) * mm});
            skLineSegment(sketch, "E1394", {"start": v(108.38, -22.42) * mm, "end": v(108.75, -21.25) * mm});
            skLineSegment(sketch, "E1395", {"start": v(108.75, -21.25) * mm, "end": v(109.14, -20.09) * mm});
            skLineSegment(sketch, "E1396", {"start": v(109.14, -20.09) * mm, "end": v(109.54, -18.93) * mm});
            skLineSegment(sketch, "E1397", {"start": v(109.54, -18.93) * mm, "end": v(109.97, -17.78) * mm});
            skLineSegment(sketch, "E1398", {"start": v(109.97, -17.78) * mm, "end": v(110.42, -16.65) * mm});
            skLineSegment(sketch, "E1399", {"start": v(110.42, -16.65) * mm, "end": v(110.9, -15.53) * mm});
            skLineSegment(sketch, "E1400", {"start": v(110.9, -15.53) * mm, "end": v(111.58, -14.22) * mm});
            skLineSegment(sketch, "E1401", {"start": v(111.58, -14.22) * mm, "end": v(112.38, -13.08) * mm});
            skLineSegment(sketch, "E1402", {"start": v(112.38, -13.08) * mm, "end": v(113.3, -12.1) * mm});
            skLineSegment(sketch, "E1403", {"start": v(113.3, -12.1) * mm, "end": v(114.35, -11.28) * mm});
            skLineSegment(sketch, "E1404", {"start": v(114.35, -11.28) * mm, "end": v(115.5, -10.63) * mm});
            skLineSegment(sketch, "E1405", {"start": v(115.5, -10.63) * mm, "end": v(116.78, -10.15) * mm});
            skLineSegment(sketch, "E1406", {"start": v(116.78, -10.15) * mm, "end": v(118.18, -9.85) * mm});
            skLineSegment(sketch, "E1407", {"start": v(118.18, -9.85) * mm, "end": v(119.68, -9.73) * mm});
            skLineSegment(sketch, "E1408", {"start": v(119.68, -9.73) * mm, "end": v(120.07, -9.75) * mm});
            skLineSegment(sketch, "E1409", {"start": v(120.07, -9.75) * mm, "end": v(120.43, -9.8) * mm});
            skLineSegment(sketch, "E1410", {"start": v(120.43, -9.8) * mm, "end": v(120.78, -9.89) * mm});
            skLineSegment(sketch, "E1411", {"start": v(120.78, -9.89) * mm, "end": v(121.1, -10.02) * mm});
            skLineSegment(sketch, "E1412", {"start": v(121.1, -10.02) * mm, "end": v(121.39, -10.2) * mm});
            skLineSegment(sketch, "E1413", {"start": v(121.39, -10.2) * mm, "end": v(121.65, -10.4) * mm});
            skLineSegment(sketch, "E1414", {"start": v(121.65, -10.4) * mm, "end": v(121.9, -10.67) * mm});
            skLineSegment(sketch, "E1415", {"start": v(121.9, -10.67) * mm, "end": v(122.12, -10.98) * mm});
            skLineSegment(sketch, "E1416", {"start": v(122.12, -10.98) * mm, "end": v(122.6, -11.82) * mm});
            skLineSegment(sketch, "E1417", {"start": v(122.6, -11.82) * mm, "end": v(123, -12.68) * mm});
            skLineSegment(sketch, "E1418", {"start": v(123, -12.68) * mm, "end": v(123.29, -13.55) * mm});
            skLineSegment(sketch, "E1419", {"start": v(123.29, -13.55) * mm, "end": v(123.47, -14.44) * mm});
            skLineSegment(sketch, "E1420", {"start": v(123.47, -14.44) * mm, "end": v(123.53, -15.33) * mm});
            skLineSegment(sketch, "E1421", {"start": v(123.53, -15.33) * mm, "end": v(123.45, -16.23) * mm});
            skLineSegment(sketch, "E1422", {"start": v(123.45, -16.23) * mm, "end": v(123.23, -17.13) * mm});
            skLineSegment(sketch, "E1423", {"start": v(123.23, -17.13) * mm, "end": v(122.84, -18.03) * mm});
            skLineSegment(sketch, "E1424", {"start": v(122.84, -18.03) * mm, "end": v(121.65, -20.1) * mm});
            skLineSegment(sketch, "E1425", {"start": v(121.65, -20.1) * mm, "end": v(120.3, -21.97) * mm});
            skLineSegment(sketch, "E1426", {"start": v(120.3, -21.97) * mm, "end": v(118.8, -23.67) * mm});
            skLineSegment(sketch, "E1427", {"start": v(118.8, -23.67) * mm, "end": v(117.13, -25.17) * mm});
            skLineSegment(sketch, "E1428", {"start": v(117.13, -25.17) * mm, "end": v(115.31, -26.47) * mm});
            skLineSegment(sketch, "E1429", {"start": v(115.31, -26.47) * mm, "end": v(113.33, -27.56) * mm});
            skLineSegment(sketch, "E1430", {"start": v(113.33, -27.56) * mm, "end": v(111.18, -28.44) * mm});
            skLineSegment(sketch, "E1431", {"start": v(111.18, -28.44) * mm, "end": v(108.85, -29.1) * mm});
            skLineSegment(sketch, "E1432", {"start": v(108.85, -29.1) * mm, "end": v(108.75, -29.12) * mm});
            skLineSegment(sketch, "E1433", {"start": v(108.75, -29.12) * mm, "end": v(108.65, -29.13) * mm});
            skLineSegment(sketch, "E1434", {"start": v(108.65, -29.13) * mm, "end": v(108.54, -29.15) * mm});
            skLineSegment(sketch, "E1435", {"start": v(108.54, -29.15) * mm, "end": v(108.44, -29.17) * mm});
            skLineSegment(sketch, "E1436", {"start": v(108.44, -29.17) * mm, "end": v(108.33, -29.18) * mm});
            skLineSegment(sketch, "E1437", {"start": v(108.33, -29.18) * mm, "end": v(108.23, -29.2) * mm});
            skLineSegment(sketch, "E1438", {"start": v(108.23, -29.2) * mm, "end": v(108.13, -29.2) * mm});
            skLineSegment(sketch, "E1439", {"start": v(108.13, -29.2) * mm, "end": v(108.02, -29.2) * mm});
            skLineSegment(sketch, "E1440", {"start": v(108.02, -29.2) * mm, "end": v(107.95, -29.21) * mm});
            skLineSegment(sketch, "E1441", {"start": v(107.95, -29.21) * mm, "end": v(107.87, -29.21) * mm});
            skLineSegment(sketch, "E1442", {"start": v(107.87, -29.21) * mm, "end": v(107.8, -29.2) * mm});
            skLineSegment(sketch, "E1443", {"start": v(107.8, -29.2) * mm, "end": v(107.7, -29.2) * mm});
            skLineSegment(sketch, "E1444", {"start": v(107.7, -29.2) * mm, "end": v(107.6, -29.2) * mm});
            skLineSegment(sketch, "E1445", {"start": v(107.6, -29.2) * mm, "end": v(107.5, -29.18) * mm});
            skLineSegment(sketch, "E1446", {"start": v(107.5, -29.18) * mm, "end": v(107.36, -29.17) * mm});
            skLineSegment(sketch, "E1447", {"start": v(107.36, -29.17) * mm, "end": v(107.21, -29.16) * mm});
            skSolve(sketch);
        }
        {
            var Q0;
            Q0=makeQuery(id+"F0.imprint","IMPRINT",FACE,{"disambiguationData":[TD([[makeQuery(id+"F0.imprint","IMPRINT",EDGE,{"derivedFrom":sQuery(id+"F0.wireOp",EDGE,"E0")}),1.0]])]});
            extrude(context, id + "F1", {"entities" : qUnion([Q0]), "depth" : 20 * mm, "offsetDistance" : 25 * mm});
        }
        {
            var Q0;
            Q0=makeQuery(id+"F1.opExtrude","SWEPT_BODY",BODY,{"disambiguationData":[OSD([sQuery(id+"F0.wireOp",EDGE,"E0"),sQuery(id+"F0.wireOp",EDGE,"E1"),sQuery(id+"F0.wireOp",EDGE,"E2"),sQuery(id+"F0.wireOp",EDGE,"E3"),sQuery(id+"F0.wireOp",EDGE,"E4"),sQuery(id+"F0.wireOp",EDGE,"E5"),sQuery(id+"F0.wireOp",EDGE,"E6"),sQuery(id+"F0.wireOp",EDGE,"E7"),sQuery(id+"F0.wireOp",EDGE,"E8"),sQuery(id+"F0.wireOp",EDGE,"E9"),sQuery(id+"F0.wireOp",EDGE,"E10"),sQuery(id+"F0.wireOp",EDGE,"E11"),sQuery(id+"F0.wireOp",EDGE,"E12"),sQuery(id+"F0.wireOp",EDGE,"E13"),sQuery(id+"F0.wireOp",EDGE,"E14"),sQuery(id+"F0.wireOp",EDGE,"E15"),sQuery(id+"F0.wireOp",EDGE,"E16"),sQuery(id+"F0.wireOp",EDGE,"E17"),sQuery(id+"F0.wireOp",EDGE,"E18"),sQuery(id+"F0.wireOp",EDGE,"E19"),sQuery(id+"F0.wireOp",EDGE,"E20"),sQuery(id+"F0.wireOp",EDGE,"E21"),sQuery(id+"F0.wireOp",EDGE,"E22"),sQuery(id+"F0.wireOp",EDGE,"E23"),sQuery(id+"F0.wireOp",EDGE,"E24"),sQuery(id+"F0.wireOp",EDGE,"E25"),sQuery(id+"F0.wireOp",EDGE,"E26"),sQuery(id+"F0.wireOp",EDGE,"E27"),sQuery(id+"F0.wireOp",EDGE,"E28"),sQuery(id+"F0.wireOp",EDGE,"E29"),sQuery(id+"F0.wireOp",EDGE,"E30"),sQuery(id+"F0.wireOp",EDGE,"E31"),sQuery(id+"F0.wireOp",EDGE,"E32"),sQuery(id+"F0.wireOp",EDGE,"E33"),sQuery(id+"F0.wireOp",EDGE,"E34"),sQuery(id+"F0.wireOp",EDGE,"E35"),sQuery(id+"F0.wireOp",EDGE,"E36"),sQuery(id+"F0.wireOp",EDGE,"E37"),sQuery(id+"F0.wireOp",EDGE,"E38"),sQuery(id+"F0.wireOp",EDGE,"E39"),sQuery(id+"F0.wireOp",EDGE,"E40"),sQuery(id+"F0.wireOp",EDGE,"E41"),sQuery(id+"F0.wireOp",EDGE,"E42"),sQuery(id+"F0.wireOp",EDGE,"E43"),sQuery(id+"F0.wireOp",EDGE,"E44"),sQuery(id+"F0.wireOp",EDGE,"E45"),sQuery(id+"F0.wireOp",EDGE,"E46"),sQuery(id+"F0.wireOp",EDGE,"E47"),sQuery(id+"F0.wireOp",EDGE,"E48"),sQuery(id+"F0.wireOp",EDGE,"E49"),sQuery(id+"F0.wireOp",EDGE,"E50"),sQuery(id+"F0.wireOp",EDGE,"E51"),sQuery(id+"F0.wireOp",EDGE,"E52"),sQuery(id+"F0.wireOp",EDGE,"E53"),sQuery(id+"F0.wireOp",EDGE,"E54"),sQuery(id+"F0.wireOp",EDGE,"E55"),sQuery(id+"F0.wireOp",EDGE,"E56"),sQuery(id+"F0.wireOp",EDGE,"E57"),sQuery(id+"F0.wireOp",EDGE,"E58"),sQuery(id+"F0.wireOp",EDGE,"E59"),sQuery(id+"F0.wireOp",EDGE,"E60"),sQuery(id+"F0.wireOp",EDGE,"E61"),sQuery(id+"F0.wireOp",EDGE,"E62"),sQuery(id+"F0.wireOp",EDGE,"E63"),sQuery(id+"F0.wireOp",EDGE,"E64"),sQuery(id+"F0.wireOp",EDGE,"E65"),sQuery(id+"F0.wireOp",EDGE,"E66"),sQuery(id+"F0.wireOp",EDGE,"E67"),sQuery(id+"F0.wireOp",EDGE,"E68"),sQuery(id+"F0.wireOp",EDGE,"E69"),sQuery(id+"F0.wireOp",EDGE,"E70"),sQuery(id+"F0.wireOp",EDGE,"E71"),sQuery(id+"F0.wireOp",EDGE,"E72"),sQuery(id+"F0.wireOp",EDGE,"E73"),sQuery(id+"F0.wireOp",EDGE,"E74"),sQuery(id+"F0.wireOp",EDGE,"E75"),sQuery(id+"F0.wireOp",EDGE,"E76"),sQuery(id+"F0.wireOp",EDGE,"E77"),sQuery(id+"F0.wireOp",EDGE,"E78"),sQuery(id+"F0.wireOp",EDGE,"E79"),sQuery(id+"F0.wireOp",EDGE,"E80"),sQuery(id+"F0.wireOp",EDGE,"E81"),sQuery(id+"F0.wireOp",EDGE,"E82"),sQuery(id+"F0.wireOp",EDGE,"E83"),sQuery(id+"F0.wireOp",EDGE,"E84"),sQuery(id+"F0.wireOp",EDGE,"E85"),sQuery(id+"F0.wireOp",EDGE,"E86"),sQuery(id+"F0.wireOp",EDGE,"E87"),sQuery(id+"F0.wireOp",EDGE,"E88"),sQuery(id+"F0.wireOp",EDGE,"E89"),sQuery(id+"F0.wireOp",EDGE,"E90"),sQuery(id+"F0.wireOp",EDGE,"E91"),sQuery(id+"F0.wireOp",EDGE,"E92"),sQuery(id+"F0.wireOp",EDGE,"E93"),sQuery(id+"F0.wireOp",EDGE,"E94"),sQuery(id+"F0.wireOp",EDGE,"E95"),sQuery(id+"F0.wireOp",EDGE,"E96"),sQuery(id+"F0.wireOp",EDGE,"E97"),sQuery(id+"F0.wireOp",EDGE,"E98"),sQuery(id+"F0.wireOp",EDGE,"E99"),sQuery(id+"F0.wireOp",EDGE,"E100"),sQuery(id+"F0.wireOp",EDGE,"E101"),sQuery(id+"F0.wireOp",EDGE,"E102"),sQuery(id+"F0.wireOp",EDGE,"E103"),sQuery(id+"F0.wireOp",EDGE,"E104"),sQuery(id+"F0.wireOp",EDGE,"E105"),sQuery(id+"F0.wireOp",EDGE,"E106"),sQuery(id+"F0.wireOp",EDGE,"E107"),sQuery(id+"F0.wireOp",EDGE,"E108"),sQuery(id+"F0.wireOp",EDGE,"E109"),sQuery(id+"F0.wireOp",EDGE,"E110"),sQuery(id+"F0.wireOp",EDGE,"E111"),sQuery(id+"F0.wireOp",EDGE,"E112"),sQuery(id+"F0.wireOp",EDGE,"E113"),sQuery(id+"F0.wireOp",EDGE,"E114"),sQuery(id+"F0.wireOp",EDGE,"E115"),sQuery(id+"F0.wireOp",EDGE,"E116"),sQuery(id+"F0.wireOp",EDGE,"E117"),sQuery(id+"F0.wireOp",EDGE,"E118"),sQuery(id+"F0.wireOp",EDGE,"E119"),sQuery(id+"F0.wireOp",EDGE,"E120"),sQuery(id+"F0.wireOp",EDGE,"E121"),sQuery(id+"F0.wireOp",EDGE,"E122"),sQuery(id+"F0.wireOp",EDGE,"E123"),sQuery(id+"F0.wireOp",EDGE,"E124"),sQuery(id+"F0.wireOp",EDGE,"E125"),sQuery(id+"F0.wireOp",EDGE,"E126"),sQuery(id+"F0.wireOp",EDGE,"E127"),sQuery(id+"F0.wireOp",EDGE,"E128"),sQuery(id+"F0.wireOp",EDGE,"E129"),sQuery(id+"F0.wireOp",EDGE,"E130"),sQuery(id+"F0.wireOp",EDGE,"E131"),sQuery(id+"F0.wireOp",EDGE,"E132"),sQuery(id+"F0.wireOp",EDGE,"E133"),sQuery(id+"F0.wireOp",EDGE,"E134"),sQuery(id+"F0.wireOp",EDGE,"E135"),sQuery(id+"F0.wireOp",EDGE,"E136"),sQuery(id+"F0.wireOp",EDGE,"E137"),sQuery(id+"F0.wireOp",EDGE,"E138"),sQuery(id+"F0.wireOp",EDGE,"E139"),sQuery(id+"F0.wireOp",EDGE,"E140"),sQuery(id+"F0.wireOp",EDGE,"E141"),sQuery(id+"F0.wireOp",EDGE,"E142"),sQuery(id+"F0.wireOp",EDGE,"E143"),sQuery(id+"F0.wireOp",EDGE,"E144"),sQuery(id+"F0.wireOp",EDGE,"E145"),sQuery(id+"F0.wireOp",EDGE,"E146"),sQuery(id+"F0.wireOp",EDGE,"E147"),sQuery(id+"F0.wireOp",EDGE,"E148"),sQuery(id+"F0.wireOp",EDGE,"E149"),sQuery(id+"F0.wireOp",EDGE,"E150"),sQuery(id+"F0.wireOp",EDGE,"E151"),sQuery(id+"F0.wireOp",EDGE,"E152"),sQuery(id+"F0.wireOp",EDGE,"E153"),sQuery(id+"F0.wireOp",EDGE,"E154"),sQuery(id+"F0.wireOp",EDGE,"E155"),sQuery(id+"F0.wireOp",EDGE,"E156"),sQuery(id+"F0.wireOp",EDGE,"E157"),sQuery(id+"F0.wireOp",EDGE,"E158"),sQuery(id+"F0.wireOp",EDGE,"E159"),sQuery(id+"F0.wireOp",EDGE,"E160"),sQuery(id+"F0.wireOp",EDGE,"E161"),sQuery(id+"F0.wireOp",EDGE,"E162"),sQuery(id+"F0.wireOp",EDGE,"E163"),sQuery(id+"F0.wireOp",EDGE,"E164"),sQuery(id+"F0.wireOp",EDGE,"E165"),sQuery(id+"F0.wireOp",EDGE,"E166"),sQuery(id+"F0.wireOp",EDGE,"E167"),sQuery(id+"F0.wireOp",EDGE,"E168"),sQuery(id+"F0.wireOp",EDGE,"E169"),sQuery(id+"F0.wireOp",EDGE,"E170"),sQuery(id+"F0.wireOp",EDGE,"E171"),sQuery(id+"F0.wireOp",EDGE,"E172"),sQuery(id+"F0.wireOp",EDGE,"E173"),sQuery(id+"F0.wireOp",EDGE,"E174"),sQuery(id+"F0.wireOp",EDGE,"E175"),sQuery(id+"F0.wireOp",EDGE,"E176"),sQuery(id+"F0.wireOp",EDGE,"E177"),sQuery(id+"F0.wireOp",EDGE,"E178"),sQuery(id+"F0.wireOp",EDGE,"E179"),sQuery(id+"F0.wireOp",EDGE,"E180"),sQuery(id+"F0.wireOp",EDGE,"E181"),sQuery(id+"F0.wireOp",EDGE,"E182"),sQuery(id+"F0.wireOp",EDGE,"E183"),sQuery(id+"F0.wireOp",EDGE,"E184"),sQuery(id+"F0.wireOp",EDGE,"E185"),sQuery(id+"F0.wireOp",EDGE,"E186"),sQuery(id+"F0.wireOp",EDGE,"E187"),sQuery(id+"F0.wireOp",EDGE,"E188"),sQuery(id+"F0.wireOp",EDGE,"E189"),sQuery(id+"F0.wireOp",EDGE,"E190"),sQuery(id+"F0.wireOp",EDGE,"E191"),sQuery(id+"F0.wireOp",EDGE,"E192"),sQuery(id+"F0.wireOp",EDGE,"E193"),sQuery(id+"F0.wireOp",EDGE,"E194"),sQuery(id+"F0.wireOp",EDGE,"E195"),sQuery(id+"F0.wireOp",EDGE,"E196"),sQuery(id+"F0.wireOp",EDGE,"E197"),sQuery(id+"F0.wireOp",EDGE,"E198"),sQuery(id+"F0.wireOp",EDGE,"E199"),sQuery(id+"F0.wireOp",EDGE,"E200"),sQuery(id+"F0.wireOp",EDGE,"E201"),sQuery(id+"F0.wireOp",EDGE,"E202"),sQuery(id+"F0.wireOp",EDGE,"E203"),sQuery(id+"F0.wireOp",EDGE,"E204"),sQuery(id+"F0.wireOp",EDGE,"E205"),sQuery(id+"F0.wireOp",EDGE,"E206"),sQuery(id+"F0.wireOp",EDGE,"E207"),sQuery(id+"F0.wireOp",EDGE,"E208"),sQuery(id+"F0.wireOp",EDGE,"E209"),sQuery(id+"F0.wireOp",EDGE,"E210"),sQuery(id+"F0.wireOp",EDGE,"E211"),sQuery(id+"F0.wireOp",EDGE,"E212"),sQuery(id+"F0.wireOp",EDGE,"E213"),sQuery(id+"F0.wireOp",EDGE,"E214"),sQuery(id+"F0.wireOp",EDGE,"E215"),sQuery(id+"F0.wireOp",EDGE,"E216"),sQuery(id+"F0.wireOp",EDGE,"E217"),sQuery(id+"F0.wireOp",EDGE,"E218"),sQuery(id+"F0.wireOp",EDGE,"E219"),sQuery(id+"F0.wireOp",EDGE,"E220"),sQuery(id+"F0.wireOp",EDGE,"E221"),sQuery(id+"F0.wireOp",EDGE,"E222"),sQuery(id+"F0.wireOp",EDGE,"E223"),sQuery(id+"F0.wireOp",EDGE,"E224"),sQuery(id+"F0.wireOp",EDGE,"E225"),sQuery(id+"F0.wireOp",EDGE,"E226"),sQuery(id+"F0.wireOp",EDGE,"E227"),sQuery(id+"F0.wireOp",EDGE,"E228"),sQuery(id+"F0.wireOp",EDGE,"E229"),sQuery(id+"F0.wireOp",EDGE,"E230"),sQuery(id+"F0.wireOp",EDGE,"E231"),sQuery(id+"F0.wireOp",EDGE,"E232"),sQuery(id+"F0.wireOp",EDGE,"E233"),sQuery(id+"F0.wireOp",EDGE,"E234"),sQuery(id+"F0.wireOp",EDGE,"E235"),sQuery(id+"F0.wireOp",EDGE,"E236"),sQuery(id+"F0.wireOp",EDGE,"E237"),sQuery(id+"F0.wireOp",EDGE,"E238"),sQuery(id+"F0.wireOp",EDGE,"E239"),sQuery(id+"F0.wireOp",EDGE,"E240"),sQuery(id+"F0.wireOp",EDGE,"E241"),sQuery(id+"F0.wireOp",EDGE,"E242"),sQuery(id+"F0.wireOp",EDGE,"E243"),sQuery(id+"F0.wireOp",EDGE,"E244"),sQuery(id+"F0.wireOp",EDGE,"E245"),sQuery(id+"F0.wireOp",EDGE,"E246"),sQuery(id+"F0.wireOp",EDGE,"E247"),sQuery(id+"F0.wireOp",EDGE,"E248"),sQuery(id+"F0.wireOp",EDGE,"E249"),sQuery(id+"F0.wireOp",EDGE,"E250"),sQuery(id+"F0.wireOp",EDGE,"E251"),sQuery(id+"F0.wireOp",EDGE,"E252"),sQuery(id+"F0.wireOp",EDGE,"E253"),sQuery(id+"F0.wireOp",EDGE,"E254"),sQuery(id+"F0.wireOp",EDGE,"E255"),sQuery(id+"F0.wireOp",EDGE,"E256"),sQuery(id+"F0.wireOp",EDGE,"E257"),sQuery(id+"F0.wireOp",EDGE,"E258"),sQuery(id+"F0.wireOp",EDGE,"E259"),sQuery(id+"F0.wireOp",EDGE,"E260"),sQuery(id+"F0.wireOp",EDGE,"E261"),sQuery(id+"F0.wireOp",EDGE,"E262"),sQuery(id+"F0.wireOp",EDGE,"E263"),sQuery(id+"F0.wireOp",EDGE,"E264"),sQuery(id+"F0.wireOp",EDGE,"E265"),sQuery(id+"F0.wireOp",EDGE,"E266"),sQuery(id+"F0.wireOp",EDGE,"E267"),sQuery(id+"F0.wireOp",EDGE,"E268"),sQuery(id+"F0.wireOp",EDGE,"E269"),sQuery(id+"F0.wireOp",EDGE,"E270"),sQuery(id+"F0.wireOp",EDGE,"E271"),sQuery(id+"F0.wireOp",EDGE,"E272"),sQuery(id+"F0.wireOp",EDGE,"E273"),sQuery(id+"F0.wireOp",EDGE,"E274"),sQuery(id+"F0.wireOp",EDGE,"E275"),sQuery(id+"F0.wireOp",EDGE,"E276"),sQuery(id+"F0.wireOp",EDGE,"E277"),sQuery(id+"F0.wireOp",EDGE,"E278"),sQuery(id+"F0.wireOp",EDGE,"E279"),sQuery(id+"F0.wireOp",EDGE,"E280"),sQuery(id+"F0.wireOp",EDGE,"E281"),sQuery(id+"F0.wireOp",EDGE,"E282"),sQuery(id+"F0.wireOp",EDGE,"E283"),sQuery(id+"F0.wireOp",EDGE,"E284"),sQuery(id+"F0.wireOp",EDGE,"E285"),sQuery(id+"F0.wireOp",EDGE,"E286"),sQuery(id+"F0.wireOp",EDGE,"E287"),sQuery(id+"F0.wireOp",EDGE,"E288"),sQuery(id+"F0.wireOp",EDGE,"E289"),sQuery(id+"F0.wireOp",EDGE,"E290"),sQuery(id+"F0.wireOp",EDGE,"E291"),sQuery(id+"F0.wireOp",EDGE,"E292"),sQuery(id+"F0.wireOp",EDGE,"E293"),sQuery(id+"F0.wireOp",EDGE,"E294"),sQuery(id+"F0.wireOp",EDGE,"E295"),sQuery(id+"F0.wireOp",EDGE,"E296"),sQuery(id+"F0.wireOp",EDGE,"E297"),sQuery(id+"F0.wireOp",EDGE,"E298"),sQuery(id+"F0.wireOp",EDGE,"E299"),sQuery(id+"F0.wireOp",EDGE,"E300"),sQuery(id+"F0.wireOp",EDGE,"E301"),sQuery(id+"F0.wireOp",EDGE,"E302"),sQuery(id+"F0.wireOp",EDGE,"E303"),sQuery(id+"F0.wireOp",EDGE,"E304"),sQuery(id+"F0.wireOp",EDGE,"E305"),sQuery(id+"F0.wireOp",EDGE,"E306"),sQuery(id+"F0.wireOp",EDGE,"E307"),sQuery(id+"F0.wireOp",EDGE,"E308"),sQuery(id+"F0.wireOp",EDGE,"E309"),sQuery(id+"F0.wireOp",EDGE,"E310"),sQuery(id+"F0.wireOp",EDGE,"E311"),sQuery(id+"F0.wireOp",EDGE,"E312"),sQuery(id+"F0.wireOp",EDGE,"E313"),sQuery(id+"F0.wireOp",EDGE,"E314"),sQuery(id+"F0.wireOp",EDGE,"E315"),sQuery(id+"F0.wireOp",EDGE,"E316"),sQuery(id+"F0.wireOp",EDGE,"E317"),sQuery(id+"F0.wireOp",EDGE,"E318"),sQuery(id+"F0.wireOp",EDGE,"E319"),sQuery(id+"F0.wireOp",EDGE,"E320"),sQuery(id+"F0.wireOp",EDGE,"E321"),sQuery(id+"F0.wireOp",EDGE,"E322"),sQuery(id+"F0.wireOp",EDGE,"E323"),sQuery(id+"F0.wireOp",EDGE,"E324"),sQuery(id+"F0.wireOp",EDGE,"E325"),sQuery(id+"F0.wireOp",EDGE,"E326"),sQuery(id+"F0.wireOp",EDGE,"E327"),sQuery(id+"F0.wireOp",EDGE,"E328"),sQuery(id+"F0.wireOp",EDGE,"E329"),sQuery(id+"F0.wireOp",EDGE,"E330"),sQuery(id+"F0.wireOp",EDGE,"E331"),sQuery(id+"F0.wireOp",EDGE,"E332"),sQuery(id+"F0.wireOp",EDGE,"E333"),sQuery(id+"F0.wireOp",EDGE,"E334"),sQuery(id+"F0.wireOp",EDGE,"E335"),sQuery(id+"F0.wireOp",EDGE,"E336"),sQuery(id+"F0.wireOp",EDGE,"E337"),sQuery(id+"F0.wireOp",EDGE,"E338"),sQuery(id+"F0.wireOp",EDGE,"E339"),sQuery(id+"F0.wireOp",EDGE,"E340"),sQuery(id+"F0.wireOp",EDGE,"E341"),sQuery(id+"F0.wireOp",EDGE,"E342"),sQuery(id+"F0.wireOp",EDGE,"E343"),sQuery(id+"F0.wireOp",EDGE,"E344"),sQuery(id+"F0.wireOp",EDGE,"E345"),sQuery(id+"F0.wireOp",EDGE,"E346"),sQuery(id+"F0.wireOp",EDGE,"E347"),sQuery(id+"F0.wireOp",EDGE,"E348"),sQuery(id+"F0.wireOp",EDGE,"E349"),sQuery(id+"F0.wireOp",EDGE,"E350"),sQuery(id+"F0.wireOp",EDGE,"E351"),sQuery(id+"F0.wireOp",EDGE,"E352"),sQuery(id+"F0.wireOp",EDGE,"E353"),sQuery(id+"F0.wireOp",EDGE,"E354"),sQuery(id+"F0.wireOp",EDGE,"E355"),sQuery(id+"F0.wireOp",EDGE,"E356"),sQuery(id+"F0.wireOp",EDGE,"E357"),sQuery(id+"F0.wireOp",EDGE,"E358"),sQuery(id+"F0.wireOp",EDGE,"E359"),sQuery(id+"F0.wireOp",EDGE,"E360"),sQuery(id+"F0.wireOp",EDGE,"E361"),sQuery(id+"F0.wireOp",EDGE,"E362"),sQuery(id+"F0.wireOp",EDGE,"E363"),sQuery(id+"F0.wireOp",EDGE,"E364"),sQuery(id+"F0.wireOp",EDGE,"E365"),sQuery(id+"F0.wireOp",EDGE,"E366"),sQuery(id+"F0.wireOp",EDGE,"E367"),sQuery(id+"F0.wireOp",EDGE,"E368"),sQuery(id+"F0.wireOp",EDGE,"E369"),sQuery(id+"F0.wireOp",EDGE,"E370"),sQuery(id+"F0.wireOp",EDGE,"E371"),sQuery(id+"F0.wireOp",EDGE,"E372"),sQuery(id+"F0.wireOp",EDGE,"E373"),sQuery(id+"F0.wireOp",EDGE,"E374"),sQuery(id+"F0.wireOp",EDGE,"E375"),sQuery(id+"F0.wireOp",EDGE,"E376"),sQuery(id+"F0.wireOp",EDGE,"E377"),sQuery(id+"F0.wireOp",EDGE,"E378"),sQuery(id+"F0.wireOp",EDGE,"E379"),sQuery(id+"F0.wireOp",EDGE,"E380"),sQuery(id+"F0.wireOp",EDGE,"E381"),sQuery(id+"F0.wireOp",EDGE,"E382"),sQuery(id+"F0.wireOp",EDGE,"E383"),sQuery(id+"F0.wireOp",EDGE,"E384"),sQuery(id+"F0.wireOp",EDGE,"E385"),sQuery(id+"F0.wireOp",EDGE,"E386"),sQuery(id+"F0.wireOp",EDGE,"E387"),sQuery(id+"F0.wireOp",EDGE,"E388"),sQuery(id+"F0.wireOp",EDGE,"E389"),sQuery(id+"F0.wireOp",EDGE,"E390"),sQuery(id+"F0.wireOp",EDGE,"E391"),sQuery(id+"F0.wireOp",EDGE,"E392"),sQuery(id+"F0.wireOp",EDGE,"E393"),sQuery(id+"F0.wireOp",EDGE,"E394"),sQuery(id+"F0.wireOp",EDGE,"E395"),sQuery(id+"F0.wireOp",EDGE,"E396"),sQuery(id+"F0.wireOp",EDGE,"E397"),sQuery(id+"F0.wireOp",EDGE,"E398"),sQuery(id+"F0.wireOp",EDGE,"E399"),sQuery(id+"F0.wireOp",EDGE,"E400"),sQuery(id+"F0.wireOp",EDGE,"E401"),sQuery(id+"F0.wireOp",EDGE,"E402"),sQuery(id+"F0.wireOp",EDGE,"E403"),sQuery(id+"F0.wireOp",EDGE,"E404"),sQuery(id+"F0.wireOp",EDGE,"E405"),sQuery(id+"F0.wireOp",EDGE,"E406"),sQuery(id+"F0.wireOp",EDGE,"E407"),sQuery(id+"F0.wireOp",EDGE,"E408"),sQuery(id+"F0.wireOp",EDGE,"E409"),sQuery(id+"F0.wireOp",EDGE,"E410"),sQuery(id+"F0.wireOp",EDGE,"E411"),sQuery(id+"F0.wireOp",EDGE,"E412"),sQuery(id+"F0.wireOp",EDGE,"E413"),sQuery(id+"F0.wireOp",EDGE,"E414"),sQuery(id+"F0.wireOp",EDGE,"E415"),sQuery(id+"F0.wireOp",EDGE,"E416"),sQuery(id+"F0.wireOp",EDGE,"E417"),sQuery(id+"F0.wireOp",EDGE,"E418"),sQuery(id+"F0.wireOp",EDGE,"E419"),sQuery(id+"F0.wireOp",EDGE,"E420"),sQuery(id+"F0.wireOp",EDGE,"E421"),sQuery(id+"F0.wireOp",EDGE,"E422"),sQuery(id+"F0.wireOp",EDGE,"E423"),sQuery(id+"F0.wireOp",EDGE,"E424"),sQuery(id+"F0.wireOp",EDGE,"E425"),sQuery(id+"F0.wireOp",EDGE,"E426"),sQuery(id+"F0.wireOp",EDGE,"E427"),sQuery(id+"F0.wireOp",EDGE,"E428"),sQuery(id+"F0.wireOp",EDGE,"E429"),sQuery(id+"F0.wireOp",EDGE,"E430"),sQuery(id+"F0.wireOp",EDGE,"E431"),sQuery(id+"F0.wireOp",EDGE,"E432"),sQuery(id+"F0.wireOp",EDGE,"E433"),sQuery(id+"F0.wireOp",EDGE,"E434"),sQuery(id+"F0.wireOp",EDGE,"E435"),sQuery(id+"F0.wireOp",EDGE,"E436"),sQuery(id+"F0.wireOp",EDGE,"E437"),sQuery(id+"F0.wireOp",EDGE,"E438"),sQuery(id+"F0.wireOp",EDGE,"E439"),sQuery(id+"F0.wireOp",EDGE,"E440"),sQuery(id+"F0.wireOp",EDGE,"E441"),sQuery(id+"F0.wireOp",EDGE,"E442"),sQuery(id+"F0.wireOp",EDGE,"E443"),sQuery(id+"F0.wireOp",EDGE,"E444"),sQuery(id+"F0.wireOp",EDGE,"E445"),sQuery(id+"F0.wireOp",EDGE,"E446"),sQuery(id+"F0.wireOp",EDGE,"E447"),sQuery(id+"F0.wireOp",EDGE,"E448"),sQuery(id+"F0.wireOp",EDGE,"E449"),sQuery(id+"F0.wireOp",EDGE,"E450"),sQuery(id+"F0.wireOp",EDGE,"E451"),sQuery(id+"F0.wireOp",EDGE,"E452"),sQuery(id+"F0.wireOp",EDGE,"E453"),sQuery(id+"F0.wireOp",EDGE,"E454"),sQuery(id+"F0.wireOp",EDGE,"E455"),sQuery(id+"F0.wireOp",EDGE,"E456"),sQuery(id+"F0.wireOp",EDGE,"E457"),sQuery(id+"F0.wireOp",EDGE,"E458"),sQuery(id+"F0.wireOp",EDGE,"E459"),sQuery(id+"F0.wireOp",EDGE,"E460"),sQuery(id+"F0.wireOp",EDGE,"E461"),sQuery(id+"F0.wireOp",EDGE,"E462"),sQuery(id+"F0.wireOp",EDGE,"E463"),sQuery(id+"F0.wireOp",EDGE,"E464"),sQuery(id+"F0.wireOp",EDGE,"E465"),sQuery(id+"F0.wireOp",EDGE,"E466"),sQuery(id+"F0.wireOp",EDGE,"E467"),sQuery(id+"F0.wireOp",EDGE,"E468"),sQuery(id+"F0.wireOp",EDGE,"E469"),sQuery(id+"F0.wireOp",EDGE,"E470"),sQuery(id+"F0.wireOp",EDGE,"E471"),sQuery(id+"F0.wireOp",EDGE,"E472"),sQuery(id+"F0.wireOp",EDGE,"E473"),sQuery(id+"F0.wireOp",EDGE,"E474"),sQuery(id+"F0.wireOp",EDGE,"E475"),sQuery(id+"F0.wireOp",EDGE,"E476"),sQuery(id+"F0.wireOp",EDGE,"E477"),sQuery(id+"F0.wireOp",EDGE,"E478"),sQuery(id+"F0.wireOp",EDGE,"E479"),sQuery(id+"F0.wireOp",EDGE,"E480"),sQuery(id+"F0.wireOp",EDGE,"E481"),sQuery(id+"F0.wireOp",EDGE,"E482"),sQuery(id+"F0.wireOp",EDGE,"E483"),sQuery(id+"F0.wireOp",EDGE,"E484"),sQuery(id+"F0.wireOp",EDGE,"E485"),sQuery(id+"F0.wireOp",EDGE,"E486"),sQuery(id+"F0.wireOp",EDGE,"E487"),sQuery(id+"F0.wireOp",EDGE,"E488"),sQuery(id+"F0.wireOp",EDGE,"E489"),sQuery(id+"F0.wireOp",EDGE,"E490"),sQuery(id+"F0.wireOp",EDGE,"E491"),sQuery(id+"F0.wireOp",EDGE,"E492"),sQuery(id+"F0.wireOp",EDGE,"E493"),sQuery(id+"F0.wireOp",EDGE,"E494"),sQuery(id+"F0.wireOp",EDGE,"E495"),sQuery(id+"F0.wireOp",EDGE,"E496"),sQuery(id+"F0.wireOp",EDGE,"E497"),sQuery(id+"F0.wireOp",EDGE,"E498"),sQuery(id+"F0.wireOp",EDGE,"E499"),sQuery(id+"F0.wireOp",EDGE,"E500"),sQuery(id+"F0.wireOp",EDGE,"E501"),sQuery(id+"F0.wireOp",EDGE,"E502"),sQuery(id+"F0.wireOp",EDGE,"E503"),sQuery(id+"F0.wireOp",EDGE,"E504"),sQuery(id+"F0.wireOp",EDGE,"E505"),sQuery(id+"F0.wireOp",EDGE,"E506"),sQuery(id+"F0.wireOp",EDGE,"E507"),sQuery(id+"F0.wireOp",EDGE,"E508"),sQuery(id+"F0.wireOp",EDGE,"E509"),sQuery(id+"F0.wireOp",EDGE,"E510"),sQuery(id+"F0.wireOp",EDGE,"E511"),sQuery(id+"F0.wireOp",EDGE,"E512"),sQuery(id+"F0.wireOp",EDGE,"E513"),sQuery(id+"F0.wireOp",EDGE,"E514"),sQuery(id+"F0.wireOp",EDGE,"E515"),sQuery(id+"F0.wireOp",EDGE,"E516"),sQuery(id+"F0.wireOp",EDGE,"E517"),sQuery(id+"F0.wireOp",EDGE,"E518"),sQuery(id+"F0.wireOp",EDGE,"E519"),sQuery(id+"F0.wireOp",EDGE,"E520"),sQuery(id+"F0.wireOp",EDGE,"E521"),sQuery(id+"F0.wireOp",EDGE,"E522"),sQuery(id+"F0.wireOp",EDGE,"E523"),sQuery(id+"F0.wireOp",EDGE,"E524"),sQuery(id+"F0.wireOp",EDGE,"E525"),sQuery(id+"F0.wireOp",EDGE,"E526"),sQuery(id+"F0.wireOp",EDGE,"E527"),sQuery(id+"F0.wireOp",EDGE,"E528"),sQuery(id+"F0.wireOp",EDGE,"E529"),sQuery(id+"F0.wireOp",EDGE,"E530"),sQuery(id+"F0.wireOp",EDGE,"E531"),sQuery(id+"F0.wireOp",EDGE,"E532"),sQuery(id+"F0.wireOp",EDGE,"E533"),sQuery(id+"F0.wireOp",EDGE,"E534"),sQuery(id+"F0.wireOp",EDGE,"E535"),sQuery(id+"F0.wireOp",EDGE,"E536"),sQuery(id+"F0.wireOp",EDGE,"E537"),sQuery(id+"F0.wireOp",EDGE,"E538"),sQuery(id+"F0.wireOp",EDGE,"E539"),sQuery(id+"F0.wireOp",EDGE,"E540"),sQuery(id+"F0.wireOp",EDGE,"E541"),sQuery(id+"F0.wireOp",EDGE,"E542"),sQuery(id+"F0.wireOp",EDGE,"E543"),sQuery(id+"F0.wireOp",EDGE,"E544"),sQuery(id+"F0.wireOp",EDGE,"E545"),sQuery(id+"F0.wireOp",EDGE,"E546"),sQuery(id+"F0.wireOp",EDGE,"E547"),sQuery(id+"F0.wireOp",EDGE,"E548"),sQuery(id+"F0.wireOp",EDGE,"E549"),sQuery(id+"F0.wireOp",EDGE,"E550"),sQuery(id+"F0.wireOp",EDGE,"E551"),sQuery(id+"F0.wireOp",EDGE,"E552"),sQuery(id+"F0.wireOp",EDGE,"E553"),sQuery(id+"F0.wireOp",EDGE,"E554"),sQuery(id+"F0.wireOp",EDGE,"E555"),sQuery(id+"F0.wireOp",EDGE,"E556"),sQuery(id+"F0.wireOp",EDGE,"E557"),sQuery(id+"F0.wireOp",EDGE,"E558"),sQuery(id+"F0.wireOp",EDGE,"E559"),sQuery(id+"F0.wireOp",EDGE,"E560"),sQuery(id+"F0.wireOp",EDGE,"E561"),sQuery(id+"F0.wireOp",EDGE,"E562"),sQuery(id+"F0.wireOp",EDGE,"E563"),sQuery(id+"F0.wireOp",EDGE,"E564"),sQuery(id+"F0.wireOp",EDGE,"E565"),sQuery(id+"F0.wireOp",EDGE,"E566"),sQuery(id+"F0.wireOp",EDGE,"E567"),sQuery(id+"F0.wireOp",EDGE,"E568"),sQuery(id+"F0.wireOp",EDGE,"E569"),sQuery(id+"F0.wireOp",EDGE,"E570"),sQuery(id+"F0.wireOp",EDGE,"E571"),sQuery(id+"F0.wireOp",EDGE,"E572"),sQuery(id+"F0.wireOp",EDGE,"E573"),sQuery(id+"F0.wireOp",EDGE,"E574"),sQuery(id+"F0.wireOp",EDGE,"E575"),sQuery(id+"F0.wireOp",EDGE,"E576"),sQuery(id+"F0.wireOp",EDGE,"E577"),sQuery(id+"F0.wireOp",EDGE,"E578"),sQuery(id+"F0.wireOp",EDGE,"E579"),sQuery(id+"F0.wireOp",EDGE,"E580"),sQuery(id+"F0.wireOp",EDGE,"E581"),sQuery(id+"F0.wireOp",EDGE,"E582"),sQuery(id+"F0.wireOp",EDGE,"E583"),sQuery(id+"F0.wireOp",EDGE,"E584"),sQuery(id+"F0.wireOp",EDGE,"E585"),sQuery(id+"F0.wireOp",EDGE,"E586"),sQuery(id+"F0.wireOp",EDGE,"E587"),sQuery(id+"F0.wireOp",EDGE,"E588"),sQuery(id+"F0.wireOp",EDGE,"E589"),sQuery(id+"F0.wireOp",EDGE,"E590"),sQuery(id+"F0.wireOp",EDGE,"E591"),sQuery(id+"F0.wireOp",EDGE,"E592"),sQuery(id+"F0.wireOp",EDGE,"E593"),sQuery(id+"F0.wireOp",EDGE,"E594"),sQuery(id+"F0.wireOp",EDGE,"E595"),sQuery(id+"F0.wireOp",EDGE,"E596"),sQuery(id+"F0.wireOp",EDGE,"E597"),sQuery(id+"F0.wireOp",EDGE,"E598"),sQuery(id+"F0.wireOp",EDGE,"E599"),sQuery(id+"F0.wireOp",EDGE,"E600"),sQuery(id+"F0.wireOp",EDGE,"E601"),sQuery(id+"F0.wireOp",EDGE,"E602"),sQuery(id+"F0.wireOp",EDGE,"E603"),sQuery(id+"F0.wireOp",EDGE,"E604"),sQuery(id+"F0.wireOp",EDGE,"E605"),sQuery(id+"F0.wireOp",EDGE,"E606"),sQuery(id+"F0.wireOp",EDGE,"E607"),sQuery(id+"F0.wireOp",EDGE,"E608"),sQuery(id+"F0.wireOp",EDGE,"E609"),sQuery(id+"F0.wireOp",EDGE,"E610"),sQuery(id+"F0.wireOp",EDGE,"E611"),sQuery(id+"F0.wireOp",EDGE,"E612"),sQuery(id+"F0.wireOp",EDGE,"E613"),sQuery(id+"F0.wireOp",EDGE,"E614"),sQuery(id+"F0.wireOp",EDGE,"E615"),sQuery(id+"F0.wireOp",EDGE,"E616"),sQuery(id+"F0.wireOp",EDGE,"E617"),sQuery(id+"F0.wireOp",EDGE,"E618"),sQuery(id+"F0.wireOp",EDGE,"E619"),sQuery(id+"F0.wireOp",EDGE,"E620"),sQuery(id+"F0.wireOp",EDGE,"E621"),sQuery(id+"F0.wireOp",EDGE,"E622"),sQuery(id+"F0.wireOp",EDGE,"E623"),sQuery(id+"F0.wireOp",EDGE,"E624"),sQuery(id+"F0.wireOp",EDGE,"E625"),sQuery(id+"F0.wireOp",EDGE,"E626"),sQuery(id+"F0.wireOp",EDGE,"E627"),sQuery(id+"F0.wireOp",EDGE,"E628"),sQuery(id+"F0.wireOp",EDGE,"E629"),sQuery(id+"F0.wireOp",EDGE,"E630"),sQuery(id+"F0.wireOp",EDGE,"E631"),sQuery(id+"F0.wireOp",EDGE,"E632"),sQuery(id+"F0.wireOp",EDGE,"E633"),sQuery(id+"F0.wireOp",EDGE,"E634"),sQuery(id+"F0.wireOp",EDGE,"E635"),sQuery(id+"F0.wireOp",EDGE,"E636"),sQuery(id+"F0.wireOp",EDGE,"E637"),sQuery(id+"F0.wireOp",EDGE,"E638"),sQuery(id+"F0.wireOp",EDGE,"E639"),sQuery(id+"F0.wireOp",EDGE,"E640"),sQuery(id+"F0.wireOp",EDGE,"E641"),sQuery(id+"F0.wireOp",EDGE,"E642"),sQuery(id+"F0.wireOp",EDGE,"E643"),sQuery(id+"F0.wireOp",EDGE,"E644"),sQuery(id+"F0.wireOp",EDGE,"E645"),sQuery(id+"F0.wireOp",EDGE,"E646"),sQuery(id+"F0.wireOp",EDGE,"E647"),sQuery(id+"F0.wireOp",EDGE,"E648"),sQuery(id+"F0.wireOp",EDGE,"E649"),sQuery(id+"F0.wireOp",EDGE,"E650"),sQuery(id+"F0.wireOp",EDGE,"E651"),sQuery(id+"F0.wireOp",EDGE,"E652"),sQuery(id+"F0.wireOp",EDGE,"E653"),sQuery(id+"F0.wireOp",EDGE,"E654"),sQuery(id+"F0.wireOp",EDGE,"E655"),sQuery(id+"F0.wireOp",EDGE,"E656"),sQuery(id+"F0.wireOp",EDGE,"E657"),sQuery(id+"F0.wireOp",EDGE,"E658"),sQuery(id+"F0.wireOp",EDGE,"E659"),sQuery(id+"F0.wireOp",EDGE,"E660"),sQuery(id+"F0.wireOp",EDGE,"E661"),sQuery(id+"F0.wireOp",EDGE,"E662"),sQuery(id+"F0.wireOp",EDGE,"E663"),sQuery(id+"F0.wireOp",EDGE,"E664"),sQuery(id+"F0.wireOp",EDGE,"E665"),sQuery(id+"F0.wireOp",EDGE,"E666"),sQuery(id+"F0.wireOp",EDGE,"E667"),sQuery(id+"F0.wireOp",EDGE,"E668"),sQuery(id+"F0.wireOp",EDGE,"E669"),sQuery(id+"F0.wireOp",EDGE,"E670"),sQuery(id+"F0.wireOp",EDGE,"E671"),sQuery(id+"F0.wireOp",EDGE,"E672"),sQuery(id+"F0.wireOp",EDGE,"E673"),sQuery(id+"F0.wireOp",EDGE,"E674"),sQuery(id+"F0.wireOp",EDGE,"E675"),sQuery(id+"F0.wireOp",EDGE,"E676"),sQuery(id+"F0.wireOp",EDGE,"E677"),sQuery(id+"F0.wireOp",EDGE,"E678"),sQuery(id+"F0.wireOp",EDGE,"E679"),sQuery(id+"F0.wireOp",EDGE,"E680"),sQuery(id+"F0.wireOp",EDGE,"E681"),sQuery(id+"F0.wireOp",EDGE,"E682"),sQuery(id+"F0.wireOp",EDGE,"E683"),sQuery(id+"F0.wireOp",EDGE,"E684"),sQuery(id+"F0.wireOp",EDGE,"E685"),sQuery(id+"F0.wireOp",EDGE,"E686"),sQuery(id+"F0.wireOp",EDGE,"E687"),sQuery(id+"F0.wireOp",EDGE,"E688"),sQuery(id+"F0.wireOp",EDGE,"E689"),sQuery(id+"F0.wireOp",EDGE,"E690"),sQuery(id+"F0.wireOp",EDGE,"E691"),sQuery(id+"F0.wireOp",EDGE,"E692"),sQuery(id+"F0.wireOp",EDGE,"E693"),sQuery(id+"F0.wireOp",EDGE,"E694"),sQuery(id+"F0.wireOp",EDGE,"E695"),sQuery(id+"F0.wireOp",EDGE,"E696"),sQuery(id+"F0.wireOp",EDGE,"E697"),sQuery(id+"F0.wireOp",EDGE,"E698"),sQuery(id+"F0.wireOp",EDGE,"E699"),sQuery(id+"F0.wireOp",EDGE,"E700"),sQuery(id+"F0.wireOp",EDGE,"E701"),sQuery(id+"F0.wireOp",EDGE,"E702"),sQuery(id+"F0.wireOp",EDGE,"E703"),sQuery(id+"F0.wireOp",EDGE,"E704"),sQuery(id+"F0.wireOp",EDGE,"E705"),sQuery(id+"F0.wireOp",EDGE,"E706"),sQuery(id+"F0.wireOp",EDGE,"E707"),sQuery(id+"F0.wireOp",EDGE,"E708"),sQuery(id+"F0.wireOp",EDGE,"E709"),sQuery(id+"F0.wireOp",EDGE,"E710"),sQuery(id+"F0.wireOp",EDGE,"E711"),sQuery(id+"F0.wireOp",EDGE,"E712"),sQuery(id+"F0.wireOp",EDGE,"E713"),sQuery(id+"F0.wireOp",EDGE,"E714"),sQuery(id+"F0.wireOp",EDGE,"E715"),sQuery(id+"F0.wireOp",EDGE,"E716"),sQuery(id+"F0.wireOp",EDGE,"E717"),sQuery(id+"F0.wireOp",EDGE,"E718"),sQuery(id+"F0.wireOp",EDGE,"E719"),sQuery(id+"F0.wireOp",EDGE,"E720"),sQuery(id+"F0.wireOp",EDGE,"E721"),sQuery(id+"F0.wireOp",EDGE,"E722"),sQuery(id+"F0.wireOp",EDGE,"E723"),sQuery(id+"F0.wireOp",EDGE,"E724"),sQuery(id+"F0.wireOp",EDGE,"E725"),sQuery(id+"F0.wireOp",EDGE,"E726"),sQuery(id+"F0.wireOp",EDGE,"E727"),sQuery(id+"F0.wireOp",EDGE,"E728"),sQuery(id+"F0.wireOp",EDGE,"E729"),sQuery(id+"F0.wireOp",EDGE,"E730"),sQuery(id+"F0.wireOp",EDGE,"E731"),sQuery(id+"F0.wireOp",EDGE,"E732"),sQuery(id+"F0.wireOp",EDGE,"E733"),sQuery(id+"F0.wireOp",EDGE,"E734"),sQuery(id+"F0.wireOp",EDGE,"E735"),sQuery(id+"F0.wireOp",EDGE,"E736"),sQuery(id+"F0.wireOp",EDGE,"E737"),sQuery(id+"F0.wireOp",EDGE,"E738"),sQuery(id+"F0.wireOp",EDGE,"E739"),sQuery(id+"F0.wireOp",EDGE,"E740"),sQuery(id+"F0.wireOp",EDGE,"E741"),sQuery(id+"F0.wireOp",EDGE,"E742"),sQuery(id+"F0.wireOp",EDGE,"E743"),sQuery(id+"F0.wireOp",EDGE,"E744"),sQuery(id+"F0.wireOp",EDGE,"E745"),sQuery(id+"F0.wireOp",EDGE,"E746"),sQuery(id+"F0.wireOp",EDGE,"E747"),sQuery(id+"F0.wireOp",EDGE,"E748"),sQuery(id+"F0.wireOp",EDGE,"E749"),sQuery(id+"F0.wireOp",EDGE,"E750"),sQuery(id+"F0.wireOp",EDGE,"E751"),sQuery(id+"F0.wireOp",EDGE,"E752"),sQuery(id+"F0.wireOp",EDGE,"E753"),sQuery(id+"F0.wireOp",EDGE,"E754"),sQuery(id+"F0.wireOp",EDGE,"E755"),sQuery(id+"F0.wireOp",EDGE,"E756"),sQuery(id+"F0.wireOp",EDGE,"E757"),sQuery(id+"F0.wireOp",EDGE,"E758"),sQuery(id+"F0.wireOp",EDGE,"E759"),sQuery(id+"F0.wireOp",EDGE,"E760"),sQuery(id+"F0.wireOp",EDGE,"E761"),sQuery(id+"F0.wireOp",EDGE,"E762"),sQuery(id+"F0.wireOp",EDGE,"E763"),sQuery(id+"F0.wireOp",EDGE,"E764"),sQuery(id+"F0.wireOp",EDGE,"E765"),sQuery(id+"F0.wireOp",EDGE,"E766"),sQuery(id+"F0.wireOp",EDGE,"E767"),sQuery(id+"F0.wireOp",EDGE,"E768"),sQuery(id+"F0.wireOp",EDGE,"E769"),sQuery(id+"F0.wireOp",EDGE,"E770"),sQuery(id+"F0.wireOp",EDGE,"E771"),sQuery(id+"F0.wireOp",EDGE,"E772"),sQuery(id+"F0.wireOp",EDGE,"E773"),sQuery(id+"F0.wireOp",EDGE,"E774"),sQuery(id+"F0.wireOp",EDGE,"E775"),sQuery(id+"F0.wireOp",EDGE,"E776"),sQuery(id+"F0.wireOp",EDGE,"E777"),sQuery(id+"F0.wireOp",EDGE,"E778"),sQuery(id+"F0.wireOp",EDGE,"E779"),sQuery(id+"F0.wireOp",EDGE,"E780"),sQuery(id+"F0.wireOp",EDGE,"E781"),sQuery(id+"F0.wireOp",EDGE,"E782"),sQuery(id+"F0.wireOp",EDGE,"E783"),sQuery(id+"F0.wireOp",EDGE,"E784"),sQuery(id+"F0.wireOp",EDGE,"E785"),sQuery(id+"F0.wireOp",EDGE,"E786"),sQuery(id+"F0.wireOp",EDGE,"E787"),sQuery(id+"F0.wireOp",EDGE,"E788"),sQuery(id+"F0.wireOp",EDGE,"E789"),sQuery(id+"F0.wireOp",EDGE,"E790"),sQuery(id+"F0.wireOp",EDGE,"E791"),sQuery(id+"F0.wireOp",EDGE,"E792"),sQuery(id+"F0.wireOp",EDGE,"E793"),sQuery(id+"F0.wireOp",EDGE,"E794"),sQuery(id+"F0.wireOp",EDGE,"E795"),sQuery(id+"F0.wireOp",EDGE,"E796"),sQuery(id+"F0.wireOp",EDGE,"E797"),sQuery(id+"F0.wireOp",EDGE,"E798"),sQuery(id+"F0.wireOp",EDGE,"E799"),sQuery(id+"F0.wireOp",EDGE,"E800"),sQuery(id+"F0.wireOp",EDGE,"E801"),sQuery(id+"F0.wireOp",EDGE,"E802"),sQuery(id+"F0.wireOp",EDGE,"E803"),sQuery(id+"F0.wireOp",EDGE,"E804"),sQuery(id+"F0.wireOp",EDGE,"E805"),sQuery(id+"F0.wireOp",EDGE,"E806"),sQuery(id+"F0.wireOp",EDGE,"E807"),sQuery(id+"F0.wireOp",EDGE,"E808"),sQuery(id+"F0.wireOp",EDGE,"E809"),sQuery(id+"F0.wireOp",EDGE,"E810"),sQuery(id+"F0.wireOp",EDGE,"E811"),sQuery(id+"F0.wireOp",EDGE,"E812"),sQuery(id+"F0.wireOp",EDGE,"E813"),sQuery(id+"F0.wireOp",EDGE,"E814"),sQuery(id+"F0.wireOp",EDGE,"E815"),sQuery(id+"F0.wireOp",EDGE,"E816"),sQuery(id+"F0.wireOp",EDGE,"E817"),sQuery(id+"F0.wireOp",EDGE,"E818"),sQuery(id+"F0.wireOp",EDGE,"E819"),sQuery(id+"F0.wireOp",EDGE,"E820"),sQuery(id+"F0.wireOp",EDGE,"E821"),sQuery(id+"F0.wireOp",EDGE,"E822"),sQuery(id+"F0.wireOp",EDGE,"E823"),sQuery(id+"F0.wireOp",EDGE,"E824"),sQuery(id+"F0.wireOp",EDGE,"E825"),sQuery(id+"F0.wireOp",EDGE,"E826"),sQuery(id+"F0.wireOp",EDGE,"E827"),sQuery(id+"F0.wireOp",EDGE,"E828"),sQuery(id+"F0.wireOp",EDGE,"E829"),sQuery(id+"F0.wireOp",EDGE,"E830"),sQuery(id+"F0.wireOp",EDGE,"E831"),sQuery(id+"F0.wireOp",EDGE,"E832"),sQuery(id+"F0.wireOp",EDGE,"E833"),sQuery(id+"F0.wireOp",EDGE,"E834"),sQuery(id+"F0.wireOp",EDGE,"E835"),sQuery(id+"F0.wireOp",EDGE,"E836"),sQuery(id+"F0.wireOp",EDGE,"E837"),sQuery(id+"F0.wireOp",EDGE,"E838"),sQuery(id+"F0.wireOp",EDGE,"E839"),sQuery(id+"F0.wireOp",EDGE,"E840"),sQuery(id+"F0.wireOp",EDGE,"E841"),sQuery(id+"F0.wireOp",EDGE,"E842"),sQuery(id+"F0.wireOp",EDGE,"E843"),sQuery(id+"F0.wireOp",EDGE,"E844"),sQuery(id+"F0.wireOp",EDGE,"E845"),sQuery(id+"F0.wireOp",EDGE,"E846"),sQuery(id+"F0.wireOp",EDGE,"E847"),sQuery(id+"F0.wireOp",EDGE,"E848"),sQuery(id+"F0.wireOp",EDGE,"E849"),sQuery(id+"F0.wireOp",EDGE,"E850"),sQuery(id+"F0.wireOp",EDGE,"E851"),sQuery(id+"F0.wireOp",EDGE,"E852"),sQuery(id+"F0.wireOp",EDGE,"E853"),sQuery(id+"F0.wireOp",EDGE,"E854"),sQuery(id+"F0.wireOp",EDGE,"E855"),sQuery(id+"F0.wireOp",EDGE,"E856"),sQuery(id+"F0.wireOp",EDGE,"E857"),sQuery(id+"F0.wireOp",EDGE,"E858"),sQuery(id+"F0.wireOp",EDGE,"E859"),sQuery(id+"F0.wireOp",EDGE,"E860"),sQuery(id+"F0.wireOp",EDGE,"E861"),sQuery(id+"F0.wireOp",EDGE,"E862"),sQuery(id+"F0.wireOp",EDGE,"E863"),sQuery(id+"F0.wireOp",EDGE,"E864"),sQuery(id+"F0.wireOp",EDGE,"E865"),sQuery(id+"F0.wireOp",EDGE,"E866"),sQuery(id+"F0.wireOp",EDGE,"E867"),sQuery(id+"F0.wireOp",EDGE,"E868"),sQuery(id+"F0.wireOp",EDGE,"E869"),sQuery(id+"F0.wireOp",EDGE,"E870"),sQuery(id+"F0.wireOp",EDGE,"E871"),sQuery(id+"F0.wireOp",EDGE,"E872"),sQuery(id+"F0.wireOp",EDGE,"E873"),sQuery(id+"F0.wireOp",EDGE,"E874"),sQuery(id+"F0.wireOp",EDGE,"E875"),sQuery(id+"F0.wireOp",EDGE,"E876"),sQuery(id+"F0.wireOp",EDGE,"E877"),sQuery(id+"F0.wireOp",EDGE,"E878"),sQuery(id+"F0.wireOp",EDGE,"E879"),sQuery(id+"F0.wireOp",EDGE,"E880"),sQuery(id+"F0.wireOp",EDGE,"E881"),sQuery(id+"F0.wireOp",EDGE,"E882"),sQuery(id+"F0.wireOp",EDGE,"E883"),sQuery(id+"F0.wireOp",EDGE,"E884"),sQuery(id+"F0.wireOp",EDGE,"E885"),sQuery(id+"F0.wireOp",EDGE,"E886"),sQuery(id+"F0.wireOp",EDGE,"E887"),sQuery(id+"F0.wireOp",EDGE,"E888"),sQuery(id+"F0.wireOp",EDGE,"E889"),sQuery(id+"F0.wireOp",EDGE,"E890"),sQuery(id+"F0.wireOp",EDGE,"E891"),sQuery(id+"F0.wireOp",EDGE,"E892"),sQuery(id+"F0.wireOp",EDGE,"E893"),sQuery(id+"F0.wireOp",EDGE,"E894"),sQuery(id+"F0.wireOp",EDGE,"E895"),sQuery(id+"F0.wireOp",EDGE,"E896"),sQuery(id+"F0.wireOp",EDGE,"E897"),sQuery(id+"F0.wireOp",EDGE,"E898"),sQuery(id+"F0.wireOp",EDGE,"E899"),sQuery(id+"F0.wireOp",EDGE,"E900"),sQuery(id+"F0.wireOp",EDGE,"E901"),sQuery(id+"F0.wireOp",EDGE,"E902"),sQuery(id+"F0.wireOp",EDGE,"E903"),sQuery(id+"F0.wireOp",EDGE,"E904"),sQuery(id+"F0.wireOp",EDGE,"E905"),sQuery(id+"F0.wireOp",EDGE,"E906"),sQuery(id+"F0.wireOp",EDGE,"E907"),sQuery(id+"F0.wireOp",EDGE,"E908"),sQuery(id+"F0.wireOp",EDGE,"E909"),sQuery(id+"F0.wireOp",EDGE,"E910"),sQuery(id+"F0.wireOp",EDGE,"E911"),sQuery(id+"F0.wireOp",EDGE,"E912"),sQuery(id+"F0.wireOp",EDGE,"E913"),sQuery(id+"F0.wireOp",EDGE,"E914"),sQuery(id+"F0.wireOp",EDGE,"E915"),sQuery(id+"F0.wireOp",EDGE,"E916"),sQuery(id+"F0.wireOp",EDGE,"E917"),sQuery(id+"F0.wireOp",EDGE,"E918"),sQuery(id+"F0.wireOp",EDGE,"E919"),sQuery(id+"F0.wireOp",EDGE,"E920"),sQuery(id+"F0.wireOp",EDGE,"E921"),sQuery(id+"F0.wireOp",EDGE,"E922"),sQuery(id+"F0.wireOp",EDGE,"E923"),sQuery(id+"F0.wireOp",EDGE,"E924"),sQuery(id+"F0.wireOp",EDGE,"E925"),sQuery(id+"F0.wireOp",EDGE,"E926"),sQuery(id+"F0.wireOp",EDGE,"E927"),sQuery(id+"F0.wireOp",EDGE,"E928"),sQuery(id+"F0.wireOp",EDGE,"E929"),sQuery(id+"F0.wireOp",EDGE,"E930"),sQuery(id+"F0.wireOp",EDGE,"E931"),sQuery(id+"F0.wireOp",EDGE,"E932"),sQuery(id+"F0.wireOp",EDGE,"E933"),sQuery(id+"F0.wireOp",EDGE,"E934"),sQuery(id+"F0.wireOp",EDGE,"E935"),sQuery(id+"F0.wireOp",EDGE,"E936"),sQuery(id+"F0.wireOp",EDGE,"E937"),sQuery(id+"F0.wireOp",EDGE,"E938"),sQuery(id+"F0.wireOp",EDGE,"E939"),sQuery(id+"F0.wireOp",EDGE,"E940"),sQuery(id+"F0.wireOp",EDGE,"E941"),sQuery(id+"F0.wireOp",EDGE,"E942"),sQuery(id+"F0.wireOp",EDGE,"E943"),sQuery(id+"F0.wireOp",EDGE,"E944"),sQuery(id+"F0.wireOp",EDGE,"E945"),sQuery(id+"F0.wireOp",EDGE,"E946"),sQuery(id+"F0.wireOp",EDGE,"E947"),sQuery(id+"F0.wireOp",EDGE,"E948"),sQuery(id+"F0.wireOp",EDGE,"E949"),sQuery(id+"F0.wireOp",EDGE,"E950"),sQuery(id+"F0.wireOp",EDGE,"E951"),sQuery(id+"F0.wireOp",EDGE,"E952"),sQuery(id+"F0.wireOp",EDGE,"E953"),sQuery(id+"F0.wireOp",EDGE,"E954"),sQuery(id+"F0.wireOp",EDGE,"E955"),sQuery(id+"F0.wireOp",EDGE,"E956"),sQuery(id+"F0.wireOp",EDGE,"E957"),sQuery(id+"F0.wireOp",EDGE,"E958"),sQuery(id+"F0.wireOp",EDGE,"E959"),sQuery(id+"F0.wireOp",EDGE,"E960"),sQuery(id+"F0.wireOp",EDGE,"E961"),sQuery(id+"F0.wireOp",EDGE,"E962"),sQuery(id+"F0.wireOp",EDGE,"E963"),sQuery(id+"F0.wireOp",EDGE,"E964"),sQuery(id+"F0.wireOp",EDGE,"E965"),sQuery(id+"F0.wireOp",EDGE,"E966"),sQuery(id+"F0.wireOp",EDGE,"E967"),sQuery(id+"F0.wireOp",EDGE,"E968"),sQuery(id+"F0.wireOp",EDGE,"E969"),sQuery(id+"F0.wireOp",EDGE,"E970"),sQuery(id+"F0.wireOp",EDGE,"E971"),sQuery(id+"F0.wireOp",EDGE,"E972"),sQuery(id+"F0.wireOp",EDGE,"E973"),sQuery(id+"F0.wireOp",EDGE,"E974"),sQuery(id+"F0.wireOp",EDGE,"E975"),sQuery(id+"F0.wireOp",EDGE,"E976"),sQuery(id+"F0.wireOp",EDGE,"E977"),sQuery(id+"F0.wireOp",EDGE,"E978"),sQuery(id+"F0.wireOp",EDGE,"E979"),sQuery(id+"F0.wireOp",EDGE,"E980"),sQuery(id+"F0.wireOp",EDGE,"E981"),sQuery(id+"F0.wireOp",EDGE,"E982"),sQuery(id+"F0.wireOp",EDGE,"E983"),sQuery(id+"F0.wireOp",EDGE,"E984"),sQuery(id+"F0.wireOp",EDGE,"E985"),sQuery(id+"F0.wireOp",EDGE,"E986"),sQuery(id+"F0.wireOp",EDGE,"E987"),sQuery(id+"F0.wireOp",EDGE,"E988"),sQuery(id+"F0.wireOp",EDGE,"E989"),sQuery(id+"F0.wireOp",EDGE,"E990"),sQuery(id+"F0.wireOp",EDGE,"E991"),sQuery(id+"F0.wireOp",EDGE,"E992"),sQuery(id+"F0.wireOp",EDGE,"E993"),sQuery(id+"F0.wireOp",EDGE,"E994"),sQuery(id+"F0.wireOp",EDGE,"E995"),sQuery(id+"F0.wireOp",EDGE,"E996"),sQuery(id+"F0.wireOp",EDGE,"E997"),sQuery(id+"F0.wireOp",EDGE,"E998"),sQuery(id+"F0.wireOp",EDGE,"E999"),sQuery(id+"F0.wireOp",EDGE,"E1000"),sQuery(id+"F0.wireOp",EDGE,"E1001"),sQuery(id+"F0.wireOp",EDGE,"E1002"),sQuery(id+"F0.wireOp",EDGE,"E1003"),sQuery(id+"F0.wireOp",EDGE,"E1004"),sQuery(id+"F0.wireOp",EDGE,"E1005"),sQuery(id+"F0.wireOp",EDGE,"E1006"),sQuery(id+"F0.wireOp",EDGE,"E1007"),sQuery(id+"F0.wireOp",EDGE,"E1008"),sQuery(id+"F0.wireOp",EDGE,"E1009"),sQuery(id+"F0.wireOp",EDGE,"E1010"),sQuery(id+"F0.wireOp",EDGE,"E1011"),sQuery(id+"F0.wireOp",EDGE,"E1012"),sQuery(id+"F0.wireOp",EDGE,"E1013"),sQuery(id+"F0.wireOp",EDGE,"E1014"),sQuery(id+"F0.wireOp",EDGE,"E1015"),sQuery(id+"F0.wireOp",EDGE,"E1016"),sQuery(id+"F0.wireOp",EDGE,"E1017"),sQuery(id+"F0.wireOp",EDGE,"E1018"),sQuery(id+"F0.wireOp",EDGE,"E1019"),sQuery(id+"F0.wireOp",EDGE,"E1020"),sQuery(id+"F0.wireOp",EDGE,"E1021"),sQuery(id+"F0.wireOp",EDGE,"E1022"),sQuery(id+"F0.wireOp",EDGE,"E1023"),sQuery(id+"F0.wireOp",EDGE,"E1024"),sQuery(id+"F0.wireOp",EDGE,"E1025"),sQuery(id+"F0.wireOp",EDGE,"E1026"),sQuery(id+"F0.wireOp",EDGE,"E1027"),sQuery(id+"F0.wireOp",EDGE,"E1028"),sQuery(id+"F0.wireOp",EDGE,"E1029"),sQuery(id+"F0.wireOp",EDGE,"E1030"),sQuery(id+"F0.wireOp",EDGE,"E1031"),sQuery(id+"F0.wireOp",EDGE,"E1032"),sQuery(id+"F0.wireOp",EDGE,"E1033"),sQuery(id+"F0.wireOp",EDGE,"E1034"),sQuery(id+"F0.wireOp",EDGE,"E1035"),sQuery(id+"F0.wireOp",EDGE,"E1036"),sQuery(id+"F0.wireOp",EDGE,"E1037"),sQuery(id+"F0.wireOp",EDGE,"E1038"),sQuery(id+"F0.wireOp",EDGE,"E1039"),sQuery(id+"F0.wireOp",EDGE,"E1040"),sQuery(id+"F0.wireOp",EDGE,"E1041"),sQuery(id+"F0.wireOp",EDGE,"E1042"),sQuery(id+"F0.wireOp",EDGE,"E1043"),sQuery(id+"F0.wireOp",EDGE,"E1044"),sQuery(id+"F0.wireOp",EDGE,"E1045"),sQuery(id+"F0.wireOp",EDGE,"E1046"),sQuery(id+"F0.wireOp",EDGE,"E1047"),sQuery(id+"F0.wireOp",EDGE,"E1048"),sQuery(id+"F0.wireOp",EDGE,"E1049"),sQuery(id+"F0.wireOp",EDGE,"E1050"),sQuery(id+"F0.wireOp",EDGE,"E1051"),sQuery(id+"F0.wireOp",EDGE,"E1052"),sQuery(id+"F0.wireOp",EDGE,"E1053"),sQuery(id+"F0.wireOp",EDGE,"E1054"),sQuery(id+"F0.wireOp",EDGE,"E1055"),sQuery(id+"F0.wireOp",EDGE,"E1056"),sQuery(id+"F0.wireOp",EDGE,"E1057"),sQuery(id+"F0.wireOp",EDGE,"E1058"),sQuery(id+"F0.wireOp",EDGE,"E1059"),sQuery(id+"F0.wireOp",EDGE,"E1060"),sQuery(id+"F0.wireOp",EDGE,"E1061"),sQuery(id+"F0.wireOp",EDGE,"E1062"),sQuery(id+"F0.wireOp",EDGE,"E1063"),sQuery(id+"F0.wireOp",EDGE,"E1064"),sQuery(id+"F0.wireOp",EDGE,"E1065"),sQuery(id+"F0.wireOp",EDGE,"E1066"),sQuery(id+"F0.wireOp",EDGE,"E1067"),sQuery(id+"F0.wireOp",EDGE,"E1068"),sQuery(id+"F0.wireOp",EDGE,"E1069"),sQuery(id+"F0.wireOp",EDGE,"E1070"),sQuery(id+"F0.wireOp",EDGE,"E1071"),sQuery(id+"F0.wireOp",EDGE,"E1072"),sQuery(id+"F0.wireOp",EDGE,"E1073"),sQuery(id+"F0.wireOp",EDGE,"E1074"),sQuery(id+"F0.wireOp",EDGE,"E1075"),sQuery(id+"F0.wireOp",EDGE,"E1076"),sQuery(id+"F0.wireOp",EDGE,"E1077"),sQuery(id+"F0.wireOp",EDGE,"E1078"),sQuery(id+"F0.wireOp",EDGE,"E1079"),sQuery(id+"F0.wireOp",EDGE,"E1080"),sQuery(id+"F0.wireOp",EDGE,"E1081"),sQuery(id+"F0.wireOp",EDGE,"E1082"),sQuery(id+"F0.wireOp",EDGE,"E1083"),sQuery(id+"F0.wireOp",EDGE,"E1084"),sQuery(id+"F0.wireOp",EDGE,"E1085"),sQuery(id+"F0.wireOp",EDGE,"E1086"),sQuery(id+"F0.wireOp",EDGE,"E1087"),sQuery(id+"F0.wireOp",EDGE,"E1088"),sQuery(id+"F0.wireOp",EDGE,"E1089"),sQuery(id+"F0.wireOp",EDGE,"E1090"),sQuery(id+"F0.wireOp",EDGE,"E1091"),sQuery(id+"F0.wireOp",EDGE,"E1092"),sQuery(id+"F0.wireOp",EDGE,"E1093"),sQuery(id+"F0.wireOp",EDGE,"E1094"),sQuery(id+"F0.wireOp",EDGE,"E1095"),sQuery(id+"F0.wireOp",EDGE,"E1096"),sQuery(id+"F0.wireOp",EDGE,"E1097"),sQuery(id+"F0.wireOp",EDGE,"E1098"),sQuery(id+"F0.wireOp",EDGE,"E1099"),sQuery(id+"F0.wireOp",EDGE,"E1100"),sQuery(id+"F0.wireOp",EDGE,"E1101"),sQuery(id+"F0.wireOp",EDGE,"E1102"),sQuery(id+"F0.wireOp",EDGE,"E1103"),sQuery(id+"F0.wireOp",EDGE,"E1104"),sQuery(id+"F0.wireOp",EDGE,"E1105"),sQuery(id+"F0.wireOp",EDGE,"E1106"),sQuery(id+"F0.wireOp",EDGE,"E1107"),sQuery(id+"F0.wireOp",EDGE,"E1108"),sQuery(id+"F0.wireOp",EDGE,"E1109"),sQuery(id+"F0.wireOp",EDGE,"E1110"),sQuery(id+"F0.wireOp",EDGE,"E1111"),sQuery(id+"F0.wireOp",EDGE,"E1112"),sQuery(id+"F0.wireOp",EDGE,"E1113"),sQuery(id+"F0.wireOp",EDGE,"E1114"),sQuery(id+"F0.wireOp",EDGE,"E1115"),sQuery(id+"F0.wireOp",EDGE,"E1116"),sQuery(id+"F0.wireOp",EDGE,"E1117"),sQuery(id+"F0.wireOp",EDGE,"E1118"),sQuery(id+"F0.wireOp",EDGE,"E1119"),sQuery(id+"F0.wireOp",EDGE,"E1120"),sQuery(id+"F0.wireOp",EDGE,"E1121"),sQuery(id+"F0.wireOp",EDGE,"E1122"),sQuery(id+"F0.wireOp",EDGE,"E1123"),sQuery(id+"F0.wireOp",EDGE,"E1124"),sQuery(id+"F0.wireOp",EDGE,"E1125"),sQuery(id+"F0.wireOp",EDGE,"E1126"),sQuery(id+"F0.wireOp",EDGE,"E1127"),sQuery(id+"F0.wireOp",EDGE,"E1128"),sQuery(id+"F0.wireOp",EDGE,"E1129"),sQuery(id+"F0.wireOp",EDGE,"E1130"),sQuery(id+"F0.wireOp",EDGE,"E1131"),sQuery(id+"F0.wireOp",EDGE,"E1132"),sQuery(id+"F0.wireOp",EDGE,"E1133"),sQuery(id+"F0.wireOp",EDGE,"E1134"),sQuery(id+"F0.wireOp",EDGE,"E1135"),sQuery(id+"F0.wireOp",EDGE,"E1136"),sQuery(id+"F0.wireOp",EDGE,"E1137"),sQuery(id+"F0.wireOp",EDGE,"E1138"),sQuery(id+"F0.wireOp",EDGE,"E1139"),sQuery(id+"F0.wireOp",EDGE,"E1140"),sQuery(id+"F0.wireOp",EDGE,"E1141"),sQuery(id+"F0.wireOp",EDGE,"E1142"),sQuery(id+"F0.wireOp",EDGE,"E1143"),sQuery(id+"F0.wireOp",EDGE,"E1144"),sQuery(id+"F0.wireOp",EDGE,"E1145"),sQuery(id+"F0.wireOp",EDGE,"E1146"),sQuery(id+"F0.wireOp",EDGE,"E1147"),sQuery(id+"F0.wireOp",EDGE,"E1148"),sQuery(id+"F0.wireOp",EDGE,"E1149"),sQuery(id+"F0.wireOp",EDGE,"E1150"),sQuery(id+"F0.wireOp",EDGE,"E1151"),sQuery(id+"F0.wireOp",EDGE,"E1152"),sQuery(id+"F0.wireOp",EDGE,"E1153"),sQuery(id+"F0.wireOp",EDGE,"E1154"),sQuery(id+"F0.wireOp",EDGE,"E1155"),sQuery(id+"F0.wireOp",EDGE,"E1156"),sQuery(id+"F0.wireOp",EDGE,"E1157"),sQuery(id+"F0.wireOp",EDGE,"E1158"),sQuery(id+"F0.wireOp",EDGE,"E1159"),sQuery(id+"F0.wireOp",EDGE,"E1160"),sQuery(id+"F0.wireOp",EDGE,"E1161"),sQuery(id+"F0.wireOp",EDGE,"E1162"),sQuery(id+"F0.wireOp",EDGE,"E1163"),sQuery(id+"F0.wireOp",EDGE,"E1164"),sQuery(id+"F0.wireOp",EDGE,"E1165"),sQuery(id+"F0.wireOp",EDGE,"E1166"),sQuery(id+"F0.wireOp",EDGE,"E1167"),sQuery(id+"F0.wireOp",EDGE,"E1168"),sQuery(id+"F0.wireOp",EDGE,"E1169"),sQuery(id+"F0.wireOp",EDGE,"E1170"),sQuery(id+"F0.wireOp",EDGE,"E1171"),sQuery(id+"F0.wireOp",EDGE,"E1172"),sQuery(id+"F0.wireOp",EDGE,"E1173"),sQuery(id+"F0.wireOp",EDGE,"E1174"),sQuery(id+"F0.wireOp",EDGE,"E1175"),sQuery(id+"F0.wireOp",EDGE,"E1176"),sQuery(id+"F0.wireOp",EDGE,"E1177"),sQuery(id+"F0.wireOp",EDGE,"E1178"),sQuery(id+"F0.wireOp",EDGE,"E1179"),sQuery(id+"F0.wireOp",EDGE,"E1180"),sQuery(id+"F0.wireOp",EDGE,"E1181"),sQuery(id+"F0.wireOp",EDGE,"E1182"),sQuery(id+"F0.wireOp",EDGE,"E1183"),sQuery(id+"F0.wireOp",EDGE,"E1184"),sQuery(id+"F0.wireOp",EDGE,"E1185"),sQuery(id+"F0.wireOp",EDGE,"E1186"),sQuery(id+"F0.wireOp",EDGE,"E1187"),sQuery(id+"F0.wireOp",EDGE,"E1188"),sQuery(id+"F0.wireOp",EDGE,"E1189"),sQuery(id+"F0.wireOp",EDGE,"E1190"),sQuery(id+"F0.wireOp",EDGE,"E1191"),sQuery(id+"F0.wireOp",EDGE,"E1192"),sQuery(id+"F0.wireOp",EDGE,"E1193"),sQuery(id+"F0.wireOp",EDGE,"E1194"),sQuery(id+"F0.wireOp",EDGE,"E1195"),sQuery(id+"F0.wireOp",EDGE,"E1196"),sQuery(id+"F0.wireOp",EDGE,"E1197"),sQuery(id+"F0.wireOp",EDGE,"E1198"),sQuery(id+"F0.wireOp",EDGE,"E1199"),sQuery(id+"F0.wireOp",EDGE,"E1200"),sQuery(id+"F0.wireOp",EDGE,"E1201"),sQuery(id+"F0.wireOp",EDGE,"E1202"),sQuery(id+"F0.wireOp",EDGE,"E1203"),sQuery(id+"F0.wireOp",EDGE,"E1204"),sQuery(id+"F0.wireOp",EDGE,"E1205"),sQuery(id+"F0.wireOp",EDGE,"E1206"),sQuery(id+"F0.wireOp",EDGE,"E1207"),sQuery(id+"F0.wireOp",EDGE,"E1208"),sQuery(id+"F0.wireOp",EDGE,"E1209"),sQuery(id+"F0.wireOp",EDGE,"E1210"),sQuery(id+"F0.wireOp",EDGE,"E1211"),sQuery(id+"F0.wireOp",EDGE,"E1212"),sQuery(id+"F0.wireOp",EDGE,"E1213"),sQuery(id+"F0.wireOp",EDGE,"E1214"),sQuery(id+"F0.wireOp",EDGE,"E1215"),sQuery(id+"F0.wireOp",EDGE,"E1216"),sQuery(id+"F0.wireOp",EDGE,"E1217"),sQuery(id+"F0.wireOp",EDGE,"E1218"),sQuery(id+"F0.wireOp",EDGE,"E1219"),sQuery(id+"F0.wireOp",EDGE,"E1220"),sQuery(id+"F0.wireOp",EDGE,"E1221"),sQuery(id+"F0.wireOp",EDGE,"E1222"),sQuery(id+"F0.wireOp",EDGE,"E1223"),sQuery(id+"F0.wireOp",EDGE,"E1224"),sQuery(id+"F0.wireOp",EDGE,"E1225"),sQuery(id+"F0.wireOp",EDGE,"E1226"),sQuery(id+"F0.wireOp",EDGE,"E1227"),sQuery(id+"F0.wireOp",EDGE,"E1228"),sQuery(id+"F0.wireOp",EDGE,"E1229"),sQuery(id+"F0.wireOp",EDGE,"E1230"),sQuery(id+"F0.wireOp",EDGE,"E1231"),sQuery(id+"F0.wireOp",EDGE,"E1232"),sQuery(id+"F0.wireOp",EDGE,"E1233"),sQuery(id+"F0.wireOp",EDGE,"E1234"),sQuery(id+"F0.wireOp",EDGE,"E1235"),sQuery(id+"F0.wireOp",EDGE,"E1236"),sQuery(id+"F0.wireOp",EDGE,"E1237"),sQuery(id+"F0.wireOp",EDGE,"E1238"),sQuery(id+"F0.wireOp",EDGE,"E1239"),sQuery(id+"F0.wireOp",EDGE,"E1240"),sQuery(id+"F0.wireOp",EDGE,"E1241"),sQuery(id+"F0.wireOp",EDGE,"E1242"),sQuery(id+"F0.wireOp",EDGE,"E1243"),sQuery(id+"F0.wireOp",EDGE,"E1244"),sQuery(id+"F0.wireOp",EDGE,"E1245"),sQuery(id+"F0.wireOp",EDGE,"E1246"),sQuery(id+"F0.wireOp",EDGE,"E1247"),sQuery(id+"F0.wireOp",EDGE,"E1248"),sQuery(id+"F0.wireOp",EDGE,"E1249"),sQuery(id+"F0.wireOp",EDGE,"E1250"),sQuery(id+"F0.wireOp",EDGE,"E1251"),sQuery(id+"F0.wireOp",EDGE,"E1252"),sQuery(id+"F0.wireOp",EDGE,"E1253"),sQuery(id+"F0.wireOp",EDGE,"E1254"),sQuery(id+"F0.wireOp",EDGE,"E1255"),sQuery(id+"F0.wireOp",EDGE,"E1256"),sQuery(id+"F0.wireOp",EDGE,"E1257"),sQuery(id+"F0.wireOp",EDGE,"E1258"),sQuery(id+"F0.wireOp",EDGE,"E1259"),sQuery(id+"F0.wireOp",EDGE,"E1260"),sQuery(id+"F0.wireOp",EDGE,"E1261"),sQuery(id+"F0.wireOp",EDGE,"E1262"),sQuery(id+"F0.wireOp",EDGE,"E1263"),sQuery(id+"F0.wireOp",EDGE,"E1264"),sQuery(id+"F0.wireOp",EDGE,"E1265"),sQuery(id+"F0.wireOp",EDGE,"E1266"),sQuery(id+"F0.wireOp",EDGE,"E1267"),sQuery(id+"F0.wireOp",EDGE,"E1268"),sQuery(id+"F0.wireOp",EDGE,"E1269"),sQuery(id+"F0.wireOp",EDGE,"E1270"),sQuery(id+"F0.wireOp",EDGE,"E1271"),sQuery(id+"F0.wireOp",EDGE,"E1272"),sQuery(id+"F0.wireOp",EDGE,"E1273"),sQuery(id+"F0.wireOp",EDGE,"E1274"),sQuery(id+"F0.wireOp",EDGE,"E1275"),sQuery(id+"F0.wireOp",EDGE,"E1276"),sQuery(id+"F0.wireOp",EDGE,"E1277"),sQuery(id+"F0.wireOp",EDGE,"E1278"),sQuery(id+"F0.wireOp",EDGE,"E1279"),sQuery(id+"F0.wireOp",EDGE,"E1280"),sQuery(id+"F0.wireOp",EDGE,"E1281"),sQuery(id+"F0.wireOp",EDGE,"E1282"),sQuery(id+"F0.wireOp",EDGE,"E1283"),sQuery(id+"F0.wireOp",EDGE,"E1284"),sQuery(id+"F0.wireOp",EDGE,"E1285"),sQuery(id+"F0.wireOp",EDGE,"E1286"),sQuery(id+"F0.wireOp",EDGE,"E1287"),sQuery(id+"F0.wireOp",EDGE,"E1288"),sQuery(id+"F0.wireOp",EDGE,"E1289"),sQuery(id+"F0.wireOp",EDGE,"E1290"),sQuery(id+"F0.wireOp",EDGE,"E1291"),sQuery(id+"F0.wireOp",EDGE,"E1292"),sQuery(id+"F0.wireOp",EDGE,"E1293"),sQuery(id+"F0.wireOp",EDGE,"E1294"),sQuery(id+"F0.wireOp",EDGE,"E1295"),sQuery(id+"F0.wireOp",EDGE,"E1296"),sQuery(id+"F0.wireOp",EDGE,"E1297"),sQuery(id+"F0.wireOp",EDGE,"E1298"),sQuery(id+"F0.wireOp",EDGE,"E1299"),sQuery(id+"F0.wireOp",EDGE,"E1300"),sQuery(id+"F0.wireOp",EDGE,"E1301"),sQuery(id+"F0.wireOp",EDGE,"E1302"),sQuery(id+"F0.wireOp",EDGE,"E1303"),sQuery(id+"F0.wireOp",EDGE,"E1304"),sQuery(id+"F0.wireOp",EDGE,"E1305"),sQuery(id+"F0.wireOp",EDGE,"E1306"),sQuery(id+"F0.wireOp",EDGE,"E1307"),sQuery(id+"F0.wireOp",EDGE,"E1308"),sQuery(id+"F0.wireOp",EDGE,"E1309"),sQuery(id+"F0.wireOp",EDGE,"E1310"),sQuery(id+"F0.wireOp",EDGE,"E1311"),sQuery(id+"F0.wireOp",EDGE,"E1312"),sQuery(id+"F0.wireOp",EDGE,"E1313"),sQuery(id+"F0.wireOp",EDGE,"E1314"),sQuery(id+"F0.wireOp",EDGE,"E1315"),sQuery(id+"F0.wireOp",EDGE,"E1316"),sQuery(id+"F0.wireOp",EDGE,"E1317"),sQuery(id+"F0.wireOp",EDGE,"E1318"),sQuery(id+"F0.wireOp",EDGE,"E1319"),sQuery(id+"F0.wireOp",EDGE,"E1320"),sQuery(id+"F0.wireOp",EDGE,"E1321"),sQuery(id+"F0.wireOp",EDGE,"E1322"),sQuery(id+"F0.wireOp",EDGE,"E1323"),sQuery(id+"F0.wireOp",EDGE,"E1324"),sQuery(id+"F0.wireOp",EDGE,"E1325"),sQuery(id+"F0.wireOp",EDGE,"E1326"),sQuery(id+"F0.wireOp",EDGE,"E1327"),sQuery(id+"F0.wireOp",EDGE,"E1328"),sQuery(id+"F0.wireOp",EDGE,"E1329"),sQuery(id+"F0.wireOp",EDGE,"E1330"),sQuery(id+"F0.wireOp",EDGE,"E1331"),sQuery(id+"F0.wireOp",EDGE,"E1332"),sQuery(id+"F0.wireOp",EDGE,"E1333"),sQuery(id+"F0.wireOp",EDGE,"E1334"),sQuery(id+"F0.wireOp",EDGE,"E1335"),sQuery(id+"F0.wireOp",EDGE,"E1336"),sQuery(id+"F0.wireOp",EDGE,"E1337"),sQuery(id+"F0.wireOp",EDGE,"E1338"),sQuery(id+"F0.wireOp",EDGE,"E1339"),sQuery(id+"F0.wireOp",EDGE,"E1340"),sQuery(id+"F0.wireOp",EDGE,"E1341"),sQuery(id+"F0.wireOp",EDGE,"E1342"),sQuery(id+"F0.wireOp",EDGE,"E1343"),sQuery(id+"F0.wireOp",EDGE,"E1344"),sQuery(id+"F0.wireOp",EDGE,"E1345"),sQuery(id+"F0.wireOp",EDGE,"E1346"),sQuery(id+"F0.wireOp",EDGE,"E1347"),sQuery(id+"F0.wireOp",EDGE,"E1348"),sQuery(id+"F0.wireOp",EDGE,"E1349"),sQuery(id+"F0.wireOp",EDGE,"E1350"),sQuery(id+"F0.wireOp",EDGE,"E1351"),sQuery(id+"F0.wireOp",EDGE,"E1352"),sQuery(id+"F0.wireOp",EDGE,"E1353"),sQuery(id+"F0.wireOp",EDGE,"E1354"),sQuery(id+"F0.wireOp",EDGE,"E1355"),sQuery(id+"F0.wireOp",EDGE,"E1356"),sQuery(id+"F0.wireOp",EDGE,"E1357"),sQuery(id+"F0.wireOp",EDGE,"E1358"),sQuery(id+"F0.wireOp",EDGE,"E1359"),sQuery(id+"F0.wireOp",EDGE,"E1360"),sQuery(id+"F0.wireOp",EDGE,"E1361"),sQuery(id+"F0.wireOp",EDGE,"E1362"),sQuery(id+"F0.wireOp",EDGE,"E1363"),sQuery(id+"F0.wireOp",EDGE,"E1364"),sQuery(id+"F0.wireOp",EDGE,"E1365"),sQuery(id+"F0.wireOp",EDGE,"E1366"),sQuery(id+"F0.wireOp",EDGE,"E1367"),sQuery(id+"F0.wireOp",EDGE,"E1368"),sQuery(id+"F0.wireOp",EDGE,"E1369"),sQuery(id+"F0.wireOp",EDGE,"E1370"),sQuery(id+"F0.wireOp",EDGE,"E1371"),sQuery(id+"F0.wireOp",EDGE,"E1372"),sQuery(id+"F0.wireOp",EDGE,"E1373"),sQuery(id+"F0.wireOp",EDGE,"E1374"),sQuery(id+"F0.wireOp",EDGE,"E1375"),sQuery(id+"F0.wireOp",EDGE,"E1376"),sQuery(id+"F0.wireOp",EDGE,"E1377"),sQuery(id+"F0.wireOp",EDGE,"E1378"),sQuery(id+"F0.wireOp",EDGE,"E1379"),sQuery(id+"F0.wireOp",EDGE,"E1380"),sQuery(id+"F0.wireOp",EDGE,"E1381"),sQuery(id+"F0.wireOp",EDGE,"E1382"),sQuery(id+"F0.wireOp",EDGE,"E1383"),sQuery(id+"F0.wireOp",EDGE,"E1384"),sQuery(id+"F0.wireOp",EDGE,"E1385"),sQuery(id+"F0.wireOp",EDGE,"E1386"),sQuery(id+"F0.wireOp",EDGE,"E1387"),sQuery(id+"F0.wireOp",EDGE,"E1388"),sQuery(id+"F0.wireOp",EDGE,"E1389"),sQuery(id+"F0.wireOp",EDGE,"E1390"),sQuery(id+"F0.wireOp",EDGE,"E1391"),sQuery(id+"F0.wireOp",EDGE,"E1392"),sQuery(id+"F0.wireOp",EDGE,"E1393"),sQuery(id+"F0.wireOp",EDGE,"E1394"),sQuery(id+"F0.wireOp",EDGE,"E1395"),sQuery(id+"F0.wireOp",EDGE,"E1396"),sQuery(id+"F0.wireOp",EDGE,"E1397"),sQuery(id+"F0.wireOp",EDGE,"E1398"),sQuery(id+"F0.wireOp",EDGE,"E1399"),sQuery(id+"F0.wireOp",EDGE,"E1400"),sQuery(id+"F0.wireOp",EDGE,"E1401"),sQuery(id+"F0.wireOp",EDGE,"E1402"),sQuery(id+"F0.wireOp",EDGE,"E1403"),sQuery(id+"F0.wireOp",EDGE,"E1404"),sQuery(id+"F0.wireOp",EDGE,"E1405"),sQuery(id+"F0.wireOp",EDGE,"E1406"),sQuery(id+"F0.wireOp",EDGE,"E1407"),sQuery(id+"F0.wireOp",EDGE,"E1408"),sQuery(id+"F0.wireOp",EDGE,"E1409"),sQuery(id+"F0.wireOp",EDGE,"E1410"),sQuery(id+"F0.wireOp",EDGE,"E1411"),sQuery(id+"F0.wireOp",EDGE,"E1412"),sQuery(id+"F0.wireOp",EDGE,"E1413"),sQuery(id+"F0.wireOp",EDGE,"E1414"),sQuery(id+"F0.wireOp",EDGE,"E1415"),sQuery(id+"F0.wireOp",EDGE,"E1416"),sQuery(id+"F0.wireOp",EDGE,"E1417"),sQuery(id+"F0.wireOp",EDGE,"E1418"),sQuery(id+"F0.wireOp",EDGE,"E1419"),sQuery(id+"F0.wireOp",EDGE,"E1420"),sQuery(id+"F0.wireOp",EDGE,"E1421"),sQuery(id+"F0.wireOp",EDGE,"E1422"),sQuery(id+"F0.wireOp",EDGE,"E1423"),sQuery(id+"F0.wireOp",EDGE,"E1424"),sQuery(id+"F0.wireOp",EDGE,"E1425"),sQuery(id+"F0.wireOp",EDGE,"E1426"),sQuery(id+"F0.wireOp",EDGE,"E1427"),sQuery(id+"F0.wireOp",EDGE,"E1428"),sQuery(id+"F0.wireOp",EDGE,"E1429"),sQuery(id+"F0.wireOp",EDGE,"E1430"),sQuery(id+"F0.wireOp",EDGE,"E1431"),sQuery(id+"F0.wireOp",EDGE,"E1432"),sQuery(id+"F0.wireOp",EDGE,"E1433"),sQuery(id+"F0.wireOp",EDGE,"E1434"),sQuery(id+"F0.wireOp",EDGE,"E1435"),sQuery(id+"F0.wireOp",EDGE,"E1436"),sQuery(id+"F0.wireOp",EDGE,"E1437"),sQuery(id+"F0.wireOp",EDGE,"E1438"),sQuery(id+"F0.wireOp",EDGE,"E1439"),sQuery(id+"F0.wireOp",EDGE,"E1440"),sQuery(id+"F0.wireOp",EDGE,"E1441"),sQuery(id+"F0.wireOp",EDGE,"E1442"),sQuery(id+"F0.wireOp",EDGE,"E1443"),sQuery(id+"F0.wireOp",EDGE,"E1444"),sQuery(id+"F0.wireOp",EDGE,"E1445"),sQuery(id+"F0.wireOp",EDGE,"E1446"),sQuery(id+"F0.wireOp",EDGE,"E1447")])]});
            var Q1;
            Q1=qCreatedBy(makeId("Origin.pointOp"),VERTEX);
            transform(context, id + "F2", {"entities" : qUnion([Q0]), "transformType" : TransformType.SCALE_UNIFORMLY, "scale" : 0.12, "scalePoint" : qUnion([Q1]), "makeCopy" : false});
        }
        {
            var Q0;
            Q0=makeQuery(id+"F1.opExtrude","CAP_FACE",FACE,{"disambiguationData":[OSD([sQuery(id+"F0.wireOp",EDGE,"E0"),sQuery(id+"F0.wireOp",EDGE,"E1"),sQuery(id+"F0.wireOp",EDGE,"E2"),sQuery(id+"F0.wireOp",EDGE,"E3"),sQuery(id+"F0.wireOp",EDGE,"E4"),sQuery(id+"F0.wireOp",EDGE,"E5"),sQuery(id+"F0.wireOp",EDGE,"E6"),sQuery(id+"F0.wireOp",EDGE,"E7"),sQuery(id+"F0.wireOp",EDGE,"E8"),sQuery(id+"F0.wireOp",EDGE,"E9"),sQuery(id+"F0.wireOp",EDGE,"E10"),sQuery(id+"F0.wireOp",EDGE,"E11"),sQuery(id+"F0.wireOp",EDGE,"E12"),sQuery(id+"F0.wireOp",EDGE,"E13"),sQuery(id+"F0.wireOp",EDGE,"E14"),sQuery(id+"F0.wireOp",EDGE,"E15"),sQuery(id+"F0.wireOp",EDGE,"E16"),sQuery(id+"F0.wireOp",EDGE,"E17"),sQuery(id+"F0.wireOp",EDGE,"E18"),sQuery(id+"F0.wireOp",EDGE,"E19"),sQuery(id+"F0.wireOp",EDGE,"E20"),sQuery(id+"F0.wireOp",EDGE,"E21"),sQuery(id+"F0.wireOp",EDGE,"E22"),sQuery(id+"F0.wireOp",EDGE,"E23"),sQuery(id+"F0.wireOp",EDGE,"E24"),sQuery(id+"F0.wireOp",EDGE,"E25"),sQuery(id+"F0.wireOp",EDGE,"E26"),sQuery(id+"F0.wireOp",EDGE,"E27"),sQuery(id+"F0.wireOp",EDGE,"E28"),sQuery(id+"F0.wireOp",EDGE,"E29"),sQuery(id+"F0.wireOp",EDGE,"E30"),sQuery(id+"F0.wireOp",EDGE,"E31"),sQuery(id+"F0.wireOp",EDGE,"E32"),sQuery(id+"F0.wireOp",EDGE,"E33"),sQuery(id+"F0.wireOp",EDGE,"E34"),sQuery(id+"F0.wireOp",EDGE,"E35"),sQuery(id+"F0.wireOp",EDGE,"E36"),sQuery(id+"F0.wireOp",EDGE,"E37"),sQuery(id+"F0.wireOp",EDGE,"E38"),sQuery(id+"F0.wireOp",EDGE,"E39"),sQuery(id+"F0.wireOp",EDGE,"E40"),sQuery(id+"F0.wireOp",EDGE,"E41"),sQuery(id+"F0.wireOp",EDGE,"E42"),sQuery(id+"F0.wireOp",EDGE,"E43"),sQuery(id+"F0.wireOp",EDGE,"E44"),sQuery(id+"F0.wireOp",EDGE,"E45"),sQuery(id+"F0.wireOp",EDGE,"E46"),sQuery(id+"F0.wireOp",EDGE,"E47"),sQuery(id+"F0.wireOp",EDGE,"E48"),sQuery(id+"F0.wireOp",EDGE,"E49"),sQuery(id+"F0.wireOp",EDGE,"E50"),sQuery(id+"F0.wireOp",EDGE,"E51"),sQuery(id+"F0.wireOp",EDGE,"E52"),sQuery(id+"F0.wireOp",EDGE,"E53"),sQuery(id+"F0.wireOp",EDGE,"E54"),sQuery(id+"F0.wireOp",EDGE,"E55"),sQuery(id+"F0.wireOp",EDGE,"E56"),sQuery(id+"F0.wireOp",EDGE,"E57"),sQuery(id+"F0.wireOp",EDGE,"E58"),sQuery(id+"F0.wireOp",EDGE,"E59"),sQuery(id+"F0.wireOp",EDGE,"E60"),sQuery(id+"F0.wireOp",EDGE,"E61"),sQuery(id+"F0.wireOp",EDGE,"E62"),sQuery(id+"F0.wireOp",EDGE,"E63"),sQuery(id+"F0.wireOp",EDGE,"E64"),sQuery(id+"F0.wireOp",EDGE,"E65"),sQuery(id+"F0.wireOp",EDGE,"E66"),sQuery(id+"F0.wireOp",EDGE,"E67"),sQuery(id+"F0.wireOp",EDGE,"E68"),sQuery(id+"F0.wireOp",EDGE,"E69"),sQuery(id+"F0.wireOp",EDGE,"E70"),sQuery(id+"F0.wireOp",EDGE,"E71"),sQuery(id+"F0.wireOp",EDGE,"E72"),sQuery(id+"F0.wireOp",EDGE,"E73"),sQuery(id+"F0.wireOp",EDGE,"E74"),sQuery(id+"F0.wireOp",EDGE,"E75"),sQuery(id+"F0.wireOp",EDGE,"E76"),sQuery(id+"F0.wireOp",EDGE,"E77"),sQuery(id+"F0.wireOp",EDGE,"E78"),sQuery(id+"F0.wireOp",EDGE,"E79"),sQuery(id+"F0.wireOp",EDGE,"E80"),sQuery(id+"F0.wireOp",EDGE,"E81"),sQuery(id+"F0.wireOp",EDGE,"E82"),sQuery(id+"F0.wireOp",EDGE,"E83"),sQuery(id+"F0.wireOp",EDGE,"E84"),sQuery(id+"F0.wireOp",EDGE,"E85"),sQuery(id+"F0.wireOp",EDGE,"E86"),sQuery(id+"F0.wireOp",EDGE,"E87"),sQuery(id+"F0.wireOp",EDGE,"E88"),sQuery(id+"F0.wireOp",EDGE,"E89"),sQuery(id+"F0.wireOp",EDGE,"E90"),sQuery(id+"F0.wireOp",EDGE,"E91"),sQuery(id+"F0.wireOp",EDGE,"E92"),sQuery(id+"F0.wireOp",EDGE,"E93"),sQuery(id+"F0.wireOp",EDGE,"E94"),sQuery(id+"F0.wireOp",EDGE,"E95"),sQuery(id+"F0.wireOp",EDGE,"E96"),sQuery(id+"F0.wireOp",EDGE,"E97"),sQuery(id+"F0.wireOp",EDGE,"E98"),sQuery(id+"F0.wireOp",EDGE,"E99"),sQuery(id+"F0.wireOp",EDGE,"E100"),sQuery(id+"F0.wireOp",EDGE,"E101"),sQuery(id+"F0.wireOp",EDGE,"E102"),sQuery(id+"F0.wireOp",EDGE,"E103"),sQuery(id+"F0.wireOp",EDGE,"E104"),sQuery(id+"F0.wireOp",EDGE,"E105"),sQuery(id+"F0.wireOp",EDGE,"E106"),sQuery(id+"F0.wireOp",EDGE,"E107"),sQuery(id+"F0.wireOp",EDGE,"E108"),sQuery(id+"F0.wireOp",EDGE,"E109"),sQuery(id+"F0.wireOp",EDGE,"E110"),sQuery(id+"F0.wireOp",EDGE,"E111"),sQuery(id+"F0.wireOp",EDGE,"E112"),sQuery(id+"F0.wireOp",EDGE,"E113"),sQuery(id+"F0.wireOp",EDGE,"E114"),sQuery(id+"F0.wireOp",EDGE,"E115"),sQuery(id+"F0.wireOp",EDGE,"E116"),sQuery(id+"F0.wireOp",EDGE,"E117"),sQuery(id+"F0.wireOp",EDGE,"E118"),sQuery(id+"F0.wireOp",EDGE,"E119"),sQuery(id+"F0.wireOp",EDGE,"E120"),sQuery(id+"F0.wireOp",EDGE,"E121"),sQuery(id+"F0.wireOp",EDGE,"E122"),sQuery(id+"F0.wireOp",EDGE,"E123"),sQuery(id+"F0.wireOp",EDGE,"E124"),sQuery(id+"F0.wireOp",EDGE,"E125"),sQuery(id+"F0.wireOp",EDGE,"E126"),sQuery(id+"F0.wireOp",EDGE,"E127"),sQuery(id+"F0.wireOp",EDGE,"E128"),sQuery(id+"F0.wireOp",EDGE,"E129"),sQuery(id+"F0.wireOp",EDGE,"E130"),sQuery(id+"F0.wireOp",EDGE,"E131"),sQuery(id+"F0.wireOp",EDGE,"E132"),sQuery(id+"F0.wireOp",EDGE,"E133"),sQuery(id+"F0.wireOp",EDGE,"E134"),sQuery(id+"F0.wireOp",EDGE,"E135"),sQuery(id+"F0.wireOp",EDGE,"E136"),sQuery(id+"F0.wireOp",EDGE,"E137"),sQuery(id+"F0.wireOp",EDGE,"E138"),sQuery(id+"F0.wireOp",EDGE,"E139"),sQuery(id+"F0.wireOp",EDGE,"E140"),sQuery(id+"F0.wireOp",EDGE,"E141"),sQuery(id+"F0.wireOp",EDGE,"E142"),sQuery(id+"F0.wireOp",EDGE,"E143"),sQuery(id+"F0.wireOp",EDGE,"E144"),sQuery(id+"F0.wireOp",EDGE,"E145"),sQuery(id+"F0.wireOp",EDGE,"E146"),sQuery(id+"F0.wireOp",EDGE,"E147"),sQuery(id+"F0.wireOp",EDGE,"E148"),sQuery(id+"F0.wireOp",EDGE,"E149"),sQuery(id+"F0.wireOp",EDGE,"E150"),sQuery(id+"F0.wireOp",EDGE,"E151"),sQuery(id+"F0.wireOp",EDGE,"E152"),sQuery(id+"F0.wireOp",EDGE,"E153"),sQuery(id+"F0.wireOp",EDGE,"E154"),sQuery(id+"F0.wireOp",EDGE,"E155"),sQuery(id+"F0.wireOp",EDGE,"E156"),sQuery(id+"F0.wireOp",EDGE,"E157"),sQuery(id+"F0.wireOp",EDGE,"E158"),sQuery(id+"F0.wireOp",EDGE,"E159"),sQuery(id+"F0.wireOp",EDGE,"E160"),sQuery(id+"F0.wireOp",EDGE,"E161"),sQuery(id+"F0.wireOp",EDGE,"E162"),sQuery(id+"F0.wireOp",EDGE,"E163"),sQuery(id+"F0.wireOp",EDGE,"E164"),sQuery(id+"F0.wireOp",EDGE,"E165"),sQuery(id+"F0.wireOp",EDGE,"E166"),sQuery(id+"F0.wireOp",EDGE,"E167"),sQuery(id+"F0.wireOp",EDGE,"E168"),sQuery(id+"F0.wireOp",EDGE,"E169"),sQuery(id+"F0.wireOp",EDGE,"E170"),sQuery(id+"F0.wireOp",EDGE,"E171"),sQuery(id+"F0.wireOp",EDGE,"E172"),sQuery(id+"F0.wireOp",EDGE,"E173"),sQuery(id+"F0.wireOp",EDGE,"E174"),sQuery(id+"F0.wireOp",EDGE,"E175"),sQuery(id+"F0.wireOp",EDGE,"E176"),sQuery(id+"F0.wireOp",EDGE,"E177"),sQuery(id+"F0.wireOp",EDGE,"E178"),sQuery(id+"F0.wireOp",EDGE,"E179"),sQuery(id+"F0.wireOp",EDGE,"E180"),sQuery(id+"F0.wireOp",EDGE,"E181"),sQuery(id+"F0.wireOp",EDGE,"E182"),sQuery(id+"F0.wireOp",EDGE,"E183"),sQuery(id+"F0.wireOp",EDGE,"E184"),sQuery(id+"F0.wireOp",EDGE,"E185"),sQuery(id+"F0.wireOp",EDGE,"E186"),sQuery(id+"F0.wireOp",EDGE,"E187"),sQuery(id+"F0.wireOp",EDGE,"E188"),sQuery(id+"F0.wireOp",EDGE,"E189"),sQuery(id+"F0.wireOp",EDGE,"E190"),sQuery(id+"F0.wireOp",EDGE,"E191"),sQuery(id+"F0.wireOp",EDGE,"E192"),sQuery(id+"F0.wireOp",EDGE,"E193"),sQuery(id+"F0.wireOp",EDGE,"E194"),sQuery(id+"F0.wireOp",EDGE,"E195"),sQuery(id+"F0.wireOp",EDGE,"E196"),sQuery(id+"F0.wireOp",EDGE,"E197"),sQuery(id+"F0.wireOp",EDGE,"E198"),sQuery(id+"F0.wireOp",EDGE,"E199"),sQuery(id+"F0.wireOp",EDGE,"E200"),sQuery(id+"F0.wireOp",EDGE,"E201"),sQuery(id+"F0.wireOp",EDGE,"E202"),sQuery(id+"F0.wireOp",EDGE,"E203"),sQuery(id+"F0.wireOp",EDGE,"E204"),sQuery(id+"F0.wireOp",EDGE,"E205"),sQuery(id+"F0.wireOp",EDGE,"E206"),sQuery(id+"F0.wireOp",EDGE,"E207"),sQuery(id+"F0.wireOp",EDGE,"E208"),sQuery(id+"F0.wireOp",EDGE,"E209"),sQuery(id+"F0.wireOp",EDGE,"E210"),sQuery(id+"F0.wireOp",EDGE,"E211"),sQuery(id+"F0.wireOp",EDGE,"E212"),sQuery(id+"F0.wireOp",EDGE,"E213"),sQuery(id+"F0.wireOp",EDGE,"E214"),sQuery(id+"F0.wireOp",EDGE,"E215"),sQuery(id+"F0.wireOp",EDGE,"E216"),sQuery(id+"F0.wireOp",EDGE,"E217"),sQuery(id+"F0.wireOp",EDGE,"E218"),sQuery(id+"F0.wireOp",EDGE,"E219"),sQuery(id+"F0.wireOp",EDGE,"E220"),sQuery(id+"F0.wireOp",EDGE,"E221"),sQuery(id+"F0.wireOp",EDGE,"E222"),sQuery(id+"F0.wireOp",EDGE,"E223"),sQuery(id+"F0.wireOp",EDGE,"E224"),sQuery(id+"F0.wireOp",EDGE,"E225"),sQuery(id+"F0.wireOp",EDGE,"E226"),sQuery(id+"F0.wireOp",EDGE,"E227"),sQuery(id+"F0.wireOp",EDGE,"E228"),sQuery(id+"F0.wireOp",EDGE,"E229"),sQuery(id+"F0.wireOp",EDGE,"E230"),sQuery(id+"F0.wireOp",EDGE,"E231"),sQuery(id+"F0.wireOp",EDGE,"E232"),sQuery(id+"F0.wireOp",EDGE,"E233"),sQuery(id+"F0.wireOp",EDGE,"E234"),sQuery(id+"F0.wireOp",EDGE,"E235"),sQuery(id+"F0.wireOp",EDGE,"E236"),sQuery(id+"F0.wireOp",EDGE,"E237"),sQuery(id+"F0.wireOp",EDGE,"E238"),sQuery(id+"F0.wireOp",EDGE,"E239"),sQuery(id+"F0.wireOp",EDGE,"E240"),sQuery(id+"F0.wireOp",EDGE,"E241"),sQuery(id+"F0.wireOp",EDGE,"E242"),sQuery(id+"F0.wireOp",EDGE,"E243"),sQuery(id+"F0.wireOp",EDGE,"E244"),sQuery(id+"F0.wireOp",EDGE,"E245"),sQuery(id+"F0.wireOp",EDGE,"E246"),sQuery(id+"F0.wireOp",EDGE,"E247"),sQuery(id+"F0.wireOp",EDGE,"E248"),sQuery(id+"F0.wireOp",EDGE,"E249"),sQuery(id+"F0.wireOp",EDGE,"E250"),sQuery(id+"F0.wireOp",EDGE,"E251"),sQuery(id+"F0.wireOp",EDGE,"E252"),sQuery(id+"F0.wireOp",EDGE,"E253"),sQuery(id+"F0.wireOp",EDGE,"E254"),sQuery(id+"F0.wireOp",EDGE,"E255"),sQuery(id+"F0.wireOp",EDGE,"E256"),sQuery(id+"F0.wireOp",EDGE,"E257"),sQuery(id+"F0.wireOp",EDGE,"E258"),sQuery(id+"F0.wireOp",EDGE,"E259"),sQuery(id+"F0.wireOp",EDGE,"E260"),sQuery(id+"F0.wireOp",EDGE,"E261"),sQuery(id+"F0.wireOp",EDGE,"E262"),sQuery(id+"F0.wireOp",EDGE,"E263"),sQuery(id+"F0.wireOp",EDGE,"E264"),sQuery(id+"F0.wireOp",EDGE,"E265"),sQuery(id+"F0.wireOp",EDGE,"E266"),sQuery(id+"F0.wireOp",EDGE,"E267"),sQuery(id+"F0.wireOp",EDGE,"E268"),sQuery(id+"F0.wireOp",EDGE,"E269"),sQuery(id+"F0.wireOp",EDGE,"E270"),sQuery(id+"F0.wireOp",EDGE,"E271"),sQuery(id+"F0.wireOp",EDGE,"E272"),sQuery(id+"F0.wireOp",EDGE,"E273"),sQuery(id+"F0.wireOp",EDGE,"E274"),sQuery(id+"F0.wireOp",EDGE,"E275"),sQuery(id+"F0.wireOp",EDGE,"E276"),sQuery(id+"F0.wireOp",EDGE,"E277"),sQuery(id+"F0.wireOp",EDGE,"E278"),sQuery(id+"F0.wireOp",EDGE,"E279"),sQuery(id+"F0.wireOp",EDGE,"E280"),sQuery(id+"F0.wireOp",EDGE,"E281"),sQuery(id+"F0.wireOp",EDGE,"E282"),sQuery(id+"F0.wireOp",EDGE,"E283"),sQuery(id+"F0.wireOp",EDGE,"E284"),sQuery(id+"F0.wireOp",EDGE,"E285"),sQuery(id+"F0.wireOp",EDGE,"E286"),sQuery(id+"F0.wireOp",EDGE,"E287"),sQuery(id+"F0.wireOp",EDGE,"E288"),sQuery(id+"F0.wireOp",EDGE,"E289"),sQuery(id+"F0.wireOp",EDGE,"E290"),sQuery(id+"F0.wireOp",EDGE,"E291"),sQuery(id+"F0.wireOp",EDGE,"E292"),sQuery(id+"F0.wireOp",EDGE,"E293"),sQuery(id+"F0.wireOp",EDGE,"E294"),sQuery(id+"F0.wireOp",EDGE,"E295"),sQuery(id+"F0.wireOp",EDGE,"E296"),sQuery(id+"F0.wireOp",EDGE,"E297"),sQuery(id+"F0.wireOp",EDGE,"E298"),sQuery(id+"F0.wireOp",EDGE,"E299"),sQuery(id+"F0.wireOp",EDGE,"E300"),sQuery(id+"F0.wireOp",EDGE,"E301"),sQuery(id+"F0.wireOp",EDGE,"E302"),sQuery(id+"F0.wireOp",EDGE,"E303"),sQuery(id+"F0.wireOp",EDGE,"E304"),sQuery(id+"F0.wireOp",EDGE,"E305"),sQuery(id+"F0.wireOp",EDGE,"E306"),sQuery(id+"F0.wireOp",EDGE,"E307"),sQuery(id+"F0.wireOp",EDGE,"E308"),sQuery(id+"F0.wireOp",EDGE,"E309"),sQuery(id+"F0.wireOp",EDGE,"E310"),sQuery(id+"F0.wireOp",EDGE,"E311"),sQuery(id+"F0.wireOp",EDGE,"E312"),sQuery(id+"F0.wireOp",EDGE,"E313"),sQuery(id+"F0.wireOp",EDGE,"E314"),sQuery(id+"F0.wireOp",EDGE,"E315"),sQuery(id+"F0.wireOp",EDGE,"E316"),sQuery(id+"F0.wireOp",EDGE,"E317"),sQuery(id+"F0.wireOp",EDGE,"E318"),sQuery(id+"F0.wireOp",EDGE,"E319"),sQuery(id+"F0.wireOp",EDGE,"E320"),sQuery(id+"F0.wireOp",EDGE,"E321"),sQuery(id+"F0.wireOp",EDGE,"E322"),sQuery(id+"F0.wireOp",EDGE,"E323"),sQuery(id+"F0.wireOp",EDGE,"E324"),sQuery(id+"F0.wireOp",EDGE,"E325"),sQuery(id+"F0.wireOp",EDGE,"E326"),sQuery(id+"F0.wireOp",EDGE,"E327"),sQuery(id+"F0.wireOp",EDGE,"E328"),sQuery(id+"F0.wireOp",EDGE,"E329"),sQuery(id+"F0.wireOp",EDGE,"E330"),sQuery(id+"F0.wireOp",EDGE,"E331"),sQuery(id+"F0.wireOp",EDGE,"E332"),sQuery(id+"F0.wireOp",EDGE,"E333"),sQuery(id+"F0.wireOp",EDGE,"E334"),sQuery(id+"F0.wireOp",EDGE,"E335"),sQuery(id+"F0.wireOp",EDGE,"E336"),sQuery(id+"F0.wireOp",EDGE,"E337"),sQuery(id+"F0.wireOp",EDGE,"E338"),sQuery(id+"F0.wireOp",EDGE,"E339"),sQuery(id+"F0.wireOp",EDGE,"E340"),sQuery(id+"F0.wireOp",EDGE,"E341"),sQuery(id+"F0.wireOp",EDGE,"E342"),sQuery(id+"F0.wireOp",EDGE,"E343"),sQuery(id+"F0.wireOp",EDGE,"E344"),sQuery(id+"F0.wireOp",EDGE,"E345"),sQuery(id+"F0.wireOp",EDGE,"E346"),sQuery(id+"F0.wireOp",EDGE,"E347"),sQuery(id+"F0.wireOp",EDGE,"E348"),sQuery(id+"F0.wireOp",EDGE,"E349"),sQuery(id+"F0.wireOp",EDGE,"E350"),sQuery(id+"F0.wireOp",EDGE,"E351"),sQuery(id+"F0.wireOp",EDGE,"E352"),sQuery(id+"F0.wireOp",EDGE,"E353"),sQuery(id+"F0.wireOp",EDGE,"E354"),sQuery(id+"F0.wireOp",EDGE,"E355"),sQuery(id+"F0.wireOp",EDGE,"E356"),sQuery(id+"F0.wireOp",EDGE,"E357"),sQuery(id+"F0.wireOp",EDGE,"E358"),sQuery(id+"F0.wireOp",EDGE,"E359"),sQuery(id+"F0.wireOp",EDGE,"E360"),sQuery(id+"F0.wireOp",EDGE,"E361"),sQuery(id+"F0.wireOp",EDGE,"E362"),sQuery(id+"F0.wireOp",EDGE,"E363"),sQuery(id+"F0.wireOp",EDGE,"E364"),sQuery(id+"F0.wireOp",EDGE,"E365"),sQuery(id+"F0.wireOp",EDGE,"E366"),sQuery(id+"F0.wireOp",EDGE,"E367"),sQuery(id+"F0.wireOp",EDGE,"E368"),sQuery(id+"F0.wireOp",EDGE,"E369"),sQuery(id+"F0.wireOp",EDGE,"E370"),sQuery(id+"F0.wireOp",EDGE,"E371"),sQuery(id+"F0.wireOp",EDGE,"E372"),sQuery(id+"F0.wireOp",EDGE,"E373"),sQuery(id+"F0.wireOp",EDGE,"E374"),sQuery(id+"F0.wireOp",EDGE,"E375"),sQuery(id+"F0.wireOp",EDGE,"E376"),sQuery(id+"F0.wireOp",EDGE,"E377"),sQuery(id+"F0.wireOp",EDGE,"E378"),sQuery(id+"F0.wireOp",EDGE,"E379"),sQuery(id+"F0.wireOp",EDGE,"E380"),sQuery(id+"F0.wireOp",EDGE,"E381"),sQuery(id+"F0.wireOp",EDGE,"E382"),sQuery(id+"F0.wireOp",EDGE,"E383"),sQuery(id+"F0.wireOp",EDGE,"E384"),sQuery(id+"F0.wireOp",EDGE,"E385"),sQuery(id+"F0.wireOp",EDGE,"E386"),sQuery(id+"F0.wireOp",EDGE,"E387"),sQuery(id+"F0.wireOp",EDGE,"E388"),sQuery(id+"F0.wireOp",EDGE,"E389"),sQuery(id+"F0.wireOp",EDGE,"E390"),sQuery(id+"F0.wireOp",EDGE,"E391"),sQuery(id+"F0.wireOp",EDGE,"E392"),sQuery(id+"F0.wireOp",EDGE,"E393"),sQuery(id+"F0.wireOp",EDGE,"E394"),sQuery(id+"F0.wireOp",EDGE,"E395"),sQuery(id+"F0.wireOp",EDGE,"E396"),sQuery(id+"F0.wireOp",EDGE,"E397"),sQuery(id+"F0.wireOp",EDGE,"E398"),sQuery(id+"F0.wireOp",EDGE,"E399"),sQuery(id+"F0.wireOp",EDGE,"E400"),sQuery(id+"F0.wireOp",EDGE,"E401"),sQuery(id+"F0.wireOp",EDGE,"E402"),sQuery(id+"F0.wireOp",EDGE,"E403"),sQuery(id+"F0.wireOp",EDGE,"E404"),sQuery(id+"F0.wireOp",EDGE,"E405"),sQuery(id+"F0.wireOp",EDGE,"E406"),sQuery(id+"F0.wireOp",EDGE,"E407"),sQuery(id+"F0.wireOp",EDGE,"E408"),sQuery(id+"F0.wireOp",EDGE,"E409"),sQuery(id+"F0.wireOp",EDGE,"E410"),sQuery(id+"F0.wireOp",EDGE,"E411"),sQuery(id+"F0.wireOp",EDGE,"E412"),sQuery(id+"F0.wireOp",EDGE,"E413"),sQuery(id+"F0.wireOp",EDGE,"E414"),sQuery(id+"F0.wireOp",EDGE,"E415"),sQuery(id+"F0.wireOp",EDGE,"E416"),sQuery(id+"F0.wireOp",EDGE,"E417"),sQuery(id+"F0.wireOp",EDGE,"E418"),sQuery(id+"F0.wireOp",EDGE,"E419"),sQuery(id+"F0.wireOp",EDGE,"E420"),sQuery(id+"F0.wireOp",EDGE,"E421"),sQuery(id+"F0.wireOp",EDGE,"E422"),sQuery(id+"F0.wireOp",EDGE,"E423"),sQuery(id+"F0.wireOp",EDGE,"E424"),sQuery(id+"F0.wireOp",EDGE,"E425"),sQuery(id+"F0.wireOp",EDGE,"E426"),sQuery(id+"F0.wireOp",EDGE,"E427"),sQuery(id+"F0.wireOp",EDGE,"E428"),sQuery(id+"F0.wireOp",EDGE,"E429"),sQuery(id+"F0.wireOp",EDGE,"E430"),sQuery(id+"F0.wireOp",EDGE,"E431"),sQuery(id+"F0.wireOp",EDGE,"E432"),sQuery(id+"F0.wireOp",EDGE,"E433"),sQuery(id+"F0.wireOp",EDGE,"E434"),sQuery(id+"F0.wireOp",EDGE,"E435"),sQuery(id+"F0.wireOp",EDGE,"E436"),sQuery(id+"F0.wireOp",EDGE,"E437"),sQuery(id+"F0.wireOp",EDGE,"E438"),sQuery(id+"F0.wireOp",EDGE,"E439"),sQuery(id+"F0.wireOp",EDGE,"E440"),sQuery(id+"F0.wireOp",EDGE,"E441"),sQuery(id+"F0.wireOp",EDGE,"E442"),sQuery(id+"F0.wireOp",EDGE,"E443"),sQuery(id+"F0.wireOp",EDGE,"E444"),sQuery(id+"F0.wireOp",EDGE,"E445"),sQuery(id+"F0.wireOp",EDGE,"E446"),sQuery(id+"F0.wireOp",EDGE,"E447"),sQuery(id+"F0.wireOp",EDGE,"E448"),sQuery(id+"F0.wireOp",EDGE,"E449"),sQuery(id+"F0.wireOp",EDGE,"E450"),sQuery(id+"F0.wireOp",EDGE,"E451"),sQuery(id+"F0.wireOp",EDGE,"E452"),sQuery(id+"F0.wireOp",EDGE,"E453"),sQuery(id+"F0.wireOp",EDGE,"E454"),sQuery(id+"F0.wireOp",EDGE,"E455"),sQuery(id+"F0.wireOp",EDGE,"E456"),sQuery(id+"F0.wireOp",EDGE,"E457"),sQuery(id+"F0.wireOp",EDGE,"E458"),sQuery(id+"F0.wireOp",EDGE,"E459"),sQuery(id+"F0.wireOp",EDGE,"E460"),sQuery(id+"F0.wireOp",EDGE,"E461"),sQuery(id+"F0.wireOp",EDGE,"E462"),sQuery(id+"F0.wireOp",EDGE,"E463"),sQuery(id+"F0.wireOp",EDGE,"E464"),sQuery(id+"F0.wireOp",EDGE,"E465"),sQuery(id+"F0.wireOp",EDGE,"E466"),sQuery(id+"F0.wireOp",EDGE,"E467"),sQuery(id+"F0.wireOp",EDGE,"E468"),sQuery(id+"F0.wireOp",EDGE,"E469"),sQuery(id+"F0.wireOp",EDGE,"E470"),sQuery(id+"F0.wireOp",EDGE,"E471"),sQuery(id+"F0.wireOp",EDGE,"E472"),sQuery(id+"F0.wireOp",EDGE,"E473"),sQuery(id+"F0.wireOp",EDGE,"E474"),sQuery(id+"F0.wireOp",EDGE,"E475"),sQuery(id+"F0.wireOp",EDGE,"E476"),sQuery(id+"F0.wireOp",EDGE,"E477"),sQuery(id+"F0.wireOp",EDGE,"E478"),sQuery(id+"F0.wireOp",EDGE,"E479"),sQuery(id+"F0.wireOp",EDGE,"E480"),sQuery(id+"F0.wireOp",EDGE,"E481"),sQuery(id+"F0.wireOp",EDGE,"E482"),sQuery(id+"F0.wireOp",EDGE,"E483"),sQuery(id+"F0.wireOp",EDGE,"E484"),sQuery(id+"F0.wireOp",EDGE,"E485"),sQuery(id+"F0.wireOp",EDGE,"E486"),sQuery(id+"F0.wireOp",EDGE,"E487"),sQuery(id+"F0.wireOp",EDGE,"E488"),sQuery(id+"F0.wireOp",EDGE,"E489"),sQuery(id+"F0.wireOp",EDGE,"E490"),sQuery(id+"F0.wireOp",EDGE,"E491"),sQuery(id+"F0.wireOp",EDGE,"E492"),sQuery(id+"F0.wireOp",EDGE,"E493"),sQuery(id+"F0.wireOp",EDGE,"E494"),sQuery(id+"F0.wireOp",EDGE,"E495"),sQuery(id+"F0.wireOp",EDGE,"E496"),sQuery(id+"F0.wireOp",EDGE,"E497"),sQuery(id+"F0.wireOp",EDGE,"E498"),sQuery(id+"F0.wireOp",EDGE,"E499"),sQuery(id+"F0.wireOp",EDGE,"E500"),sQuery(id+"F0.wireOp",EDGE,"E501"),sQuery(id+"F0.wireOp",EDGE,"E502"),sQuery(id+"F0.wireOp",EDGE,"E503"),sQuery(id+"F0.wireOp",EDGE,"E504"),sQuery(id+"F0.wireOp",EDGE,"E505"),sQuery(id+"F0.wireOp",EDGE,"E506"),sQuery(id+"F0.wireOp",EDGE,"E507"),sQuery(id+"F0.wireOp",EDGE,"E508"),sQuery(id+"F0.wireOp",EDGE,"E509"),sQuery(id+"F0.wireOp",EDGE,"E510"),sQuery(id+"F0.wireOp",EDGE,"E511"),sQuery(id+"F0.wireOp",EDGE,"E512"),sQuery(id+"F0.wireOp",EDGE,"E513"),sQuery(id+"F0.wireOp",EDGE,"E514"),sQuery(id+"F0.wireOp",EDGE,"E515"),sQuery(id+"F0.wireOp",EDGE,"E516"),sQuery(id+"F0.wireOp",EDGE,"E517"),sQuery(id+"F0.wireOp",EDGE,"E518"),sQuery(id+"F0.wireOp",EDGE,"E519"),sQuery(id+"F0.wireOp",EDGE,"E520"),sQuery(id+"F0.wireOp",EDGE,"E521"),sQuery(id+"F0.wireOp",EDGE,"E522"),sQuery(id+"F0.wireOp",EDGE,"E523"),sQuery(id+"F0.wireOp",EDGE,"E524"),sQuery(id+"F0.wireOp",EDGE,"E525"),sQuery(id+"F0.wireOp",EDGE,"E526"),sQuery(id+"F0.wireOp",EDGE,"E527"),sQuery(id+"F0.wireOp",EDGE,"E528"),sQuery(id+"F0.wireOp",EDGE,"E529"),sQuery(id+"F0.wireOp",EDGE,"E530"),sQuery(id+"F0.wireOp",EDGE,"E531"),sQuery(id+"F0.wireOp",EDGE,"E532"),sQuery(id+"F0.wireOp",EDGE,"E533"),sQuery(id+"F0.wireOp",EDGE,"E534"),sQuery(id+"F0.wireOp",EDGE,"E535"),sQuery(id+"F0.wireOp",EDGE,"E536"),sQuery(id+"F0.wireOp",EDGE,"E537"),sQuery(id+"F0.wireOp",EDGE,"E538"),sQuery(id+"F0.wireOp",EDGE,"E539"),sQuery(id+"F0.wireOp",EDGE,"E540"),sQuery(id+"F0.wireOp",EDGE,"E541"),sQuery(id+"F0.wireOp",EDGE,"E542"),sQuery(id+"F0.wireOp",EDGE,"E543"),sQuery(id+"F0.wireOp",EDGE,"E544"),sQuery(id+"F0.wireOp",EDGE,"E545"),sQuery(id+"F0.wireOp",EDGE,"E546"),sQuery(id+"F0.wireOp",EDGE,"E547"),sQuery(id+"F0.wireOp",EDGE,"E548"),sQuery(id+"F0.wireOp",EDGE,"E549"),sQuery(id+"F0.wireOp",EDGE,"E550"),sQuery(id+"F0.wireOp",EDGE,"E551"),sQuery(id+"F0.wireOp",EDGE,"E552"),sQuery(id+"F0.wireOp",EDGE,"E553"),sQuery(id+"F0.wireOp",EDGE,"E554"),sQuery(id+"F0.wireOp",EDGE,"E555"),sQuery(id+"F0.wireOp",EDGE,"E556"),sQuery(id+"F0.wireOp",EDGE,"E557"),sQuery(id+"F0.wireOp",EDGE,"E558"),sQuery(id+"F0.wireOp",EDGE,"E559"),sQuery(id+"F0.wireOp",EDGE,"E560"),sQuery(id+"F0.wireOp",EDGE,"E561"),sQuery(id+"F0.wireOp",EDGE,"E562"),sQuery(id+"F0.wireOp",EDGE,"E563"),sQuery(id+"F0.wireOp",EDGE,"E564"),sQuery(id+"F0.wireOp",EDGE,"E565"),sQuery(id+"F0.wireOp",EDGE,"E566"),sQuery(id+"F0.wireOp",EDGE,"E567"),sQuery(id+"F0.wireOp",EDGE,"E568"),sQuery(id+"F0.wireOp",EDGE,"E569"),sQuery(id+"F0.wireOp",EDGE,"E570"),sQuery(id+"F0.wireOp",EDGE,"E571"),sQuery(id+"F0.wireOp",EDGE,"E572"),sQuery(id+"F0.wireOp",EDGE,"E573"),sQuery(id+"F0.wireOp",EDGE,"E574"),sQuery(id+"F0.wireOp",EDGE,"E575"),sQuery(id+"F0.wireOp",EDGE,"E576"),sQuery(id+"F0.wireOp",EDGE,"E577"),sQuery(id+"F0.wireOp",EDGE,"E578"),sQuery(id+"F0.wireOp",EDGE,"E579"),sQuery(id+"F0.wireOp",EDGE,"E580"),sQuery(id+"F0.wireOp",EDGE,"E581"),sQuery(id+"F0.wireOp",EDGE,"E582"),sQuery(id+"F0.wireOp",EDGE,"E583"),sQuery(id+"F0.wireOp",EDGE,"E584"),sQuery(id+"F0.wireOp",EDGE,"E585"),sQuery(id+"F0.wireOp",EDGE,"E586"),sQuery(id+"F0.wireOp",EDGE,"E587"),sQuery(id+"F0.wireOp",EDGE,"E588"),sQuery(id+"F0.wireOp",EDGE,"E589"),sQuery(id+"F0.wireOp",EDGE,"E590"),sQuery(id+"F0.wireOp",EDGE,"E591"),sQuery(id+"F0.wireOp",EDGE,"E592"),sQuery(id+"F0.wireOp",EDGE,"E593"),sQuery(id+"F0.wireOp",EDGE,"E594"),sQuery(id+"F0.wireOp",EDGE,"E595"),sQuery(id+"F0.wireOp",EDGE,"E596"),sQuery(id+"F0.wireOp",EDGE,"E597"),sQuery(id+"F0.wireOp",EDGE,"E598"),sQuery(id+"F0.wireOp",EDGE,"E599"),sQuery(id+"F0.wireOp",EDGE,"E600"),sQuery(id+"F0.wireOp",EDGE,"E601"),sQuery(id+"F0.wireOp",EDGE,"E602"),sQuery(id+"F0.wireOp",EDGE,"E603"),sQuery(id+"F0.wireOp",EDGE,"E604"),sQuery(id+"F0.wireOp",EDGE,"E605"),sQuery(id+"F0.wireOp",EDGE,"E606"),sQuery(id+"F0.wireOp",EDGE,"E607"),sQuery(id+"F0.wireOp",EDGE,"E608"),sQuery(id+"F0.wireOp",EDGE,"E609"),sQuery(id+"F0.wireOp",EDGE,"E610"),sQuery(id+"F0.wireOp",EDGE,"E611"),sQuery(id+"F0.wireOp",EDGE,"E612"),sQuery(id+"F0.wireOp",EDGE,"E613"),sQuery(id+"F0.wireOp",EDGE,"E614"),sQuery(id+"F0.wireOp",EDGE,"E615"),sQuery(id+"F0.wireOp",EDGE,"E616"),sQuery(id+"F0.wireOp",EDGE,"E617"),sQuery(id+"F0.wireOp",EDGE,"E618"),sQuery(id+"F0.wireOp",EDGE,"E619"),sQuery(id+"F0.wireOp",EDGE,"E620"),sQuery(id+"F0.wireOp",EDGE,"E621"),sQuery(id+"F0.wireOp",EDGE,"E622"),sQuery(id+"F0.wireOp",EDGE,"E623"),sQuery(id+"F0.wireOp",EDGE,"E624"),sQuery(id+"F0.wireOp",EDGE,"E625"),sQuery(id+"F0.wireOp",EDGE,"E626"),sQuery(id+"F0.wireOp",EDGE,"E627"),sQuery(id+"F0.wireOp",EDGE,"E628"),sQuery(id+"F0.wireOp",EDGE,"E629"),sQuery(id+"F0.wireOp",EDGE,"E630"),sQuery(id+"F0.wireOp",EDGE,"E631"),sQuery(id+"F0.wireOp",EDGE,"E632"),sQuery(id+"F0.wireOp",EDGE,"E633"),sQuery(id+"F0.wireOp",EDGE,"E634"),sQuery(id+"F0.wireOp",EDGE,"E635"),sQuery(id+"F0.wireOp",EDGE,"E636"),sQuery(id+"F0.wireOp",EDGE,"E637"),sQuery(id+"F0.wireOp",EDGE,"E638"),sQuery(id+"F0.wireOp",EDGE,"E639"),sQuery(id+"F0.wireOp",EDGE,"E640"),sQuery(id+"F0.wireOp",EDGE,"E641"),sQuery(id+"F0.wireOp",EDGE,"E642"),sQuery(id+"F0.wireOp",EDGE,"E643"),sQuery(id+"F0.wireOp",EDGE,"E644"),sQuery(id+"F0.wireOp",EDGE,"E645"),sQuery(id+"F0.wireOp",EDGE,"E646"),sQuery(id+"F0.wireOp",EDGE,"E647"),sQuery(id+"F0.wireOp",EDGE,"E648"),sQuery(id+"F0.wireOp",EDGE,"E649"),sQuery(id+"F0.wireOp",EDGE,"E650"),sQuery(id+"F0.wireOp",EDGE,"E651"),sQuery(id+"F0.wireOp",EDGE,"E652"),sQuery(id+"F0.wireOp",EDGE,"E653"),sQuery(id+"F0.wireOp",EDGE,"E654"),sQuery(id+"F0.wireOp",EDGE,"E655"),sQuery(id+"F0.wireOp",EDGE,"E656"),sQuery(id+"F0.wireOp",EDGE,"E657"),sQuery(id+"F0.wireOp",EDGE,"E658"),sQuery(id+"F0.wireOp",EDGE,"E659"),sQuery(id+"F0.wireOp",EDGE,"E660"),sQuery(id+"F0.wireOp",EDGE,"E661"),sQuery(id+"F0.wireOp",EDGE,"E662"),sQuery(id+"F0.wireOp",EDGE,"E663"),sQuery(id+"F0.wireOp",EDGE,"E664"),sQuery(id+"F0.wireOp",EDGE,"E665"),sQuery(id+"F0.wireOp",EDGE,"E666"),sQuery(id+"F0.wireOp",EDGE,"E667"),sQuery(id+"F0.wireOp",EDGE,"E668"),sQuery(id+"F0.wireOp",EDGE,"E669"),sQuery(id+"F0.wireOp",EDGE,"E670"),sQuery(id+"F0.wireOp",EDGE,"E671"),sQuery(id+"F0.wireOp",EDGE,"E672"),sQuery(id+"F0.wireOp",EDGE,"E673"),sQuery(id+"F0.wireOp",EDGE,"E674"),sQuery(id+"F0.wireOp",EDGE,"E675"),sQuery(id+"F0.wireOp",EDGE,"E676"),sQuery(id+"F0.wireOp",EDGE,"E677"),sQuery(id+"F0.wireOp",EDGE,"E678"),sQuery(id+"F0.wireOp",EDGE,"E679"),sQuery(id+"F0.wireOp",EDGE,"E680"),sQuery(id+"F0.wireOp",EDGE,"E681"),sQuery(id+"F0.wireOp",EDGE,"E682"),sQuery(id+"F0.wireOp",EDGE,"E683"),sQuery(id+"F0.wireOp",EDGE,"E684"),sQuery(id+"F0.wireOp",EDGE,"E685"),sQuery(id+"F0.wireOp",EDGE,"E686"),sQuery(id+"F0.wireOp",EDGE,"E687"),sQuery(id+"F0.wireOp",EDGE,"E688"),sQuery(id+"F0.wireOp",EDGE,"E689"),sQuery(id+"F0.wireOp",EDGE,"E690"),sQuery(id+"F0.wireOp",EDGE,"E691"),sQuery(id+"F0.wireOp",EDGE,"E692"),sQuery(id+"F0.wireOp",EDGE,"E693"),sQuery(id+"F0.wireOp",EDGE,"E694"),sQuery(id+"F0.wireOp",EDGE,"E695"),sQuery(id+"F0.wireOp",EDGE,"E696"),sQuery(id+"F0.wireOp",EDGE,"E697"),sQuery(id+"F0.wireOp",EDGE,"E698"),sQuery(id+"F0.wireOp",EDGE,"E699"),sQuery(id+"F0.wireOp",EDGE,"E700"),sQuery(id+"F0.wireOp",EDGE,"E701"),sQuery(id+"F0.wireOp",EDGE,"E702"),sQuery(id+"F0.wireOp",EDGE,"E703"),sQuery(id+"F0.wireOp",EDGE,"E704"),sQuery(id+"F0.wireOp",EDGE,"E705"),sQuery(id+"F0.wireOp",EDGE,"E706"),sQuery(id+"F0.wireOp",EDGE,"E707"),sQuery(id+"F0.wireOp",EDGE,"E708"),sQuery(id+"F0.wireOp",EDGE,"E709"),sQuery(id+"F0.wireOp",EDGE,"E710"),sQuery(id+"F0.wireOp",EDGE,"E711"),sQuery(id+"F0.wireOp",EDGE,"E712"),sQuery(id+"F0.wireOp",EDGE,"E713"),sQuery(id+"F0.wireOp",EDGE,"E714"),sQuery(id+"F0.wireOp",EDGE,"E715"),sQuery(id+"F0.wireOp",EDGE,"E716"),sQuery(id+"F0.wireOp",EDGE,"E717"),sQuery(id+"F0.wireOp",EDGE,"E718"),sQuery(id+"F0.wireOp",EDGE,"E719"),sQuery(id+"F0.wireOp",EDGE,"E720"),sQuery(id+"F0.wireOp",EDGE,"E721"),sQuery(id+"F0.wireOp",EDGE,"E722"),sQuery(id+"F0.wireOp",EDGE,"E723"),sQuery(id+"F0.wireOp",EDGE,"E724"),sQuery(id+"F0.wireOp",EDGE,"E725"),sQuery(id+"F0.wireOp",EDGE,"E726"),sQuery(id+"F0.wireOp",EDGE,"E727"),sQuery(id+"F0.wireOp",EDGE,"E728"),sQuery(id+"F0.wireOp",EDGE,"E729"),sQuery(id+"F0.wireOp",EDGE,"E730"),sQuery(id+"F0.wireOp",EDGE,"E731"),sQuery(id+"F0.wireOp",EDGE,"E732"),sQuery(id+"F0.wireOp",EDGE,"E733"),sQuery(id+"F0.wireOp",EDGE,"E734"),sQuery(id+"F0.wireOp",EDGE,"E735"),sQuery(id+"F0.wireOp",EDGE,"E736"),sQuery(id+"F0.wireOp",EDGE,"E737"),sQuery(id+"F0.wireOp",EDGE,"E738"),sQuery(id+"F0.wireOp",EDGE,"E739"),sQuery(id+"F0.wireOp",EDGE,"E740"),sQuery(id+"F0.wireOp",EDGE,"E741"),sQuery(id+"F0.wireOp",EDGE,"E742"),sQuery(id+"F0.wireOp",EDGE,"E743"),sQuery(id+"F0.wireOp",EDGE,"E744"),sQuery(id+"F0.wireOp",EDGE,"E745"),sQuery(id+"F0.wireOp",EDGE,"E746"),sQuery(id+"F0.wireOp",EDGE,"E747"),sQuery(id+"F0.wireOp",EDGE,"E748"),sQuery(id+"F0.wireOp",EDGE,"E749"),sQuery(id+"F0.wireOp",EDGE,"E750"),sQuery(id+"F0.wireOp",EDGE,"E751"),sQuery(id+"F0.wireOp",EDGE,"E752"),sQuery(id+"F0.wireOp",EDGE,"E753"),sQuery(id+"F0.wireOp",EDGE,"E754"),sQuery(id+"F0.wireOp",EDGE,"E755"),sQuery(id+"F0.wireOp",EDGE,"E756"),sQuery(id+"F0.wireOp",EDGE,"E757"),sQuery(id+"F0.wireOp",EDGE,"E758"),sQuery(id+"F0.wireOp",EDGE,"E759"),sQuery(id+"F0.wireOp",EDGE,"E760"),sQuery(id+"F0.wireOp",EDGE,"E761"),sQuery(id+"F0.wireOp",EDGE,"E762"),sQuery(id+"F0.wireOp",EDGE,"E763"),sQuery(id+"F0.wireOp",EDGE,"E764"),sQuery(id+"F0.wireOp",EDGE,"E765"),sQuery(id+"F0.wireOp",EDGE,"E766"),sQuery(id+"F0.wireOp",EDGE,"E767"),sQuery(id+"F0.wireOp",EDGE,"E768"),sQuery(id+"F0.wireOp",EDGE,"E769"),sQuery(id+"F0.wireOp",EDGE,"E770"),sQuery(id+"F0.wireOp",EDGE,"E771"),sQuery(id+"F0.wireOp",EDGE,"E772"),sQuery(id+"F0.wireOp",EDGE,"E773"),sQuery(id+"F0.wireOp",EDGE,"E774"),sQuery(id+"F0.wireOp",EDGE,"E775"),sQuery(id+"F0.wireOp",EDGE,"E776"),sQuery(id+"F0.wireOp",EDGE,"E777"),sQuery(id+"F0.wireOp",EDGE,"E778"),sQuery(id+"F0.wireOp",EDGE,"E779"),sQuery(id+"F0.wireOp",EDGE,"E780"),sQuery(id+"F0.wireOp",EDGE,"E781"),sQuery(id+"F0.wireOp",EDGE,"E782"),sQuery(id+"F0.wireOp",EDGE,"E783"),sQuery(id+"F0.wireOp",EDGE,"E784"),sQuery(id+"F0.wireOp",EDGE,"E785"),sQuery(id+"F0.wireOp",EDGE,"E786"),sQuery(id+"F0.wireOp",EDGE,"E787"),sQuery(id+"F0.wireOp",EDGE,"E788"),sQuery(id+"F0.wireOp",EDGE,"E789"),sQuery(id+"F0.wireOp",EDGE,"E790"),sQuery(id+"F0.wireOp",EDGE,"E791"),sQuery(id+"F0.wireOp",EDGE,"E792"),sQuery(id+"F0.wireOp",EDGE,"E793"),sQuery(id+"F0.wireOp",EDGE,"E794"),sQuery(id+"F0.wireOp",EDGE,"E795"),sQuery(id+"F0.wireOp",EDGE,"E796"),sQuery(id+"F0.wireOp",EDGE,"E797"),sQuery(id+"F0.wireOp",EDGE,"E798"),sQuery(id+"F0.wireOp",EDGE,"E799"),sQuery(id+"F0.wireOp",EDGE,"E800"),sQuery(id+"F0.wireOp",EDGE,"E801"),sQuery(id+"F0.wireOp",EDGE,"E802"),sQuery(id+"F0.wireOp",EDGE,"E803"),sQuery(id+"F0.wireOp",EDGE,"E804"),sQuery(id+"F0.wireOp",EDGE,"E805"),sQuery(id+"F0.wireOp",EDGE,"E806"),sQuery(id+"F0.wireOp",EDGE,"E807"),sQuery(id+"F0.wireOp",EDGE,"E808"),sQuery(id+"F0.wireOp",EDGE,"E809"),sQuery(id+"F0.wireOp",EDGE,"E810"),sQuery(id+"F0.wireOp",EDGE,"E811"),sQuery(id+"F0.wireOp",EDGE,"E812"),sQuery(id+"F0.wireOp",EDGE,"E813"),sQuery(id+"F0.wireOp",EDGE,"E814"),sQuery(id+"F0.wireOp",EDGE,"E815"),sQuery(id+"F0.wireOp",EDGE,"E816"),sQuery(id+"F0.wireOp",EDGE,"E817"),sQuery(id+"F0.wireOp",EDGE,"E818"),sQuery(id+"F0.wireOp",EDGE,"E819"),sQuery(id+"F0.wireOp",EDGE,"E820"),sQuery(id+"F0.wireOp",EDGE,"E821"),sQuery(id+"F0.wireOp",EDGE,"E822"),sQuery(id+"F0.wireOp",EDGE,"E823"),sQuery(id+"F0.wireOp",EDGE,"E824"),sQuery(id+"F0.wireOp",EDGE,"E825"),sQuery(id+"F0.wireOp",EDGE,"E826"),sQuery(id+"F0.wireOp",EDGE,"E827"),sQuery(id+"F0.wireOp",EDGE,"E828"),sQuery(id+"F0.wireOp",EDGE,"E829"),sQuery(id+"F0.wireOp",EDGE,"E830"),sQuery(id+"F0.wireOp",EDGE,"E831"),sQuery(id+"F0.wireOp",EDGE,"E832"),sQuery(id+"F0.wireOp",EDGE,"E833"),sQuery(id+"F0.wireOp",EDGE,"E834"),sQuery(id+"F0.wireOp",EDGE,"E835"),sQuery(id+"F0.wireOp",EDGE,"E836"),sQuery(id+"F0.wireOp",EDGE,"E837"),sQuery(id+"F0.wireOp",EDGE,"E838"),sQuery(id+"F0.wireOp",EDGE,"E839"),sQuery(id+"F0.wireOp",EDGE,"E840"),sQuery(id+"F0.wireOp",EDGE,"E841"),sQuery(id+"F0.wireOp",EDGE,"E842"),sQuery(id+"F0.wireOp",EDGE,"E843"),sQuery(id+"F0.wireOp",EDGE,"E844"),sQuery(id+"F0.wireOp",EDGE,"E845"),sQuery(id+"F0.wireOp",EDGE,"E846"),sQuery(id+"F0.wireOp",EDGE,"E847"),sQuery(id+"F0.wireOp",EDGE,"E848"),sQuery(id+"F0.wireOp",EDGE,"E849"),sQuery(id+"F0.wireOp",EDGE,"E850"),sQuery(id+"F0.wireOp",EDGE,"E851"),sQuery(id+"F0.wireOp",EDGE,"E852"),sQuery(id+"F0.wireOp",EDGE,"E853"),sQuery(id+"F0.wireOp",EDGE,"E854"),sQuery(id+"F0.wireOp",EDGE,"E855"),sQuery(id+"F0.wireOp",EDGE,"E856"),sQuery(id+"F0.wireOp",EDGE,"E857"),sQuery(id+"F0.wireOp",EDGE,"E858"),sQuery(id+"F0.wireOp",EDGE,"E859"),sQuery(id+"F0.wireOp",EDGE,"E860"),sQuery(id+"F0.wireOp",EDGE,"E861"),sQuery(id+"F0.wireOp",EDGE,"E862"),sQuery(id+"F0.wireOp",EDGE,"E863"),sQuery(id+"F0.wireOp",EDGE,"E864"),sQuery(id+"F0.wireOp",EDGE,"E865"),sQuery(id+"F0.wireOp",EDGE,"E866"),sQuery(id+"F0.wireOp",EDGE,"E867"),sQuery(id+"F0.wireOp",EDGE,"E868"),sQuery(id+"F0.wireOp",EDGE,"E869"),sQuery(id+"F0.wireOp",EDGE,"E870"),sQuery(id+"F0.wireOp",EDGE,"E871"),sQuery(id+"F0.wireOp",EDGE,"E872"),sQuery(id+"F0.wireOp",EDGE,"E873"),sQuery(id+"F0.wireOp",EDGE,"E874"),sQuery(id+"F0.wireOp",EDGE,"E875"),sQuery(id+"F0.wireOp",EDGE,"E876"),sQuery(id+"F0.wireOp",EDGE,"E877"),sQuery(id+"F0.wireOp",EDGE,"E878"),sQuery(id+"F0.wireOp",EDGE,"E879"),sQuery(id+"F0.wireOp",EDGE,"E880"),sQuery(id+"F0.wireOp",EDGE,"E881"),sQuery(id+"F0.wireOp",EDGE,"E882"),sQuery(id+"F0.wireOp",EDGE,"E883"),sQuery(id+"F0.wireOp",EDGE,"E884"),sQuery(id+"F0.wireOp",EDGE,"E885"),sQuery(id+"F0.wireOp",EDGE,"E886"),sQuery(id+"F0.wireOp",EDGE,"E887"),sQuery(id+"F0.wireOp",EDGE,"E888"),sQuery(id+"F0.wireOp",EDGE,"E889"),sQuery(id+"F0.wireOp",EDGE,"E890"),sQuery(id+"F0.wireOp",EDGE,"E891"),sQuery(id+"F0.wireOp",EDGE,"E892"),sQuery(id+"F0.wireOp",EDGE,"E893"),sQuery(id+"F0.wireOp",EDGE,"E894"),sQuery(id+"F0.wireOp",EDGE,"E895"),sQuery(id+"F0.wireOp",EDGE,"E896"),sQuery(id+"F0.wireOp",EDGE,"E897"),sQuery(id+"F0.wireOp",EDGE,"E898"),sQuery(id+"F0.wireOp",EDGE,"E899"),sQuery(id+"F0.wireOp",EDGE,"E900"),sQuery(id+"F0.wireOp",EDGE,"E901"),sQuery(id+"F0.wireOp",EDGE,"E902"),sQuery(id+"F0.wireOp",EDGE,"E903"),sQuery(id+"F0.wireOp",EDGE,"E904"),sQuery(id+"F0.wireOp",EDGE,"E905"),sQuery(id+"F0.wireOp",EDGE,"E906"),sQuery(id+"F0.wireOp",EDGE,"E907"),sQuery(id+"F0.wireOp",EDGE,"E908"),sQuery(id+"F0.wireOp",EDGE,"E909"),sQuery(id+"F0.wireOp",EDGE,"E910"),sQuery(id+"F0.wireOp",EDGE,"E911"),sQuery(id+"F0.wireOp",EDGE,"E912"),sQuery(id+"F0.wireOp",EDGE,"E913"),sQuery(id+"F0.wireOp",EDGE,"E914"),sQuery(id+"F0.wireOp",EDGE,"E915"),sQuery(id+"F0.wireOp",EDGE,"E916"),sQuery(id+"F0.wireOp",EDGE,"E917"),sQuery(id+"F0.wireOp",EDGE,"E918"),sQuery(id+"F0.wireOp",EDGE,"E919"),sQuery(id+"F0.wireOp",EDGE,"E920"),sQuery(id+"F0.wireOp",EDGE,"E921"),sQuery(id+"F0.wireOp",EDGE,"E922"),sQuery(id+"F0.wireOp",EDGE,"E923"),sQuery(id+"F0.wireOp",EDGE,"E924"),sQuery(id+"F0.wireOp",EDGE,"E925"),sQuery(id+"F0.wireOp",EDGE,"E926"),sQuery(id+"F0.wireOp",EDGE,"E927"),sQuery(id+"F0.wireOp",EDGE,"E928"),sQuery(id+"F0.wireOp",EDGE,"E929"),sQuery(id+"F0.wireOp",EDGE,"E930"),sQuery(id+"F0.wireOp",EDGE,"E931"),sQuery(id+"F0.wireOp",EDGE,"E932"),sQuery(id+"F0.wireOp",EDGE,"E933"),sQuery(id+"F0.wireOp",EDGE,"E934"),sQuery(id+"F0.wireOp",EDGE,"E935"),sQuery(id+"F0.wireOp",EDGE,"E936"),sQuery(id+"F0.wireOp",EDGE,"E937"),sQuery(id+"F0.wireOp",EDGE,"E938"),sQuery(id+"F0.wireOp",EDGE,"E939"),sQuery(id+"F0.wireOp",EDGE,"E940"),sQuery(id+"F0.wireOp",EDGE,"E941"),sQuery(id+"F0.wireOp",EDGE,"E942"),sQuery(id+"F0.wireOp",EDGE,"E943"),sQuery(id+"F0.wireOp",EDGE,"E944"),sQuery(id+"F0.wireOp",EDGE,"E945"),sQuery(id+"F0.wireOp",EDGE,"E946"),sQuery(id+"F0.wireOp",EDGE,"E947"),sQuery(id+"F0.wireOp",EDGE,"E948"),sQuery(id+"F0.wireOp",EDGE,"E949"),sQuery(id+"F0.wireOp",EDGE,"E950"),sQuery(id+"F0.wireOp",EDGE,"E951"),sQuery(id+"F0.wireOp",EDGE,"E952"),sQuery(id+"F0.wireOp",EDGE,"E953"),sQuery(id+"F0.wireOp",EDGE,"E954"),sQuery(id+"F0.wireOp",EDGE,"E955"),sQuery(id+"F0.wireOp",EDGE,"E956"),sQuery(id+"F0.wireOp",EDGE,"E957"),sQuery(id+"F0.wireOp",EDGE,"E958"),sQuery(id+"F0.wireOp",EDGE,"E959"),sQuery(id+"F0.wireOp",EDGE,"E960"),sQuery(id+"F0.wireOp",EDGE,"E961"),sQuery(id+"F0.wireOp",EDGE,"E962"),sQuery(id+"F0.wireOp",EDGE,"E963"),sQuery(id+"F0.wireOp",EDGE,"E964"),sQuery(id+"F0.wireOp",EDGE,"E965"),sQuery(id+"F0.wireOp",EDGE,"E966"),sQuery(id+"F0.wireOp",EDGE,"E967"),sQuery(id+"F0.wireOp",EDGE,"E968"),sQuery(id+"F0.wireOp",EDGE,"E969"),sQuery(id+"F0.wireOp",EDGE,"E970"),sQuery(id+"F0.wireOp",EDGE,"E971"),sQuery(id+"F0.wireOp",EDGE,"E972"),sQuery(id+"F0.wireOp",EDGE,"E973"),sQuery(id+"F0.wireOp",EDGE,"E974"),sQuery(id+"F0.wireOp",EDGE,"E975"),sQuery(id+"F0.wireOp",EDGE,"E976"),sQuery(id+"F0.wireOp",EDGE,"E977"),sQuery(id+"F0.wireOp",EDGE,"E978"),sQuery(id+"F0.wireOp",EDGE,"E979"),sQuery(id+"F0.wireOp",EDGE,"E980"),sQuery(id+"F0.wireOp",EDGE,"E981"),sQuery(id+"F0.wireOp",EDGE,"E982"),sQuery(id+"F0.wireOp",EDGE,"E983"),sQuery(id+"F0.wireOp",EDGE,"E984"),sQuery(id+"F0.wireOp",EDGE,"E985"),sQuery(id+"F0.wireOp",EDGE,"E986"),sQuery(id+"F0.wireOp",EDGE,"E987"),sQuery(id+"F0.wireOp",EDGE,"E988"),sQuery(id+"F0.wireOp",EDGE,"E989"),sQuery(id+"F0.wireOp",EDGE,"E990"),sQuery(id+"F0.wireOp",EDGE,"E991"),sQuery(id+"F0.wireOp",EDGE,"E992"),sQuery(id+"F0.wireOp",EDGE,"E993"),sQuery(id+"F0.wireOp",EDGE,"E994"),sQuery(id+"F0.wireOp",EDGE,"E995"),sQuery(id+"F0.wireOp",EDGE,"E996"),sQuery(id+"F0.wireOp",EDGE,"E997"),sQuery(id+"F0.wireOp",EDGE,"E998"),sQuery(id+"F0.wireOp",EDGE,"E999"),sQuery(id+"F0.wireOp",EDGE,"E1000"),sQuery(id+"F0.wireOp",EDGE,"E1001"),sQuery(id+"F0.wireOp",EDGE,"E1002"),sQuery(id+"F0.wireOp",EDGE,"E1003"),sQuery(id+"F0.wireOp",EDGE,"E1004"),sQuery(id+"F0.wireOp",EDGE,"E1005"),sQuery(id+"F0.wireOp",EDGE,"E1006"),sQuery(id+"F0.wireOp",EDGE,"E1007"),sQuery(id+"F0.wireOp",EDGE,"E1008"),sQuery(id+"F0.wireOp",EDGE,"E1009"),sQuery(id+"F0.wireOp",EDGE,"E1010"),sQuery(id+"F0.wireOp",EDGE,"E1011"),sQuery(id+"F0.wireOp",EDGE,"E1012"),sQuery(id+"F0.wireOp",EDGE,"E1013"),sQuery(id+"F0.wireOp",EDGE,"E1014"),sQuery(id+"F0.wireOp",EDGE,"E1015"),sQuery(id+"F0.wireOp",EDGE,"E1016"),sQuery(id+"F0.wireOp",EDGE,"E1017"),sQuery(id+"F0.wireOp",EDGE,"E1018"),sQuery(id+"F0.wireOp",EDGE,"E1019"),sQuery(id+"F0.wireOp",EDGE,"E1020"),sQuery(id+"F0.wireOp",EDGE,"E1021"),sQuery(id+"F0.wireOp",EDGE,"E1022"),sQuery(id+"F0.wireOp",EDGE,"E1023"),sQuery(id+"F0.wireOp",EDGE,"E1024"),sQuery(id+"F0.wireOp",EDGE,"E1025"),sQuery(id+"F0.wireOp",EDGE,"E1026"),sQuery(id+"F0.wireOp",EDGE,"E1027"),sQuery(id+"F0.wireOp",EDGE,"E1028"),sQuery(id+"F0.wireOp",EDGE,"E1029"),sQuery(id+"F0.wireOp",EDGE,"E1030"),sQuery(id+"F0.wireOp",EDGE,"E1031"),sQuery(id+"F0.wireOp",EDGE,"E1032"),sQuery(id+"F0.wireOp",EDGE,"E1033"),sQuery(id+"F0.wireOp",EDGE,"E1034"),sQuery(id+"F0.wireOp",EDGE,"E1035"),sQuery(id+"F0.wireOp",EDGE,"E1036"),sQuery(id+"F0.wireOp",EDGE,"E1037"),sQuery(id+"F0.wireOp",EDGE,"E1038"),sQuery(id+"F0.wireOp",EDGE,"E1039"),sQuery(id+"F0.wireOp",EDGE,"E1040"),sQuery(id+"F0.wireOp",EDGE,"E1041"),sQuery(id+"F0.wireOp",EDGE,"E1042"),sQuery(id+"F0.wireOp",EDGE,"E1043"),sQuery(id+"F0.wireOp",EDGE,"E1044"),sQuery(id+"F0.wireOp",EDGE,"E1045"),sQuery(id+"F0.wireOp",EDGE,"E1046"),sQuery(id+"F0.wireOp",EDGE,"E1047"),sQuery(id+"F0.wireOp",EDGE,"E1048"),sQuery(id+"F0.wireOp",EDGE,"E1049"),sQuery(id+"F0.wireOp",EDGE,"E1050"),sQuery(id+"F0.wireOp",EDGE,"E1051"),sQuery(id+"F0.wireOp",EDGE,"E1052"),sQuery(id+"F0.wireOp",EDGE,"E1053"),sQuery(id+"F0.wireOp",EDGE,"E1054"),sQuery(id+"F0.wireOp",EDGE,"E1055"),sQuery(id+"F0.wireOp",EDGE,"E1056"),sQuery(id+"F0.wireOp",EDGE,"E1057"),sQuery(id+"F0.wireOp",EDGE,"E1058"),sQuery(id+"F0.wireOp",EDGE,"E1059"),sQuery(id+"F0.wireOp",EDGE,"E1060"),sQuery(id+"F0.wireOp",EDGE,"E1061"),sQuery(id+"F0.wireOp",EDGE,"E1062"),sQuery(id+"F0.wireOp",EDGE,"E1063"),sQuery(id+"F0.wireOp",EDGE,"E1064"),sQuery(id+"F0.wireOp",EDGE,"E1065"),sQuery(id+"F0.wireOp",EDGE,"E1066"),sQuery(id+"F0.wireOp",EDGE,"E1067"),sQuery(id+"F0.wireOp",EDGE,"E1068"),sQuery(id+"F0.wireOp",EDGE,"E1069"),sQuery(id+"F0.wireOp",EDGE,"E1070"),sQuery(id+"F0.wireOp",EDGE,"E1071"),sQuery(id+"F0.wireOp",EDGE,"E1072"),sQuery(id+"F0.wireOp",EDGE,"E1073"),sQuery(id+"F0.wireOp",EDGE,"E1074"),sQuery(id+"F0.wireOp",EDGE,"E1075"),sQuery(id+"F0.wireOp",EDGE,"E1076"),sQuery(id+"F0.wireOp",EDGE,"E1077"),sQuery(id+"F0.wireOp",EDGE,"E1078"),sQuery(id+"F0.wireOp",EDGE,"E1079"),sQuery(id+"F0.wireOp",EDGE,"E1080"),sQuery(id+"F0.wireOp",EDGE,"E1081"),sQuery(id+"F0.wireOp",EDGE,"E1082"),sQuery(id+"F0.wireOp",EDGE,"E1083"),sQuery(id+"F0.wireOp",EDGE,"E1084"),sQuery(id+"F0.wireOp",EDGE,"E1085"),sQuery(id+"F0.wireOp",EDGE,"E1086"),sQuery(id+"F0.wireOp",EDGE,"E1087"),sQuery(id+"F0.wireOp",EDGE,"E1088"),sQuery(id+"F0.wireOp",EDGE,"E1089"),sQuery(id+"F0.wireOp",EDGE,"E1090"),sQuery(id+"F0.wireOp",EDGE,"E1091"),sQuery(id+"F0.wireOp",EDGE,"E1092"),sQuery(id+"F0.wireOp",EDGE,"E1093"),sQuery(id+"F0.wireOp",EDGE,"E1094"),sQuery(id+"F0.wireOp",EDGE,"E1095"),sQuery(id+"F0.wireOp",EDGE,"E1096"),sQuery(id+"F0.wireOp",EDGE,"E1097"),sQuery(id+"F0.wireOp",EDGE,"E1098"),sQuery(id+"F0.wireOp",EDGE,"E1099"),sQuery(id+"F0.wireOp",EDGE,"E1100"),sQuery(id+"F0.wireOp",EDGE,"E1101"),sQuery(id+"F0.wireOp",EDGE,"E1102"),sQuery(id+"F0.wireOp",EDGE,"E1103"),sQuery(id+"F0.wireOp",EDGE,"E1104"),sQuery(id+"F0.wireOp",EDGE,"E1105"),sQuery(id+"F0.wireOp",EDGE,"E1106"),sQuery(id+"F0.wireOp",EDGE,"E1107"),sQuery(id+"F0.wireOp",EDGE,"E1108"),sQuery(id+"F0.wireOp",EDGE,"E1109"),sQuery(id+"F0.wireOp",EDGE,"E1110"),sQuery(id+"F0.wireOp",EDGE,"E1111"),sQuery(id+"F0.wireOp",EDGE,"E1112"),sQuery(id+"F0.wireOp",EDGE,"E1113"),sQuery(id+"F0.wireOp",EDGE,"E1114"),sQuery(id+"F0.wireOp",EDGE,"E1115"),sQuery(id+"F0.wireOp",EDGE,"E1116"),sQuery(id+"F0.wireOp",EDGE,"E1117"),sQuery(id+"F0.wireOp",EDGE,"E1118"),sQuery(id+"F0.wireOp",EDGE,"E1119"),sQuery(id+"F0.wireOp",EDGE,"E1120"),sQuery(id+"F0.wireOp",EDGE,"E1121"),sQuery(id+"F0.wireOp",EDGE,"E1122"),sQuery(id+"F0.wireOp",EDGE,"E1123"),sQuery(id+"F0.wireOp",EDGE,"E1124"),sQuery(id+"F0.wireOp",EDGE,"E1125"),sQuery(id+"F0.wireOp",EDGE,"E1126"),sQuery(id+"F0.wireOp",EDGE,"E1127"),sQuery(id+"F0.wireOp",EDGE,"E1128"),sQuery(id+"F0.wireOp",EDGE,"E1129"),sQuery(id+"F0.wireOp",EDGE,"E1130"),sQuery(id+"F0.wireOp",EDGE,"E1131"),sQuery(id+"F0.wireOp",EDGE,"E1132"),sQuery(id+"F0.wireOp",EDGE,"E1133"),sQuery(id+"F0.wireOp",EDGE,"E1134"),sQuery(id+"F0.wireOp",EDGE,"E1135"),sQuery(id+"F0.wireOp",EDGE,"E1136"),sQuery(id+"F0.wireOp",EDGE,"E1137"),sQuery(id+"F0.wireOp",EDGE,"E1138"),sQuery(id+"F0.wireOp",EDGE,"E1139"),sQuery(id+"F0.wireOp",EDGE,"E1140"),sQuery(id+"F0.wireOp",EDGE,"E1141"),sQuery(id+"F0.wireOp",EDGE,"E1142"),sQuery(id+"F0.wireOp",EDGE,"E1143"),sQuery(id+"F0.wireOp",EDGE,"E1144"),sQuery(id+"F0.wireOp",EDGE,"E1145"),sQuery(id+"F0.wireOp",EDGE,"E1146"),sQuery(id+"F0.wireOp",EDGE,"E1147"),sQuery(id+"F0.wireOp",EDGE,"E1148"),sQuery(id+"F0.wireOp",EDGE,"E1149"),sQuery(id+"F0.wireOp",EDGE,"E1150"),sQuery(id+"F0.wireOp",EDGE,"E1151"),sQuery(id+"F0.wireOp",EDGE,"E1152"),sQuery(id+"F0.wireOp",EDGE,"E1153"),sQuery(id+"F0.wireOp",EDGE,"E1154"),sQuery(id+"F0.wireOp",EDGE,"E1155"),sQuery(id+"F0.wireOp",EDGE,"E1156"),sQuery(id+"F0.wireOp",EDGE,"E1157"),sQuery(id+"F0.wireOp",EDGE,"E1158"),sQuery(id+"F0.wireOp",EDGE,"E1159"),sQuery(id+"F0.wireOp",EDGE,"E1160"),sQuery(id+"F0.wireOp",EDGE,"E1161"),sQuery(id+"F0.wireOp",EDGE,"E1162"),sQuery(id+"F0.wireOp",EDGE,"E1163"),sQuery(id+"F0.wireOp",EDGE,"E1164"),sQuery(id+"F0.wireOp",EDGE,"E1165"),sQuery(id+"F0.wireOp",EDGE,"E1166"),sQuery(id+"F0.wireOp",EDGE,"E1167"),sQuery(id+"F0.wireOp",EDGE,"E1168"),sQuery(id+"F0.wireOp",EDGE,"E1169"),sQuery(id+"F0.wireOp",EDGE,"E1170"),sQuery(id+"F0.wireOp",EDGE,"E1171"),sQuery(id+"F0.wireOp",EDGE,"E1172"),sQuery(id+"F0.wireOp",EDGE,"E1173"),sQuery(id+"F0.wireOp",EDGE,"E1174"),sQuery(id+"F0.wireOp",EDGE,"E1175"),sQuery(id+"F0.wireOp",EDGE,"E1176"),sQuery(id+"F0.wireOp",EDGE,"E1177"),sQuery(id+"F0.wireOp",EDGE,"E1178"),sQuery(id+"F0.wireOp",EDGE,"E1179"),sQuery(id+"F0.wireOp",EDGE,"E1180"),sQuery(id+"F0.wireOp",EDGE,"E1181"),sQuery(id+"F0.wireOp",EDGE,"E1182"),sQuery(id+"F0.wireOp",EDGE,"E1183"),sQuery(id+"F0.wireOp",EDGE,"E1184"),sQuery(id+"F0.wireOp",EDGE,"E1185"),sQuery(id+"F0.wireOp",EDGE,"E1186"),sQuery(id+"F0.wireOp",EDGE,"E1187"),sQuery(id+"F0.wireOp",EDGE,"E1188"),sQuery(id+"F0.wireOp",EDGE,"E1189"),sQuery(id+"F0.wireOp",EDGE,"E1190"),sQuery(id+"F0.wireOp",EDGE,"E1191"),sQuery(id+"F0.wireOp",EDGE,"E1192"),sQuery(id+"F0.wireOp",EDGE,"E1193"),sQuery(id+"F0.wireOp",EDGE,"E1194"),sQuery(id+"F0.wireOp",EDGE,"E1195"),sQuery(id+"F0.wireOp",EDGE,"E1196"),sQuery(id+"F0.wireOp",EDGE,"E1197"),sQuery(id+"F0.wireOp",EDGE,"E1198"),sQuery(id+"F0.wireOp",EDGE,"E1199"),sQuery(id+"F0.wireOp",EDGE,"E1200"),sQuery(id+"F0.wireOp",EDGE,"E1201"),sQuery(id+"F0.wireOp",EDGE,"E1202"),sQuery(id+"F0.wireOp",EDGE,"E1203"),sQuery(id+"F0.wireOp",EDGE,"E1204"),sQuery(id+"F0.wireOp",EDGE,"E1205"),sQuery(id+"F0.wireOp",EDGE,"E1206"),sQuery(id+"F0.wireOp",EDGE,"E1207"),sQuery(id+"F0.wireOp",EDGE,"E1208"),sQuery(id+"F0.wireOp",EDGE,"E1209"),sQuery(id+"F0.wireOp",EDGE,"E1210"),sQuery(id+"F0.wireOp",EDGE,"E1211"),sQuery(id+"F0.wireOp",EDGE,"E1212"),sQuery(id+"F0.wireOp",EDGE,"E1213"),sQuery(id+"F0.wireOp",EDGE,"E1214"),sQuery(id+"F0.wireOp",EDGE,"E1215"),sQuery(id+"F0.wireOp",EDGE,"E1216"),sQuery(id+"F0.wireOp",EDGE,"E1217"),sQuery(id+"F0.wireOp",EDGE,"E1218"),sQuery(id+"F0.wireOp",EDGE,"E1219"),sQuery(id+"F0.wireOp",EDGE,"E1220"),sQuery(id+"F0.wireOp",EDGE,"E1221"),sQuery(id+"F0.wireOp",EDGE,"E1222"),sQuery(id+"F0.wireOp",EDGE,"E1223"),sQuery(id+"F0.wireOp",EDGE,"E1224"),sQuery(id+"F0.wireOp",EDGE,"E1225"),sQuery(id+"F0.wireOp",EDGE,"E1226"),sQuery(id+"F0.wireOp",EDGE,"E1227"),sQuery(id+"F0.wireOp",EDGE,"E1228"),sQuery(id+"F0.wireOp",EDGE,"E1229"),sQuery(id+"F0.wireOp",EDGE,"E1230"),sQuery(id+"F0.wireOp",EDGE,"E1231"),sQuery(id+"F0.wireOp",EDGE,"E1232"),sQuery(id+"F0.wireOp",EDGE,"E1233"),sQuery(id+"F0.wireOp",EDGE,"E1234"),sQuery(id+"F0.wireOp",EDGE,"E1235"),sQuery(id+"F0.wireOp",EDGE,"E1236"),sQuery(id+"F0.wireOp",EDGE,"E1237"),sQuery(id+"F0.wireOp",EDGE,"E1238"),sQuery(id+"F0.wireOp",EDGE,"E1239"),sQuery(id+"F0.wireOp",EDGE,"E1240"),sQuery(id+"F0.wireOp",EDGE,"E1241"),sQuery(id+"F0.wireOp",EDGE,"E1242"),sQuery(id+"F0.wireOp",EDGE,"E1243"),sQuery(id+"F0.wireOp",EDGE,"E1244"),sQuery(id+"F0.wireOp",EDGE,"E1245"),sQuery(id+"F0.wireOp",EDGE,"E1246"),sQuery(id+"F0.wireOp",EDGE,"E1247"),sQuery(id+"F0.wireOp",EDGE,"E1248"),sQuery(id+"F0.wireOp",EDGE,"E1249"),sQuery(id+"F0.wireOp",EDGE,"E1250"),sQuery(id+"F0.wireOp",EDGE,"E1251"),sQuery(id+"F0.wireOp",EDGE,"E1252"),sQuery(id+"F0.wireOp",EDGE,"E1253"),sQuery(id+"F0.wireOp",EDGE,"E1254"),sQuery(id+"F0.wireOp",EDGE,"E1255"),sQuery(id+"F0.wireOp",EDGE,"E1256"),sQuery(id+"F0.wireOp",EDGE,"E1257"),sQuery(id+"F0.wireOp",EDGE,"E1258"),sQuery(id+"F0.wireOp",EDGE,"E1259"),sQuery(id+"F0.wireOp",EDGE,"E1260"),sQuery(id+"F0.wireOp",EDGE,"E1261"),sQuery(id+"F0.wireOp",EDGE,"E1262"),sQuery(id+"F0.wireOp",EDGE,"E1263"),sQuery(id+"F0.wireOp",EDGE,"E1264"),sQuery(id+"F0.wireOp",EDGE,"E1265"),sQuery(id+"F0.wireOp",EDGE,"E1266"),sQuery(id+"F0.wireOp",EDGE,"E1267"),sQuery(id+"F0.wireOp",EDGE,"E1268"),sQuery(id+"F0.wireOp",EDGE,"E1269"),sQuery(id+"F0.wireOp",EDGE,"E1270"),sQuery(id+"F0.wireOp",EDGE,"E1271"),sQuery(id+"F0.wireOp",EDGE,"E1272"),sQuery(id+"F0.wireOp",EDGE,"E1273"),sQuery(id+"F0.wireOp",EDGE,"E1274"),sQuery(id+"F0.wireOp",EDGE,"E1275"),sQuery(id+"F0.wireOp",EDGE,"E1276"),sQuery(id+"F0.wireOp",EDGE,"E1277"),sQuery(id+"F0.wireOp",EDGE,"E1278"),sQuery(id+"F0.wireOp",EDGE,"E1279"),sQuery(id+"F0.wireOp",EDGE,"E1280"),sQuery(id+"F0.wireOp",EDGE,"E1281"),sQuery(id+"F0.wireOp",EDGE,"E1282"),sQuery(id+"F0.wireOp",EDGE,"E1283"),sQuery(id+"F0.wireOp",EDGE,"E1284"),sQuery(id+"F0.wireOp",EDGE,"E1285"),sQuery(id+"F0.wireOp",EDGE,"E1286"),sQuery(id+"F0.wireOp",EDGE,"E1287"),sQuery(id+"F0.wireOp",EDGE,"E1288"),sQuery(id+"F0.wireOp",EDGE,"E1289"),sQuery(id+"F0.wireOp",EDGE,"E1290"),sQuery(id+"F0.wireOp",EDGE,"E1291"),sQuery(id+"F0.wireOp",EDGE,"E1292"),sQuery(id+"F0.wireOp",EDGE,"E1293"),sQuery(id+"F0.wireOp",EDGE,"E1294"),sQuery(id+"F0.wireOp",EDGE,"E1295"),sQuery(id+"F0.wireOp",EDGE,"E1296"),sQuery(id+"F0.wireOp",EDGE,"E1297"),sQuery(id+"F0.wireOp",EDGE,"E1298"),sQuery(id+"F0.wireOp",EDGE,"E1299"),sQuery(id+"F0.wireOp",EDGE,"E1300"),sQuery(id+"F0.wireOp",EDGE,"E1301"),sQuery(id+"F0.wireOp",EDGE,"E1302"),sQuery(id+"F0.wireOp",EDGE,"E1303"),sQuery(id+"F0.wireOp",EDGE,"E1304"),sQuery(id+"F0.wireOp",EDGE,"E1305"),sQuery(id+"F0.wireOp",EDGE,"E1306"),sQuery(id+"F0.wireOp",EDGE,"E1307"),sQuery(id+"F0.wireOp",EDGE,"E1308"),sQuery(id+"F0.wireOp",EDGE,"E1309"),sQuery(id+"F0.wireOp",EDGE,"E1310"),sQuery(id+"F0.wireOp",EDGE,"E1311"),sQuery(id+"F0.wireOp",EDGE,"E1312"),sQuery(id+"F0.wireOp",EDGE,"E1313"),sQuery(id+"F0.wireOp",EDGE,"E1314"),sQuery(id+"F0.wireOp",EDGE,"E1315"),sQuery(id+"F0.wireOp",EDGE,"E1316"),sQuery(id+"F0.wireOp",EDGE,"E1317"),sQuery(id+"F0.wireOp",EDGE,"E1318"),sQuery(id+"F0.wireOp",EDGE,"E1319"),sQuery(id+"F0.wireOp",EDGE,"E1320"),sQuery(id+"F0.wireOp",EDGE,"E1321"),sQuery(id+"F0.wireOp",EDGE,"E1322"),sQuery(id+"F0.wireOp",EDGE,"E1323"),sQuery(id+"F0.wireOp",EDGE,"E1324"),sQuery(id+"F0.wireOp",EDGE,"E1325"),sQuery(id+"F0.wireOp",EDGE,"E1326"),sQuery(id+"F0.wireOp",EDGE,"E1327"),sQuery(id+"F0.wireOp",EDGE,"E1328"),sQuery(id+"F0.wireOp",EDGE,"E1329"),sQuery(id+"F0.wireOp",EDGE,"E1330"),sQuery(id+"F0.wireOp",EDGE,"E1331"),sQuery(id+"F0.wireOp",EDGE,"E1332"),sQuery(id+"F0.wireOp",EDGE,"E1333"),sQuery(id+"F0.wireOp",EDGE,"E1334"),sQuery(id+"F0.wireOp",EDGE,"E1335"),sQuery(id+"F0.wireOp",EDGE,"E1336"),sQuery(id+"F0.wireOp",EDGE,"E1337"),sQuery(id+"F0.wireOp",EDGE,"E1338"),sQuery(id+"F0.wireOp",EDGE,"E1339"),sQuery(id+"F0.wireOp",EDGE,"E1340"),sQuery(id+"F0.wireOp",EDGE,"E1341"),sQuery(id+"F0.wireOp",EDGE,"E1342"),sQuery(id+"F0.wireOp",EDGE,"E1343"),sQuery(id+"F0.wireOp",EDGE,"E1344"),sQuery(id+"F0.wireOp",EDGE,"E1345"),sQuery(id+"F0.wireOp",EDGE,"E1346"),sQuery(id+"F0.wireOp",EDGE,"E1347"),sQuery(id+"F0.wireOp",EDGE,"E1348"),sQuery(id+"F0.wireOp",EDGE,"E1349"),sQuery(id+"F0.wireOp",EDGE,"E1350"),sQuery(id+"F0.wireOp",EDGE,"E1351"),sQuery(id+"F0.wireOp",EDGE,"E1352"),sQuery(id+"F0.wireOp",EDGE,"E1353"),sQuery(id+"F0.wireOp",EDGE,"E1354"),sQuery(id+"F0.wireOp",EDGE,"E1355"),sQuery(id+"F0.wireOp",EDGE,"E1356"),sQuery(id+"F0.wireOp",EDGE,"E1357"),sQuery(id+"F0.wireOp",EDGE,"E1358"),sQuery(id+"F0.wireOp",EDGE,"E1359"),sQuery(id+"F0.wireOp",EDGE,"E1360"),sQuery(id+"F0.wireOp",EDGE,"E1361"),sQuery(id+"F0.wireOp",EDGE,"E1362"),sQuery(id+"F0.wireOp",EDGE,"E1363"),sQuery(id+"F0.wireOp",EDGE,"E1364"),sQuery(id+"F0.wireOp",EDGE,"E1365"),sQuery(id+"F0.wireOp",EDGE,"E1366"),sQuery(id+"F0.wireOp",EDGE,"E1367"),sQuery(id+"F0.wireOp",EDGE,"E1368"),sQuery(id+"F0.wireOp",EDGE,"E1369"),sQuery(id+"F0.wireOp",EDGE,"E1370"),sQuery(id+"F0.wireOp",EDGE,"E1371"),sQuery(id+"F0.wireOp",EDGE,"E1372"),sQuery(id+"F0.wireOp",EDGE,"E1373"),sQuery(id+"F0.wireOp",EDGE,"E1374"),sQuery(id+"F0.wireOp",EDGE,"E1375"),sQuery(id+"F0.wireOp",EDGE,"E1376"),sQuery(id+"F0.wireOp",EDGE,"E1377"),sQuery(id+"F0.wireOp",EDGE,"E1378"),sQuery(id+"F0.wireOp",EDGE,"E1379"),sQuery(id+"F0.wireOp",EDGE,"E1380"),sQuery(id+"F0.wireOp",EDGE,"E1381"),sQuery(id+"F0.wireOp",EDGE,"E1382"),sQuery(id+"F0.wireOp",EDGE,"E1383"),sQuery(id+"F0.wireOp",EDGE,"E1384"),sQuery(id+"F0.wireOp",EDGE,"E1385"),sQuery(id+"F0.wireOp",EDGE,"E1386"),sQuery(id+"F0.wireOp",EDGE,"E1387"),sQuery(id+"F0.wireOp",EDGE,"E1388"),sQuery(id+"F0.wireOp",EDGE,"E1389"),sQuery(id+"F0.wireOp",EDGE,"E1390"),sQuery(id+"F0.wireOp",EDGE,"E1391"),sQuery(id+"F0.wireOp",EDGE,"E1392"),sQuery(id+"F0.wireOp",EDGE,"E1393"),sQuery(id+"F0.wireOp",EDGE,"E1394"),sQuery(id+"F0.wireOp",EDGE,"E1395"),sQuery(id+"F0.wireOp",EDGE,"E1396"),sQuery(id+"F0.wireOp",EDGE,"E1397"),sQuery(id+"F0.wireOp",EDGE,"E1398"),sQuery(id+"F0.wireOp",EDGE,"E1399"),sQuery(id+"F0.wireOp",EDGE,"E1400"),sQuery(id+"F0.wireOp",EDGE,"E1401"),sQuery(id+"F0.wireOp",EDGE,"E1402"),sQuery(id+"F0.wireOp",EDGE,"E1403"),sQuery(id+"F0.wireOp",EDGE,"E1404"),sQuery(id+"F0.wireOp",EDGE,"E1405"),sQuery(id+"F0.wireOp",EDGE,"E1406"),sQuery(id+"F0.wireOp",EDGE,"E1407"),sQuery(id+"F0.wireOp",EDGE,"E1408"),sQuery(id+"F0.wireOp",EDGE,"E1409"),sQuery(id+"F0.wireOp",EDGE,"E1410"),sQuery(id+"F0.wireOp",EDGE,"E1411"),sQuery(id+"F0.wireOp",EDGE,"E1412"),sQuery(id+"F0.wireOp",EDGE,"E1413"),sQuery(id+"F0.wireOp",EDGE,"E1414"),sQuery(id+"F0.wireOp",EDGE,"E1415"),sQuery(id+"F0.wireOp",EDGE,"E1416"),sQuery(id+"F0.wireOp",EDGE,"E1417"),sQuery(id+"F0.wireOp",EDGE,"E1418"),sQuery(id+"F0.wireOp",EDGE,"E1419"),sQuery(id+"F0.wireOp",EDGE,"E1420"),sQuery(id+"F0.wireOp",EDGE,"E1421"),sQuery(id+"F0.wireOp",EDGE,"E1422"),sQuery(id+"F0.wireOp",EDGE,"E1423"),sQuery(id+"F0.wireOp",EDGE,"E1424"),sQuery(id+"F0.wireOp",EDGE,"E1425"),sQuery(id+"F0.wireOp",EDGE,"E1426"),sQuery(id+"F0.wireOp",EDGE,"E1427"),sQuery(id+"F0.wireOp",EDGE,"E1428"),sQuery(id+"F0.wireOp",EDGE,"E1429"),sQuery(id+"F0.wireOp",EDGE,"E1430"),sQuery(id+"F0.wireOp",EDGE,"E1431"),sQuery(id+"F0.wireOp",EDGE,"E1432"),sQuery(id+"F0.wireOp",EDGE,"E1433"),sQuery(id+"F0.wireOp",EDGE,"E1434"),sQuery(id+"F0.wireOp",EDGE,"E1435"),sQuery(id+"F0.wireOp",EDGE,"E1436"),sQuery(id+"F0.wireOp",EDGE,"E1437"),sQuery(id+"F0.wireOp",EDGE,"E1438"),sQuery(id+"F0.wireOp",EDGE,"E1439"),sQuery(id+"F0.wireOp",EDGE,"E1440"),sQuery(id+"F0.wireOp",EDGE,"E1441"),sQuery(id+"F0.wireOp",EDGE,"E1442"),sQuery(id+"F0.wireOp",EDGE,"E1443"),sQuery(id+"F0.wireOp",EDGE,"E1444"),sQuery(id+"F0.wireOp",EDGE,"E1445"),sQuery(id+"F0.wireOp",EDGE,"E1446"),sQuery(id+"F0.wireOp",EDGE,"E1447")])],"isStart":false});
            var sketch = newSketch(context, id + "F3", { "sketchPlane" : qUnion([Q0])});
            skLineSegment(sketch, "E1448.bottom", {"start": v(-23.9, 9.9) * mm, "end": v(21.54, 9.9) * mm});
            skLineSegment(sketch, "E1448.top", {"start": v(-23.9, -9.9) * mm, "end": v(21.54, -9.9) * mm});
            skLineSegment(sketch, "E1448.left", {"start": v(-23.9, 9.9) * mm, "end": v(-23.9, -9.9) * mm});
            skLineSegment(sketch, "E1448.right", {"start": v(21.54, 9.9) * mm, "end": v(21.54, -9.9) * mm});
            skPoint(sketch, "E1448.middle", {"position": v(-1.18, 0) * mm});
            skSolve(sketch);
        }
        {
            var Q0;
            Q0 = qSketchRegion(id + "F3", true);
            extrude(context, id + "F4", {"entities" : qUnion([Q0]), "depth" : 6 * mm, "offsetDistance" : 25 * mm});
        }
        {
            var Q0;
            Q0=makeQuery(id+"F1.opExtrude","CAP_FACE",FACE,{"disambiguationData":[OSD([sQuery(id+"F0.wireOp",EDGE,"E0"),sQuery(id+"F0.wireOp",EDGE,"E1"),sQuery(id+"F0.wireOp",EDGE,"E2"),sQuery(id+"F0.wireOp",EDGE,"E3"),sQuery(id+"F0.wireOp",EDGE,"E4"),sQuery(id+"F0.wireOp",EDGE,"E5"),sQuery(id+"F0.wireOp",EDGE,"E6"),sQuery(id+"F0.wireOp",EDGE,"E7"),sQuery(id+"F0.wireOp",EDGE,"E8"),sQuery(id+"F0.wireOp",EDGE,"E9"),sQuery(id+"F0.wireOp",EDGE,"E10"),sQuery(id+"F0.wireOp",EDGE,"E11"),sQuery(id+"F0.wireOp",EDGE,"E12"),sQuery(id+"F0.wireOp",EDGE,"E13"),sQuery(id+"F0.wireOp",EDGE,"E14"),sQuery(id+"F0.wireOp",EDGE,"E15"),sQuery(id+"F0.wireOp",EDGE,"E16"),sQuery(id+"F0.wireOp",EDGE,"E17"),sQuery(id+"F0.wireOp",EDGE,"E18"),sQuery(id+"F0.wireOp",EDGE,"E19"),sQuery(id+"F0.wireOp",EDGE,"E20"),sQuery(id+"F0.wireOp",EDGE,"E21"),sQuery(id+"F0.wireOp",EDGE,"E22"),sQuery(id+"F0.wireOp",EDGE,"E23"),sQuery(id+"F0.wireOp",EDGE,"E24"),sQuery(id+"F0.wireOp",EDGE,"E25"),sQuery(id+"F0.wireOp",EDGE,"E26"),sQuery(id+"F0.wireOp",EDGE,"E27"),sQuery(id+"F0.wireOp",EDGE,"E28"),sQuery(id+"F0.wireOp",EDGE,"E29"),sQuery(id+"F0.wireOp",EDGE,"E30"),sQuery(id+"F0.wireOp",EDGE,"E31"),sQuery(id+"F0.wireOp",EDGE,"E32"),sQuery(id+"F0.wireOp",EDGE,"E33"),sQuery(id+"F0.wireOp",EDGE,"E34"),sQuery(id+"F0.wireOp",EDGE,"E35"),sQuery(id+"F0.wireOp",EDGE,"E36"),sQuery(id+"F0.wireOp",EDGE,"E37"),sQuery(id+"F0.wireOp",EDGE,"E38"),sQuery(id+"F0.wireOp",EDGE,"E39"),sQuery(id+"F0.wireOp",EDGE,"E40"),sQuery(id+"F0.wireOp",EDGE,"E41"),sQuery(id+"F0.wireOp",EDGE,"E42"),sQuery(id+"F0.wireOp",EDGE,"E43"),sQuery(id+"F0.wireOp",EDGE,"E44"),sQuery(id+"F0.wireOp",EDGE,"E45"),sQuery(id+"F0.wireOp",EDGE,"E46"),sQuery(id+"F0.wireOp",EDGE,"E47"),sQuery(id+"F0.wireOp",EDGE,"E48"),sQuery(id+"F0.wireOp",EDGE,"E49"),sQuery(id+"F0.wireOp",EDGE,"E50"),sQuery(id+"F0.wireOp",EDGE,"E51"),sQuery(id+"F0.wireOp",EDGE,"E52"),sQuery(id+"F0.wireOp",EDGE,"E53"),sQuery(id+"F0.wireOp",EDGE,"E54"),sQuery(id+"F0.wireOp",EDGE,"E55"),sQuery(id+"F0.wireOp",EDGE,"E56"),sQuery(id+"F0.wireOp",EDGE,"E57"),sQuery(id+"F0.wireOp",EDGE,"E58"),sQuery(id+"F0.wireOp",EDGE,"E59"),sQuery(id+"F0.wireOp",EDGE,"E60"),sQuery(id+"F0.wireOp",EDGE,"E61"),sQuery(id+"F0.wireOp",EDGE,"E62"),sQuery(id+"F0.wireOp",EDGE,"E63"),sQuery(id+"F0.wireOp",EDGE,"E64"),sQuery(id+"F0.wireOp",EDGE,"E65"),sQuery(id+"F0.wireOp",EDGE,"E66"),sQuery(id+"F0.wireOp",EDGE,"E67"),sQuery(id+"F0.wireOp",EDGE,"E68"),sQuery(id+"F0.wireOp",EDGE,"E69"),sQuery(id+"F0.wireOp",EDGE,"E70"),sQuery(id+"F0.wireOp",EDGE,"E71"),sQuery(id+"F0.wireOp",EDGE,"E72"),sQuery(id+"F0.wireOp",EDGE,"E73"),sQuery(id+"F0.wireOp",EDGE,"E74"),sQuery(id+"F0.wireOp",EDGE,"E75"),sQuery(id+"F0.wireOp",EDGE,"E76"),sQuery(id+"F0.wireOp",EDGE,"E77"),sQuery(id+"F0.wireOp",EDGE,"E78"),sQuery(id+"F0.wireOp",EDGE,"E79"),sQuery(id+"F0.wireOp",EDGE,"E80"),sQuery(id+"F0.wireOp",EDGE,"E81"),sQuery(id+"F0.wireOp",EDGE,"E82"),sQuery(id+"F0.wireOp",EDGE,"E83"),sQuery(id+"F0.wireOp",EDGE,"E84"),sQuery(id+"F0.wireOp",EDGE,"E85"),sQuery(id+"F0.wireOp",EDGE,"E86"),sQuery(id+"F0.wireOp",EDGE,"E87"),sQuery(id+"F0.wireOp",EDGE,"E88"),sQuery(id+"F0.wireOp",EDGE,"E89"),sQuery(id+"F0.wireOp",EDGE,"E90"),sQuery(id+"F0.wireOp",EDGE,"E91"),sQuery(id+"F0.wireOp",EDGE,"E92"),sQuery(id+"F0.wireOp",EDGE,"E93"),sQuery(id+"F0.wireOp",EDGE,"E94"),sQuery(id+"F0.wireOp",EDGE,"E95"),sQuery(id+"F0.wireOp",EDGE,"E96"),sQuery(id+"F0.wireOp",EDGE,"E97"),sQuery(id+"F0.wireOp",EDGE,"E98"),sQuery(id+"F0.wireOp",EDGE,"E99"),sQuery(id+"F0.wireOp",EDGE,"E100"),sQuery(id+"F0.wireOp",EDGE,"E101"),sQuery(id+"F0.wireOp",EDGE,"E102"),sQuery(id+"F0.wireOp",EDGE,"E103"),sQuery(id+"F0.wireOp",EDGE,"E104"),sQuery(id+"F0.wireOp",EDGE,"E105"),sQuery(id+"F0.wireOp",EDGE,"E106"),sQuery(id+"F0.wireOp",EDGE,"E107"),sQuery(id+"F0.wireOp",EDGE,"E108"),sQuery(id+"F0.wireOp",EDGE,"E109"),sQuery(id+"F0.wireOp",EDGE,"E110"),sQuery(id+"F0.wireOp",EDGE,"E111"),sQuery(id+"F0.wireOp",EDGE,"E112"),sQuery(id+"F0.wireOp",EDGE,"E113"),sQuery(id+"F0.wireOp",EDGE,"E114"),sQuery(id+"F0.wireOp",EDGE,"E115"),sQuery(id+"F0.wireOp",EDGE,"E116"),sQuery(id+"F0.wireOp",EDGE,"E117"),sQuery(id+"F0.wireOp",EDGE,"E118"),sQuery(id+"F0.wireOp",EDGE,"E119"),sQuery(id+"F0.wireOp",EDGE,"E120"),sQuery(id+"F0.wireOp",EDGE,"E121"),sQuery(id+"F0.wireOp",EDGE,"E122"),sQuery(id+"F0.wireOp",EDGE,"E123"),sQuery(id+"F0.wireOp",EDGE,"E124"),sQuery(id+"F0.wireOp",EDGE,"E125"),sQuery(id+"F0.wireOp",EDGE,"E126"),sQuery(id+"F0.wireOp",EDGE,"E127"),sQuery(id+"F0.wireOp",EDGE,"E128"),sQuery(id+"F0.wireOp",EDGE,"E129"),sQuery(id+"F0.wireOp",EDGE,"E130"),sQuery(id+"F0.wireOp",EDGE,"E131"),sQuery(id+"F0.wireOp",EDGE,"E132"),sQuery(id+"F0.wireOp",EDGE,"E133"),sQuery(id+"F0.wireOp",EDGE,"E134"),sQuery(id+"F0.wireOp",EDGE,"E135"),sQuery(id+"F0.wireOp",EDGE,"E136"),sQuery(id+"F0.wireOp",EDGE,"E137"),sQuery(id+"F0.wireOp",EDGE,"E138"),sQuery(id+"F0.wireOp",EDGE,"E139"),sQuery(id+"F0.wireOp",EDGE,"E140"),sQuery(id+"F0.wireOp",EDGE,"E141"),sQuery(id+"F0.wireOp",EDGE,"E142"),sQuery(id+"F0.wireOp",EDGE,"E143"),sQuery(id+"F0.wireOp",EDGE,"E144"),sQuery(id+"F0.wireOp",EDGE,"E145"),sQuery(id+"F0.wireOp",EDGE,"E146"),sQuery(id+"F0.wireOp",EDGE,"E147"),sQuery(id+"F0.wireOp",EDGE,"E148"),sQuery(id+"F0.wireOp",EDGE,"E149"),sQuery(id+"F0.wireOp",EDGE,"E150"),sQuery(id+"F0.wireOp",EDGE,"E151"),sQuery(id+"F0.wireOp",EDGE,"E152"),sQuery(id+"F0.wireOp",EDGE,"E153"),sQuery(id+"F0.wireOp",EDGE,"E154"),sQuery(id+"F0.wireOp",EDGE,"E155"),sQuery(id+"F0.wireOp",EDGE,"E156"),sQuery(id+"F0.wireOp",EDGE,"E157"),sQuery(id+"F0.wireOp",EDGE,"E158"),sQuery(id+"F0.wireOp",EDGE,"E159"),sQuery(id+"F0.wireOp",EDGE,"E160"),sQuery(id+"F0.wireOp",EDGE,"E161"),sQuery(id+"F0.wireOp",EDGE,"E162"),sQuery(id+"F0.wireOp",EDGE,"E163"),sQuery(id+"F0.wireOp",EDGE,"E164"),sQuery(id+"F0.wireOp",EDGE,"E165"),sQuery(id+"F0.wireOp",EDGE,"E166"),sQuery(id+"F0.wireOp",EDGE,"E167"),sQuery(id+"F0.wireOp",EDGE,"E168"),sQuery(id+"F0.wireOp",EDGE,"E169"),sQuery(id+"F0.wireOp",EDGE,"E170"),sQuery(id+"F0.wireOp",EDGE,"E171"),sQuery(id+"F0.wireOp",EDGE,"E172"),sQuery(id+"F0.wireOp",EDGE,"E173"),sQuery(id+"F0.wireOp",EDGE,"E174"),sQuery(id+"F0.wireOp",EDGE,"E175"),sQuery(id+"F0.wireOp",EDGE,"E176"),sQuery(id+"F0.wireOp",EDGE,"E177"),sQuery(id+"F0.wireOp",EDGE,"E178"),sQuery(id+"F0.wireOp",EDGE,"E179"),sQuery(id+"F0.wireOp",EDGE,"E180"),sQuery(id+"F0.wireOp",EDGE,"E181"),sQuery(id+"F0.wireOp",EDGE,"E182"),sQuery(id+"F0.wireOp",EDGE,"E183"),sQuery(id+"F0.wireOp",EDGE,"E184"),sQuery(id+"F0.wireOp",EDGE,"E185"),sQuery(id+"F0.wireOp",EDGE,"E186"),sQuery(id+"F0.wireOp",EDGE,"E187"),sQuery(id+"F0.wireOp",EDGE,"E188"),sQuery(id+"F0.wireOp",EDGE,"E189"),sQuery(id+"F0.wireOp",EDGE,"E190"),sQuery(id+"F0.wireOp",EDGE,"E191"),sQuery(id+"F0.wireOp",EDGE,"E192"),sQuery(id+"F0.wireOp",EDGE,"E193"),sQuery(id+"F0.wireOp",EDGE,"E194"),sQuery(id+"F0.wireOp",EDGE,"E195"),sQuery(id+"F0.wireOp",EDGE,"E196"),sQuery(id+"F0.wireOp",EDGE,"E197"),sQuery(id+"F0.wireOp",EDGE,"E198"),sQuery(id+"F0.wireOp",EDGE,"E199"),sQuery(id+"F0.wireOp",EDGE,"E200"),sQuery(id+"F0.wireOp",EDGE,"E201"),sQuery(id+"F0.wireOp",EDGE,"E202"),sQuery(id+"F0.wireOp",EDGE,"E203"),sQuery(id+"F0.wireOp",EDGE,"E204"),sQuery(id+"F0.wireOp",EDGE,"E205"),sQuery(id+"F0.wireOp",EDGE,"E206"),sQuery(id+"F0.wireOp",EDGE,"E207"),sQuery(id+"F0.wireOp",EDGE,"E208"),sQuery(id+"F0.wireOp",EDGE,"E209"),sQuery(id+"F0.wireOp",EDGE,"E210"),sQuery(id+"F0.wireOp",EDGE,"E211"),sQuery(id+"F0.wireOp",EDGE,"E212"),sQuery(id+"F0.wireOp",EDGE,"E213"),sQuery(id+"F0.wireOp",EDGE,"E214"),sQuery(id+"F0.wireOp",EDGE,"E215"),sQuery(id+"F0.wireOp",EDGE,"E216"),sQuery(id+"F0.wireOp",EDGE,"E217"),sQuery(id+"F0.wireOp",EDGE,"E218"),sQuery(id+"F0.wireOp",EDGE,"E219"),sQuery(id+"F0.wireOp",EDGE,"E220"),sQuery(id+"F0.wireOp",EDGE,"E221"),sQuery(id+"F0.wireOp",EDGE,"E222"),sQuery(id+"F0.wireOp",EDGE,"E223"),sQuery(id+"F0.wireOp",EDGE,"E224"),sQuery(id+"F0.wireOp",EDGE,"E225"),sQuery(id+"F0.wireOp",EDGE,"E226"),sQuery(id+"F0.wireOp",EDGE,"E227"),sQuery(id+"F0.wireOp",EDGE,"E228"),sQuery(id+"F0.wireOp",EDGE,"E229"),sQuery(id+"F0.wireOp",EDGE,"E230"),sQuery(id+"F0.wireOp",EDGE,"E231"),sQuery(id+"F0.wireOp",EDGE,"E232"),sQuery(id+"F0.wireOp",EDGE,"E233"),sQuery(id+"F0.wireOp",EDGE,"E234"),sQuery(id+"F0.wireOp",EDGE,"E235"),sQuery(id+"F0.wireOp",EDGE,"E236"),sQuery(id+"F0.wireOp",EDGE,"E237"),sQuery(id+"F0.wireOp",EDGE,"E238"),sQuery(id+"F0.wireOp",EDGE,"E239"),sQuery(id+"F0.wireOp",EDGE,"E240"),sQuery(id+"F0.wireOp",EDGE,"E241"),sQuery(id+"F0.wireOp",EDGE,"E242"),sQuery(id+"F0.wireOp",EDGE,"E243"),sQuery(id+"F0.wireOp",EDGE,"E244"),sQuery(id+"F0.wireOp",EDGE,"E245"),sQuery(id+"F0.wireOp",EDGE,"E246"),sQuery(id+"F0.wireOp",EDGE,"E247"),sQuery(id+"F0.wireOp",EDGE,"E248"),sQuery(id+"F0.wireOp",EDGE,"E249"),sQuery(id+"F0.wireOp",EDGE,"E250"),sQuery(id+"F0.wireOp",EDGE,"E251"),sQuery(id+"F0.wireOp",EDGE,"E252"),sQuery(id+"F0.wireOp",EDGE,"E253"),sQuery(id+"F0.wireOp",EDGE,"E254"),sQuery(id+"F0.wireOp",EDGE,"E255"),sQuery(id+"F0.wireOp",EDGE,"E256"),sQuery(id+"F0.wireOp",EDGE,"E257"),sQuery(id+"F0.wireOp",EDGE,"E258"),sQuery(id+"F0.wireOp",EDGE,"E259"),sQuery(id+"F0.wireOp",EDGE,"E260"),sQuery(id+"F0.wireOp",EDGE,"E261"),sQuery(id+"F0.wireOp",EDGE,"E262"),sQuery(id+"F0.wireOp",EDGE,"E263"),sQuery(id+"F0.wireOp",EDGE,"E264"),sQuery(id+"F0.wireOp",EDGE,"E265"),sQuery(id+"F0.wireOp",EDGE,"E266"),sQuery(id+"F0.wireOp",EDGE,"E267"),sQuery(id+"F0.wireOp",EDGE,"E268"),sQuery(id+"F0.wireOp",EDGE,"E269"),sQuery(id+"F0.wireOp",EDGE,"E270"),sQuery(id+"F0.wireOp",EDGE,"E271"),sQuery(id+"F0.wireOp",EDGE,"E272"),sQuery(id+"F0.wireOp",EDGE,"E273"),sQuery(id+"F0.wireOp",EDGE,"E274"),sQuery(id+"F0.wireOp",EDGE,"E275"),sQuery(id+"F0.wireOp",EDGE,"E276"),sQuery(id+"F0.wireOp",EDGE,"E277"),sQuery(id+"F0.wireOp",EDGE,"E278"),sQuery(id+"F0.wireOp",EDGE,"E279"),sQuery(id+"F0.wireOp",EDGE,"E280"),sQuery(id+"F0.wireOp",EDGE,"E281"),sQuery(id+"F0.wireOp",EDGE,"E282"),sQuery(id+"F0.wireOp",EDGE,"E283"),sQuery(id+"F0.wireOp",EDGE,"E284"),sQuery(id+"F0.wireOp",EDGE,"E285"),sQuery(id+"F0.wireOp",EDGE,"E286"),sQuery(id+"F0.wireOp",EDGE,"E287"),sQuery(id+"F0.wireOp",EDGE,"E288"),sQuery(id+"F0.wireOp",EDGE,"E289"),sQuery(id+"F0.wireOp",EDGE,"E290"),sQuery(id+"F0.wireOp",EDGE,"E291"),sQuery(id+"F0.wireOp",EDGE,"E292"),sQuery(id+"F0.wireOp",EDGE,"E293"),sQuery(id+"F0.wireOp",EDGE,"E294"),sQuery(id+"F0.wireOp",EDGE,"E295"),sQuery(id+"F0.wireOp",EDGE,"E296"),sQuery(id+"F0.wireOp",EDGE,"E297"),sQuery(id+"F0.wireOp",EDGE,"E298"),sQuery(id+"F0.wireOp",EDGE,"E299"),sQuery(id+"F0.wireOp",EDGE,"E300"),sQuery(id+"F0.wireOp",EDGE,"E301"),sQuery(id+"F0.wireOp",EDGE,"E302"),sQuery(id+"F0.wireOp",EDGE,"E303"),sQuery(id+"F0.wireOp",EDGE,"E304"),sQuery(id+"F0.wireOp",EDGE,"E305"),sQuery(id+"F0.wireOp",EDGE,"E306"),sQuery(id+"F0.wireOp",EDGE,"E307"),sQuery(id+"F0.wireOp",EDGE,"E308"),sQuery(id+"F0.wireOp",EDGE,"E309"),sQuery(id+"F0.wireOp",EDGE,"E310"),sQuery(id+"F0.wireOp",EDGE,"E311"),sQuery(id+"F0.wireOp",EDGE,"E312"),sQuery(id+"F0.wireOp",EDGE,"E313"),sQuery(id+"F0.wireOp",EDGE,"E314"),sQuery(id+"F0.wireOp",EDGE,"E315"),sQuery(id+"F0.wireOp",EDGE,"E316"),sQuery(id+"F0.wireOp",EDGE,"E317"),sQuery(id+"F0.wireOp",EDGE,"E318"),sQuery(id+"F0.wireOp",EDGE,"E319"),sQuery(id+"F0.wireOp",EDGE,"E320"),sQuery(id+"F0.wireOp",EDGE,"E321"),sQuery(id+"F0.wireOp",EDGE,"E322"),sQuery(id+"F0.wireOp",EDGE,"E323"),sQuery(id+"F0.wireOp",EDGE,"E324"),sQuery(id+"F0.wireOp",EDGE,"E325"),sQuery(id+"F0.wireOp",EDGE,"E326"),sQuery(id+"F0.wireOp",EDGE,"E327"),sQuery(id+"F0.wireOp",EDGE,"E328"),sQuery(id+"F0.wireOp",EDGE,"E329"),sQuery(id+"F0.wireOp",EDGE,"E330"),sQuery(id+"F0.wireOp",EDGE,"E331"),sQuery(id+"F0.wireOp",EDGE,"E332"),sQuery(id+"F0.wireOp",EDGE,"E333"),sQuery(id+"F0.wireOp",EDGE,"E334"),sQuery(id+"F0.wireOp",EDGE,"E335"),sQuery(id+"F0.wireOp",EDGE,"E336"),sQuery(id+"F0.wireOp",EDGE,"E337"),sQuery(id+"F0.wireOp",EDGE,"E338"),sQuery(id+"F0.wireOp",EDGE,"E339"),sQuery(id+"F0.wireOp",EDGE,"E340"),sQuery(id+"F0.wireOp",EDGE,"E341"),sQuery(id+"F0.wireOp",EDGE,"E342"),sQuery(id+"F0.wireOp",EDGE,"E343"),sQuery(id+"F0.wireOp",EDGE,"E344"),sQuery(id+"F0.wireOp",EDGE,"E345"),sQuery(id+"F0.wireOp",EDGE,"E346"),sQuery(id+"F0.wireOp",EDGE,"E347"),sQuery(id+"F0.wireOp",EDGE,"E348"),sQuery(id+"F0.wireOp",EDGE,"E349"),sQuery(id+"F0.wireOp",EDGE,"E350"),sQuery(id+"F0.wireOp",EDGE,"E351"),sQuery(id+"F0.wireOp",EDGE,"E352"),sQuery(id+"F0.wireOp",EDGE,"E353"),sQuery(id+"F0.wireOp",EDGE,"E354"),sQuery(id+"F0.wireOp",EDGE,"E355"),sQuery(id+"F0.wireOp",EDGE,"E356"),sQuery(id+"F0.wireOp",EDGE,"E357"),sQuery(id+"F0.wireOp",EDGE,"E358"),sQuery(id+"F0.wireOp",EDGE,"E359"),sQuery(id+"F0.wireOp",EDGE,"E360"),sQuery(id+"F0.wireOp",EDGE,"E361"),sQuery(id+"F0.wireOp",EDGE,"E362"),sQuery(id+"F0.wireOp",EDGE,"E363"),sQuery(id+"F0.wireOp",EDGE,"E364"),sQuery(id+"F0.wireOp",EDGE,"E365"),sQuery(id+"F0.wireOp",EDGE,"E366"),sQuery(id+"F0.wireOp",EDGE,"E367"),sQuery(id+"F0.wireOp",EDGE,"E368"),sQuery(id+"F0.wireOp",EDGE,"E369"),sQuery(id+"F0.wireOp",EDGE,"E370"),sQuery(id+"F0.wireOp",EDGE,"E371"),sQuery(id+"F0.wireOp",EDGE,"E372"),sQuery(id+"F0.wireOp",EDGE,"E373"),sQuery(id+"F0.wireOp",EDGE,"E374"),sQuery(id+"F0.wireOp",EDGE,"E375"),sQuery(id+"F0.wireOp",EDGE,"E376"),sQuery(id+"F0.wireOp",EDGE,"E377"),sQuery(id+"F0.wireOp",EDGE,"E378"),sQuery(id+"F0.wireOp",EDGE,"E379"),sQuery(id+"F0.wireOp",EDGE,"E380"),sQuery(id+"F0.wireOp",EDGE,"E381"),sQuery(id+"F0.wireOp",EDGE,"E382"),sQuery(id+"F0.wireOp",EDGE,"E383"),sQuery(id+"F0.wireOp",EDGE,"E384"),sQuery(id+"F0.wireOp",EDGE,"E385"),sQuery(id+"F0.wireOp",EDGE,"E386"),sQuery(id+"F0.wireOp",EDGE,"E387"),sQuery(id+"F0.wireOp",EDGE,"E388"),sQuery(id+"F0.wireOp",EDGE,"E389"),sQuery(id+"F0.wireOp",EDGE,"E390"),sQuery(id+"F0.wireOp",EDGE,"E391"),sQuery(id+"F0.wireOp",EDGE,"E392"),sQuery(id+"F0.wireOp",EDGE,"E393"),sQuery(id+"F0.wireOp",EDGE,"E394"),sQuery(id+"F0.wireOp",EDGE,"E395"),sQuery(id+"F0.wireOp",EDGE,"E396"),sQuery(id+"F0.wireOp",EDGE,"E397"),sQuery(id+"F0.wireOp",EDGE,"E398"),sQuery(id+"F0.wireOp",EDGE,"E399"),sQuery(id+"F0.wireOp",EDGE,"E400"),sQuery(id+"F0.wireOp",EDGE,"E401"),sQuery(id+"F0.wireOp",EDGE,"E402"),sQuery(id+"F0.wireOp",EDGE,"E403"),sQuery(id+"F0.wireOp",EDGE,"E404"),sQuery(id+"F0.wireOp",EDGE,"E405"),sQuery(id+"F0.wireOp",EDGE,"E406"),sQuery(id+"F0.wireOp",EDGE,"E407"),sQuery(id+"F0.wireOp",EDGE,"E408"),sQuery(id+"F0.wireOp",EDGE,"E409"),sQuery(id+"F0.wireOp",EDGE,"E410"),sQuery(id+"F0.wireOp",EDGE,"E411"),sQuery(id+"F0.wireOp",EDGE,"E412"),sQuery(id+"F0.wireOp",EDGE,"E413"),sQuery(id+"F0.wireOp",EDGE,"E414"),sQuery(id+"F0.wireOp",EDGE,"E415"),sQuery(id+"F0.wireOp",EDGE,"E416"),sQuery(id+"F0.wireOp",EDGE,"E417"),sQuery(id+"F0.wireOp",EDGE,"E418"),sQuery(id+"F0.wireOp",EDGE,"E419"),sQuery(id+"F0.wireOp",EDGE,"E420"),sQuery(id+"F0.wireOp",EDGE,"E421"),sQuery(id+"F0.wireOp",EDGE,"E422"),sQuery(id+"F0.wireOp",EDGE,"E423"),sQuery(id+"F0.wireOp",EDGE,"E424"),sQuery(id+"F0.wireOp",EDGE,"E425"),sQuery(id+"F0.wireOp",EDGE,"E426"),sQuery(id+"F0.wireOp",EDGE,"E427"),sQuery(id+"F0.wireOp",EDGE,"E428"),sQuery(id+"F0.wireOp",EDGE,"E429"),sQuery(id+"F0.wireOp",EDGE,"E430"),sQuery(id+"F0.wireOp",EDGE,"E431"),sQuery(id+"F0.wireOp",EDGE,"E432"),sQuery(id+"F0.wireOp",EDGE,"E433"),sQuery(id+"F0.wireOp",EDGE,"E434"),sQuery(id+"F0.wireOp",EDGE,"E435"),sQuery(id+"F0.wireOp",EDGE,"E436"),sQuery(id+"F0.wireOp",EDGE,"E437"),sQuery(id+"F0.wireOp",EDGE,"E438"),sQuery(id+"F0.wireOp",EDGE,"E439"),sQuery(id+"F0.wireOp",EDGE,"E440"),sQuery(id+"F0.wireOp",EDGE,"E441"),sQuery(id+"F0.wireOp",EDGE,"E442"),sQuery(id+"F0.wireOp",EDGE,"E443"),sQuery(id+"F0.wireOp",EDGE,"E444"),sQuery(id+"F0.wireOp",EDGE,"E445"),sQuery(id+"F0.wireOp",EDGE,"E446"),sQuery(id+"F0.wireOp",EDGE,"E447"),sQuery(id+"F0.wireOp",EDGE,"E448"),sQuery(id+"F0.wireOp",EDGE,"E449"),sQuery(id+"F0.wireOp",EDGE,"E450"),sQuery(id+"F0.wireOp",EDGE,"E451"),sQuery(id+"F0.wireOp",EDGE,"E452"),sQuery(id+"F0.wireOp",EDGE,"E453"),sQuery(id+"F0.wireOp",EDGE,"E454"),sQuery(id+"F0.wireOp",EDGE,"E455"),sQuery(id+"F0.wireOp",EDGE,"E456"),sQuery(id+"F0.wireOp",EDGE,"E457"),sQuery(id+"F0.wireOp",EDGE,"E458"),sQuery(id+"F0.wireOp",EDGE,"E459"),sQuery(id+"F0.wireOp",EDGE,"E460"),sQuery(id+"F0.wireOp",EDGE,"E461"),sQuery(id+"F0.wireOp",EDGE,"E462"),sQuery(id+"F0.wireOp",EDGE,"E463"),sQuery(id+"F0.wireOp",EDGE,"E464"),sQuery(id+"F0.wireOp",EDGE,"E465"),sQuery(id+"F0.wireOp",EDGE,"E466"),sQuery(id+"F0.wireOp",EDGE,"E467"),sQuery(id+"F0.wireOp",EDGE,"E468"),sQuery(id+"F0.wireOp",EDGE,"E469"),sQuery(id+"F0.wireOp",EDGE,"E470"),sQuery(id+"F0.wireOp",EDGE,"E471"),sQuery(id+"F0.wireOp",EDGE,"E472"),sQuery(id+"F0.wireOp",EDGE,"E473"),sQuery(id+"F0.wireOp",EDGE,"E474"),sQuery(id+"F0.wireOp",EDGE,"E475"),sQuery(id+"F0.wireOp",EDGE,"E476"),sQuery(id+"F0.wireOp",EDGE,"E477"),sQuery(id+"F0.wireOp",EDGE,"E478"),sQuery(id+"F0.wireOp",EDGE,"E479"),sQuery(id+"F0.wireOp",EDGE,"E480"),sQuery(id+"F0.wireOp",EDGE,"E481"),sQuery(id+"F0.wireOp",EDGE,"E482"),sQuery(id+"F0.wireOp",EDGE,"E483"),sQuery(id+"F0.wireOp",EDGE,"E484"),sQuery(id+"F0.wireOp",EDGE,"E485"),sQuery(id+"F0.wireOp",EDGE,"E486"),sQuery(id+"F0.wireOp",EDGE,"E487"),sQuery(id+"F0.wireOp",EDGE,"E488"),sQuery(id+"F0.wireOp",EDGE,"E489"),sQuery(id+"F0.wireOp",EDGE,"E490"),sQuery(id+"F0.wireOp",EDGE,"E491"),sQuery(id+"F0.wireOp",EDGE,"E492"),sQuery(id+"F0.wireOp",EDGE,"E493"),sQuery(id+"F0.wireOp",EDGE,"E494"),sQuery(id+"F0.wireOp",EDGE,"E495"),sQuery(id+"F0.wireOp",EDGE,"E496"),sQuery(id+"F0.wireOp",EDGE,"E497"),sQuery(id+"F0.wireOp",EDGE,"E498"),sQuery(id+"F0.wireOp",EDGE,"E499"),sQuery(id+"F0.wireOp",EDGE,"E500"),sQuery(id+"F0.wireOp",EDGE,"E501"),sQuery(id+"F0.wireOp",EDGE,"E502"),sQuery(id+"F0.wireOp",EDGE,"E503"),sQuery(id+"F0.wireOp",EDGE,"E504"),sQuery(id+"F0.wireOp",EDGE,"E505"),sQuery(id+"F0.wireOp",EDGE,"E506"),sQuery(id+"F0.wireOp",EDGE,"E507"),sQuery(id+"F0.wireOp",EDGE,"E508"),sQuery(id+"F0.wireOp",EDGE,"E509"),sQuery(id+"F0.wireOp",EDGE,"E510"),sQuery(id+"F0.wireOp",EDGE,"E511"),sQuery(id+"F0.wireOp",EDGE,"E512"),sQuery(id+"F0.wireOp",EDGE,"E513"),sQuery(id+"F0.wireOp",EDGE,"E514"),sQuery(id+"F0.wireOp",EDGE,"E515"),sQuery(id+"F0.wireOp",EDGE,"E516"),sQuery(id+"F0.wireOp",EDGE,"E517"),sQuery(id+"F0.wireOp",EDGE,"E518"),sQuery(id+"F0.wireOp",EDGE,"E519"),sQuery(id+"F0.wireOp",EDGE,"E520"),sQuery(id+"F0.wireOp",EDGE,"E521"),sQuery(id+"F0.wireOp",EDGE,"E522"),sQuery(id+"F0.wireOp",EDGE,"E523"),sQuery(id+"F0.wireOp",EDGE,"E524"),sQuery(id+"F0.wireOp",EDGE,"E525"),sQuery(id+"F0.wireOp",EDGE,"E526"),sQuery(id+"F0.wireOp",EDGE,"E527"),sQuery(id+"F0.wireOp",EDGE,"E528"),sQuery(id+"F0.wireOp",EDGE,"E529"),sQuery(id+"F0.wireOp",EDGE,"E530"),sQuery(id+"F0.wireOp",EDGE,"E531"),sQuery(id+"F0.wireOp",EDGE,"E532"),sQuery(id+"F0.wireOp",EDGE,"E533"),sQuery(id+"F0.wireOp",EDGE,"E534"),sQuery(id+"F0.wireOp",EDGE,"E535"),sQuery(id+"F0.wireOp",EDGE,"E536"),sQuery(id+"F0.wireOp",EDGE,"E537"),sQuery(id+"F0.wireOp",EDGE,"E538"),sQuery(id+"F0.wireOp",EDGE,"E539"),sQuery(id+"F0.wireOp",EDGE,"E540"),sQuery(id+"F0.wireOp",EDGE,"E541"),sQuery(id+"F0.wireOp",EDGE,"E542"),sQuery(id+"F0.wireOp",EDGE,"E543"),sQuery(id+"F0.wireOp",EDGE,"E544"),sQuery(id+"F0.wireOp",EDGE,"E545"),sQuery(id+"F0.wireOp",EDGE,"E546"),sQuery(id+"F0.wireOp",EDGE,"E547"),sQuery(id+"F0.wireOp",EDGE,"E548"),sQuery(id+"F0.wireOp",EDGE,"E549"),sQuery(id+"F0.wireOp",EDGE,"E550"),sQuery(id+"F0.wireOp",EDGE,"E551"),sQuery(id+"F0.wireOp",EDGE,"E552"),sQuery(id+"F0.wireOp",EDGE,"E553"),sQuery(id+"F0.wireOp",EDGE,"E554"),sQuery(id+"F0.wireOp",EDGE,"E555"),sQuery(id+"F0.wireOp",EDGE,"E556"),sQuery(id+"F0.wireOp",EDGE,"E557"),sQuery(id+"F0.wireOp",EDGE,"E558"),sQuery(id+"F0.wireOp",EDGE,"E559"),sQuery(id+"F0.wireOp",EDGE,"E560"),sQuery(id+"F0.wireOp",EDGE,"E561"),sQuery(id+"F0.wireOp",EDGE,"E562"),sQuery(id+"F0.wireOp",EDGE,"E563"),sQuery(id+"F0.wireOp",EDGE,"E564"),sQuery(id+"F0.wireOp",EDGE,"E565"),sQuery(id+"F0.wireOp",EDGE,"E566"),sQuery(id+"F0.wireOp",EDGE,"E567"),sQuery(id+"F0.wireOp",EDGE,"E568"),sQuery(id+"F0.wireOp",EDGE,"E569"),sQuery(id+"F0.wireOp",EDGE,"E570"),sQuery(id+"F0.wireOp",EDGE,"E571"),sQuery(id+"F0.wireOp",EDGE,"E572"),sQuery(id+"F0.wireOp",EDGE,"E573"),sQuery(id+"F0.wireOp",EDGE,"E574"),sQuery(id+"F0.wireOp",EDGE,"E575"),sQuery(id+"F0.wireOp",EDGE,"E576"),sQuery(id+"F0.wireOp",EDGE,"E577"),sQuery(id+"F0.wireOp",EDGE,"E578"),sQuery(id+"F0.wireOp",EDGE,"E579"),sQuery(id+"F0.wireOp",EDGE,"E580"),sQuery(id+"F0.wireOp",EDGE,"E581"),sQuery(id+"F0.wireOp",EDGE,"E582"),sQuery(id+"F0.wireOp",EDGE,"E583"),sQuery(id+"F0.wireOp",EDGE,"E584"),sQuery(id+"F0.wireOp",EDGE,"E585"),sQuery(id+"F0.wireOp",EDGE,"E586"),sQuery(id+"F0.wireOp",EDGE,"E587"),sQuery(id+"F0.wireOp",EDGE,"E588"),sQuery(id+"F0.wireOp",EDGE,"E589"),sQuery(id+"F0.wireOp",EDGE,"E590"),sQuery(id+"F0.wireOp",EDGE,"E591"),sQuery(id+"F0.wireOp",EDGE,"E592"),sQuery(id+"F0.wireOp",EDGE,"E593"),sQuery(id+"F0.wireOp",EDGE,"E594"),sQuery(id+"F0.wireOp",EDGE,"E595"),sQuery(id+"F0.wireOp",EDGE,"E596"),sQuery(id+"F0.wireOp",EDGE,"E597"),sQuery(id+"F0.wireOp",EDGE,"E598"),sQuery(id+"F0.wireOp",EDGE,"E599"),sQuery(id+"F0.wireOp",EDGE,"E600"),sQuery(id+"F0.wireOp",EDGE,"E601"),sQuery(id+"F0.wireOp",EDGE,"E602"),sQuery(id+"F0.wireOp",EDGE,"E603"),sQuery(id+"F0.wireOp",EDGE,"E604"),sQuery(id+"F0.wireOp",EDGE,"E605"),sQuery(id+"F0.wireOp",EDGE,"E606"),sQuery(id+"F0.wireOp",EDGE,"E607"),sQuery(id+"F0.wireOp",EDGE,"E608"),sQuery(id+"F0.wireOp",EDGE,"E609"),sQuery(id+"F0.wireOp",EDGE,"E610"),sQuery(id+"F0.wireOp",EDGE,"E611"),sQuery(id+"F0.wireOp",EDGE,"E612"),sQuery(id+"F0.wireOp",EDGE,"E613"),sQuery(id+"F0.wireOp",EDGE,"E614"),sQuery(id+"F0.wireOp",EDGE,"E615"),sQuery(id+"F0.wireOp",EDGE,"E616"),sQuery(id+"F0.wireOp",EDGE,"E617"),sQuery(id+"F0.wireOp",EDGE,"E618"),sQuery(id+"F0.wireOp",EDGE,"E619"),sQuery(id+"F0.wireOp",EDGE,"E620"),sQuery(id+"F0.wireOp",EDGE,"E621"),sQuery(id+"F0.wireOp",EDGE,"E622"),sQuery(id+"F0.wireOp",EDGE,"E623"),sQuery(id+"F0.wireOp",EDGE,"E624"),sQuery(id+"F0.wireOp",EDGE,"E625"),sQuery(id+"F0.wireOp",EDGE,"E626"),sQuery(id+"F0.wireOp",EDGE,"E627"),sQuery(id+"F0.wireOp",EDGE,"E628"),sQuery(id+"F0.wireOp",EDGE,"E629"),sQuery(id+"F0.wireOp",EDGE,"E630"),sQuery(id+"F0.wireOp",EDGE,"E631"),sQuery(id+"F0.wireOp",EDGE,"E632"),sQuery(id+"F0.wireOp",EDGE,"E633"),sQuery(id+"F0.wireOp",EDGE,"E634"),sQuery(id+"F0.wireOp",EDGE,"E635"),sQuery(id+"F0.wireOp",EDGE,"E636"),sQuery(id+"F0.wireOp",EDGE,"E637"),sQuery(id+"F0.wireOp",EDGE,"E638"),sQuery(id+"F0.wireOp",EDGE,"E639"),sQuery(id+"F0.wireOp",EDGE,"E640"),sQuery(id+"F0.wireOp",EDGE,"E641"),sQuery(id+"F0.wireOp",EDGE,"E642"),sQuery(id+"F0.wireOp",EDGE,"E643"),sQuery(id+"F0.wireOp",EDGE,"E644"),sQuery(id+"F0.wireOp",EDGE,"E645"),sQuery(id+"F0.wireOp",EDGE,"E646"),sQuery(id+"F0.wireOp",EDGE,"E647"),sQuery(id+"F0.wireOp",EDGE,"E648"),sQuery(id+"F0.wireOp",EDGE,"E649"),sQuery(id+"F0.wireOp",EDGE,"E650"),sQuery(id+"F0.wireOp",EDGE,"E651"),sQuery(id+"F0.wireOp",EDGE,"E652"),sQuery(id+"F0.wireOp",EDGE,"E653"),sQuery(id+"F0.wireOp",EDGE,"E654"),sQuery(id+"F0.wireOp",EDGE,"E655"),sQuery(id+"F0.wireOp",EDGE,"E656"),sQuery(id+"F0.wireOp",EDGE,"E657"),sQuery(id+"F0.wireOp",EDGE,"E658"),sQuery(id+"F0.wireOp",EDGE,"E659"),sQuery(id+"F0.wireOp",EDGE,"E660"),sQuery(id+"F0.wireOp",EDGE,"E661"),sQuery(id+"F0.wireOp",EDGE,"E662"),sQuery(id+"F0.wireOp",EDGE,"E663"),sQuery(id+"F0.wireOp",EDGE,"E664"),sQuery(id+"F0.wireOp",EDGE,"E665"),sQuery(id+"F0.wireOp",EDGE,"E666"),sQuery(id+"F0.wireOp",EDGE,"E667"),sQuery(id+"F0.wireOp",EDGE,"E668"),sQuery(id+"F0.wireOp",EDGE,"E669"),sQuery(id+"F0.wireOp",EDGE,"E670"),sQuery(id+"F0.wireOp",EDGE,"E671"),sQuery(id+"F0.wireOp",EDGE,"E672"),sQuery(id+"F0.wireOp",EDGE,"E673"),sQuery(id+"F0.wireOp",EDGE,"E674"),sQuery(id+"F0.wireOp",EDGE,"E675"),sQuery(id+"F0.wireOp",EDGE,"E676"),sQuery(id+"F0.wireOp",EDGE,"E677"),sQuery(id+"F0.wireOp",EDGE,"E678"),sQuery(id+"F0.wireOp",EDGE,"E679"),sQuery(id+"F0.wireOp",EDGE,"E680"),sQuery(id+"F0.wireOp",EDGE,"E681"),sQuery(id+"F0.wireOp",EDGE,"E682"),sQuery(id+"F0.wireOp",EDGE,"E683"),sQuery(id+"F0.wireOp",EDGE,"E684"),sQuery(id+"F0.wireOp",EDGE,"E685"),sQuery(id+"F0.wireOp",EDGE,"E686"),sQuery(id+"F0.wireOp",EDGE,"E687"),sQuery(id+"F0.wireOp",EDGE,"E688"),sQuery(id+"F0.wireOp",EDGE,"E689"),sQuery(id+"F0.wireOp",EDGE,"E690"),sQuery(id+"F0.wireOp",EDGE,"E691"),sQuery(id+"F0.wireOp",EDGE,"E692"),sQuery(id+"F0.wireOp",EDGE,"E693"),sQuery(id+"F0.wireOp",EDGE,"E694"),sQuery(id+"F0.wireOp",EDGE,"E695"),sQuery(id+"F0.wireOp",EDGE,"E696"),sQuery(id+"F0.wireOp",EDGE,"E697"),sQuery(id+"F0.wireOp",EDGE,"E698"),sQuery(id+"F0.wireOp",EDGE,"E699"),sQuery(id+"F0.wireOp",EDGE,"E700"),sQuery(id+"F0.wireOp",EDGE,"E701"),sQuery(id+"F0.wireOp",EDGE,"E702"),sQuery(id+"F0.wireOp",EDGE,"E703"),sQuery(id+"F0.wireOp",EDGE,"E704"),sQuery(id+"F0.wireOp",EDGE,"E705"),sQuery(id+"F0.wireOp",EDGE,"E706"),sQuery(id+"F0.wireOp",EDGE,"E707"),sQuery(id+"F0.wireOp",EDGE,"E708"),sQuery(id+"F0.wireOp",EDGE,"E709"),sQuery(id+"F0.wireOp",EDGE,"E710"),sQuery(id+"F0.wireOp",EDGE,"E711"),sQuery(id+"F0.wireOp",EDGE,"E712"),sQuery(id+"F0.wireOp",EDGE,"E713"),sQuery(id+"F0.wireOp",EDGE,"E714"),sQuery(id+"F0.wireOp",EDGE,"E715"),sQuery(id+"F0.wireOp",EDGE,"E716"),sQuery(id+"F0.wireOp",EDGE,"E717"),sQuery(id+"F0.wireOp",EDGE,"E718"),sQuery(id+"F0.wireOp",EDGE,"E719"),sQuery(id+"F0.wireOp",EDGE,"E720"),sQuery(id+"F0.wireOp",EDGE,"E721"),sQuery(id+"F0.wireOp",EDGE,"E722"),sQuery(id+"F0.wireOp",EDGE,"E723"),sQuery(id+"F0.wireOp",EDGE,"E724"),sQuery(id+"F0.wireOp",EDGE,"E725"),sQuery(id+"F0.wireOp",EDGE,"E726"),sQuery(id+"F0.wireOp",EDGE,"E727"),sQuery(id+"F0.wireOp",EDGE,"E728"),sQuery(id+"F0.wireOp",EDGE,"E729"),sQuery(id+"F0.wireOp",EDGE,"E730"),sQuery(id+"F0.wireOp",EDGE,"E731"),sQuery(id+"F0.wireOp",EDGE,"E732"),sQuery(id+"F0.wireOp",EDGE,"E733"),sQuery(id+"F0.wireOp",EDGE,"E734"),sQuery(id+"F0.wireOp",EDGE,"E735"),sQuery(id+"F0.wireOp",EDGE,"E736"),sQuery(id+"F0.wireOp",EDGE,"E737"),sQuery(id+"F0.wireOp",EDGE,"E738"),sQuery(id+"F0.wireOp",EDGE,"E739"),sQuery(id+"F0.wireOp",EDGE,"E740"),sQuery(id+"F0.wireOp",EDGE,"E741"),sQuery(id+"F0.wireOp",EDGE,"E742"),sQuery(id+"F0.wireOp",EDGE,"E743"),sQuery(id+"F0.wireOp",EDGE,"E744"),sQuery(id+"F0.wireOp",EDGE,"E745"),sQuery(id+"F0.wireOp",EDGE,"E746"),sQuery(id+"F0.wireOp",EDGE,"E747"),sQuery(id+"F0.wireOp",EDGE,"E748"),sQuery(id+"F0.wireOp",EDGE,"E749"),sQuery(id+"F0.wireOp",EDGE,"E750"),sQuery(id+"F0.wireOp",EDGE,"E751"),sQuery(id+"F0.wireOp",EDGE,"E752"),sQuery(id+"F0.wireOp",EDGE,"E753"),sQuery(id+"F0.wireOp",EDGE,"E754"),sQuery(id+"F0.wireOp",EDGE,"E755"),sQuery(id+"F0.wireOp",EDGE,"E756"),sQuery(id+"F0.wireOp",EDGE,"E757"),sQuery(id+"F0.wireOp",EDGE,"E758"),sQuery(id+"F0.wireOp",EDGE,"E759"),sQuery(id+"F0.wireOp",EDGE,"E760"),sQuery(id+"F0.wireOp",EDGE,"E761"),sQuery(id+"F0.wireOp",EDGE,"E762"),sQuery(id+"F0.wireOp",EDGE,"E763"),sQuery(id+"F0.wireOp",EDGE,"E764"),sQuery(id+"F0.wireOp",EDGE,"E765"),sQuery(id+"F0.wireOp",EDGE,"E766"),sQuery(id+"F0.wireOp",EDGE,"E767"),sQuery(id+"F0.wireOp",EDGE,"E768"),sQuery(id+"F0.wireOp",EDGE,"E769"),sQuery(id+"F0.wireOp",EDGE,"E770"),sQuery(id+"F0.wireOp",EDGE,"E771"),sQuery(id+"F0.wireOp",EDGE,"E772"),sQuery(id+"F0.wireOp",EDGE,"E773"),sQuery(id+"F0.wireOp",EDGE,"E774"),sQuery(id+"F0.wireOp",EDGE,"E775"),sQuery(id+"F0.wireOp",EDGE,"E776"),sQuery(id+"F0.wireOp",EDGE,"E777"),sQuery(id+"F0.wireOp",EDGE,"E778"),sQuery(id+"F0.wireOp",EDGE,"E779"),sQuery(id+"F0.wireOp",EDGE,"E780"),sQuery(id+"F0.wireOp",EDGE,"E781"),sQuery(id+"F0.wireOp",EDGE,"E782"),sQuery(id+"F0.wireOp",EDGE,"E783"),sQuery(id+"F0.wireOp",EDGE,"E784"),sQuery(id+"F0.wireOp",EDGE,"E785"),sQuery(id+"F0.wireOp",EDGE,"E786"),sQuery(id+"F0.wireOp",EDGE,"E787"),sQuery(id+"F0.wireOp",EDGE,"E788"),sQuery(id+"F0.wireOp",EDGE,"E789"),sQuery(id+"F0.wireOp",EDGE,"E790"),sQuery(id+"F0.wireOp",EDGE,"E791"),sQuery(id+"F0.wireOp",EDGE,"E792"),sQuery(id+"F0.wireOp",EDGE,"E793"),sQuery(id+"F0.wireOp",EDGE,"E794"),sQuery(id+"F0.wireOp",EDGE,"E795"),sQuery(id+"F0.wireOp",EDGE,"E796"),sQuery(id+"F0.wireOp",EDGE,"E797"),sQuery(id+"F0.wireOp",EDGE,"E798"),sQuery(id+"F0.wireOp",EDGE,"E799"),sQuery(id+"F0.wireOp",EDGE,"E800"),sQuery(id+"F0.wireOp",EDGE,"E801"),sQuery(id+"F0.wireOp",EDGE,"E802"),sQuery(id+"F0.wireOp",EDGE,"E803"),sQuery(id+"F0.wireOp",EDGE,"E804"),sQuery(id+"F0.wireOp",EDGE,"E805"),sQuery(id+"F0.wireOp",EDGE,"E806"),sQuery(id+"F0.wireOp",EDGE,"E807"),sQuery(id+"F0.wireOp",EDGE,"E808"),sQuery(id+"F0.wireOp",EDGE,"E809"),sQuery(id+"F0.wireOp",EDGE,"E810"),sQuery(id+"F0.wireOp",EDGE,"E811"),sQuery(id+"F0.wireOp",EDGE,"E812"),sQuery(id+"F0.wireOp",EDGE,"E813"),sQuery(id+"F0.wireOp",EDGE,"E814"),sQuery(id+"F0.wireOp",EDGE,"E815"),sQuery(id+"F0.wireOp",EDGE,"E816"),sQuery(id+"F0.wireOp",EDGE,"E817"),sQuery(id+"F0.wireOp",EDGE,"E818"),sQuery(id+"F0.wireOp",EDGE,"E819"),sQuery(id+"F0.wireOp",EDGE,"E820"),sQuery(id+"F0.wireOp",EDGE,"E821"),sQuery(id+"F0.wireOp",EDGE,"E822"),sQuery(id+"F0.wireOp",EDGE,"E823"),sQuery(id+"F0.wireOp",EDGE,"E824"),sQuery(id+"F0.wireOp",EDGE,"E825"),sQuery(id+"F0.wireOp",EDGE,"E826"),sQuery(id+"F0.wireOp",EDGE,"E827"),sQuery(id+"F0.wireOp",EDGE,"E828"),sQuery(id+"F0.wireOp",EDGE,"E829"),sQuery(id+"F0.wireOp",EDGE,"E830"),sQuery(id+"F0.wireOp",EDGE,"E831"),sQuery(id+"F0.wireOp",EDGE,"E832"),sQuery(id+"F0.wireOp",EDGE,"E833"),sQuery(id+"F0.wireOp",EDGE,"E834"),sQuery(id+"F0.wireOp",EDGE,"E835"),sQuery(id+"F0.wireOp",EDGE,"E836"),sQuery(id+"F0.wireOp",EDGE,"E837"),sQuery(id+"F0.wireOp",EDGE,"E838"),sQuery(id+"F0.wireOp",EDGE,"E839"),sQuery(id+"F0.wireOp",EDGE,"E840"),sQuery(id+"F0.wireOp",EDGE,"E841"),sQuery(id+"F0.wireOp",EDGE,"E842"),sQuery(id+"F0.wireOp",EDGE,"E843"),sQuery(id+"F0.wireOp",EDGE,"E844"),sQuery(id+"F0.wireOp",EDGE,"E845"),sQuery(id+"F0.wireOp",EDGE,"E846"),sQuery(id+"F0.wireOp",EDGE,"E847"),sQuery(id+"F0.wireOp",EDGE,"E848"),sQuery(id+"F0.wireOp",EDGE,"E849"),sQuery(id+"F0.wireOp",EDGE,"E850"),sQuery(id+"F0.wireOp",EDGE,"E851"),sQuery(id+"F0.wireOp",EDGE,"E852"),sQuery(id+"F0.wireOp",EDGE,"E853"),sQuery(id+"F0.wireOp",EDGE,"E854"),sQuery(id+"F0.wireOp",EDGE,"E855"),sQuery(id+"F0.wireOp",EDGE,"E856"),sQuery(id+"F0.wireOp",EDGE,"E857"),sQuery(id+"F0.wireOp",EDGE,"E858"),sQuery(id+"F0.wireOp",EDGE,"E859"),sQuery(id+"F0.wireOp",EDGE,"E860"),sQuery(id+"F0.wireOp",EDGE,"E861"),sQuery(id+"F0.wireOp",EDGE,"E862"),sQuery(id+"F0.wireOp",EDGE,"E863"),sQuery(id+"F0.wireOp",EDGE,"E864"),sQuery(id+"F0.wireOp",EDGE,"E865"),sQuery(id+"F0.wireOp",EDGE,"E866"),sQuery(id+"F0.wireOp",EDGE,"E867"),sQuery(id+"F0.wireOp",EDGE,"E868"),sQuery(id+"F0.wireOp",EDGE,"E869"),sQuery(id+"F0.wireOp",EDGE,"E870"),sQuery(id+"F0.wireOp",EDGE,"E871"),sQuery(id+"F0.wireOp",EDGE,"E872"),sQuery(id+"F0.wireOp",EDGE,"E873"),sQuery(id+"F0.wireOp",EDGE,"E874"),sQuery(id+"F0.wireOp",EDGE,"E875"),sQuery(id+"F0.wireOp",EDGE,"E876"),sQuery(id+"F0.wireOp",EDGE,"E877"),sQuery(id+"F0.wireOp",EDGE,"E878"),sQuery(id+"F0.wireOp",EDGE,"E879"),sQuery(id+"F0.wireOp",EDGE,"E880"),sQuery(id+"F0.wireOp",EDGE,"E881"),sQuery(id+"F0.wireOp",EDGE,"E882"),sQuery(id+"F0.wireOp",EDGE,"E883"),sQuery(id+"F0.wireOp",EDGE,"E884"),sQuery(id+"F0.wireOp",EDGE,"E885"),sQuery(id+"F0.wireOp",EDGE,"E886"),sQuery(id+"F0.wireOp",EDGE,"E887"),sQuery(id+"F0.wireOp",EDGE,"E888"),sQuery(id+"F0.wireOp",EDGE,"E889"),sQuery(id+"F0.wireOp",EDGE,"E890"),sQuery(id+"F0.wireOp",EDGE,"E891"),sQuery(id+"F0.wireOp",EDGE,"E892"),sQuery(id+"F0.wireOp",EDGE,"E893"),sQuery(id+"F0.wireOp",EDGE,"E894"),sQuery(id+"F0.wireOp",EDGE,"E895"),sQuery(id+"F0.wireOp",EDGE,"E896"),sQuery(id+"F0.wireOp",EDGE,"E897"),sQuery(id+"F0.wireOp",EDGE,"E898"),sQuery(id+"F0.wireOp",EDGE,"E899"),sQuery(id+"F0.wireOp",EDGE,"E900"),sQuery(id+"F0.wireOp",EDGE,"E901"),sQuery(id+"F0.wireOp",EDGE,"E902"),sQuery(id+"F0.wireOp",EDGE,"E903"),sQuery(id+"F0.wireOp",EDGE,"E904"),sQuery(id+"F0.wireOp",EDGE,"E905"),sQuery(id+"F0.wireOp",EDGE,"E906"),sQuery(id+"F0.wireOp",EDGE,"E907"),sQuery(id+"F0.wireOp",EDGE,"E908"),sQuery(id+"F0.wireOp",EDGE,"E909"),sQuery(id+"F0.wireOp",EDGE,"E910"),sQuery(id+"F0.wireOp",EDGE,"E911"),sQuery(id+"F0.wireOp",EDGE,"E912"),sQuery(id+"F0.wireOp",EDGE,"E913"),sQuery(id+"F0.wireOp",EDGE,"E914"),sQuery(id+"F0.wireOp",EDGE,"E915"),sQuery(id+"F0.wireOp",EDGE,"E916"),sQuery(id+"F0.wireOp",EDGE,"E917"),sQuery(id+"F0.wireOp",EDGE,"E918"),sQuery(id+"F0.wireOp",EDGE,"E919"),sQuery(id+"F0.wireOp",EDGE,"E920"),sQuery(id+"F0.wireOp",EDGE,"E921"),sQuery(id+"F0.wireOp",EDGE,"E922"),sQuery(id+"F0.wireOp",EDGE,"E923"),sQuery(id+"F0.wireOp",EDGE,"E924"),sQuery(id+"F0.wireOp",EDGE,"E925"),sQuery(id+"F0.wireOp",EDGE,"E926"),sQuery(id+"F0.wireOp",EDGE,"E927"),sQuery(id+"F0.wireOp",EDGE,"E928"),sQuery(id+"F0.wireOp",EDGE,"E929"),sQuery(id+"F0.wireOp",EDGE,"E930"),sQuery(id+"F0.wireOp",EDGE,"E931"),sQuery(id+"F0.wireOp",EDGE,"E932"),sQuery(id+"F0.wireOp",EDGE,"E933"),sQuery(id+"F0.wireOp",EDGE,"E934"),sQuery(id+"F0.wireOp",EDGE,"E935"),sQuery(id+"F0.wireOp",EDGE,"E936"),sQuery(id+"F0.wireOp",EDGE,"E937"),sQuery(id+"F0.wireOp",EDGE,"E938"),sQuery(id+"F0.wireOp",EDGE,"E939"),sQuery(id+"F0.wireOp",EDGE,"E940"),sQuery(id+"F0.wireOp",EDGE,"E941"),sQuery(id+"F0.wireOp",EDGE,"E942"),sQuery(id+"F0.wireOp",EDGE,"E943"),sQuery(id+"F0.wireOp",EDGE,"E944"),sQuery(id+"F0.wireOp",EDGE,"E945"),sQuery(id+"F0.wireOp",EDGE,"E946"),sQuery(id+"F0.wireOp",EDGE,"E947"),sQuery(id+"F0.wireOp",EDGE,"E948"),sQuery(id+"F0.wireOp",EDGE,"E949"),sQuery(id+"F0.wireOp",EDGE,"E950"),sQuery(id+"F0.wireOp",EDGE,"E951"),sQuery(id+"F0.wireOp",EDGE,"E952"),sQuery(id+"F0.wireOp",EDGE,"E953"),sQuery(id+"F0.wireOp",EDGE,"E954"),sQuery(id+"F0.wireOp",EDGE,"E955"),sQuery(id+"F0.wireOp",EDGE,"E956"),sQuery(id+"F0.wireOp",EDGE,"E957"),sQuery(id+"F0.wireOp",EDGE,"E958"),sQuery(id+"F0.wireOp",EDGE,"E959"),sQuery(id+"F0.wireOp",EDGE,"E960"),sQuery(id+"F0.wireOp",EDGE,"E961"),sQuery(id+"F0.wireOp",EDGE,"E962"),sQuery(id+"F0.wireOp",EDGE,"E963"),sQuery(id+"F0.wireOp",EDGE,"E964"),sQuery(id+"F0.wireOp",EDGE,"E965"),sQuery(id+"F0.wireOp",EDGE,"E966"),sQuery(id+"F0.wireOp",EDGE,"E967"),sQuery(id+"F0.wireOp",EDGE,"E968"),sQuery(id+"F0.wireOp",EDGE,"E969"),sQuery(id+"F0.wireOp",EDGE,"E970"),sQuery(id+"F0.wireOp",EDGE,"E971"),sQuery(id+"F0.wireOp",EDGE,"E972"),sQuery(id+"F0.wireOp",EDGE,"E973"),sQuery(id+"F0.wireOp",EDGE,"E974"),sQuery(id+"F0.wireOp",EDGE,"E975"),sQuery(id+"F0.wireOp",EDGE,"E976"),sQuery(id+"F0.wireOp",EDGE,"E977"),sQuery(id+"F0.wireOp",EDGE,"E978"),sQuery(id+"F0.wireOp",EDGE,"E979"),sQuery(id+"F0.wireOp",EDGE,"E980"),sQuery(id+"F0.wireOp",EDGE,"E981"),sQuery(id+"F0.wireOp",EDGE,"E982"),sQuery(id+"F0.wireOp",EDGE,"E983"),sQuery(id+"F0.wireOp",EDGE,"E984"),sQuery(id+"F0.wireOp",EDGE,"E985"),sQuery(id+"F0.wireOp",EDGE,"E986"),sQuery(id+"F0.wireOp",EDGE,"E987"),sQuery(id+"F0.wireOp",EDGE,"E988"),sQuery(id+"F0.wireOp",EDGE,"E989"),sQuery(id+"F0.wireOp",EDGE,"E990"),sQuery(id+"F0.wireOp",EDGE,"E991"),sQuery(id+"F0.wireOp",EDGE,"E992"),sQuery(id+"F0.wireOp",EDGE,"E993"),sQuery(id+"F0.wireOp",EDGE,"E994"),sQuery(id+"F0.wireOp",EDGE,"E995"),sQuery(id+"F0.wireOp",EDGE,"E996"),sQuery(id+"F0.wireOp",EDGE,"E997"),sQuery(id+"F0.wireOp",EDGE,"E998"),sQuery(id+"F0.wireOp",EDGE,"E999"),sQuery(id+"F0.wireOp",EDGE,"E1000"),sQuery(id+"F0.wireOp",EDGE,"E1001"),sQuery(id+"F0.wireOp",EDGE,"E1002"),sQuery(id+"F0.wireOp",EDGE,"E1003"),sQuery(id+"F0.wireOp",EDGE,"E1004"),sQuery(id+"F0.wireOp",EDGE,"E1005"),sQuery(id+"F0.wireOp",EDGE,"E1006"),sQuery(id+"F0.wireOp",EDGE,"E1007"),sQuery(id+"F0.wireOp",EDGE,"E1008"),sQuery(id+"F0.wireOp",EDGE,"E1009"),sQuery(id+"F0.wireOp",EDGE,"E1010"),sQuery(id+"F0.wireOp",EDGE,"E1011"),sQuery(id+"F0.wireOp",EDGE,"E1012"),sQuery(id+"F0.wireOp",EDGE,"E1013"),sQuery(id+"F0.wireOp",EDGE,"E1014"),sQuery(id+"F0.wireOp",EDGE,"E1015"),sQuery(id+"F0.wireOp",EDGE,"E1016"),sQuery(id+"F0.wireOp",EDGE,"E1017"),sQuery(id+"F0.wireOp",EDGE,"E1018"),sQuery(id+"F0.wireOp",EDGE,"E1019"),sQuery(id+"F0.wireOp",EDGE,"E1020"),sQuery(id+"F0.wireOp",EDGE,"E1021"),sQuery(id+"F0.wireOp",EDGE,"E1022"),sQuery(id+"F0.wireOp",EDGE,"E1023"),sQuery(id+"F0.wireOp",EDGE,"E1024"),sQuery(id+"F0.wireOp",EDGE,"E1025"),sQuery(id+"F0.wireOp",EDGE,"E1026"),sQuery(id+"F0.wireOp",EDGE,"E1027"),sQuery(id+"F0.wireOp",EDGE,"E1028"),sQuery(id+"F0.wireOp",EDGE,"E1029"),sQuery(id+"F0.wireOp",EDGE,"E1030"),sQuery(id+"F0.wireOp",EDGE,"E1031"),sQuery(id+"F0.wireOp",EDGE,"E1032"),sQuery(id+"F0.wireOp",EDGE,"E1033"),sQuery(id+"F0.wireOp",EDGE,"E1034"),sQuery(id+"F0.wireOp",EDGE,"E1035"),sQuery(id+"F0.wireOp",EDGE,"E1036"),sQuery(id+"F0.wireOp",EDGE,"E1037"),sQuery(id+"F0.wireOp",EDGE,"E1038"),sQuery(id+"F0.wireOp",EDGE,"E1039"),sQuery(id+"F0.wireOp",EDGE,"E1040"),sQuery(id+"F0.wireOp",EDGE,"E1041"),sQuery(id+"F0.wireOp",EDGE,"E1042"),sQuery(id+"F0.wireOp",EDGE,"E1043"),sQuery(id+"F0.wireOp",EDGE,"E1044"),sQuery(id+"F0.wireOp",EDGE,"E1045"),sQuery(id+"F0.wireOp",EDGE,"E1046"),sQuery(id+"F0.wireOp",EDGE,"E1047"),sQuery(id+"F0.wireOp",EDGE,"E1048"),sQuery(id+"F0.wireOp",EDGE,"E1049"),sQuery(id+"F0.wireOp",EDGE,"E1050"),sQuery(id+"F0.wireOp",EDGE,"E1051"),sQuery(id+"F0.wireOp",EDGE,"E1052"),sQuery(id+"F0.wireOp",EDGE,"E1053"),sQuery(id+"F0.wireOp",EDGE,"E1054"),sQuery(id+"F0.wireOp",EDGE,"E1055"),sQuery(id+"F0.wireOp",EDGE,"E1056"),sQuery(id+"F0.wireOp",EDGE,"E1057"),sQuery(id+"F0.wireOp",EDGE,"E1058"),sQuery(id+"F0.wireOp",EDGE,"E1059"),sQuery(id+"F0.wireOp",EDGE,"E1060"),sQuery(id+"F0.wireOp",EDGE,"E1061"),sQuery(id+"F0.wireOp",EDGE,"E1062"),sQuery(id+"F0.wireOp",EDGE,"E1063"),sQuery(id+"F0.wireOp",EDGE,"E1064"),sQuery(id+"F0.wireOp",EDGE,"E1065"),sQuery(id+"F0.wireOp",EDGE,"E1066"),sQuery(id+"F0.wireOp",EDGE,"E1067"),sQuery(id+"F0.wireOp",EDGE,"E1068"),sQuery(id+"F0.wireOp",EDGE,"E1069"),sQuery(id+"F0.wireOp",EDGE,"E1070"),sQuery(id+"F0.wireOp",EDGE,"E1071"),sQuery(id+"F0.wireOp",EDGE,"E1072"),sQuery(id+"F0.wireOp",EDGE,"E1073"),sQuery(id+"F0.wireOp",EDGE,"E1074"),sQuery(id+"F0.wireOp",EDGE,"E1075"),sQuery(id+"F0.wireOp",EDGE,"E1076"),sQuery(id+"F0.wireOp",EDGE,"E1077"),sQuery(id+"F0.wireOp",EDGE,"E1078"),sQuery(id+"F0.wireOp",EDGE,"E1079"),sQuery(id+"F0.wireOp",EDGE,"E1080"),sQuery(id+"F0.wireOp",EDGE,"E1081"),sQuery(id+"F0.wireOp",EDGE,"E1082"),sQuery(id+"F0.wireOp",EDGE,"E1083"),sQuery(id+"F0.wireOp",EDGE,"E1084"),sQuery(id+"F0.wireOp",EDGE,"E1085"),sQuery(id+"F0.wireOp",EDGE,"E1086"),sQuery(id+"F0.wireOp",EDGE,"E1087"),sQuery(id+"F0.wireOp",EDGE,"E1088"),sQuery(id+"F0.wireOp",EDGE,"E1089"),sQuery(id+"F0.wireOp",EDGE,"E1090"),sQuery(id+"F0.wireOp",EDGE,"E1091"),sQuery(id+"F0.wireOp",EDGE,"E1092"),sQuery(id+"F0.wireOp",EDGE,"E1093"),sQuery(id+"F0.wireOp",EDGE,"E1094"),sQuery(id+"F0.wireOp",EDGE,"E1095"),sQuery(id+"F0.wireOp",EDGE,"E1096"),sQuery(id+"F0.wireOp",EDGE,"E1097"),sQuery(id+"F0.wireOp",EDGE,"E1098"),sQuery(id+"F0.wireOp",EDGE,"E1099"),sQuery(id+"F0.wireOp",EDGE,"E1100"),sQuery(id+"F0.wireOp",EDGE,"E1101"),sQuery(id+"F0.wireOp",EDGE,"E1102"),sQuery(id+"F0.wireOp",EDGE,"E1103"),sQuery(id+"F0.wireOp",EDGE,"E1104"),sQuery(id+"F0.wireOp",EDGE,"E1105"),sQuery(id+"F0.wireOp",EDGE,"E1106"),sQuery(id+"F0.wireOp",EDGE,"E1107"),sQuery(id+"F0.wireOp",EDGE,"E1108"),sQuery(id+"F0.wireOp",EDGE,"E1109"),sQuery(id+"F0.wireOp",EDGE,"E1110"),sQuery(id+"F0.wireOp",EDGE,"E1111"),sQuery(id+"F0.wireOp",EDGE,"E1112"),sQuery(id+"F0.wireOp",EDGE,"E1113"),sQuery(id+"F0.wireOp",EDGE,"E1114"),sQuery(id+"F0.wireOp",EDGE,"E1115"),sQuery(id+"F0.wireOp",EDGE,"E1116"),sQuery(id+"F0.wireOp",EDGE,"E1117"),sQuery(id+"F0.wireOp",EDGE,"E1118"),sQuery(id+"F0.wireOp",EDGE,"E1119"),sQuery(id+"F0.wireOp",EDGE,"E1120"),sQuery(id+"F0.wireOp",EDGE,"E1121"),sQuery(id+"F0.wireOp",EDGE,"E1122"),sQuery(id+"F0.wireOp",EDGE,"E1123"),sQuery(id+"F0.wireOp",EDGE,"E1124"),sQuery(id+"F0.wireOp",EDGE,"E1125"),sQuery(id+"F0.wireOp",EDGE,"E1126"),sQuery(id+"F0.wireOp",EDGE,"E1127"),sQuery(id+"F0.wireOp",EDGE,"E1128"),sQuery(id+"F0.wireOp",EDGE,"E1129"),sQuery(id+"F0.wireOp",EDGE,"E1130"),sQuery(id+"F0.wireOp",EDGE,"E1131"),sQuery(id+"F0.wireOp",EDGE,"E1132"),sQuery(id+"F0.wireOp",EDGE,"E1133"),sQuery(id+"F0.wireOp",EDGE,"E1134"),sQuery(id+"F0.wireOp",EDGE,"E1135"),sQuery(id+"F0.wireOp",EDGE,"E1136"),sQuery(id+"F0.wireOp",EDGE,"E1137"),sQuery(id+"F0.wireOp",EDGE,"E1138"),sQuery(id+"F0.wireOp",EDGE,"E1139"),sQuery(id+"F0.wireOp",EDGE,"E1140"),sQuery(id+"F0.wireOp",EDGE,"E1141"),sQuery(id+"F0.wireOp",EDGE,"E1142"),sQuery(id+"F0.wireOp",EDGE,"E1143"),sQuery(id+"F0.wireOp",EDGE,"E1144"),sQuery(id+"F0.wireOp",EDGE,"E1145"),sQuery(id+"F0.wireOp",EDGE,"E1146"),sQuery(id+"F0.wireOp",EDGE,"E1147"),sQuery(id+"F0.wireOp",EDGE,"E1148"),sQuery(id+"F0.wireOp",EDGE,"E1149"),sQuery(id+"F0.wireOp",EDGE,"E1150"),sQuery(id+"F0.wireOp",EDGE,"E1151"),sQuery(id+"F0.wireOp",EDGE,"E1152"),sQuery(id+"F0.wireOp",EDGE,"E1153"),sQuery(id+"F0.wireOp",EDGE,"E1154"),sQuery(id+"F0.wireOp",EDGE,"E1155"),sQuery(id+"F0.wireOp",EDGE,"E1156"),sQuery(id+"F0.wireOp",EDGE,"E1157"),sQuery(id+"F0.wireOp",EDGE,"E1158"),sQuery(id+"F0.wireOp",EDGE,"E1159"),sQuery(id+"F0.wireOp",EDGE,"E1160"),sQuery(id+"F0.wireOp",EDGE,"E1161"),sQuery(id+"F0.wireOp",EDGE,"E1162"),sQuery(id+"F0.wireOp",EDGE,"E1163"),sQuery(id+"F0.wireOp",EDGE,"E1164"),sQuery(id+"F0.wireOp",EDGE,"E1165"),sQuery(id+"F0.wireOp",EDGE,"E1166"),sQuery(id+"F0.wireOp",EDGE,"E1167"),sQuery(id+"F0.wireOp",EDGE,"E1168"),sQuery(id+"F0.wireOp",EDGE,"E1169"),sQuery(id+"F0.wireOp",EDGE,"E1170"),sQuery(id+"F0.wireOp",EDGE,"E1171"),sQuery(id+"F0.wireOp",EDGE,"E1172"),sQuery(id+"F0.wireOp",EDGE,"E1173"),sQuery(id+"F0.wireOp",EDGE,"E1174"),sQuery(id+"F0.wireOp",EDGE,"E1175"),sQuery(id+"F0.wireOp",EDGE,"E1176"),sQuery(id+"F0.wireOp",EDGE,"E1177"),sQuery(id+"F0.wireOp",EDGE,"E1178"),sQuery(id+"F0.wireOp",EDGE,"E1179"),sQuery(id+"F0.wireOp",EDGE,"E1180"),sQuery(id+"F0.wireOp",EDGE,"E1181"),sQuery(id+"F0.wireOp",EDGE,"E1182"),sQuery(id+"F0.wireOp",EDGE,"E1183"),sQuery(id+"F0.wireOp",EDGE,"E1184"),sQuery(id+"F0.wireOp",EDGE,"E1185"),sQuery(id+"F0.wireOp",EDGE,"E1186"),sQuery(id+"F0.wireOp",EDGE,"E1187"),sQuery(id+"F0.wireOp",EDGE,"E1188"),sQuery(id+"F0.wireOp",EDGE,"E1189"),sQuery(id+"F0.wireOp",EDGE,"E1190"),sQuery(id+"F0.wireOp",EDGE,"E1191"),sQuery(id+"F0.wireOp",EDGE,"E1192"),sQuery(id+"F0.wireOp",EDGE,"E1193"),sQuery(id+"F0.wireOp",EDGE,"E1194"),sQuery(id+"F0.wireOp",EDGE,"E1195"),sQuery(id+"F0.wireOp",EDGE,"E1196"),sQuery(id+"F0.wireOp",EDGE,"E1197"),sQuery(id+"F0.wireOp",EDGE,"E1198"),sQuery(id+"F0.wireOp",EDGE,"E1199"),sQuery(id+"F0.wireOp",EDGE,"E1200"),sQuery(id+"F0.wireOp",EDGE,"E1201"),sQuery(id+"F0.wireOp",EDGE,"E1202"),sQuery(id+"F0.wireOp",EDGE,"E1203"),sQuery(id+"F0.wireOp",EDGE,"E1204"),sQuery(id+"F0.wireOp",EDGE,"E1205"),sQuery(id+"F0.wireOp",EDGE,"E1206"),sQuery(id+"F0.wireOp",EDGE,"E1207"),sQuery(id+"F0.wireOp",EDGE,"E1208"),sQuery(id+"F0.wireOp",EDGE,"E1209"),sQuery(id+"F0.wireOp",EDGE,"E1210"),sQuery(id+"F0.wireOp",EDGE,"E1211"),sQuery(id+"F0.wireOp",EDGE,"E1212"),sQuery(id+"F0.wireOp",EDGE,"E1213"),sQuery(id+"F0.wireOp",EDGE,"E1214"),sQuery(id+"F0.wireOp",EDGE,"E1215"),sQuery(id+"F0.wireOp",EDGE,"E1216"),sQuery(id+"F0.wireOp",EDGE,"E1217"),sQuery(id+"F0.wireOp",EDGE,"E1218"),sQuery(id+"F0.wireOp",EDGE,"E1219"),sQuery(id+"F0.wireOp",EDGE,"E1220"),sQuery(id+"F0.wireOp",EDGE,"E1221"),sQuery(id+"F0.wireOp",EDGE,"E1222"),sQuery(id+"F0.wireOp",EDGE,"E1223"),sQuery(id+"F0.wireOp",EDGE,"E1224"),sQuery(id+"F0.wireOp",EDGE,"E1225"),sQuery(id+"F0.wireOp",EDGE,"E1226"),sQuery(id+"F0.wireOp",EDGE,"E1227"),sQuery(id+"F0.wireOp",EDGE,"E1228"),sQuery(id+"F0.wireOp",EDGE,"E1229"),sQuery(id+"F0.wireOp",EDGE,"E1230"),sQuery(id+"F0.wireOp",EDGE,"E1231"),sQuery(id+"F0.wireOp",EDGE,"E1232"),sQuery(id+"F0.wireOp",EDGE,"E1233"),sQuery(id+"F0.wireOp",EDGE,"E1234"),sQuery(id+"F0.wireOp",EDGE,"E1235"),sQuery(id+"F0.wireOp",EDGE,"E1236"),sQuery(id+"F0.wireOp",EDGE,"E1237"),sQuery(id+"F0.wireOp",EDGE,"E1238"),sQuery(id+"F0.wireOp",EDGE,"E1239"),sQuery(id+"F0.wireOp",EDGE,"E1240"),sQuery(id+"F0.wireOp",EDGE,"E1241"),sQuery(id+"F0.wireOp",EDGE,"E1242"),sQuery(id+"F0.wireOp",EDGE,"E1243"),sQuery(id+"F0.wireOp",EDGE,"E1244"),sQuery(id+"F0.wireOp",EDGE,"E1245"),sQuery(id+"F0.wireOp",EDGE,"E1246"),sQuery(id+"F0.wireOp",EDGE,"E1247"),sQuery(id+"F0.wireOp",EDGE,"E1248"),sQuery(id+"F0.wireOp",EDGE,"E1249"),sQuery(id+"F0.wireOp",EDGE,"E1250"),sQuery(id+"F0.wireOp",EDGE,"E1251"),sQuery(id+"F0.wireOp",EDGE,"E1252"),sQuery(id+"F0.wireOp",EDGE,"E1253"),sQuery(id+"F0.wireOp",EDGE,"E1254"),sQuery(id+"F0.wireOp",EDGE,"E1255"),sQuery(id+"F0.wireOp",EDGE,"E1256"),sQuery(id+"F0.wireOp",EDGE,"E1257"),sQuery(id+"F0.wireOp",EDGE,"E1258"),sQuery(id+"F0.wireOp",EDGE,"E1259"),sQuery(id+"F0.wireOp",EDGE,"E1260"),sQuery(id+"F0.wireOp",EDGE,"E1261"),sQuery(id+"F0.wireOp",EDGE,"E1262"),sQuery(id+"F0.wireOp",EDGE,"E1263"),sQuery(id+"F0.wireOp",EDGE,"E1264"),sQuery(id+"F0.wireOp",EDGE,"E1265"),sQuery(id+"F0.wireOp",EDGE,"E1266"),sQuery(id+"F0.wireOp",EDGE,"E1267"),sQuery(id+"F0.wireOp",EDGE,"E1268"),sQuery(id+"F0.wireOp",EDGE,"E1269"),sQuery(id+"F0.wireOp",EDGE,"E1270"),sQuery(id+"F0.wireOp",EDGE,"E1271"),sQuery(id+"F0.wireOp",EDGE,"E1272"),sQuery(id+"F0.wireOp",EDGE,"E1273"),sQuery(id+"F0.wireOp",EDGE,"E1274"),sQuery(id+"F0.wireOp",EDGE,"E1275"),sQuery(id+"F0.wireOp",EDGE,"E1276"),sQuery(id+"F0.wireOp",EDGE,"E1277"),sQuery(id+"F0.wireOp",EDGE,"E1278"),sQuery(id+"F0.wireOp",EDGE,"E1279"),sQuery(id+"F0.wireOp",EDGE,"E1280"),sQuery(id+"F0.wireOp",EDGE,"E1281"),sQuery(id+"F0.wireOp",EDGE,"E1282"),sQuery(id+"F0.wireOp",EDGE,"E1283"),sQuery(id+"F0.wireOp",EDGE,"E1284"),sQuery(id+"F0.wireOp",EDGE,"E1285"),sQuery(id+"F0.wireOp",EDGE,"E1286"),sQuery(id+"F0.wireOp",EDGE,"E1287"),sQuery(id+"F0.wireOp",EDGE,"E1288"),sQuery(id+"F0.wireOp",EDGE,"E1289"),sQuery(id+"F0.wireOp",EDGE,"E1290"),sQuery(id+"F0.wireOp",EDGE,"E1291"),sQuery(id+"F0.wireOp",EDGE,"E1292"),sQuery(id+"F0.wireOp",EDGE,"E1293"),sQuery(id+"F0.wireOp",EDGE,"E1294"),sQuery(id+"F0.wireOp",EDGE,"E1295"),sQuery(id+"F0.wireOp",EDGE,"E1296"),sQuery(id+"F0.wireOp",EDGE,"E1297"),sQuery(id+"F0.wireOp",EDGE,"E1298"),sQuery(id+"F0.wireOp",EDGE,"E1299"),sQuery(id+"F0.wireOp",EDGE,"E1300"),sQuery(id+"F0.wireOp",EDGE,"E1301"),sQuery(id+"F0.wireOp",EDGE,"E1302"),sQuery(id+"F0.wireOp",EDGE,"E1303"),sQuery(id+"F0.wireOp",EDGE,"E1304"),sQuery(id+"F0.wireOp",EDGE,"E1305"),sQuery(id+"F0.wireOp",EDGE,"E1306"),sQuery(id+"F0.wireOp",EDGE,"E1307"),sQuery(id+"F0.wireOp",EDGE,"E1308"),sQuery(id+"F0.wireOp",EDGE,"E1309"),sQuery(id+"F0.wireOp",EDGE,"E1310"),sQuery(id+"F0.wireOp",EDGE,"E1311"),sQuery(id+"F0.wireOp",EDGE,"E1312"),sQuery(id+"F0.wireOp",EDGE,"E1313"),sQuery(id+"F0.wireOp",EDGE,"E1314"),sQuery(id+"F0.wireOp",EDGE,"E1315"),sQuery(id+"F0.wireOp",EDGE,"E1316"),sQuery(id+"F0.wireOp",EDGE,"E1317"),sQuery(id+"F0.wireOp",EDGE,"E1318"),sQuery(id+"F0.wireOp",EDGE,"E1319"),sQuery(id+"F0.wireOp",EDGE,"E1320"),sQuery(id+"F0.wireOp",EDGE,"E1321"),sQuery(id+"F0.wireOp",EDGE,"E1322"),sQuery(id+"F0.wireOp",EDGE,"E1323"),sQuery(id+"F0.wireOp",EDGE,"E1324"),sQuery(id+"F0.wireOp",EDGE,"E1325"),sQuery(id+"F0.wireOp",EDGE,"E1326"),sQuery(id+"F0.wireOp",EDGE,"E1327"),sQuery(id+"F0.wireOp",EDGE,"E1328"),sQuery(id+"F0.wireOp",EDGE,"E1329"),sQuery(id+"F0.wireOp",EDGE,"E1330"),sQuery(id+"F0.wireOp",EDGE,"E1331"),sQuery(id+"F0.wireOp",EDGE,"E1332"),sQuery(id+"F0.wireOp",EDGE,"E1333"),sQuery(id+"F0.wireOp",EDGE,"E1334"),sQuery(id+"F0.wireOp",EDGE,"E1335"),sQuery(id+"F0.wireOp",EDGE,"E1336"),sQuery(id+"F0.wireOp",EDGE,"E1337"),sQuery(id+"F0.wireOp",EDGE,"E1338"),sQuery(id+"F0.wireOp",EDGE,"E1339"),sQuery(id+"F0.wireOp",EDGE,"E1340"),sQuery(id+"F0.wireOp",EDGE,"E1341"),sQuery(id+"F0.wireOp",EDGE,"E1342"),sQuery(id+"F0.wireOp",EDGE,"E1343"),sQuery(id+"F0.wireOp",EDGE,"E1344"),sQuery(id+"F0.wireOp",EDGE,"E1345"),sQuery(id+"F0.wireOp",EDGE,"E1346"),sQuery(id+"F0.wireOp",EDGE,"E1347"),sQuery(id+"F0.wireOp",EDGE,"E1348"),sQuery(id+"F0.wireOp",EDGE,"E1349"),sQuery(id+"F0.wireOp",EDGE,"E1350"),sQuery(id+"F0.wireOp",EDGE,"E1351"),sQuery(id+"F0.wireOp",EDGE,"E1352"),sQuery(id+"F0.wireOp",EDGE,"E1353"),sQuery(id+"F0.wireOp",EDGE,"E1354"),sQuery(id+"F0.wireOp",EDGE,"E1355"),sQuery(id+"F0.wireOp",EDGE,"E1356"),sQuery(id+"F0.wireOp",EDGE,"E1357"),sQuery(id+"F0.wireOp",EDGE,"E1358"),sQuery(id+"F0.wireOp",EDGE,"E1359"),sQuery(id+"F0.wireOp",EDGE,"E1360"),sQuery(id+"F0.wireOp",EDGE,"E1361"),sQuery(id+"F0.wireOp",EDGE,"E1362"),sQuery(id+"F0.wireOp",EDGE,"E1363"),sQuery(id+"F0.wireOp",EDGE,"E1364"),sQuery(id+"F0.wireOp",EDGE,"E1365"),sQuery(id+"F0.wireOp",EDGE,"E1366"),sQuery(id+"F0.wireOp",EDGE,"E1367"),sQuery(id+"F0.wireOp",EDGE,"E1368"),sQuery(id+"F0.wireOp",EDGE,"E1369"),sQuery(id+"F0.wireOp",EDGE,"E1370"),sQuery(id+"F0.wireOp",EDGE,"E1371"),sQuery(id+"F0.wireOp",EDGE,"E1372"),sQuery(id+"F0.wireOp",EDGE,"E1373"),sQuery(id+"F0.wireOp",EDGE,"E1374"),sQuery(id+"F0.wireOp",EDGE,"E1375"),sQuery(id+"F0.wireOp",EDGE,"E1376"),sQuery(id+"F0.wireOp",EDGE,"E1377"),sQuery(id+"F0.wireOp",EDGE,"E1378"),sQuery(id+"F0.wireOp",EDGE,"E1379"),sQuery(id+"F0.wireOp",EDGE,"E1380"),sQuery(id+"F0.wireOp",EDGE,"E1381"),sQuery(id+"F0.wireOp",EDGE,"E1382"),sQuery(id+"F0.wireOp",EDGE,"E1383"),sQuery(id+"F0.wireOp",EDGE,"E1384"),sQuery(id+"F0.wireOp",EDGE,"E1385"),sQuery(id+"F0.wireOp",EDGE,"E1386"),sQuery(id+"F0.wireOp",EDGE,"E1387"),sQuery(id+"F0.wireOp",EDGE,"E1388"),sQuery(id+"F0.wireOp",EDGE,"E1389"),sQuery(id+"F0.wireOp",EDGE,"E1390"),sQuery(id+"F0.wireOp",EDGE,"E1391"),sQuery(id+"F0.wireOp",EDGE,"E1392"),sQuery(id+"F0.wireOp",EDGE,"E1393"),sQuery(id+"F0.wireOp",EDGE,"E1394"),sQuery(id+"F0.wireOp",EDGE,"E1395"),sQuery(id+"F0.wireOp",EDGE,"E1396"),sQuery(id+"F0.wireOp",EDGE,"E1397"),sQuery(id+"F0.wireOp",EDGE,"E1398"),sQuery(id+"F0.wireOp",EDGE,"E1399"),sQuery(id+"F0.wireOp",EDGE,"E1400"),sQuery(id+"F0.wireOp",EDGE,"E1401"),sQuery(id+"F0.wireOp",EDGE,"E1402"),sQuery(id+"F0.wireOp",EDGE,"E1403"),sQuery(id+"F0.wireOp",EDGE,"E1404"),sQuery(id+"F0.wireOp",EDGE,"E1405"),sQuery(id+"F0.wireOp",EDGE,"E1406"),sQuery(id+"F0.wireOp",EDGE,"E1407"),sQuery(id+"F0.wireOp",EDGE,"E1408"),sQuery(id+"F0.wireOp",EDGE,"E1409"),sQuery(id+"F0.wireOp",EDGE,"E1410"),sQuery(id+"F0.wireOp",EDGE,"E1411"),sQuery(id+"F0.wireOp",EDGE,"E1412"),sQuery(id+"F0.wireOp",EDGE,"E1413"),sQuery(id+"F0.wireOp",EDGE,"E1414"),sQuery(id+"F0.wireOp",EDGE,"E1415"),sQuery(id+"F0.wireOp",EDGE,"E1416"),sQuery(id+"F0.wireOp",EDGE,"E1417"),sQuery(id+"F0.wireOp",EDGE,"E1418"),sQuery(id+"F0.wireOp",EDGE,"E1419"),sQuery(id+"F0.wireOp",EDGE,"E1420"),sQuery(id+"F0.wireOp",EDGE,"E1421"),sQuery(id+"F0.wireOp",EDGE,"E1422"),sQuery(id+"F0.wireOp",EDGE,"E1423"),sQuery(id+"F0.wireOp",EDGE,"E1424"),sQuery(id+"F0.wireOp",EDGE,"E1425"),sQuery(id+"F0.wireOp",EDGE,"E1426"),sQuery(id+"F0.wireOp",EDGE,"E1427"),sQuery(id+"F0.wireOp",EDGE,"E1428"),sQuery(id+"F0.wireOp",EDGE,"E1429"),sQuery(id+"F0.wireOp",EDGE,"E1430"),sQuery(id+"F0.wireOp",EDGE,"E1431"),sQuery(id+"F0.wireOp",EDGE,"E1432"),sQuery(id+"F0.wireOp",EDGE,"E1433"),sQuery(id+"F0.wireOp",EDGE,"E1434"),sQuery(id+"F0.wireOp",EDGE,"E1435"),sQuery(id+"F0.wireOp",EDGE,"E1436"),sQuery(id+"F0.wireOp",EDGE,"E1437"),sQuery(id+"F0.wireOp",EDGE,"E1438"),sQuery(id+"F0.wireOp",EDGE,"E1439"),sQuery(id+"F0.wireOp",EDGE,"E1440"),sQuery(id+"F0.wireOp",EDGE,"E1441"),sQuery(id+"F0.wireOp",EDGE,"E1442"),sQuery(id+"F0.wireOp",EDGE,"E1443"),sQuery(id+"F0.wireOp",EDGE,"E1444"),sQuery(id+"F0.wireOp",EDGE,"E1445"),sQuery(id+"F0.wireOp",EDGE,"E1446"),sQuery(id+"F0.wireOp",EDGE,"E1447")])],"isStart":true});
            extrude(context, id + "F5", {"entities" : qUnion([Q0]), "operationType" : NewBodyOperationType.REMOVE, "oppositeDirection" : true, "depth" : 4.8 * mm, "offsetDistance" : 25 * mm, "hasDraft" : true, "draftAngle" : 2 * degree, "draftPullDirection" : true});
        }
        {
            var Q0;
            Q0=makeQuery(id+"F5.boolean.opBoolean","COPY",EDGE,{"derivedFrom":makeQuery(id+"F5.opExtrude","SWEPT_EDGE",EDGE,{"disambiguationData":[OSD([sQuery(id+"F0.wireOp",EDGE,"E599"),sQuery(id+"F0.wireOp",EDGE,"E600")])]})});
            var Q1;
            Q1=makeQuery(id+"F5.boolean.opBoolean","COPY",EDGE,{"derivedFrom":makeQuery(id+"F5.opExtrude","SWEPT_EDGE",EDGE,{"disambiguationData":[OSD([sQuery(id+"F0.wireOp",EDGE,"E551"),sQuery(id+"F0.wireOp",EDGE,"E552")])]})});
            fillet(context, id + "F6", {"entities" : qUnion([Q0, Q1]), "radius" : 0.1 * mm, "tangentPropagation" : true, "allowEdgeOverflow" : false});
        }
        {
            var Q0;
            {var subQ0=sQuery(id+"F3.wireOp",EDGE,"E1448.bottom");var subQ1=sQuery(id+"F3.wireOp",EDGE,"E1448.top");var subQ2=sQuery(id+"F3.wireOp",EDGE,"E1448.left");var subQ3=sQuery(id+"F3.wireOp",EDGE,"E1448.right");Q0=makeQuery(id+"F5.boolean.opBoolean","SPLIT",FACE,{"disambiguationData":[TD([makeQuery(id+"F4.opExtrude","SWEPT_FACE",FACE,{"disambiguationData":[OSD([subQ0])]})])],"derivedFrom":makeQuery(id+"F4.opExtrude","CAP_FACE",FACE,{"disambiguationData":[OSD([subQ0,subQ1,subQ2,subQ3])],"isStart":true})});}
            var sketch = newSketch(context, id + "F7", { "sketchPlane" : qUnion([Q0])});
            skLineSegment(sketch, "E1449", {"start": v(-19.8, 8.67) * mm, "end": v(-19.8, -1.55) * mm});
            skLineSegment(sketch, "E1450", {"start": v(-19.8, -1.55) * mm, "end": v(-12.05, -1.55) * mm});
            skLineSegment(sketch, "E1451", {"start": v(-12.05, -1.55) * mm, "end": v(-9.26, -8.38) * mm});
            skLineSegment(sketch, "E1452", {"start": v(-9.26, -8.38) * mm, "end": v(12, -8.38) * mm});
            skLineSegment(sketch, "E1453", {"start": v(12, -8.38) * mm, "end": v(12, -2.15) * mm});
            skLineSegment(sketch, "E1454", {"start": v(12, -2.15) * mm, "end": v(19.98, -2.15) * mm});
            skLineSegment(sketch, "E1455", {"start": v(19.98, -2.15) * mm, "end": v(19.98, 8.67) * mm});
            skLineSegment(sketch, "E1456", {"start": v(19.98, 8.67) * mm, "end": v(-19.8, 8.67) * mm});
            skLineSegment(sketch, "E1457.bottom", {"start": v(-29.96, 15.19) * mm, "end": v(30.87, 15.19) * mm});
            skLineSegment(sketch, "E1457.top", {"start": v(-29.96, -14.71) * mm, "end": v(30.87, -14.71) * mm});
            skLineSegment(sketch, "E1457.left", {"start": v(-29.96, 15.19) * mm, "end": v(-29.96, -14.71) * mm});
            skLineSegment(sketch, "E1457.right", {"start": v(30.87, 15.19) * mm, "end": v(30.87, -14.71) * mm});
            skPoint(sketch, "E1457.middle", {"position": v(0.45, 0.24) * mm});
            skSolve(sketch);
        }
        {
            var Q0;
            Q0 = qSketchRegion(id + "F7", true);
            extrude(context, id + "F8", {"entities" : qUnion([Q0]), "operationType" : NewBodyOperationType.REMOVE, "oppositeDirection" : true, "depth" : 25 * mm, "offsetDistance" : 25 * mm});
        }
        {
            var Q0;
            Q0=makeQuery(id+"F4.opExtrude","CAP_FACE",FACE,{"disambiguationData":[OSD([sQuery(id+"F3.wireOp",EDGE,"E1448.bottom"),sQuery(id+"F3.wireOp",EDGE,"E1448.top"),sQuery(id+"F3.wireOp",EDGE,"E1448.left"),sQuery(id+"F3.wireOp",EDGE,"E1448.right")])],"isStart":false});
            var sketch = newSketch(context, id + "F9", { "sketchPlane" : qUnion([Q0])});
            skLineSegment(sketch, "E1458.bottom", {"start": v(38.76, -13.79) * mm, "end": v(-35.5, -13.79) * mm});
            skLineSegment(sketch, "E1458.top", {"start": v(38.76, 12.26) * mm, "end": v(-35.5, 12.26) * mm});
            skLineSegment(sketch, "E1458.left", {"start": v(38.76, -13.79) * mm, "end": v(38.76, 12.26) * mm});
            skLineSegment(sketch, "E1458.right", {"start": v(-35.5, -13.79) * mm, "end": v(-35.5, 12.26) * mm});
            skPoint(sketch, "E1458.middle", {"position": v(1.63, -0.76) * mm});
            skSolve(sketch);
        }
        {
            var Q0;
            Q0 = qSketchRegion(id + "F9", true);
            extrude(context, id + "F10", {"entities" : qUnion([Q0]), "operationType" : NewBodyOperationType.REMOVE, "oppositeDirection" : true, "depth" : 1 * mm, "offsetDistance" : 25 * mm});
        }
        {
            var Q0;
            Q0=makeQuery(id+"F8.boolean.opBoolean","COPY",EDGE,{"derivedFrom":makeQuery(id+"F8.opExtrude","SWEPT_EDGE",EDGE,{"disambiguationData":[OSD([sQuery(id+"F7.wireOp",EDGE,"E1449"),sQuery(id+"F7.wireOp",EDGE,"E1450")])]})});
            var Q1;
            Q1=makeQuery(id+"F8.boolean.opBoolean","COPY",EDGE,{"derivedFrom":makeQuery(id+"F8.opExtrude","SWEPT_EDGE",EDGE,{"disambiguationData":[OSD([sQuery(id+"F7.wireOp",EDGE,"E1449"),sQuery(id+"F7.wireOp",EDGE,"E1456")])]})});
            var Q2;
            Q2=makeQuery(id+"F8.boolean.opBoolean","COPY",EDGE,{"derivedFrom":makeQuery(id+"F8.opExtrude","SWEPT_EDGE",EDGE,{"disambiguationData":[OSD([sQuery(id+"F7.wireOp",EDGE,"E1454"),sQuery(id+"F7.wireOp",EDGE,"E1455")])]})});
            var Q3;
            Q3=makeQuery(id+"F8.boolean.opBoolean","COPY",EDGE,{"derivedFrom":makeQuery(id+"F8.opExtrude","SWEPT_EDGE",EDGE,{"disambiguationData":[OSD([sQuery(id+"F7.wireOp",EDGE,"E1455"),sQuery(id+"F7.wireOp",EDGE,"E1456")])]})});
            var Q4;
            Q4=makeQuery(id+"F8.boolean.opBoolean","COPY",EDGE,{"derivedFrom":makeQuery(id+"F8.opExtrude","SWEPT_EDGE",EDGE,{"disambiguationData":[OSD([sQuery(id+"F7.wireOp",EDGE,"E1452"),sQuery(id+"F7.wireOp",EDGE,"E1453")])]})});
            var Q5;
            Q5=makeQuery(id+"F8.boolean.opBoolean","COPY",EDGE,{"derivedFrom":makeQuery(id+"F8.opExtrude","SWEPT_EDGE",EDGE,{"disambiguationData":[OSD([sQuery(id+"F7.wireOp",EDGE,"E1453"),sQuery(id+"F7.wireOp",EDGE,"E1454")])]})});
            var Q6;
            Q6=makeQuery(id+"F8.boolean.opBoolean","COPY",EDGE,{"derivedFrom":makeQuery(id+"F8.opExtrude","SWEPT_EDGE",EDGE,{"disambiguationData":[OSD([sQuery(id+"F7.wireOp",EDGE,"E1451"),sQuery(id+"F7.wireOp",EDGE,"E1452")])]})});
            var Q7;
            Q7=makeQuery(id+"F8.boolean.opBoolean","COPY",EDGE,{"derivedFrom":makeQuery(id+"F8.opExtrude","SWEPT_EDGE",EDGE,{"disambiguationData":[OSD([sQuery(id+"F7.wireOp",EDGE,"E1450"),sQuery(id+"F7.wireOp",EDGE,"E1451")])]})});
            fillet(context, id + "F11", {"entities" : qUnion([Q0, Q1, Q2, Q3, Q4, Q5, Q6, Q7]), "radius" : 3 * mm, "tangentPropagation" : true, "allowEdgeOverflow" : false});
        }
    });
